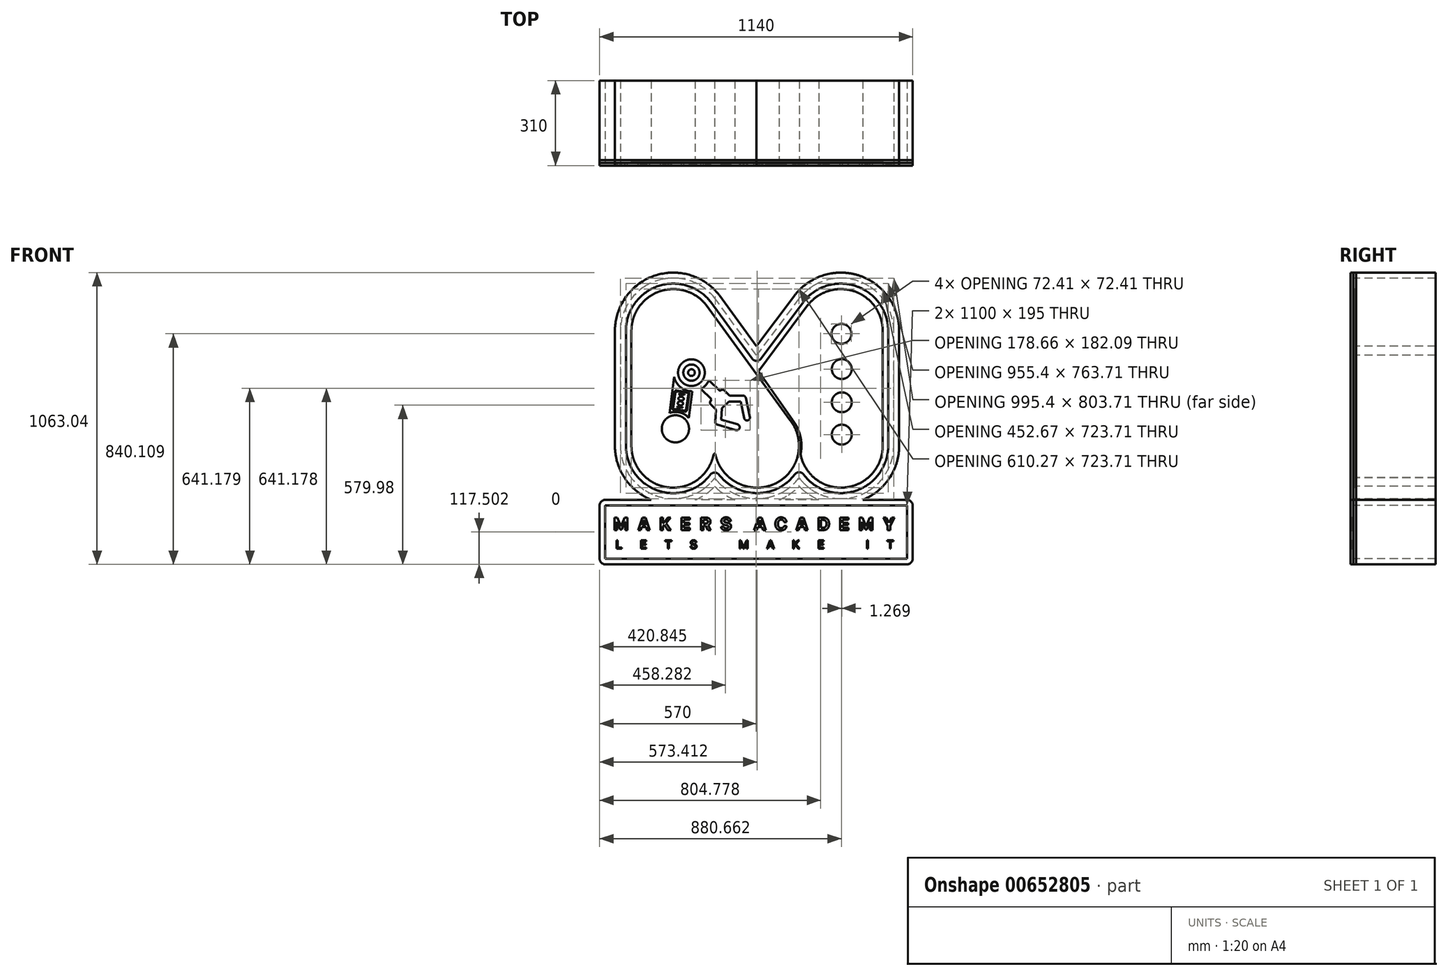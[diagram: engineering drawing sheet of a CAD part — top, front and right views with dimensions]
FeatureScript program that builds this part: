
annotation { "Feature Type Name" : "Feature", "Feature Type Description" : "" }
export const myFeature = defineFeature(function(context is Context, id is Id, definition is map)
    precondition{}
    {
        {
            var Q0;
            Q0=qCreatedBy(makeId("Front.planeOp"),FACE);
            var sketch = newSketch(context, id + "F0", { "sketchPlane" : qUnion([Q0])});
            skLineSegment(sketch, "E0", {"start": v(-550, -511.99) * mm, "end": v(550, -511.99) * mm});
            skLineSegment(sketch, "E1", {"start": v(550, -316.99) * mm, "end": v(-550, -316.99) * mm});
            skLineSegment(sketch, "E2", {"start": v(-550, -316.99) * mm, "end": v(-550, -511.99) * mm});
            skArc(sketch, "E3", {"start": v(-150.98, -217.61) * mm, "mid": v(-142.45, -227.73) * mm, "end": v(-133.24, -237.25) * mm});
            skArc(sketch, "E4", {"start": v(-133.24, -237.25) * mm, "mid": v(-111.33, -255.56) * mm, "end": v(-87, -270.53) * mm});
            skArc(sketch, "E5", {"start": v(-87, -270.53) * mm, "mid": v(-70.2, -278.28) * mm, "end": v(-52.73, -284.43) * mm});
            skArc(sketch, "E6", {"start": v(-52.73, -284.43) * mm, "mid": v(-21.09, -291.12) * mm, "end": v(11.22, -292.51) * mm});
            skArc(sketch, "E7", {"start": v(11.22, -292.51) * mm, "mid": v(24.47, -291.52) * mm, "end": v(37.6, -289.63) * mm});
            skArc(sketch, "E8", {"start": v(37.6, -289.63) * mm, "mid": v(69.6, -280.98) * mm, "end": v(99.62, -266.94) * mm});
            skArc(sketch, "E9", {"start": v(99.62, -266.94) * mm, "mid": v(130.78, -244.53) * mm, "end": v(156.9, -216.4) * mm});
            skArc(sketch, "E10", {"start": v(156.9, -216.4) * mm, "mid": v(166.57, -228.37) * mm, "end": v(177.16, -239.53) * mm});
            skArc(sketch, "E11", {"start": v(177.16, -239.53) * mm, "mid": v(189.2, -250.27) * mm, "end": v(202.1, -259.94) * mm});
            skArc(sketch, "E12", {"start": v(202.1, -259.94) * mm, "mid": v(217.76, -269.57) * mm, "end": v(234.28, -277.6) * mm});
            skArc(sketch, "E13", {"start": v(234.28, -277.6) * mm, "mid": v(256.09, -285.35) * mm, "end": v(278.69, -290.34) * mm});
            skArc(sketch, "E14", {"start": v(278.69, -290.34) * mm, "mid": v(290.19, -291.8) * mm, "end": v(301.76, -292.55) * mm});
            skArc(sketch, "E15", {"start": v(301.76, -292.55) * mm, "mid": v(320.66, -292.3) * mm, "end": v(339.45, -290.2) * mm});
            skArc(sketch, "E16", {"start": v(339.45, -290.2) * mm, "mid": v(373.7, -281.35) * mm, "end": v(405.75, -266.36) * mm});
            skArc(sketch, "E17", {"start": v(405.75, -266.36) * mm, "mid": v(442.26, -238.68) * mm, "end": v(471.22, -203.18) * mm});
            skArc(sketch, "E18", {"start": v(471.22, -203.18) * mm, "mid": v(481.3, -185.26) * mm, "end": v(489.4, -166.37) * mm});
            skArc(sketch, "E19", {"start": v(489.4, -166.37) * mm, "mid": v(496.56, -141.9) * mm, "end": v(500.4, -116.68) * mm});
            skArc(sketch, "E20", {"start": v(500.4, -116.68) * mm, "mid": v(500.94, -108.4) * mm, "end": v(501.11, -100.1) * mm});
            skLineSegment(sketch, "E21", {"start": v(501.11, -100.1) * mm, "end": v(501.11, 318.47) * mm});
            skArc(sketch, "E22", {"start": v(501.11, 318.47) * mm, "mid": v(499.96, 339.69) * mm, "end": v(496.47, 360.65) * mm});
            skArc(sketch, "E23", {"start": v(496.47, 360.65) * mm, "mid": v(485.62, 394.26) * mm, "end": v(468.78, 425.3) * mm});
            skArc(sketch, "E24", {"start": v(468.78, 425.3) * mm, "mid": v(442.9, 456.44) * mm, "end": v(411.1, 481.5) * mm});
            skArc(sketch, "E25", {"start": v(411.1, 481.5) * mm, "mid": v(392.87, 491.64) * mm, "end": v(373.66, 499.74) * mm});
            skArc(sketch, "E26", {"start": v(373.66, 499.74) * mm, "mid": v(349.05, 506.77) * mm, "end": v(323.73, 510.45) * mm});
            skArc(sketch, "E27", {"start": v(323.73, 510.45) * mm, "mid": v(304.95, 511.01) * mm, "end": v(286.2, 509.76) * mm});
            skArc(sketch, "E28", {"start": v(286.2, 509.76) * mm, "mid": v(254.68, 503.4) * mm, "end": v(224.66, 491.85) * mm});
            skArc(sketch, "E29", {"start": v(224.66, 491.85) * mm, "mid": v(210.68, 484.35) * mm, "end": v(197.37, 475.72) * mm});
            skArc(sketch, "E30", {"start": v(197.37, 475.72) * mm, "mid": v(175.68, 457.87) * mm, "end": v(156.81, 437.06) * mm});
            skArc(sketch, "E31", {"start": v(156.81, 437.06) * mm, "mid": v(156.59, 436.76) * mm, "end": v(156.36, 436.46) * mm});
            skLineSegment(sketch, "E32", {"start": v(156.36, 436.46) * mm, "end": v(1.38, 229.45) * mm});
            skLineSegment(sketch, "E33", {"start": v(1.38, 229.45) * mm, "end": v(-149.24, 436.06) * mm});
            skArc(sketch, "E34", {"start": v(-149.24, 436.06) * mm, "mid": v(-149.74, 436.73) * mm, "end": v(-150.26, 437.4) * mm});
            skArc(sketch, "E35", {"start": v(-150.26, 437.4) * mm, "mid": v(-178.98, 466.86) * mm, "end": v(-213.3, 489.58) * mm});
            skArc(sketch, "E36", {"start": v(-213.3, 489.58) * mm, "mid": v(-246.8, 503.08) * mm, "end": v(-282.23, 510.07) * mm});
            skArc(sketch, "E37", {"start": v(-282.23, 510.07) * mm, "mid": v(-298.43, 511.02) * mm, "end": v(-314.65, 510.62) * mm});
            skArc(sketch, "E38", {"start": v(-314.65, 510.62) * mm, "mid": v(-327.45, 509.34) * mm, "end": v(-340.13, 507.2) * mm});
            skArc(sketch, "E39", {"start": v(-340.13, 507.2) * mm, "mid": v(-372.24, 497.7) * mm, "end": v(-402.22, 482.77) * mm});
            skArc(sketch, "E40", {"start": v(-402.22, 482.77) * mm, "mid": v(-441.08, 451.38) * mm, "end": v(-470.6, 411.07) * mm});
            skArc(sketch, "E41", {"start": v(-470.6, 411.07) * mm, "mid": v(-486.12, 374.1) * mm, "end": v(-493.61, 334.71) * mm});
            skArc(sketch, "E42", {"start": v(-493.61, 334.71) * mm, "mid": v(-494.12, 326.6) * mm, "end": v(-494.29, 318.47) * mm});
            skLineSegment(sketch, "E43", {"start": v(-494.29, 318.47) * mm, "end": v(-494.29, -100.1) * mm});
            skArc(sketch, "E44", {"start": v(-494.29, -100.1) * mm, "mid": v(-493.13, -121.3) * mm, "end": v(-489.65, -142.27) * mm});
            skArc(sketch, "E45", {"start": v(-489.65, -142.27) * mm, "mid": v(-478.8, -175.88) * mm, "end": v(-461.96, -206.93) * mm});
            skArc(sketch, "E46", {"start": v(-461.96, -206.93) * mm, "mid": v(-436.07, -238.06) * mm, "end": v(-404.27, -263.12) * mm});
            skArc(sketch, "E47", {"start": v(-404.27, -263.12) * mm, "mid": v(-385.92, -273.32) * mm, "end": v(-366.57, -281.46) * mm});
            skArc(sketch, "E48", {"start": v(-366.57, -281.46) * mm, "mid": v(-342.63, -288.3) * mm, "end": v(-318, -291.98) * mm});
            skArc(sketch, "E49", {"start": v(-318, -291.98) * mm, "mid": v(-299.59, -292.66) * mm, "end": v(-281.2, -291.58) * mm});
            skArc(sketch, "E50", {"start": v(-281.2, -291.58) * mm, "mid": v(-269.11, -289.9) * mm, "end": v(-257.17, -287.43) * mm});
            skArc(sketch, "E51", {"start": v(-257.17, -287.43) * mm, "mid": v(-222.65, -275.47) * mm, "end": v(-191.12, -257.01) * mm});
            skArc(sketch, "E52", {"start": v(-191.12, -257.01) * mm, "mid": v(-176.56, -245.31) * mm, "end": v(-163.22, -232.23) * mm});
            skArc(sketch, "E53", {"start": v(-163.22, -232.23) * mm, "mid": v(-156.92, -225.08) * mm, "end": v(-150.98, -217.61) * mm});
            skArc(sketch, "E54", {"start": v(83.64, -296.99) * mm, "mid": v(101.14, -288.9) * mm, "end": v(117.83, -279.27) * mm});
            skArc(sketch, "E55", {"start": v(117.83, -279.27) * mm, "mid": v(138.24, -264.44) * mm, "end": v(156.76, -247.31) * mm});
            skArc(sketch, "E56", {"start": v(156.76, -247.31) * mm, "mid": v(161.27, -251.95) * mm, "end": v(165.93, -256.46) * mm});
            skLineSegment(sketch, "E57", {"start": v(165.93, -256.46) * mm, "end": v(165.93, -256.46) * mm});
            skArc(sketch, "E58", {"start": v(165.93, -256.46) * mm, "mid": v(179.46, -268.1) * mm, "end": v(193.94, -278.55) * mm});
            skLineSegment(sketch, "E59", {"start": v(193.94, -278.55) * mm, "end": v(193.94, -278.55) * mm});
            skArc(sketch, "E60", {"start": v(193.94, -278.55) * mm, "mid": v(210.92, -288.6) * mm, "end": v(228.79, -296.99) * mm});
            skLineSegment(sketch, "E61", {"start": v(228.79, -296.99) * mm, "end": v(83.64, -296.99) * mm});
            skArc(sketch, "E62", {"start": v(388.77, -296.99) * mm, "mid": v(405.98, -289.06) * mm, "end": v(422.4, -279.62) * mm});
            skArc(sketch, "E63", {"start": v(422.4, -279.62) * mm, "mid": v(461.58, -247.63) * mm, "end": v(492.13, -207.3) * mm});
            skLineSegment(sketch, "E64", {"start": v(492.13, -207.3) * mm, "end": v(492.13, -207.3) * mm});
            skArc(sketch, "E65", {"start": v(492.13, -207.3) * mm, "mid": v(502.9, -186.3) * mm, "end": v(511.25, -164.23) * mm});
            skLineSegment(sketch, "E66", {"start": v(511.25, -164.23) * mm, "end": v(511.25, -164.22) * mm});
            skArc(sketch, "E67", {"start": v(511.25, -164.22) * mm, "mid": v(517.15, -141.08) * mm, "end": v(520.41, -117.42) * mm});
            skArc(sketch, "E68", {"start": v(520.41, -117.42) * mm, "mid": v(520.94, -108.76) * mm, "end": v(521.11, -100.09) * mm});
            skLineSegment(sketch, "E69", {"start": v(521.11, -100.09) * mm, "end": v(521.11, 318.46) * mm});
            skArc(sketch, "E70", {"start": v(521.11, 318.46) * mm, "mid": v(519.73, 342.83) * mm, "end": v(515.56, 366.88) * mm});
            skLineSegment(sketch, "E71", {"start": v(515.56, 366.88) * mm, "end": v(515.56, 366.89) * mm});
            skArc(sketch, "E72", {"start": v(515.56, 366.89) * mm, "mid": v(503.43, 403.45) * mm, "end": v(484.88, 437.2) * mm});
            skArc(sketch, "E73", {"start": v(484.88, 437.2) * mm, "mid": v(453.73, 473.74) * mm, "end": v(415.2, 502.38) * mm});
            skLineSegment(sketch, "E74", {"start": v(415.2, 502.38) * mm, "end": v(415.2, 502.38) * mm});
            skArc(sketch, "E75", {"start": v(415.2, 502.38) * mm, "mid": v(393.81, 513.23) * mm, "end": v(371.34, 521.6) * mm});
            skLineSegment(sketch, "E76", {"start": v(371.34, 521.6) * mm, "end": v(371.34, 521.6) * mm});
            skArc(sketch, "E77", {"start": v(371.34, 521.6) * mm, "mid": v(348.09, 527.36) * mm, "end": v(324.33, 530.46) * mm});
            skArc(sketch, "E78", {"start": v(324.33, 530.46) * mm, "mid": v(301.23, 530.92) * mm, "end": v(278.2, 528.89) * mm});
            skLineSegment(sketch, "E79", {"start": v(278.2, 528.89) * mm, "end": v(278.2, 528.89) * mm});
            skArc(sketch, "E80", {"start": v(278.2, 528.89) * mm, "mid": v(236, 518.32) * mm, "end": v(196.86, 499.36) * mm});
            skLineSegment(sketch, "E81", {"start": v(196.86, 499.36) * mm, "end": v(196.86, 499.36) * mm});
            skArc(sketch, "E82", {"start": v(196.86, 499.36) * mm, "mid": v(180.99, 488.53) * mm, "end": v(166.16, 476.3) * mm});
            skArc(sketch, "E83", {"start": v(166.16, 476.3) * mm, "mid": v(153.03, 463.39) * mm, "end": v(141.06, 449.38) * mm});
            skArc(sketch, "E84", {"start": v(141.06, 449.38) * mm, "mid": v(141.04, 449.35) * mm, "end": v(141.02, 449.33) * mm});
            skArc(sketch, "E85", {"start": v(141.02, 449.33) * mm, "mid": v(140.68, 448.9) * mm, "end": v(140.35, 448.45) * mm});
            skLineSegment(sketch, "E86", {"start": v(140.35, 448.45) * mm, "end": v(140.35, 448.45) * mm});
            skLineSegment(sketch, "E87", {"start": v(140.35, 448.45) * mm, "end": v(1.6, 263.1) * mm});
            skLineSegment(sketch, "E88", {"start": v(1.6, 263.1) * mm, "end": v(-133.08, 447.84) * mm});
            skLineSegment(sketch, "E89", {"start": v(-133.08, 447.84) * mm, "end": v(-133.09, 447.85) * mm});
            skArc(sketch, "E90", {"start": v(-133.09, 447.85) * mm, "mid": v(-133.81, 448.83) * mm, "end": v(-134.55, 449.78) * mm});
            skArc(sketch, "E91", {"start": v(-134.55, 449.78) * mm, "mid": v(-166.62, 482.59) * mm, "end": v(-204.95, 507.78) * mm});
            skLineSegment(sketch, "E92", {"start": v(-204.95, 507.78) * mm, "end": v(-204.96, 507.78) * mm});
            skArc(sketch, "E93", {"start": v(-204.96, 507.78) * mm, "mid": v(-242.95, 522.8) * mm, "end": v(-283.12, 530.24) * mm});
            skArc(sketch, "E94", {"start": v(-283.12, 530.24) * mm, "mid": v(-305.69, 531) * mm, "end": v(-328.22, 529.4) * mm});
            skLineSegment(sketch, "E95", {"start": v(-328.22, 529.4) * mm, "end": v(-328.22, 529.4) * mm});
            skArc(sketch, "E96", {"start": v(-328.22, 529.4) * mm, "mid": v(-372.48, 518.96) * mm, "end": v(-413.49, 499.32) * mm});
            skArc(sketch, "E97", {"start": v(-413.49, 499.32) * mm, "mid": v(-456.54, 464.14) * mm, "end": v(-489.04, 419.02) * mm});
            skLineSegment(sketch, "E98", {"start": v(-489.04, 419.02) * mm, "end": v(-489.04, 419.02) * mm});
            skArc(sketch, "E99", {"start": v(-489.04, 419.02) * mm, "mid": v(-505.68, 378.5) * mm, "end": v(-513.62, 335.44) * mm});
            skArc(sketch, "E100", {"start": v(-513.62, 335.44) * mm, "mid": v(-514.12, 326.96) * mm, "end": v(-514.29, 318.47) * mm});
            skLineSegment(sketch, "E101", {"start": v(-514.29, 318.47) * mm, "end": v(-514.29, -100.08) * mm});
            skArc(sketch, "E102", {"start": v(-514.29, -100.08) * mm, "mid": v(-512.9, -124.45) * mm, "end": v(-508.74, -148.5) * mm});
            skLineSegment(sketch, "E103", {"start": v(-508.74, -148.5) * mm, "end": v(-508.74, -148.5) * mm});
            skArc(sketch, "E104", {"start": v(-508.74, -148.5) * mm, "mid": v(-496.6, -185.07) * mm, "end": v(-478.06, -218.83) * mm});
            skArc(sketch, "E105", {"start": v(-478.06, -218.83) * mm, "mid": v(-446.89, -255.38) * mm, "end": v(-408.33, -284.03) * mm});
            skLineSegment(sketch, "E106", {"start": v(-408.33, -284.03) * mm, "end": v(-408.33, -284.03) * mm});
            skArc(sketch, "E107", {"start": v(-408.33, -284.03) * mm, "mid": v(-395.36, -290.97) * mm, "end": v(-381.95, -296.99) * mm});
            skLineSegment(sketch, "E108", {"start": v(-381.95, -296.99) * mm, "end": v(-550, -296.99) * mm});
            skArc(sketch, "E109", {"start": v(-550, -296.99) * mm, "mid": v(-564.14, -302.85) * mm, "end": v(-570, -316.99) * mm});
            skLineSegment(sketch, "E110", {"start": v(-570, -316.99) * mm, "end": v(-570, -511.99) * mm});
            skArc(sketch, "E111", {"start": v(-570, -511.99) * mm, "mid": v(-564.14, -526.13) * mm, "end": v(-550, -531.99) * mm});
            skLineSegment(sketch, "E112", {"start": v(-550, -531.99) * mm, "end": v(550, -531.99) * mm});
            skArc(sketch, "E113", {"start": v(550, -531.99) * mm, "mid": v(564.14, -526.13) * mm, "end": v(570, -511.99) * mm});
            skLineSegment(sketch, "E114", {"start": v(570, -511.99) * mm, "end": v(570, -316.99) * mm});
            skArc(sketch, "E115", {"start": v(570, -316.99) * mm, "mid": v(564.14, -302.85) * mm, "end": v(550, -296.99) * mm});
            skLineSegment(sketch, "E116", {"start": v(550, -296.99) * mm, "end": v(388.77, -296.99) * mm});
            skArc(sketch, "E117", {"start": v(-221.97, -296.99) * mm, "mid": v(-198.71, -285.65) * mm, "end": v(-177.06, -271.5) * mm});
            skArc(sketch, "E118", {"start": v(-177.06, -271.5) * mm, "mid": v(-163.39, -260.36) * mm, "end": v(-150.7, -248.12) * mm});
            skArc(sketch, "E119", {"start": v(-150.7, -248.12) * mm, "mid": v(-147.2, -251.58) * mm, "end": v(-143.63, -254.95) * mm});
            skArc(sketch, "E120", {"start": v(-143.63, -254.95) * mm, "mid": v(-119.45, -274.3) * mm, "end": v(-92.77, -290.03) * mm});
            skArc(sketch, "E121", {"start": v(-92.77, -290.03) * mm, "mid": v(-85.1, -293.66) * mm, "end": v(-77.29, -296.99) * mm});
            skLineSegment(sketch, "E122", {"start": v(-77.29, -296.99) * mm, "end": v(-221.97, -296.99) * mm});
            skArc(sketch, "E123", {"start": v(-135.27, -205.24) * mm, "mid": v(-151.18, -197.61) * mm, "end": v(-166.94, -205.56) * mm});
            skArc(sketch, "E124", {"start": v(-166.94, -205.56) * mm, "mid": v(-172.01, -211.94) * mm, "end": v(-177.38, -218.08) * mm});
            skLineSegment(sketch, "E125", {"start": v(-177.38, -218.08) * mm, "end": v(-177.38, -218.09) * mm});
            skArc(sketch, "E126", {"start": v(-177.38, -218.09) * mm, "mid": v(-188.68, -229.32) * mm, "end": v(-200.99, -239.44) * mm});
            skLineSegment(sketch, "E127", {"start": v(-200.99, -239.44) * mm, "end": v(-201, -239.44) * mm});
            skArc(sketch, "E128", {"start": v(-201, -239.44) * mm, "mid": v(-227.9, -255.83) * mm, "end": v(-257.4, -266.85) * mm});
            skArc(sketch, "E129", {"start": v(-257.4, -266.85) * mm, "mid": v(-269.15, -269.57) * mm, "end": v(-281.07, -271.43) * mm});
            skArc(sketch, "E130", {"start": v(-281.07, -271.43) * mm, "mid": v(-298.29, -272.63) * mm, "end": v(-315.54, -272.12) * mm});
            skLineSegment(sketch, "E131", {"start": v(-315.54, -272.12) * mm, "end": v(-315.56, -272.12) * mm});
            skArc(sketch, "E132", {"start": v(-315.56, -272.12) * mm, "mid": v(-334.18, -269.61) * mm, "end": v(-352.42, -265.1) * mm});
            skArc(sketch, "E133", {"start": v(-352.42, -265.1) * mm, "mid": v(-370.78, -258.29) * mm, "end": v(-388.24, -249.44) * mm});
            skArc(sketch, "E134", {"start": v(-388.24, -249.44) * mm, "mid": v(-419.57, -226.16) * mm, "end": v(-444.9, -196.47) * mm});
            skLineSegment(sketch, "E135", {"start": v(-444.9, -196.47) * mm, "end": v(-444.9, -196.46) * mm});
            skArc(sketch, "E136", {"start": v(-444.9, -196.46) * mm, "mid": v(-459.94, -169.08) * mm, "end": v(-469.78, -139.42) * mm});
            skArc(sketch, "E137", {"start": v(-469.78, -139.42) * mm, "mid": v(-473.17, -119.9) * mm, "end": v(-474.29, -100.1) * mm});
            skLineSegment(sketch, "E138", {"start": v(-474.29, -100.1) * mm, "end": v(-474.29, -100.1) * mm});
            skLineSegment(sketch, "E139", {"start": v(-474.29, -100.1) * mm, "end": v(-474.29, 318.47) * mm});
            skLineSegment(sketch, "E140", {"start": v(-474.29, 318.47) * mm, "end": v(-474.29, 318.48) * mm});
            skArc(sketch, "E141", {"start": v(-474.29, 318.48) * mm, "mid": v(-474.15, 325.38) * mm, "end": v(-473.75, 332.28) * mm});
            skLineSegment(sketch, "E142", {"start": v(-473.75, 332.28) * mm, "end": v(-473.74, 332.29) * mm});
            skArc(sketch, "E143", {"start": v(-473.74, 332.29) * mm, "mid": v(-467.3, 367.22) * mm, "end": v(-453.81, 400.08) * mm});
            skArc(sketch, "E144", {"start": v(-453.81, 400.08) * mm, "mid": v(-427.4, 436.73) * mm, "end": v(-392.43, 465.3) * mm});
            skLineSegment(sketch, "E145", {"start": v(-392.43, 465.3) * mm, "end": v(-392.43, 465.3) * mm});
            skArc(sketch, "E146", {"start": v(-392.43, 465.3) * mm, "mid": v(-359.17, 481.24) * mm, "end": v(-323.27, 489.7) * mm});
            skArc(sketch, "E147", {"start": v(-323.27, 489.7) * mm, "mid": v(-304.95, 491.02) * mm, "end": v(-286.58, 490.39) * mm});
            skLineSegment(sketch, "E148", {"start": v(-286.58, 490.39) * mm, "end": v(-286.58, 490.39) * mm});
            skArc(sketch, "E149", {"start": v(-286.58, 490.39) * mm, "mid": v(-254, 484.35) * mm, "end": v(-223.19, 472.17) * mm});
            skArc(sketch, "E150", {"start": v(-223.19, 472.17) * mm, "mid": v(-192.03, 451.7) * mm, "end": v(-165.98, 425.04) * mm});
            skArc(sketch, "E151", {"start": v(-165.98, 425.04) * mm, "mid": v(-165.96, 425) * mm, "end": v(-165.93, 424.97) * mm});
            skArc(sketch, "E152", {"start": v(-165.93, 424.97) * mm, "mid": v(-165.66, 424.62) * mm, "end": v(-165.4, 424.27) * mm});
            skLineSegment(sketch, "E153", {"start": v(-165.4, 424.27) * mm, "end": v(-14.78, 217.67) * mm});
            skArc(sketch, "E154", {"start": v(-14.78, 217.67) * mm, "mid": v(1.25, 209.45) * mm, "end": v(17.4, 217.46) * mm});
            skLineSegment(sketch, "E155", {"start": v(17.4, 217.46) * mm, "end": v(172.37, 424.47) * mm});
            skArc(sketch, "E156", {"start": v(172.37, 424.47) * mm, "mid": v(172.48, 424.62) * mm, "end": v(172.59, 424.76) * mm});
            skArc(sketch, "E157", {"start": v(172.59, 424.76) * mm, "mid": v(182.3, 436.13) * mm, "end": v(192.96, 446.61) * mm});
            skArc(sketch, "E158", {"start": v(192.96, 446.61) * mm, "mid": v(205, 456.54) * mm, "end": v(217.9, 465.34) * mm});
            skArc(sketch, "E159", {"start": v(217.9, 465.34) * mm, "mid": v(249.65, 480.72) * mm, "end": v(283.87, 489.3) * mm});
            skArc(sketch, "E160", {"start": v(283.87, 489.3) * mm, "mid": v(302.6, 490.94) * mm, "end": v(321.39, 490.57) * mm});
            skLineSegment(sketch, "E161", {"start": v(321.39, 490.57) * mm, "end": v(321.4, 490.57) * mm});
            skArc(sketch, "E162", {"start": v(321.4, 490.57) * mm, "mid": v(340.67, 488.05) * mm, "end": v(359.54, 483.38) * mm});
            skArc(sketch, "E163", {"start": v(359.54, 483.38) * mm, "mid": v(377.76, 476.6) * mm, "end": v(395.1, 467.8) * mm});
            skArc(sketch, "E164", {"start": v(395.1, 467.8) * mm, "mid": v(426.4, 444.53) * mm, "end": v(451.71, 414.85) * mm});
            skLineSegment(sketch, "E165", {"start": v(451.71, 414.85) * mm, "end": v(451.72, 414.84) * mm});
            skArc(sketch, "E166", {"start": v(451.72, 414.84) * mm, "mid": v(466.77, 387.46) * mm, "end": v(476.6, 357.8) * mm});
            skArc(sketch, "E167", {"start": v(476.6, 357.8) * mm, "mid": v(479.99, 338.27) * mm, "end": v(481.11, 318.48) * mm});
            skLineSegment(sketch, "E168", {"start": v(481.11, 318.48) * mm, "end": v(481.11, 318.47) * mm});
            skLineSegment(sketch, "E169", {"start": v(481.11, 318.47) * mm, "end": v(481.11, -100.1) * mm});
            skLineSegment(sketch, "E170", {"start": v(481.11, -100.1) * mm, "end": v(481.11, -100.1) * mm});
            skArc(sketch, "E171", {"start": v(481.11, -100.1) * mm, "mid": v(480.97, -107.15) * mm, "end": v(480.55, -114.2) * mm});
            skLineSegment(sketch, "E172", {"start": v(480.55, -114.2) * mm, "end": v(480.54, -114.2) * mm});
            skArc(sketch, "E173", {"start": v(480.54, -114.2) * mm, "mid": v(477.9, -133.4) * mm, "end": v(473.11, -152.17) * mm});
            skArc(sketch, "E174", {"start": v(473.11, -152.17) * mm, "mid": v(466.33, -170.07) * mm, "end": v(457.6, -187.1) * mm});
            skArc(sketch, "E175", {"start": v(457.6, -187.1) * mm, "mid": v(432.79, -219.87) * mm, "end": v(400.96, -245.86) * mm});
            skLineSegment(sketch, "E176", {"start": v(400.96, -245.86) * mm, "end": v(400.95, -245.86) * mm});
            skArc(sketch, "E177", {"start": v(400.95, -245.86) * mm, "mid": v(370.95, -261.03) * mm, "end": v(338.57, -270.06) * mm});
            skArc(sketch, "E178", {"start": v(338.57, -270.06) * mm, "mid": v(320.97, -272.23) * mm, "end": v(303.25, -272.59) * mm});
            skLineSegment(sketch, "E179", {"start": v(303.25, -272.59) * mm, "end": v(303.24, -272.59) * mm});
            skArc(sketch, "E180", {"start": v(303.24, -272.59) * mm, "mid": v(293.25, -272) * mm, "end": v(283.3, -270.82) * mm});
            skLineSegment(sketch, "E181", {"start": v(283.3, -270.82) * mm, "end": v(283.3, -270.82) * mm});
            skArc(sketch, "E182", {"start": v(283.3, -270.82) * mm, "mid": v(264.93, -267.04) * mm, "end": v(247.09, -261.23) * mm});
            skArc(sketch, "E183", {"start": v(247.09, -261.23) * mm, "mid": v(231.09, -254) * mm, "end": v(215.94, -245.14) * mm});
            skArc(sketch, "E184", {"start": v(215.94, -245.14) * mm, "mid": v(204.23, -236.7) * mm, "end": v(193.3, -227.28) * mm});
            skArc(sketch, "E185", {"start": v(193.3, -227.28) * mm, "mid": v(182.62, -216.33) * mm, "end": v(172.95, -204.47) * mm});
            skArc(sketch, "E186", {"start": v(172.95, -204.47) * mm, "mid": v(157, -196.4) * mm, "end": v(140.97, -204.32) * mm});
            skArc(sketch, "E187", {"start": v(140.97, -204.32) * mm, "mid": v(120.45, -226.92) * mm, "end": v(96.28, -245.57) * mm});
            skLineSegment(sketch, "E188", {"start": v(96.28, -245.57) * mm, "end": v(96.27, -245.57) * mm});
            skArc(sketch, "E189", {"start": v(96.27, -245.57) * mm, "mid": v(68.18, -260.1) * mm, "end": v(37.9, -269.21) * mm});
            skArc(sketch, "E190", {"start": v(37.9, -269.21) * mm, "mid": v(26.9, -271.08) * mm, "end": v(15.8, -272.23) * mm});
            skArc(sketch, "E191", {"start": v(15.8, -272.23) * mm, "mid": v(-14.35, -271.77) * mm, "end": v(-43.98, -266.15) * mm});
            skArc(sketch, "E192", {"start": v(-43.98, -266.15) * mm, "mid": v(-59.75, -260.9) * mm, "end": v(-74.96, -254.21) * mm});
            skLineSegment(sketch, "E193", {"start": v(-74.96, -254.21) * mm, "end": v(-74.96, -254.21) * mm});
            skArc(sketch, "E194", {"start": v(-74.96, -254.21) * mm, "mid": v(-96.74, -241.38) * mm, "end": v(-116.48, -225.58) * mm});
            skLineSegment(sketch, "E195", {"start": v(-116.48, -225.58) * mm, "end": v(-116.48, -225.58) * mm});
            skArc(sketch, "E196", {"start": v(-116.48, -225.58) * mm, "mid": v(-126.28, -215.78) * mm, "end": v(-135.27, -205.24) * mm});
            skLineSegment(sketch, "E197", {"start": v(-530, -491.99) * mm, "end": v(-530, -336.99) * mm});
            skLineSegment(sketch, "E198", {"start": v(-530, -336.99) * mm, "end": v(530, -336.99) * mm});
            skLineSegment(sketch, "E199", {"start": v(530, -336.99) * mm, "end": v(530, -491.99) * mm});
            skLineSegment(sketch, "E200", {"start": v(530, -491.99) * mm, "end": v(-530, -491.99) * mm});
            skLineSegment(sketch, "E201", {"start": v(311.93, 143.37) * mm, "end": v(311, 143.38) * mm});
            skLineSegment(sketch, "E202", {"start": v(311, 143.38) * mm, "end": v(310.07, 143.42) * mm});
            skLineSegment(sketch, "E203", {"start": v(310.07, 143.42) * mm, "end": v(309.15, 143.47) * mm});
            skLineSegment(sketch, "E204", {"start": v(309.15, 143.47) * mm, "end": v(308.23, 143.56) * mm});
            skLineSegment(sketch, "E205", {"start": v(308.23, 143.56) * mm, "end": v(307.32, 143.66) * mm});
            skLineSegment(sketch, "E206", {"start": v(307.32, 143.66) * mm, "end": v(306.42, 143.79) * mm});
            skLineSegment(sketch, "E207", {"start": v(306.42, 143.79) * mm, "end": v(305.52, 143.93) * mm});
            skLineSegment(sketch, "E208", {"start": v(305.52, 143.93) * mm, "end": v(304.63, 144.1) * mm});
            skLineSegment(sketch, "E209", {"start": v(304.63, 144.1) * mm, "end": v(303.75, 144.3) * mm});
            skLineSegment(sketch, "E210", {"start": v(303.75, 144.3) * mm, "end": v(302.88, 144.5) * mm});
            skLineSegment(sketch, "E211", {"start": v(302.88, 144.5) * mm, "end": v(302.02, 144.74) * mm});
            skLineSegment(sketch, "E212", {"start": v(302.02, 144.74) * mm, "end": v(301.17, 145) * mm});
            skLineSegment(sketch, "E213", {"start": v(301.17, 145) * mm, "end": v(300.32, 145.27) * mm});
            skLineSegment(sketch, "E214", {"start": v(300.32, 145.27) * mm, "end": v(299.48, 145.57) * mm});
            skLineSegment(sketch, "E215", {"start": v(299.48, 145.57) * mm, "end": v(298.66, 145.88) * mm});
            skLineSegment(sketch, "E216", {"start": v(298.66, 145.88) * mm, "end": v(297.84, 146.21) * mm});
            skLineSegment(sketch, "E217", {"start": v(297.84, 146.21) * mm, "end": v(297.03, 146.57) * mm});
            skLineSegment(sketch, "E218", {"start": v(297.03, 146.57) * mm, "end": v(296.23, 146.94) * mm});
            skLineSegment(sketch, "E219", {"start": v(296.23, 146.94) * mm, "end": v(295.45, 147.33) * mm});
            skLineSegment(sketch, "E220", {"start": v(295.45, 147.33) * mm, "end": v(294.67, 147.74) * mm});
            skLineSegment(sketch, "E221", {"start": v(294.67, 147.74) * mm, "end": v(293.9, 148.17) * mm});
            skLineSegment(sketch, "E222", {"start": v(293.9, 148.17) * mm, "end": v(293.16, 148.6) * mm});
            skLineSegment(sketch, "E223", {"start": v(293.16, 148.6) * mm, "end": v(292.42, 149.07) * mm});
            skLineSegment(sketch, "E224", {"start": v(292.42, 149.07) * mm, "end": v(291.69, 149.55) * mm});
            skLineSegment(sketch, "E225", {"start": v(291.69, 149.55) * mm, "end": v(290.97, 150.05) * mm});
            skLineSegment(sketch, "E226", {"start": v(290.97, 150.05) * mm, "end": v(290.27, 150.56) * mm});
            skLineSegment(sketch, "E227", {"start": v(290.27, 150.56) * mm, "end": v(289.58, 151.1) * mm});
            skLineSegment(sketch, "E228", {"start": v(289.58, 151.1) * mm, "end": v(288.9, 151.64) * mm});
            skLineSegment(sketch, "E229", {"start": v(288.9, 151.64) * mm, "end": v(288.24, 152.2) * mm});
            skLineSegment(sketch, "E230", {"start": v(288.24, 152.2) * mm, "end": v(287.59, 152.77) * mm});
            skLineSegment(sketch, "E231", {"start": v(287.59, 152.77) * mm, "end": v(286.95, 153.37) * mm});
            skLineSegment(sketch, "E232", {"start": v(286.95, 153.37) * mm, "end": v(286.33, 153.97) * mm});
            skLineSegment(sketch, "E233", {"start": v(286.33, 153.97) * mm, "end": v(285.72, 154.6) * mm});
            skLineSegment(sketch, "E234", {"start": v(285.72, 154.6) * mm, "end": v(285.13, 155.23) * mm});
            skLineSegment(sketch, "E235", {"start": v(285.13, 155.23) * mm, "end": v(284.55, 155.88) * mm});
            skLineSegment(sketch, "E236", {"start": v(284.55, 155.88) * mm, "end": v(284, 156.54) * mm});
            skLineSegment(sketch, "E237", {"start": v(284, 156.54) * mm, "end": v(283.45, 157.22) * mm});
            skLineSegment(sketch, "E238", {"start": v(283.45, 157.22) * mm, "end": v(282.92, 157.91) * mm});
            skLineSegment(sketch, "E239", {"start": v(282.92, 157.91) * mm, "end": v(282.4, 158.61) * mm});
            skLineSegment(sketch, "E240", {"start": v(282.4, 158.61) * mm, "end": v(281.9, 159.33) * mm});
            skLineSegment(sketch, "E241", {"start": v(281.9, 159.33) * mm, "end": v(281.43, 160.06) * mm});
            skLineSegment(sketch, "E242", {"start": v(281.43, 160.06) * mm, "end": v(280.97, 160.8) * mm});
            skLineSegment(sketch, "E243", {"start": v(280.97, 160.8) * mm, "end": v(280.52, 161.55) * mm});
            skLineSegment(sketch, "E244", {"start": v(280.52, 161.55) * mm, "end": v(280.1, 162.32) * mm});
            skLineSegment(sketch, "E245", {"start": v(280.1, 162.32) * mm, "end": v(279.69, 163.1) * mm});
            skLineSegment(sketch, "E246", {"start": v(279.69, 163.1) * mm, "end": v(279.3, 163.88) * mm});
            skLineSegment(sketch, "E247", {"start": v(279.3, 163.88) * mm, "end": v(278.92, 164.67) * mm});
            skLineSegment(sketch, "E248", {"start": v(278.92, 164.67) * mm, "end": v(278.57, 165.48) * mm});
            skLineSegment(sketch, "E249", {"start": v(278.57, 165.48) * mm, "end": v(278.24, 166.3) * mm});
            skLineSegment(sketch, "E250", {"start": v(278.24, 166.3) * mm, "end": v(277.92, 167.13) * mm});
            skLineSegment(sketch, "E251", {"start": v(277.92, 167.13) * mm, "end": v(277.63, 167.96) * mm});
            skLineSegment(sketch, "E252", {"start": v(277.63, 167.96) * mm, "end": v(277.35, 168.8) * mm});
            skLineSegment(sketch, "E253", {"start": v(277.35, 168.8) * mm, "end": v(277.1, 169.66) * mm});
            skLineSegment(sketch, "E254", {"start": v(277.1, 169.66) * mm, "end": v(276.87, 170.53) * mm});
            skLineSegment(sketch, "E255", {"start": v(276.87, 170.53) * mm, "end": v(276.65, 171.4) * mm});
            skLineSegment(sketch, "E256", {"start": v(276.65, 171.4) * mm, "end": v(276.46, 172.28) * mm});
            skLineSegment(sketch, "E257", {"start": v(276.46, 172.28) * mm, "end": v(276.3, 173.16) * mm});
            skLineSegment(sketch, "E258", {"start": v(276.3, 173.16) * mm, "end": v(276.14, 174.06) * mm});
            skLineSegment(sketch, "E259", {"start": v(276.14, 174.06) * mm, "end": v(276.02, 174.96) * mm});
            skLineSegment(sketch, "E260", {"start": v(276.02, 174.96) * mm, "end": v(275.91, 175.87) * mm});
            skLineSegment(sketch, "E261", {"start": v(275.91, 175.87) * mm, "end": v(275.83, 176.79) * mm});
            skLineSegment(sketch, "E262", {"start": v(275.83, 176.79) * mm, "end": v(275.77, 177.71) * mm});
            skLineSegment(sketch, "E263", {"start": v(275.77, 177.71) * mm, "end": v(275.74, 178.64) * mm});
            skLineSegment(sketch, "E264", {"start": v(275.74, 178.64) * mm, "end": v(275.73, 179.57) * mm});
            skLineSegment(sketch, "E265", {"start": v(275.73, 179.57) * mm, "end": v(275.74, 180.5) * mm});
            skLineSegment(sketch, "E266", {"start": v(275.74, 180.5) * mm, "end": v(275.77, 181.44) * mm});
            skLineSegment(sketch, "E267", {"start": v(275.77, 181.44) * mm, "end": v(275.83, 182.36) * mm});
            skLineSegment(sketch, "E268", {"start": v(275.83, 182.36) * mm, "end": v(275.91, 183.28) * mm});
            skLineSegment(sketch, "E269", {"start": v(275.91, 183.28) * mm, "end": v(276.02, 184.19) * mm});
            skLineSegment(sketch, "E270", {"start": v(276.02, 184.19) * mm, "end": v(276.14, 185.09) * mm});
            skLineSegment(sketch, "E271", {"start": v(276.14, 185.09) * mm, "end": v(276.3, 185.98) * mm});
            skLineSegment(sketch, "E272", {"start": v(276.3, 185.98) * mm, "end": v(276.46, 186.87) * mm});
            skLineSegment(sketch, "E273", {"start": v(276.46, 186.87) * mm, "end": v(276.65, 187.75) * mm});
            skLineSegment(sketch, "E274", {"start": v(276.65, 187.75) * mm, "end": v(276.87, 188.62) * mm});
            skLineSegment(sketch, "E275", {"start": v(276.87, 188.62) * mm, "end": v(277.1, 189.49) * mm});
            skLineSegment(sketch, "E276", {"start": v(277.1, 189.49) * mm, "end": v(277.35, 190.34) * mm});
            skLineSegment(sketch, "E277", {"start": v(277.35, 190.34) * mm, "end": v(277.63, 191.19) * mm});
            skLineSegment(sketch, "E278", {"start": v(277.63, 191.19) * mm, "end": v(277.92, 192.02) * mm});
            skLineSegment(sketch, "E279", {"start": v(277.92, 192.02) * mm, "end": v(278.24, 192.85) * mm});
            skLineSegment(sketch, "E280", {"start": v(278.24, 192.85) * mm, "end": v(278.57, 193.67) * mm});
            skLineSegment(sketch, "E281", {"start": v(278.57, 193.67) * mm, "end": v(278.92, 194.47) * mm});
            skLineSegment(sketch, "E282", {"start": v(278.92, 194.47) * mm, "end": v(279.3, 195.27) * mm});
            skLineSegment(sketch, "E283", {"start": v(279.3, 195.27) * mm, "end": v(279.69, 196.06) * mm});
            skLineSegment(sketch, "E284", {"start": v(279.69, 196.06) * mm, "end": v(280.1, 196.83) * mm});
            skLineSegment(sketch, "E285", {"start": v(280.1, 196.83) * mm, "end": v(280.52, 197.6) * mm});
            skLineSegment(sketch, "E286", {"start": v(280.52, 197.6) * mm, "end": v(280.97, 198.35) * mm});
            skLineSegment(sketch, "E287", {"start": v(280.97, 198.35) * mm, "end": v(281.43, 199.09) * mm});
            skLineSegment(sketch, "E288", {"start": v(281.43, 199.09) * mm, "end": v(281.9, 199.82) * mm});
            skLineSegment(sketch, "E289", {"start": v(281.9, 199.82) * mm, "end": v(282.4, 200.53) * mm});
            skLineSegment(sketch, "E290", {"start": v(282.4, 200.53) * mm, "end": v(282.92, 201.24) * mm});
            skLineSegment(sketch, "E291", {"start": v(282.92, 201.24) * mm, "end": v(283.45, 201.93) * mm});
            skLineSegment(sketch, "E292", {"start": v(283.45, 201.93) * mm, "end": v(284, 202.6) * mm});
            skLineSegment(sketch, "E293", {"start": v(284, 202.6) * mm, "end": v(284.55, 203.27) * mm});
            skLineSegment(sketch, "E294", {"start": v(284.55, 203.27) * mm, "end": v(285.13, 203.92) * mm});
            skLineSegment(sketch, "E295", {"start": v(285.13, 203.92) * mm, "end": v(285.72, 204.55) * mm});
            skLineSegment(sketch, "E296", {"start": v(285.72, 204.55) * mm, "end": v(286.33, 205.17) * mm});
            skLineSegment(sketch, "E297", {"start": v(286.33, 205.17) * mm, "end": v(286.95, 205.78) * mm});
            skLineSegment(sketch, "E298", {"start": v(286.95, 205.78) * mm, "end": v(287.59, 206.37) * mm});
            skLineSegment(sketch, "E299", {"start": v(287.59, 206.37) * mm, "end": v(288.24, 206.95) * mm});
            skLineSegment(sketch, "E300", {"start": v(288.24, 206.95) * mm, "end": v(288.9, 207.51) * mm});
            skLineSegment(sketch, "E301", {"start": v(288.9, 207.51) * mm, "end": v(289.58, 208.06) * mm});
            skLineSegment(sketch, "E302", {"start": v(289.58, 208.06) * mm, "end": v(290.27, 208.59) * mm});
            skLineSegment(sketch, "E303", {"start": v(290.27, 208.59) * mm, "end": v(290.97, 209.1) * mm});
            skLineSegment(sketch, "E304", {"start": v(290.97, 209.1) * mm, "end": v(291.69, 209.6) * mm});
            skLineSegment(sketch, "E305", {"start": v(291.69, 209.6) * mm, "end": v(292.42, 210.08) * mm});
            skLineSegment(sketch, "E306", {"start": v(292.42, 210.08) * mm, "end": v(293.16, 210.54) * mm});
            skLineSegment(sketch, "E307", {"start": v(293.16, 210.54) * mm, "end": v(293.9, 210.98) * mm});
            skLineSegment(sketch, "E308", {"start": v(293.9, 210.98) * mm, "end": v(294.67, 211.4) * mm});
            skLineSegment(sketch, "E309", {"start": v(294.67, 211.4) * mm, "end": v(295.45, 211.82) * mm});
            skLineSegment(sketch, "E310", {"start": v(295.45, 211.82) * mm, "end": v(296.23, 212.2) * mm});
            skLineSegment(sketch, "E311", {"start": v(296.23, 212.2) * mm, "end": v(297.03, 212.58) * mm});
            skLineSegment(sketch, "E312", {"start": v(297.03, 212.58) * mm, "end": v(297.84, 212.93) * mm});
            skLineSegment(sketch, "E313", {"start": v(297.84, 212.93) * mm, "end": v(298.66, 213.27) * mm});
            skLineSegment(sketch, "E314", {"start": v(298.66, 213.27) * mm, "end": v(299.48, 213.58) * mm});
            skLineSegment(sketch, "E315", {"start": v(299.48, 213.58) * mm, "end": v(300.32, 213.88) * mm});
            skLineSegment(sketch, "E316", {"start": v(300.32, 213.88) * mm, "end": v(301.17, 214.15) * mm});
            skLineSegment(sketch, "E317", {"start": v(301.17, 214.15) * mm, "end": v(302.02, 214.4) * mm});
            skLineSegment(sketch, "E318", {"start": v(302.02, 214.4) * mm, "end": v(302.88, 214.64) * mm});
            skLineSegment(sketch, "E319", {"start": v(302.88, 214.64) * mm, "end": v(303.75, 214.85) * mm});
            skLineSegment(sketch, "E320", {"start": v(303.75, 214.85) * mm, "end": v(304.63, 215.04) * mm});
            skLineSegment(sketch, "E321", {"start": v(304.63, 215.04) * mm, "end": v(305.52, 215.21) * mm});
            skLineSegment(sketch, "E322", {"start": v(305.52, 215.21) * mm, "end": v(306.42, 215.36) * mm});
            skLineSegment(sketch, "E323", {"start": v(306.42, 215.36) * mm, "end": v(307.32, 215.49) * mm});
            skLineSegment(sketch, "E324", {"start": v(307.32, 215.49) * mm, "end": v(308.23, 215.6) * mm});
            skLineSegment(sketch, "E325", {"start": v(308.23, 215.6) * mm, "end": v(309.15, 215.67) * mm});
            skLineSegment(sketch, "E326", {"start": v(309.15, 215.67) * mm, "end": v(310.07, 215.73) * mm});
            skLineSegment(sketch, "E327", {"start": v(310.07, 215.73) * mm, "end": v(311, 215.77) * mm});
            skLineSegment(sketch, "E328", {"start": v(311, 215.77) * mm, "end": v(311.93, 215.78) * mm});
            skLineSegment(sketch, "E329", {"start": v(311.93, 215.78) * mm, "end": v(312.87, 215.77) * mm});
            skLineSegment(sketch, "E330", {"start": v(312.87, 215.77) * mm, "end": v(313.8, 215.73) * mm});
            skLineSegment(sketch, "E331", {"start": v(313.8, 215.73) * mm, "end": v(314.72, 215.67) * mm});
            skLineSegment(sketch, "E332", {"start": v(314.72, 215.67) * mm, "end": v(315.63, 215.6) * mm});
            skLineSegment(sketch, "E333", {"start": v(315.63, 215.6) * mm, "end": v(316.54, 215.49) * mm});
            skLineSegment(sketch, "E334", {"start": v(316.54, 215.49) * mm, "end": v(317.44, 215.36) * mm});
            skLineSegment(sketch, "E335", {"start": v(317.44, 215.36) * mm, "end": v(318.34, 215.21) * mm});
            skLineSegment(sketch, "E336", {"start": v(318.34, 215.21) * mm, "end": v(319.23, 215.04) * mm});
            skLineSegment(sketch, "E337", {"start": v(319.23, 215.04) * mm, "end": v(320.1, 214.85) * mm});
            skLineSegment(sketch, "E338", {"start": v(320.1, 214.85) * mm, "end": v(320.98, 214.64) * mm});
            skLineSegment(sketch, "E339", {"start": v(320.98, 214.64) * mm, "end": v(321.84, 214.4) * mm});
            skLineSegment(sketch, "E340", {"start": v(321.84, 214.4) * mm, "end": v(322.7, 214.15) * mm});
            skLineSegment(sketch, "E341", {"start": v(322.7, 214.15) * mm, "end": v(323.54, 213.88) * mm});
            skLineSegment(sketch, "E342", {"start": v(323.54, 213.88) * mm, "end": v(324.38, 213.58) * mm});
            skLineSegment(sketch, "E343", {"start": v(324.38, 213.58) * mm, "end": v(325.2, 213.27) * mm});
            skLineSegment(sketch, "E344", {"start": v(325.2, 213.27) * mm, "end": v(326.02, 212.93) * mm});
            skLineSegment(sketch, "E345", {"start": v(326.02, 212.93) * mm, "end": v(326.83, 212.58) * mm});
            skLineSegment(sketch, "E346", {"start": v(326.83, 212.58) * mm, "end": v(327.63, 212.2) * mm});
            skLineSegment(sketch, "E347", {"start": v(327.63, 212.2) * mm, "end": v(328.41, 211.82) * mm});
            skLineSegment(sketch, "E348", {"start": v(328.41, 211.82) * mm, "end": v(329.19, 211.4) * mm});
            skLineSegment(sketch, "E349", {"start": v(329.19, 211.4) * mm, "end": v(329.95, 210.98) * mm});
            skLineSegment(sketch, "E350", {"start": v(329.95, 210.98) * mm, "end": v(330.7, 210.54) * mm});
            skLineSegment(sketch, "E351", {"start": v(330.7, 210.54) * mm, "end": v(331.44, 210.08) * mm});
            skLineSegment(sketch, "E352", {"start": v(331.44, 210.08) * mm, "end": v(332.17, 209.6) * mm});
            skLineSegment(sketch, "E353", {"start": v(332.17, 209.6) * mm, "end": v(332.89, 209.1) * mm});
            skLineSegment(sketch, "E354", {"start": v(332.89, 209.1) * mm, "end": v(333.6, 208.59) * mm});
            skLineSegment(sketch, "E355", {"start": v(333.6, 208.59) * mm, "end": v(334.28, 208.06) * mm});
            skLineSegment(sketch, "E356", {"start": v(334.28, 208.06) * mm, "end": v(334.96, 207.51) * mm});
            skLineSegment(sketch, "E357", {"start": v(334.96, 207.51) * mm, "end": v(335.62, 206.95) * mm});
            skLineSegment(sketch, "E358", {"start": v(335.62, 206.95) * mm, "end": v(336.27, 206.37) * mm});
            skLineSegment(sketch, "E359", {"start": v(336.27, 206.37) * mm, "end": v(336.9, 205.78) * mm});
            skLineSegment(sketch, "E360", {"start": v(336.9, 205.78) * mm, "end": v(337.53, 205.17) * mm});
            skLineSegment(sketch, "E361", {"start": v(337.53, 205.17) * mm, "end": v(338.14, 204.55) * mm});
            skLineSegment(sketch, "E362", {"start": v(338.14, 204.55) * mm, "end": v(338.73, 203.92) * mm});
            skLineSegment(sketch, "E363", {"start": v(338.73, 203.92) * mm, "end": v(339.3, 203.27) * mm});
            skLineSegment(sketch, "E364", {"start": v(339.3, 203.27) * mm, "end": v(339.87, 202.6) * mm});
            skLineSegment(sketch, "E365", {"start": v(339.87, 202.6) * mm, "end": v(340.41, 201.93) * mm});
            skLineSegment(sketch, "E366", {"start": v(340.41, 201.93) * mm, "end": v(340.94, 201.24) * mm});
            skLineSegment(sketch, "E367", {"start": v(340.94, 201.24) * mm, "end": v(341.46, 200.53) * mm});
            skLineSegment(sketch, "E368", {"start": v(341.46, 200.53) * mm, "end": v(341.95, 199.82) * mm});
            skLineSegment(sketch, "E369", {"start": v(341.95, 199.82) * mm, "end": v(342.43, 199.09) * mm});
            skLineSegment(sketch, "E370", {"start": v(342.43, 199.09) * mm, "end": v(342.9, 198.35) * mm});
            skLineSegment(sketch, "E371", {"start": v(342.9, 198.35) * mm, "end": v(343.34, 197.6) * mm});
            skLineSegment(sketch, "E372", {"start": v(343.34, 197.6) * mm, "end": v(343.77, 196.83) * mm});
            skLineSegment(sketch, "E373", {"start": v(343.77, 196.83) * mm, "end": v(344.17, 196.06) * mm});
            skLineSegment(sketch, "E374", {"start": v(344.17, 196.06) * mm, "end": v(344.56, 195.27) * mm});
            skLineSegment(sketch, "E375", {"start": v(344.56, 195.27) * mm, "end": v(344.94, 194.47) * mm});
            skLineSegment(sketch, "E376", {"start": v(344.94, 194.47) * mm, "end": v(345.29, 193.67) * mm});
            skLineSegment(sketch, "E377", {"start": v(345.29, 193.67) * mm, "end": v(345.62, 192.85) * mm});
            skLineSegment(sketch, "E378", {"start": v(345.62, 192.85) * mm, "end": v(345.94, 192.02) * mm});
            skLineSegment(sketch, "E379", {"start": v(345.94, 192.02) * mm, "end": v(346.23, 191.19) * mm});
            skLineSegment(sketch, "E380", {"start": v(346.23, 191.19) * mm, "end": v(346.5, 190.34) * mm});
            skLineSegment(sketch, "E381", {"start": v(346.5, 190.34) * mm, "end": v(346.76, 189.49) * mm});
            skLineSegment(sketch, "E382", {"start": v(346.76, 189.49) * mm, "end": v(347, 188.62) * mm});
            skLineSegment(sketch, "E383", {"start": v(347, 188.62) * mm, "end": v(347.2, 187.75) * mm});
            skLineSegment(sketch, "E384", {"start": v(347.2, 187.75) * mm, "end": v(347.4, 186.87) * mm});
            skLineSegment(sketch, "E385", {"start": v(347.4, 186.87) * mm, "end": v(347.57, 185.98) * mm});
            skLineSegment(sketch, "E386", {"start": v(347.57, 185.98) * mm, "end": v(347.72, 185.09) * mm});
            skLineSegment(sketch, "E387", {"start": v(347.72, 185.09) * mm, "end": v(347.84, 184.19) * mm});
            skLineSegment(sketch, "E388", {"start": v(347.84, 184.19) * mm, "end": v(347.95, 183.28) * mm});
            skLineSegment(sketch, "E389", {"start": v(347.95, 183.28) * mm, "end": v(348.03, 182.36) * mm});
            skLineSegment(sketch, "E390", {"start": v(348.03, 182.36) * mm, "end": v(348.09, 181.44) * mm});
            skLineSegment(sketch, "E391", {"start": v(348.09, 181.44) * mm, "end": v(348.12, 180.5) * mm});
            skLineSegment(sketch, "E392", {"start": v(348.12, 180.5) * mm, "end": v(348.13, 179.57) * mm});
            skLineSegment(sketch, "E393", {"start": v(348.13, 179.57) * mm, "end": v(348.12, 178.64) * mm});
            skLineSegment(sketch, "E394", {"start": v(348.12, 178.64) * mm, "end": v(348.09, 177.71) * mm});
            skLineSegment(sketch, "E395", {"start": v(348.09, 177.71) * mm, "end": v(348.03, 176.79) * mm});
            skLineSegment(sketch, "E396", {"start": v(348.03, 176.79) * mm, "end": v(347.95, 175.87) * mm});
            skLineSegment(sketch, "E397", {"start": v(347.95, 175.87) * mm, "end": v(347.84, 174.96) * mm});
            skLineSegment(sketch, "E398", {"start": v(347.84, 174.96) * mm, "end": v(347.72, 174.06) * mm});
            skLineSegment(sketch, "E399", {"start": v(347.72, 174.06) * mm, "end": v(347.57, 173.16) * mm});
            skLineSegment(sketch, "E400", {"start": v(347.57, 173.16) * mm, "end": v(347.4, 172.28) * mm});
            skLineSegment(sketch, "E401", {"start": v(347.4, 172.28) * mm, "end": v(347.2, 171.4) * mm});
            skLineSegment(sketch, "E402", {"start": v(347.2, 171.4) * mm, "end": v(347, 170.53) * mm});
            skLineSegment(sketch, "E403", {"start": v(347, 170.53) * mm, "end": v(346.76, 169.66) * mm});
            skLineSegment(sketch, "E404", {"start": v(346.76, 169.66) * mm, "end": v(346.5, 168.8) * mm});
            skLineSegment(sketch, "E405", {"start": v(346.5, 168.8) * mm, "end": v(346.23, 167.96) * mm});
            skLineSegment(sketch, "E406", {"start": v(346.23, 167.96) * mm, "end": v(345.94, 167.13) * mm});
            skLineSegment(sketch, "E407", {"start": v(345.94, 167.13) * mm, "end": v(345.62, 166.3) * mm});
            skLineSegment(sketch, "E408", {"start": v(345.62, 166.3) * mm, "end": v(345.29, 165.48) * mm});
            skLineSegment(sketch, "E409", {"start": v(345.29, 165.48) * mm, "end": v(344.94, 164.67) * mm});
            skLineSegment(sketch, "E410", {"start": v(344.94, 164.67) * mm, "end": v(344.56, 163.88) * mm});
            skLineSegment(sketch, "E411", {"start": v(344.56, 163.88) * mm, "end": v(344.17, 163.1) * mm});
            skLineSegment(sketch, "E412", {"start": v(344.17, 163.1) * mm, "end": v(343.77, 162.32) * mm});
            skLineSegment(sketch, "E413", {"start": v(343.77, 162.32) * mm, "end": v(343.34, 161.55) * mm});
            skLineSegment(sketch, "E414", {"start": v(343.34, 161.55) * mm, "end": v(342.9, 160.8) * mm});
            skLineSegment(sketch, "E415", {"start": v(342.9, 160.8) * mm, "end": v(342.43, 160.06) * mm});
            skLineSegment(sketch, "E416", {"start": v(342.43, 160.06) * mm, "end": v(341.95, 159.33) * mm});
            skLineSegment(sketch, "E417", {"start": v(341.95, 159.33) * mm, "end": v(341.46, 158.61) * mm});
            skLineSegment(sketch, "E418", {"start": v(341.46, 158.61) * mm, "end": v(340.94, 157.91) * mm});
            skLineSegment(sketch, "E419", {"start": v(340.94, 157.91) * mm, "end": v(340.41, 157.22) * mm});
            skLineSegment(sketch, "E420", {"start": v(340.41, 157.22) * mm, "end": v(339.87, 156.54) * mm});
            skLineSegment(sketch, "E421", {"start": v(339.87, 156.54) * mm, "end": v(339.3, 155.88) * mm});
            skLineSegment(sketch, "E422", {"start": v(339.3, 155.88) * mm, "end": v(338.73, 155.23) * mm});
            skLineSegment(sketch, "E423", {"start": v(338.73, 155.23) * mm, "end": v(338.14, 154.6) * mm});
            skLineSegment(sketch, "E424", {"start": v(338.14, 154.6) * mm, "end": v(337.53, 153.97) * mm});
            skLineSegment(sketch, "E425", {"start": v(337.53, 153.97) * mm, "end": v(336.9, 153.37) * mm});
            skLineSegment(sketch, "E426", {"start": v(336.9, 153.37) * mm, "end": v(336.27, 152.77) * mm});
            skLineSegment(sketch, "E427", {"start": v(336.27, 152.77) * mm, "end": v(335.62, 152.2) * mm});
            skLineSegment(sketch, "E428", {"start": v(335.62, 152.2) * mm, "end": v(334.96, 151.64) * mm});
            skLineSegment(sketch, "E429", {"start": v(334.96, 151.64) * mm, "end": v(334.28, 151.1) * mm});
            skLineSegment(sketch, "E430", {"start": v(334.28, 151.1) * mm, "end": v(333.6, 150.56) * mm});
            skLineSegment(sketch, "E431", {"start": v(333.6, 150.56) * mm, "end": v(332.89, 150.05) * mm});
            skLineSegment(sketch, "E432", {"start": v(332.89, 150.05) * mm, "end": v(332.17, 149.55) * mm});
            skLineSegment(sketch, "E433", {"start": v(332.17, 149.55) * mm, "end": v(331.44, 149.07) * mm});
            skLineSegment(sketch, "E434", {"start": v(331.44, 149.07) * mm, "end": v(330.7, 148.6) * mm});
            skLineSegment(sketch, "E435", {"start": v(330.7, 148.6) * mm, "end": v(329.95, 148.17) * mm});
            skLineSegment(sketch, "E436", {"start": v(329.95, 148.17) * mm, "end": v(329.19, 147.74) * mm});
            skLineSegment(sketch, "E437", {"start": v(329.19, 147.74) * mm, "end": v(328.41, 147.33) * mm});
            skLineSegment(sketch, "E438", {"start": v(328.41, 147.33) * mm, "end": v(327.63, 146.94) * mm});
            skLineSegment(sketch, "E439", {"start": v(327.63, 146.94) * mm, "end": v(326.83, 146.57) * mm});
            skLineSegment(sketch, "E440", {"start": v(326.83, 146.57) * mm, "end": v(326.02, 146.21) * mm});
            skLineSegment(sketch, "E441", {"start": v(326.02, 146.21) * mm, "end": v(325.2, 145.88) * mm});
            skLineSegment(sketch, "E442", {"start": v(325.2, 145.88) * mm, "end": v(324.38, 145.57) * mm});
            skLineSegment(sketch, "E443", {"start": v(324.38, 145.57) * mm, "end": v(323.54, 145.27) * mm});
            skLineSegment(sketch, "E444", {"start": v(323.54, 145.27) * mm, "end": v(322.7, 145) * mm});
            skLineSegment(sketch, "E445", {"start": v(322.7, 145) * mm, "end": v(321.84, 144.74) * mm});
            skLineSegment(sketch, "E446", {"start": v(321.84, 144.74) * mm, "end": v(320.98, 144.5) * mm});
            skLineSegment(sketch, "E447", {"start": v(320.98, 144.5) * mm, "end": v(320.1, 144.3) * mm});
            skLineSegment(sketch, "E448", {"start": v(320.1, 144.3) * mm, "end": v(319.23, 144.1) * mm});
            skLineSegment(sketch, "E449", {"start": v(319.23, 144.1) * mm, "end": v(318.34, 143.93) * mm});
            skLineSegment(sketch, "E450", {"start": v(318.34, 143.93) * mm, "end": v(317.44, 143.79) * mm});
            skLineSegment(sketch, "E451", {"start": v(317.44, 143.79) * mm, "end": v(316.54, 143.66) * mm});
            skLineSegment(sketch, "E452", {"start": v(316.54, 143.66) * mm, "end": v(315.63, 143.56) * mm});
            skLineSegment(sketch, "E453", {"start": v(315.63, 143.56) * mm, "end": v(314.72, 143.47) * mm});
            skLineSegment(sketch, "E454", {"start": v(314.72, 143.47) * mm, "end": v(313.8, 143.42) * mm});
            skLineSegment(sketch, "E455", {"start": v(313.8, 143.42) * mm, "end": v(312.87, 143.38) * mm});
            skLineSegment(sketch, "E456", {"start": v(312.87, 143.38) * mm, "end": v(311.93, 143.37) * mm});
            skLineSegment(sketch, "E457", {"start": v(311.93, 22.27) * mm, "end": v(311, 22.28) * mm});
            skLineSegment(sketch, "E458", {"start": v(311, 22.28) * mm, "end": v(310.07, 22.32) * mm});
            skLineSegment(sketch, "E459", {"start": v(310.07, 22.32) * mm, "end": v(309.15, 22.38) * mm});
            skLineSegment(sketch, "E460", {"start": v(309.15, 22.38) * mm, "end": v(308.23, 22.46) * mm});
            skLineSegment(sketch, "E461", {"start": v(308.23, 22.46) * mm, "end": v(307.32, 22.56) * mm});
            skLineSegment(sketch, "E462", {"start": v(307.32, 22.56) * mm, "end": v(306.42, 22.69) * mm});
            skLineSegment(sketch, "E463", {"start": v(306.42, 22.69) * mm, "end": v(305.52, 22.84) * mm});
            skLineSegment(sketch, "E464", {"start": v(305.52, 22.84) * mm, "end": v(304.63, 23) * mm});
            skLineSegment(sketch, "E465", {"start": v(304.63, 23) * mm, "end": v(303.75, 23.2) * mm});
            skLineSegment(sketch, "E466", {"start": v(303.75, 23.2) * mm, "end": v(302.88, 23.41) * mm});
            skLineSegment(sketch, "E467", {"start": v(302.88, 23.41) * mm, "end": v(302.02, 23.64) * mm});
            skLineSegment(sketch, "E468", {"start": v(302.02, 23.64) * mm, "end": v(301.17, 23.9) * mm});
            skLineSegment(sketch, "E469", {"start": v(301.17, 23.9) * mm, "end": v(300.32, 24.17) * mm});
            skLineSegment(sketch, "E470", {"start": v(300.32, 24.17) * mm, "end": v(299.48, 24.47) * mm});
            skLineSegment(sketch, "E471", {"start": v(299.48, 24.47) * mm, "end": v(298.66, 24.78) * mm});
            skLineSegment(sketch, "E472", {"start": v(298.66, 24.78) * mm, "end": v(297.84, 25.12) * mm});
            skLineSegment(sketch, "E473", {"start": v(297.84, 25.12) * mm, "end": v(297.03, 25.47) * mm});
            skLineSegment(sketch, "E474", {"start": v(297.03, 25.47) * mm, "end": v(296.23, 25.84) * mm});
            skLineSegment(sketch, "E475", {"start": v(296.23, 25.84) * mm, "end": v(295.45, 26.23) * mm});
            skLineSegment(sketch, "E476", {"start": v(295.45, 26.23) * mm, "end": v(294.67, 26.64) * mm});
            skLineSegment(sketch, "E477", {"start": v(294.67, 26.64) * mm, "end": v(293.9, 27.07) * mm});
            skLineSegment(sketch, "E478", {"start": v(293.9, 27.07) * mm, "end": v(293.16, 27.51) * mm});
            skLineSegment(sketch, "E479", {"start": v(293.16, 27.51) * mm, "end": v(292.42, 27.97) * mm});
            skLineSegment(sketch, "E480", {"start": v(292.42, 27.97) * mm, "end": v(291.69, 28.45) * mm});
            skLineSegment(sketch, "E481", {"start": v(291.69, 28.45) * mm, "end": v(290.97, 28.95) * mm});
            skLineSegment(sketch, "E482", {"start": v(290.97, 28.95) * mm, "end": v(290.27, 29.46) * mm});
            skLineSegment(sketch, "E483", {"start": v(290.27, 29.46) * mm, "end": v(289.58, 30) * mm});
            skLineSegment(sketch, "E484", {"start": v(289.58, 30) * mm, "end": v(288.9, 30.54) * mm});
            skLineSegment(sketch, "E485", {"start": v(288.9, 30.54) * mm, "end": v(288.24, 31.1) * mm});
            skLineSegment(sketch, "E486", {"start": v(288.24, 31.1) * mm, "end": v(287.59, 31.68) * mm});
            skLineSegment(sketch, "E487", {"start": v(287.59, 31.68) * mm, "end": v(286.95, 32.27) * mm});
            skLineSegment(sketch, "E488", {"start": v(286.95, 32.27) * mm, "end": v(286.33, 32.87) * mm});
            skLineSegment(sketch, "E489", {"start": v(286.33, 32.87) * mm, "end": v(285.72, 33.5) * mm});
            skLineSegment(sketch, "E490", {"start": v(285.72, 33.5) * mm, "end": v(285.13, 34.13) * mm});
            skLineSegment(sketch, "E491", {"start": v(285.13, 34.13) * mm, "end": v(284.55, 34.78) * mm});
            skLineSegment(sketch, "E492", {"start": v(284.55, 34.78) * mm, "end": v(284, 35.45) * mm});
            skLineSegment(sketch, "E493", {"start": v(284, 35.45) * mm, "end": v(283.45, 36.12) * mm});
            skLineSegment(sketch, "E494", {"start": v(283.45, 36.12) * mm, "end": v(282.92, 36.81) * mm});
            skLineSegment(sketch, "E495", {"start": v(282.92, 36.81) * mm, "end": v(282.4, 37.52) * mm});
            skLineSegment(sketch, "E496", {"start": v(282.4, 37.52) * mm, "end": v(281.9, 38.23) * mm});
            skLineSegment(sketch, "E497", {"start": v(281.9, 38.23) * mm, "end": v(281.43, 38.96) * mm});
            skLineSegment(sketch, "E498", {"start": v(281.43, 38.96) * mm, "end": v(280.97, 39.7) * mm});
            skLineSegment(sketch, "E499", {"start": v(280.97, 39.7) * mm, "end": v(280.52, 40.45) * mm});
            skLineSegment(sketch, "E500", {"start": v(280.52, 40.45) * mm, "end": v(280.1, 41.22) * mm});
            skLineSegment(sketch, "E501", {"start": v(280.1, 41.22) * mm, "end": v(279.69, 42) * mm});
            skLineSegment(sketch, "E502", {"start": v(279.69, 42) * mm, "end": v(279.3, 42.78) * mm});
            skLineSegment(sketch, "E503", {"start": v(279.3, 42.78) * mm, "end": v(278.92, 43.58) * mm});
            skLineSegment(sketch, "E504", {"start": v(278.92, 43.58) * mm, "end": v(278.57, 44.38) * mm});
            skLineSegment(sketch, "E505", {"start": v(278.57, 44.38) * mm, "end": v(278.24, 45.2) * mm});
            skLineSegment(sketch, "E506", {"start": v(278.24, 45.2) * mm, "end": v(277.92, 46.03) * mm});
            skLineSegment(sketch, "E507", {"start": v(277.92, 46.03) * mm, "end": v(277.63, 46.86) * mm});
            skLineSegment(sketch, "E508", {"start": v(277.63, 46.86) * mm, "end": v(277.35, 47.71) * mm});
            skLineSegment(sketch, "E509", {"start": v(277.35, 47.71) * mm, "end": v(277.1, 48.57) * mm});
            skLineSegment(sketch, "E510", {"start": v(277.1, 48.57) * mm, "end": v(276.87, 49.43) * mm});
            skLineSegment(sketch, "E511", {"start": v(276.87, 49.43) * mm, "end": v(276.65, 50.3) * mm});
            skLineSegment(sketch, "E512", {"start": v(276.65, 50.3) * mm, "end": v(276.46, 51.18) * mm});
            skLineSegment(sketch, "E513", {"start": v(276.46, 51.18) * mm, "end": v(276.3, 52.07) * mm});
            skLineSegment(sketch, "E514", {"start": v(276.3, 52.07) * mm, "end": v(276.14, 52.96) * mm});
            skLineSegment(sketch, "E515", {"start": v(276.14, 52.96) * mm, "end": v(276.02, 53.87) * mm});
            skLineSegment(sketch, "E516", {"start": v(276.02, 53.87) * mm, "end": v(275.91, 54.78) * mm});
            skLineSegment(sketch, "E517", {"start": v(275.91, 54.78) * mm, "end": v(275.83, 55.7) * mm});
            skLineSegment(sketch, "E518", {"start": v(275.83, 55.7) * mm, "end": v(275.77, 56.61) * mm});
            skLineSegment(sketch, "E519", {"start": v(275.77, 56.61) * mm, "end": v(275.74, 57.54) * mm});
            skLineSegment(sketch, "E520", {"start": v(275.74, 57.54) * mm, "end": v(275.73, 58.48) * mm});
            skLineSegment(sketch, "E521", {"start": v(275.73, 58.48) * mm, "end": v(275.74, 59.41) * mm});
            skLineSegment(sketch, "E522", {"start": v(275.74, 59.41) * mm, "end": v(275.77, 60.34) * mm});
            skLineSegment(sketch, "E523", {"start": v(275.77, 60.34) * mm, "end": v(275.83, 61.26) * mm});
            skLineSegment(sketch, "E524", {"start": v(275.83, 61.26) * mm, "end": v(275.91, 62.18) * mm});
            skLineSegment(sketch, "E525", {"start": v(275.91, 62.18) * mm, "end": v(276.02, 63.09) * mm});
            skLineSegment(sketch, "E526", {"start": v(276.02, 63.09) * mm, "end": v(276.14, 64) * mm});
            skLineSegment(sketch, "E527", {"start": v(276.14, 64) * mm, "end": v(276.3, 64.89) * mm});
            skLineSegment(sketch, "E528", {"start": v(276.3, 64.89) * mm, "end": v(276.46, 65.77) * mm});
            skLineSegment(sketch, "E529", {"start": v(276.46, 65.77) * mm, "end": v(276.65, 66.65) * mm});
            skLineSegment(sketch, "E530", {"start": v(276.65, 66.65) * mm, "end": v(276.87, 67.53) * mm});
            skLineSegment(sketch, "E531", {"start": v(276.87, 67.53) * mm, "end": v(277.1, 68.39) * mm});
            skLineSegment(sketch, "E532", {"start": v(277.1, 68.39) * mm, "end": v(277.35, 69.24) * mm});
            skLineSegment(sketch, "E533", {"start": v(277.35, 69.24) * mm, "end": v(277.63, 70.1) * mm});
            skLineSegment(sketch, "E534", {"start": v(277.63, 70.1) * mm, "end": v(277.92, 70.93) * mm});
            skLineSegment(sketch, "E535", {"start": v(277.92, 70.93) * mm, "end": v(278.24, 71.75) * mm});
            skLineSegment(sketch, "E536", {"start": v(278.24, 71.75) * mm, "end": v(278.57, 72.57) * mm});
            skLineSegment(sketch, "E537", {"start": v(278.57, 72.57) * mm, "end": v(278.92, 73.38) * mm});
            skLineSegment(sketch, "E538", {"start": v(278.92, 73.38) * mm, "end": v(279.3, 74.17) * mm});
            skLineSegment(sketch, "E539", {"start": v(279.3, 74.17) * mm, "end": v(279.69, 74.96) * mm});
            skLineSegment(sketch, "E540", {"start": v(279.69, 74.96) * mm, "end": v(280.1, 75.74) * mm});
            skLineSegment(sketch, "E541", {"start": v(280.1, 75.74) * mm, "end": v(280.52, 76.5) * mm});
            skLineSegment(sketch, "E542", {"start": v(280.52, 76.5) * mm, "end": v(280.97, 77.25) * mm});
            skLineSegment(sketch, "E543", {"start": v(280.97, 77.25) * mm, "end": v(281.43, 78) * mm});
            skLineSegment(sketch, "E544", {"start": v(281.43, 78) * mm, "end": v(281.9, 78.72) * mm});
            skLineSegment(sketch, "E545", {"start": v(281.9, 78.72) * mm, "end": v(282.4, 79.44) * mm});
            skLineSegment(sketch, "E546", {"start": v(282.4, 79.44) * mm, "end": v(282.92, 80.14) * mm});
            skLineSegment(sketch, "E547", {"start": v(282.92, 80.14) * mm, "end": v(283.45, 80.83) * mm});
            skLineSegment(sketch, "E548", {"start": v(283.45, 80.83) * mm, "end": v(284, 81.5) * mm});
            skLineSegment(sketch, "E549", {"start": v(284, 81.5) * mm, "end": v(284.55, 82.17) * mm});
            skLineSegment(sketch, "E550", {"start": v(284.55, 82.17) * mm, "end": v(285.13, 82.82) * mm});
            skLineSegment(sketch, "E551", {"start": v(285.13, 82.82) * mm, "end": v(285.72, 83.46) * mm});
            skLineSegment(sketch, "E552", {"start": v(285.72, 83.46) * mm, "end": v(286.33, 84.08) * mm});
            skLineSegment(sketch, "E553", {"start": v(286.33, 84.08) * mm, "end": v(286.95, 84.69) * mm});
            skLineSegment(sketch, "E554", {"start": v(286.95, 84.69) * mm, "end": v(287.59, 85.28) * mm});
            skLineSegment(sketch, "E555", {"start": v(287.59, 85.28) * mm, "end": v(288.24, 85.85) * mm});
            skLineSegment(sketch, "E556", {"start": v(288.24, 85.85) * mm, "end": v(288.9, 86.42) * mm});
            skLineSegment(sketch, "E557", {"start": v(288.9, 86.42) * mm, "end": v(289.58, 86.96) * mm});
            skLineSegment(sketch, "E558", {"start": v(289.58, 86.96) * mm, "end": v(290.27, 87.5) * mm});
            skLineSegment(sketch, "E559", {"start": v(290.27, 87.5) * mm, "end": v(290.97, 88) * mm});
            skLineSegment(sketch, "E560", {"start": v(290.97, 88) * mm, "end": v(291.69, 88.5) * mm});
            skLineSegment(sketch, "E561", {"start": v(291.69, 88.5) * mm, "end": v(292.42, 88.98) * mm});
            skLineSegment(sketch, "E562", {"start": v(292.42, 88.98) * mm, "end": v(293.16, 89.44) * mm});
            skLineSegment(sketch, "E563", {"start": v(293.16, 89.44) * mm, "end": v(293.9, 89.89) * mm});
            skLineSegment(sketch, "E564", {"start": v(293.9, 89.89) * mm, "end": v(294.67, 90.31) * mm});
            skLineSegment(sketch, "E565", {"start": v(294.67, 90.31) * mm, "end": v(295.45, 90.72) * mm});
            skLineSegment(sketch, "E566", {"start": v(295.45, 90.72) * mm, "end": v(296.23, 91.11) * mm});
            skLineSegment(sketch, "E567", {"start": v(296.23, 91.11) * mm, "end": v(297.03, 91.48) * mm});
            skLineSegment(sketch, "E568", {"start": v(297.03, 91.48) * mm, "end": v(297.84, 91.84) * mm});
            skLineSegment(sketch, "E569", {"start": v(297.84, 91.84) * mm, "end": v(298.66, 92.17) * mm});
            skLineSegment(sketch, "E570", {"start": v(298.66, 92.17) * mm, "end": v(299.48, 92.49) * mm});
            skLineSegment(sketch, "E571", {"start": v(299.48, 92.49) * mm, "end": v(300.32, 92.78) * mm});
            skLineSegment(sketch, "E572", {"start": v(300.32, 92.78) * mm, "end": v(301.17, 93.06) * mm});
            skLineSegment(sketch, "E573", {"start": v(301.17, 93.06) * mm, "end": v(302.02, 93.3) * mm});
            skLineSegment(sketch, "E574", {"start": v(302.02, 93.3) * mm, "end": v(302.88, 93.54) * mm});
            skLineSegment(sketch, "E575", {"start": v(302.88, 93.54) * mm, "end": v(303.75, 93.76) * mm});
            skLineSegment(sketch, "E576", {"start": v(303.75, 93.76) * mm, "end": v(304.63, 93.95) * mm});
            skLineSegment(sketch, "E577", {"start": v(304.63, 93.95) * mm, "end": v(305.52, 94.12) * mm});
            skLineSegment(sketch, "E578", {"start": v(305.52, 94.12) * mm, "end": v(306.42, 94.27) * mm});
            skLineSegment(sketch, "E579", {"start": v(306.42, 94.27) * mm, "end": v(307.32, 94.4) * mm});
            skLineSegment(sketch, "E580", {"start": v(307.32, 94.4) * mm, "end": v(308.23, 94.5) * mm});
            skLineSegment(sketch, "E581", {"start": v(308.23, 94.5) * mm, "end": v(309.15, 94.58) * mm});
            skLineSegment(sketch, "E582", {"start": v(309.15, 94.58) * mm, "end": v(310.07, 94.64) * mm});
            skLineSegment(sketch, "E583", {"start": v(310.07, 94.64) * mm, "end": v(311, 94.67) * mm});
            skLineSegment(sketch, "E584", {"start": v(311, 94.67) * mm, "end": v(311.93, 94.68) * mm});
            skLineSegment(sketch, "E585", {"start": v(311.93, 94.68) * mm, "end": v(312.87, 94.67) * mm});
            skLineSegment(sketch, "E586", {"start": v(312.87, 94.67) * mm, "end": v(313.8, 94.64) * mm});
            skLineSegment(sketch, "E587", {"start": v(313.8, 94.64) * mm, "end": v(314.72, 94.58) * mm});
            skLineSegment(sketch, "E588", {"start": v(314.72, 94.58) * mm, "end": v(315.63, 94.5) * mm});
            skLineSegment(sketch, "E589", {"start": v(315.63, 94.5) * mm, "end": v(316.54, 94.4) * mm});
            skLineSegment(sketch, "E590", {"start": v(316.54, 94.4) * mm, "end": v(317.44, 94.27) * mm});
            skLineSegment(sketch, "E591", {"start": v(317.44, 94.27) * mm, "end": v(318.34, 94.12) * mm});
            skLineSegment(sketch, "E592", {"start": v(318.34, 94.12) * mm, "end": v(319.23, 93.95) * mm});
            skLineSegment(sketch, "E593", {"start": v(319.23, 93.95) * mm, "end": v(320.1, 93.76) * mm});
            skLineSegment(sketch, "E594", {"start": v(320.1, 93.76) * mm, "end": v(320.98, 93.54) * mm});
            skLineSegment(sketch, "E595", {"start": v(320.98, 93.54) * mm, "end": v(321.84, 93.3) * mm});
            skLineSegment(sketch, "E596", {"start": v(321.84, 93.3) * mm, "end": v(322.7, 93.06) * mm});
            skLineSegment(sketch, "E597", {"start": v(322.7, 93.06) * mm, "end": v(323.54, 92.78) * mm});
            skLineSegment(sketch, "E598", {"start": v(323.54, 92.78) * mm, "end": v(324.38, 92.49) * mm});
            skLineSegment(sketch, "E599", {"start": v(324.38, 92.49) * mm, "end": v(325.2, 92.17) * mm});
            skLineSegment(sketch, "E600", {"start": v(325.2, 92.17) * mm, "end": v(326.02, 91.84) * mm});
            skLineSegment(sketch, "E601", {"start": v(326.02, 91.84) * mm, "end": v(326.83, 91.48) * mm});
            skLineSegment(sketch, "E602", {"start": v(326.83, 91.48) * mm, "end": v(327.63, 91.11) * mm});
            skLineSegment(sketch, "E603", {"start": v(327.63, 91.11) * mm, "end": v(328.41, 90.72) * mm});
            skLineSegment(sketch, "E604", {"start": v(328.41, 90.72) * mm, "end": v(329.19, 90.31) * mm});
            skLineSegment(sketch, "E605", {"start": v(329.19, 90.31) * mm, "end": v(329.95, 89.89) * mm});
            skLineSegment(sketch, "E606", {"start": v(329.95, 89.89) * mm, "end": v(330.7, 89.44) * mm});
            skLineSegment(sketch, "E607", {"start": v(330.7, 89.44) * mm, "end": v(331.44, 88.98) * mm});
            skLineSegment(sketch, "E608", {"start": v(331.44, 88.98) * mm, "end": v(332.17, 88.5) * mm});
            skLineSegment(sketch, "E609", {"start": v(332.17, 88.5) * mm, "end": v(332.89, 88) * mm});
            skLineSegment(sketch, "E610", {"start": v(332.89, 88) * mm, "end": v(333.6, 87.5) * mm});
            skLineSegment(sketch, "E611", {"start": v(333.6, 87.5) * mm, "end": v(334.28, 86.96) * mm});
            skLineSegment(sketch, "E612", {"start": v(334.28, 86.96) * mm, "end": v(334.96, 86.42) * mm});
            skLineSegment(sketch, "E613", {"start": v(334.96, 86.42) * mm, "end": v(335.62, 85.85) * mm});
            skLineSegment(sketch, "E614", {"start": v(335.62, 85.85) * mm, "end": v(336.27, 85.28) * mm});
            skLineSegment(sketch, "E615", {"start": v(336.27, 85.28) * mm, "end": v(336.9, 84.69) * mm});
            skLineSegment(sketch, "E616", {"start": v(336.9, 84.69) * mm, "end": v(337.53, 84.08) * mm});
            skLineSegment(sketch, "E617", {"start": v(337.53, 84.08) * mm, "end": v(338.14, 83.46) * mm});
            skLineSegment(sketch, "E618", {"start": v(338.14, 83.46) * mm, "end": v(338.73, 82.82) * mm});
            skLineSegment(sketch, "E619", {"start": v(338.73, 82.82) * mm, "end": v(339.3, 82.17) * mm});
            skLineSegment(sketch, "E620", {"start": v(339.3, 82.17) * mm, "end": v(339.87, 81.5) * mm});
            skLineSegment(sketch, "E621", {"start": v(339.87, 81.5) * mm, "end": v(340.41, 80.83) * mm});
            skLineSegment(sketch, "E622", {"start": v(340.41, 80.83) * mm, "end": v(340.94, 80.14) * mm});
            skLineSegment(sketch, "E623", {"start": v(340.94, 80.14) * mm, "end": v(341.46, 79.44) * mm});
            skLineSegment(sketch, "E624", {"start": v(341.46, 79.44) * mm, "end": v(341.95, 78.72) * mm});
            skLineSegment(sketch, "E625", {"start": v(341.95, 78.72) * mm, "end": v(342.43, 78) * mm});
            skLineSegment(sketch, "E626", {"start": v(342.43, 78) * mm, "end": v(342.9, 77.25) * mm});
            skLineSegment(sketch, "E627", {"start": v(342.9, 77.25) * mm, "end": v(343.34, 76.5) * mm});
            skLineSegment(sketch, "E628", {"start": v(343.34, 76.5) * mm, "end": v(343.77, 75.74) * mm});
            skLineSegment(sketch, "E629", {"start": v(343.77, 75.74) * mm, "end": v(344.17, 74.96) * mm});
            skLineSegment(sketch, "E630", {"start": v(344.17, 74.96) * mm, "end": v(344.56, 74.17) * mm});
            skLineSegment(sketch, "E631", {"start": v(344.56, 74.17) * mm, "end": v(344.94, 73.38) * mm});
            skLineSegment(sketch, "E632", {"start": v(344.94, 73.38) * mm, "end": v(345.29, 72.57) * mm});
            skLineSegment(sketch, "E633", {"start": v(345.29, 72.57) * mm, "end": v(345.62, 71.75) * mm});
            skLineSegment(sketch, "E634", {"start": v(345.62, 71.75) * mm, "end": v(345.94, 70.93) * mm});
            skLineSegment(sketch, "E635", {"start": v(345.94, 70.93) * mm, "end": v(346.23, 70.1) * mm});
            skLineSegment(sketch, "E636", {"start": v(346.23, 70.1) * mm, "end": v(346.5, 69.24) * mm});
            skLineSegment(sketch, "E637", {"start": v(346.5, 69.24) * mm, "end": v(346.76, 68.39) * mm});
            skLineSegment(sketch, "E638", {"start": v(346.76, 68.39) * mm, "end": v(347, 67.53) * mm});
            skLineSegment(sketch, "E639", {"start": v(347, 67.53) * mm, "end": v(347.2, 66.65) * mm});
            skLineSegment(sketch, "E640", {"start": v(347.2, 66.65) * mm, "end": v(347.4, 65.77) * mm});
            skLineSegment(sketch, "E641", {"start": v(347.4, 65.77) * mm, "end": v(347.57, 64.89) * mm});
            skLineSegment(sketch, "E642", {"start": v(347.57, 64.89) * mm, "end": v(347.72, 64) * mm});
            skLineSegment(sketch, "E643", {"start": v(347.72, 64) * mm, "end": v(347.84, 63.09) * mm});
            skLineSegment(sketch, "E644", {"start": v(347.84, 63.09) * mm, "end": v(347.95, 62.18) * mm});
            skLineSegment(sketch, "E645", {"start": v(347.95, 62.18) * mm, "end": v(348.03, 61.26) * mm});
            skLineSegment(sketch, "E646", {"start": v(348.03, 61.26) * mm, "end": v(348.09, 60.34) * mm});
            skLineSegment(sketch, "E647", {"start": v(348.09, 60.34) * mm, "end": v(348.12, 59.41) * mm});
            skLineSegment(sketch, "E648", {"start": v(348.12, 59.41) * mm, "end": v(348.13, 58.48) * mm});
            skLineSegment(sketch, "E649", {"start": v(348.13, 58.48) * mm, "end": v(348.12, 57.54) * mm});
            skLineSegment(sketch, "E650", {"start": v(348.12, 57.54) * mm, "end": v(348.09, 56.61) * mm});
            skLineSegment(sketch, "E651", {"start": v(348.09, 56.61) * mm, "end": v(348.03, 55.7) * mm});
            skLineSegment(sketch, "E652", {"start": v(348.03, 55.7) * mm, "end": v(347.95, 54.78) * mm});
            skLineSegment(sketch, "E653", {"start": v(347.95, 54.78) * mm, "end": v(347.84, 53.87) * mm});
            skLineSegment(sketch, "E654", {"start": v(347.84, 53.87) * mm, "end": v(347.72, 52.96) * mm});
            skLineSegment(sketch, "E655", {"start": v(347.72, 52.96) * mm, "end": v(347.57, 52.07) * mm});
            skLineSegment(sketch, "E656", {"start": v(347.57, 52.07) * mm, "end": v(347.4, 51.18) * mm});
            skLineSegment(sketch, "E657", {"start": v(347.4, 51.18) * mm, "end": v(347.2, 50.3) * mm});
            skLineSegment(sketch, "E658", {"start": v(347.2, 50.3) * mm, "end": v(347, 49.43) * mm});
            skLineSegment(sketch, "E659", {"start": v(347, 49.43) * mm, "end": v(346.76, 48.57) * mm});
            skLineSegment(sketch, "E660", {"start": v(346.76, 48.57) * mm, "end": v(346.5, 47.71) * mm});
            skLineSegment(sketch, "E661", {"start": v(346.5, 47.71) * mm, "end": v(346.23, 46.86) * mm});
            skLineSegment(sketch, "E662", {"start": v(346.23, 46.86) * mm, "end": v(345.94, 46.03) * mm});
            skLineSegment(sketch, "E663", {"start": v(345.94, 46.03) * mm, "end": v(345.62, 45.2) * mm});
            skLineSegment(sketch, "E664", {"start": v(345.62, 45.2) * mm, "end": v(345.29, 44.38) * mm});
            skLineSegment(sketch, "E665", {"start": v(345.29, 44.38) * mm, "end": v(344.94, 43.58) * mm});
            skLineSegment(sketch, "E666", {"start": v(344.94, 43.58) * mm, "end": v(344.56, 42.78) * mm});
            skLineSegment(sketch, "E667", {"start": v(344.56, 42.78) * mm, "end": v(344.17, 42) * mm});
            skLineSegment(sketch, "E668", {"start": v(344.17, 42) * mm, "end": v(343.77, 41.22) * mm});
            skLineSegment(sketch, "E669", {"start": v(343.77, 41.22) * mm, "end": v(343.34, 40.45) * mm});
            skLineSegment(sketch, "E670", {"start": v(343.34, 40.45) * mm, "end": v(342.9, 39.7) * mm});
            skLineSegment(sketch, "E671", {"start": v(342.9, 39.7) * mm, "end": v(342.43, 38.96) * mm});
            skLineSegment(sketch, "E672", {"start": v(342.43, 38.96) * mm, "end": v(341.95, 38.23) * mm});
            skLineSegment(sketch, "E673", {"start": v(341.95, 38.23) * mm, "end": v(341.46, 37.52) * mm});
            skLineSegment(sketch, "E674", {"start": v(341.46, 37.52) * mm, "end": v(340.94, 36.81) * mm});
            skLineSegment(sketch, "E675", {"start": v(340.94, 36.81) * mm, "end": v(340.41, 36.12) * mm});
            skLineSegment(sketch, "E676", {"start": v(340.41, 36.12) * mm, "end": v(339.87, 35.45) * mm});
            skLineSegment(sketch, "E677", {"start": v(339.87, 35.45) * mm, "end": v(339.3, 34.78) * mm});
            skLineSegment(sketch, "E678", {"start": v(339.3, 34.78) * mm, "end": v(338.73, 34.13) * mm});
            skLineSegment(sketch, "E679", {"start": v(338.73, 34.13) * mm, "end": v(338.14, 33.5) * mm});
            skLineSegment(sketch, "E680", {"start": v(338.14, 33.5) * mm, "end": v(337.53, 32.87) * mm});
            skLineSegment(sketch, "E681", {"start": v(337.53, 32.87) * mm, "end": v(336.9, 32.27) * mm});
            skLineSegment(sketch, "E682", {"start": v(336.9, 32.27) * mm, "end": v(336.27, 31.68) * mm});
            skLineSegment(sketch, "E683", {"start": v(336.27, 31.68) * mm, "end": v(335.62, 31.1) * mm});
            skLineSegment(sketch, "E684", {"start": v(335.62, 31.1) * mm, "end": v(334.96, 30.54) * mm});
            skLineSegment(sketch, "E685", {"start": v(334.96, 30.54) * mm, "end": v(334.28, 30) * mm});
            skLineSegment(sketch, "E686", {"start": v(334.28, 30) * mm, "end": v(333.6, 29.46) * mm});
            skLineSegment(sketch, "E687", {"start": v(333.6, 29.46) * mm, "end": v(332.89, 28.95) * mm});
            skLineSegment(sketch, "E688", {"start": v(332.89, 28.95) * mm, "end": v(332.17, 28.45) * mm});
            skLineSegment(sketch, "E689", {"start": v(332.17, 28.45) * mm, "end": v(331.44, 27.97) * mm});
            skLineSegment(sketch, "E690", {"start": v(331.44, 27.97) * mm, "end": v(330.7, 27.51) * mm});
            skLineSegment(sketch, "E691", {"start": v(330.7, 27.51) * mm, "end": v(329.95, 27.07) * mm});
            skLineSegment(sketch, "E692", {"start": v(329.95, 27.07) * mm, "end": v(329.19, 26.64) * mm});
            skLineSegment(sketch, "E693", {"start": v(329.19, 26.64) * mm, "end": v(328.41, 26.23) * mm});
            skLineSegment(sketch, "E694", {"start": v(328.41, 26.23) * mm, "end": v(327.63, 25.84) * mm});
            skLineSegment(sketch, "E695", {"start": v(327.63, 25.84) * mm, "end": v(326.83, 25.47) * mm});
            skLineSegment(sketch, "E696", {"start": v(326.83, 25.47) * mm, "end": v(326.02, 25.12) * mm});
            skLineSegment(sketch, "E697", {"start": v(326.02, 25.12) * mm, "end": v(325.2, 24.78) * mm});
            skLineSegment(sketch, "E698", {"start": v(325.2, 24.78) * mm, "end": v(324.38, 24.47) * mm});
            skLineSegment(sketch, "E699", {"start": v(324.38, 24.47) * mm, "end": v(323.54, 24.17) * mm});
            skLineSegment(sketch, "E700", {"start": v(323.54, 24.17) * mm, "end": v(322.7, 23.9) * mm});
            skLineSegment(sketch, "E701", {"start": v(322.7, 23.9) * mm, "end": v(321.84, 23.64) * mm});
            skLineSegment(sketch, "E702", {"start": v(321.84, 23.64) * mm, "end": v(320.98, 23.41) * mm});
            skLineSegment(sketch, "E703", {"start": v(320.98, 23.41) * mm, "end": v(320.1, 23.2) * mm});
            skLineSegment(sketch, "E704", {"start": v(320.1, 23.2) * mm, "end": v(319.23, 23) * mm});
            skLineSegment(sketch, "E705", {"start": v(319.23, 23) * mm, "end": v(318.34, 22.84) * mm});
            skLineSegment(sketch, "E706", {"start": v(318.34, 22.84) * mm, "end": v(317.44, 22.69) * mm});
            skLineSegment(sketch, "E707", {"start": v(317.44, 22.69) * mm, "end": v(316.54, 22.56) * mm});
            skLineSegment(sketch, "E708", {"start": v(316.54, 22.56) * mm, "end": v(315.63, 22.46) * mm});
            skLineSegment(sketch, "E709", {"start": v(315.63, 22.46) * mm, "end": v(314.72, 22.38) * mm});
            skLineSegment(sketch, "E710", {"start": v(314.72, 22.38) * mm, "end": v(313.8, 22.32) * mm});
            skLineSegment(sketch, "E711", {"start": v(313.8, 22.32) * mm, "end": v(312.87, 22.28) * mm});
            skLineSegment(sketch, "E712", {"start": v(312.87, 22.28) * mm, "end": v(311.93, 22.27) * mm});
            skLineSegment(sketch, "E713", {"start": v(311.93, -95.46) * mm, "end": v(311, -95.44) * mm});
            skLineSegment(sketch, "E714", {"start": v(311, -95.44) * mm, "end": v(310.07, -95.4) * mm});
            skLineSegment(sketch, "E715", {"start": v(310.07, -95.4) * mm, "end": v(309.15, -95.35) * mm});
            skLineSegment(sketch, "E716", {"start": v(309.15, -95.35) * mm, "end": v(308.23, -95.27) * mm});
            skLineSegment(sketch, "E717", {"start": v(308.23, -95.27) * mm, "end": v(307.32, -95.17) * mm});
            skLineSegment(sketch, "E718", {"start": v(307.32, -95.17) * mm, "end": v(306.42, -95.04) * mm});
            skLineSegment(sketch, "E719", {"start": v(306.42, -95.04) * mm, "end": v(305.52, -94.9) * mm});
            skLineSegment(sketch, "E720", {"start": v(305.52, -94.9) * mm, "end": v(304.63, -94.72) * mm});
            skLineSegment(sketch, "E721", {"start": v(304.63, -94.72) * mm, "end": v(303.75, -94.53) * mm});
            skLineSegment(sketch, "E722", {"start": v(303.75, -94.53) * mm, "end": v(302.88, -94.32) * mm});
            skLineSegment(sketch, "E723", {"start": v(302.88, -94.32) * mm, "end": v(302.02, -94.08) * mm});
            skLineSegment(sketch, "E724", {"start": v(302.02, -94.08) * mm, "end": v(301.17, -93.83) * mm});
            skLineSegment(sketch, "E725", {"start": v(301.17, -93.83) * mm, "end": v(300.32, -93.55) * mm});
            skLineSegment(sketch, "E726", {"start": v(300.32, -93.55) * mm, "end": v(299.48, -93.26) * mm});
            skLineSegment(sketch, "E727", {"start": v(299.48, -93.26) * mm, "end": v(298.66, -92.95) * mm});
            skLineSegment(sketch, "E728", {"start": v(298.66, -92.95) * mm, "end": v(297.84, -92.61) * mm});
            skLineSegment(sketch, "E729", {"start": v(297.84, -92.61) * mm, "end": v(297.03, -92.26) * mm});
            skLineSegment(sketch, "E730", {"start": v(297.03, -92.26) * mm, "end": v(296.23, -91.89) * mm});
            skLineSegment(sketch, "E731", {"start": v(296.23, -91.89) * mm, "end": v(295.45, -91.5) * mm});
            skLineSegment(sketch, "E732", {"start": v(295.45, -91.5) * mm, "end": v(294.67, -91.09) * mm});
            skLineSegment(sketch, "E733", {"start": v(294.67, -91.09) * mm, "end": v(293.9, -90.66) * mm});
            skLineSegment(sketch, "E734", {"start": v(293.9, -90.66) * mm, "end": v(293.16, -90.21) * mm});
            skLineSegment(sketch, "E735", {"start": v(293.16, -90.21) * mm, "end": v(292.42, -89.75) * mm});
            skLineSegment(sketch, "E736", {"start": v(292.42, -89.75) * mm, "end": v(291.69, -89.27) * mm});
            skLineSegment(sketch, "E737", {"start": v(291.69, -89.27) * mm, "end": v(290.97, -88.78) * mm});
            skLineSegment(sketch, "E738", {"start": v(290.97, -88.78) * mm, "end": v(290.27, -88.26) * mm});
            skLineSegment(sketch, "E739", {"start": v(290.27, -88.26) * mm, "end": v(289.58, -87.73) * mm});
            skLineSegment(sketch, "E740", {"start": v(289.58, -87.73) * mm, "end": v(288.9, -87.19) * mm});
            skLineSegment(sketch, "E741", {"start": v(288.9, -87.19) * mm, "end": v(288.24, -86.63) * mm});
            skLineSegment(sketch, "E742", {"start": v(288.24, -86.63) * mm, "end": v(287.59, -86.05) * mm});
            skLineSegment(sketch, "E743", {"start": v(287.59, -86.05) * mm, "end": v(286.95, -85.46) * mm});
            skLineSegment(sketch, "E744", {"start": v(286.95, -85.46) * mm, "end": v(286.33, -84.85) * mm});
            skLineSegment(sketch, "E745", {"start": v(286.33, -84.85) * mm, "end": v(285.72, -84.23) * mm});
            skLineSegment(sketch, "E746", {"start": v(285.72, -84.23) * mm, "end": v(285.13, -83.6) * mm});
            skLineSegment(sketch, "E747", {"start": v(285.13, -83.6) * mm, "end": v(284.55, -82.94) * mm});
            skLineSegment(sketch, "E748", {"start": v(284.55, -82.94) * mm, "end": v(284, -82.28) * mm});
            skLineSegment(sketch, "E749", {"start": v(284, -82.28) * mm, "end": v(283.45, -81.6) * mm});
            skLineSegment(sketch, "E750", {"start": v(283.45, -81.6) * mm, "end": v(282.92, -80.91) * mm});
            skLineSegment(sketch, "E751", {"start": v(282.92, -80.91) * mm, "end": v(282.4, -80.21) * mm});
            skLineSegment(sketch, "E752", {"start": v(282.4, -80.21) * mm, "end": v(281.9, -79.5) * mm});
            skLineSegment(sketch, "E753", {"start": v(281.9, -79.5) * mm, "end": v(281.43, -78.77) * mm});
            skLineSegment(sketch, "E754", {"start": v(281.43, -78.77) * mm, "end": v(280.97, -78.03) * mm});
            skLineSegment(sketch, "E755", {"start": v(280.97, -78.03) * mm, "end": v(280.52, -77.27) * mm});
            skLineSegment(sketch, "E756", {"start": v(280.52, -77.27) * mm, "end": v(280.1, -76.5) * mm});
            skLineSegment(sketch, "E757", {"start": v(280.1, -76.5) * mm, "end": v(279.69, -75.73) * mm});
            skLineSegment(sketch, "E758", {"start": v(279.69, -75.73) * mm, "end": v(279.3, -74.95) * mm});
            skLineSegment(sketch, "E759", {"start": v(279.3, -74.95) * mm, "end": v(278.92, -74.15) * mm});
            skLineSegment(sketch, "E760", {"start": v(278.92, -74.15) * mm, "end": v(278.57, -73.34) * mm});
            skLineSegment(sketch, "E761", {"start": v(278.57, -73.34) * mm, "end": v(278.24, -72.53) * mm});
            skLineSegment(sketch, "E762", {"start": v(278.24, -72.53) * mm, "end": v(277.92, -71.7) * mm});
            skLineSegment(sketch, "E763", {"start": v(277.92, -71.7) * mm, "end": v(277.63, -70.86) * mm});
            skLineSegment(sketch, "E764", {"start": v(277.63, -70.86) * mm, "end": v(277.35, -70.02) * mm});
            skLineSegment(sketch, "E765", {"start": v(277.35, -70.02) * mm, "end": v(277.1, -69.16) * mm});
            skLineSegment(sketch, "E766", {"start": v(277.1, -69.16) * mm, "end": v(276.87, -68.3) * mm});
            skLineSegment(sketch, "E767", {"start": v(276.87, -68.3) * mm, "end": v(276.65, -67.43) * mm});
            skLineSegment(sketch, "E768", {"start": v(276.65, -67.43) * mm, "end": v(276.46, -66.55) * mm});
            skLineSegment(sketch, "E769", {"start": v(276.46, -66.55) * mm, "end": v(276.3, -65.66) * mm});
            skLineSegment(sketch, "E770", {"start": v(276.3, -65.66) * mm, "end": v(276.14, -64.76) * mm});
            skLineSegment(sketch, "E771", {"start": v(276.14, -64.76) * mm, "end": v(276.02, -63.86) * mm});
            skLineSegment(sketch, "E772", {"start": v(276.02, -63.86) * mm, "end": v(275.91, -62.95) * mm});
            skLineSegment(sketch, "E773", {"start": v(275.91, -62.95) * mm, "end": v(275.83, -62.04) * mm});
            skLineSegment(sketch, "E774", {"start": v(275.83, -62.04) * mm, "end": v(275.77, -61.11) * mm});
            skLineSegment(sketch, "E775", {"start": v(275.77, -61.11) * mm, "end": v(275.74, -60.19) * mm});
            skLineSegment(sketch, "E776", {"start": v(275.74, -60.19) * mm, "end": v(275.73, -59.25) * mm});
            skLineSegment(sketch, "E777", {"start": v(275.73, -59.25) * mm, "end": v(275.74, -58.32) * mm});
            skLineSegment(sketch, "E778", {"start": v(275.74, -58.32) * mm, "end": v(275.77, -57.39) * mm});
            skLineSegment(sketch, "E779", {"start": v(275.77, -57.39) * mm, "end": v(275.83, -56.47) * mm});
            skLineSegment(sketch, "E780", {"start": v(275.83, -56.47) * mm, "end": v(275.91, -55.55) * mm});
            skLineSegment(sketch, "E781", {"start": v(275.91, -55.55) * mm, "end": v(276.02, -54.64) * mm});
            skLineSegment(sketch, "E782", {"start": v(276.02, -54.64) * mm, "end": v(276.14, -53.74) * mm});
            skLineSegment(sketch, "E783", {"start": v(276.14, -53.74) * mm, "end": v(276.3, -52.84) * mm});
            skLineSegment(sketch, "E784", {"start": v(276.3, -52.84) * mm, "end": v(276.46, -51.95) * mm});
            skLineSegment(sketch, "E785", {"start": v(276.46, -51.95) * mm, "end": v(276.65, -51.07) * mm});
            skLineSegment(sketch, "E786", {"start": v(276.65, -51.07) * mm, "end": v(276.87, -50.2) * mm});
            skLineSegment(sketch, "E787", {"start": v(276.87, -50.2) * mm, "end": v(277.1, -49.34) * mm});
            skLineSegment(sketch, "E788", {"start": v(277.1, -49.34) * mm, "end": v(277.35, -48.48) * mm});
            skLineSegment(sketch, "E789", {"start": v(277.35, -48.48) * mm, "end": v(277.63, -47.64) * mm});
            skLineSegment(sketch, "E790", {"start": v(277.63, -47.64) * mm, "end": v(277.92, -46.8) * mm});
            skLineSegment(sketch, "E791", {"start": v(277.92, -46.8) * mm, "end": v(278.24, -45.98) * mm});
            skLineSegment(sketch, "E792", {"start": v(278.24, -45.98) * mm, "end": v(278.57, -45.16) * mm});
            skLineSegment(sketch, "E793", {"start": v(278.57, -45.16) * mm, "end": v(278.92, -44.35) * mm});
            skLineSegment(sketch, "E794", {"start": v(278.92, -44.35) * mm, "end": v(279.3, -43.55) * mm});
            skLineSegment(sketch, "E795", {"start": v(279.3, -43.55) * mm, "end": v(279.69, -42.77) * mm});
            skLineSegment(sketch, "E796", {"start": v(279.69, -42.77) * mm, "end": v(280.1, -42) * mm});
            skLineSegment(sketch, "E797", {"start": v(280.1, -42) * mm, "end": v(280.52, -41.23) * mm});
            skLineSegment(sketch, "E798", {"start": v(280.52, -41.23) * mm, "end": v(280.97, -40.48) * mm});
            skLineSegment(sketch, "E799", {"start": v(280.97, -40.48) * mm, "end": v(281.43, -39.74) * mm});
            skLineSegment(sketch, "E800", {"start": v(281.43, -39.74) * mm, "end": v(281.9, -39) * mm});
            skLineSegment(sketch, "E801", {"start": v(281.9, -39) * mm, "end": v(282.4, -38.3) * mm});
            skLineSegment(sketch, "E802", {"start": v(282.4, -38.3) * mm, "end": v(282.92, -37.59) * mm});
            skLineSegment(sketch, "E803", {"start": v(282.92, -37.59) * mm, "end": v(283.45, -36.9) * mm});
            skLineSegment(sketch, "E804", {"start": v(283.45, -36.9) * mm, "end": v(284, -36.22) * mm});
            skLineSegment(sketch, "E805", {"start": v(284, -36.22) * mm, "end": v(284.55, -35.56) * mm});
            skLineSegment(sketch, "E806", {"start": v(284.55, -35.56) * mm, "end": v(285.13, -34.9) * mm});
            skLineSegment(sketch, "E807", {"start": v(285.13, -34.9) * mm, "end": v(285.72, -34.27) * mm});
            skLineSegment(sketch, "E808", {"start": v(285.72, -34.27) * mm, "end": v(286.33, -33.65) * mm});
            skLineSegment(sketch, "E809", {"start": v(286.33, -33.65) * mm, "end": v(286.95, -33.04) * mm});
            skLineSegment(sketch, "E810", {"start": v(286.95, -33.04) * mm, "end": v(287.59, -32.45) * mm});
            skLineSegment(sketch, "E811", {"start": v(287.59, -32.45) * mm, "end": v(288.24, -31.87) * mm});
            skLineSegment(sketch, "E812", {"start": v(288.24, -31.87) * mm, "end": v(288.9, -31.31) * mm});
            skLineSegment(sketch, "E813", {"start": v(288.9, -31.31) * mm, "end": v(289.58, -30.77) * mm});
            skLineSegment(sketch, "E814", {"start": v(289.58, -30.77) * mm, "end": v(290.27, -30.24) * mm});
            skLineSegment(sketch, "E815", {"start": v(290.27, -30.24) * mm, "end": v(290.97, -29.73) * mm});
            skLineSegment(sketch, "E816", {"start": v(290.97, -29.73) * mm, "end": v(291.69, -29.23) * mm});
            skLineSegment(sketch, "E817", {"start": v(291.69, -29.23) * mm, "end": v(292.42, -28.75) * mm});
            skLineSegment(sketch, "E818", {"start": v(292.42, -28.75) * mm, "end": v(293.16, -28.29) * mm});
            skLineSegment(sketch, "E819", {"start": v(293.16, -28.29) * mm, "end": v(293.9, -27.84) * mm});
            skLineSegment(sketch, "E820", {"start": v(293.9, -27.84) * mm, "end": v(294.67, -27.42) * mm});
            skLineSegment(sketch, "E821", {"start": v(294.67, -27.42) * mm, "end": v(295.45, -27) * mm});
            skLineSegment(sketch, "E822", {"start": v(295.45, -27) * mm, "end": v(296.23, -26.62) * mm});
            skLineSegment(sketch, "E823", {"start": v(296.23, -26.62) * mm, "end": v(297.03, -26.24) * mm});
            skLineSegment(sketch, "E824", {"start": v(297.03, -26.24) * mm, "end": v(297.84, -25.9) * mm});
            skLineSegment(sketch, "E825", {"start": v(297.84, -25.9) * mm, "end": v(298.66, -25.56) * mm});
            skLineSegment(sketch, "E826", {"start": v(298.66, -25.56) * mm, "end": v(299.48, -25.24) * mm});
            skLineSegment(sketch, "E827", {"start": v(299.48, -25.24) * mm, "end": v(300.32, -24.95) * mm});
            skLineSegment(sketch, "E828", {"start": v(300.32, -24.95) * mm, "end": v(301.17, -24.67) * mm});
            skLineSegment(sketch, "E829", {"start": v(301.17, -24.67) * mm, "end": v(302.02, -24.42) * mm});
            skLineSegment(sketch, "E830", {"start": v(302.02, -24.42) * mm, "end": v(302.88, -24.19) * mm});
            skLineSegment(sketch, "E831", {"start": v(302.88, -24.19) * mm, "end": v(303.75, -23.97) * mm});
            skLineSegment(sketch, "E832", {"start": v(303.75, -23.97) * mm, "end": v(304.63, -23.78) * mm});
            skLineSegment(sketch, "E833", {"start": v(304.63, -23.78) * mm, "end": v(305.52, -23.61) * mm});
            skLineSegment(sketch, "E834", {"start": v(305.52, -23.61) * mm, "end": v(306.42, -23.46) * mm});
            skLineSegment(sketch, "E835", {"start": v(306.42, -23.46) * mm, "end": v(307.32, -23.34) * mm});
            skLineSegment(sketch, "E836", {"start": v(307.32, -23.34) * mm, "end": v(308.23, -23.23) * mm});
            skLineSegment(sketch, "E837", {"start": v(308.23, -23.23) * mm, "end": v(309.15, -23.15) * mm});
            skLineSegment(sketch, "E838", {"start": v(309.15, -23.15) * mm, "end": v(310.07, -23.1) * mm});
            skLineSegment(sketch, "E839", {"start": v(310.07, -23.1) * mm, "end": v(311, -23.06) * mm});
            skLineSegment(sketch, "E840", {"start": v(311, -23.06) * mm, "end": v(311.93, -23.05) * mm});
            skLineSegment(sketch, "E841", {"start": v(311.93, -23.05) * mm, "end": v(312.87, -23.06) * mm});
            skLineSegment(sketch, "E842", {"start": v(312.87, -23.06) * mm, "end": v(313.8, -23.1) * mm});
            skLineSegment(sketch, "E843", {"start": v(313.8, -23.1) * mm, "end": v(314.72, -23.15) * mm});
            skLineSegment(sketch, "E844", {"start": v(314.72, -23.15) * mm, "end": v(315.63, -23.23) * mm});
            skLineSegment(sketch, "E845", {"start": v(315.63, -23.23) * mm, "end": v(316.54, -23.34) * mm});
            skLineSegment(sketch, "E846", {"start": v(316.54, -23.34) * mm, "end": v(317.44, -23.46) * mm});
            skLineSegment(sketch, "E847", {"start": v(317.44, -23.46) * mm, "end": v(318.34, -23.61) * mm});
            skLineSegment(sketch, "E848", {"start": v(318.34, -23.61) * mm, "end": v(319.23, -23.78) * mm});
            skLineSegment(sketch, "E849", {"start": v(319.23, -23.78) * mm, "end": v(320.1, -23.97) * mm});
            skLineSegment(sketch, "E850", {"start": v(320.1, -23.97) * mm, "end": v(320.98, -24.19) * mm});
            skLineSegment(sketch, "E851", {"start": v(320.98, -24.19) * mm, "end": v(321.84, -24.42) * mm});
            skLineSegment(sketch, "E852", {"start": v(321.84, -24.42) * mm, "end": v(322.7, -24.67) * mm});
            skLineSegment(sketch, "E853", {"start": v(322.7, -24.67) * mm, "end": v(323.54, -24.95) * mm});
            skLineSegment(sketch, "E854", {"start": v(323.54, -24.95) * mm, "end": v(324.38, -25.24) * mm});
            skLineSegment(sketch, "E855", {"start": v(324.38, -25.24) * mm, "end": v(325.2, -25.56) * mm});
            skLineSegment(sketch, "E856", {"start": v(325.2, -25.56) * mm, "end": v(326.02, -25.9) * mm});
            skLineSegment(sketch, "E857", {"start": v(326.02, -25.9) * mm, "end": v(326.83, -26.24) * mm});
            skLineSegment(sketch, "E858", {"start": v(326.83, -26.24) * mm, "end": v(327.63, -26.62) * mm});
            skLineSegment(sketch, "E859", {"start": v(327.63, -26.62) * mm, "end": v(328.41, -27) * mm});
            skLineSegment(sketch, "E860", {"start": v(328.41, -27) * mm, "end": v(329.19, -27.42) * mm});
            skLineSegment(sketch, "E861", {"start": v(329.19, -27.42) * mm, "end": v(329.95, -27.84) * mm});
            skLineSegment(sketch, "E862", {"start": v(329.95, -27.84) * mm, "end": v(330.7, -28.29) * mm});
            skLineSegment(sketch, "E863", {"start": v(330.7, -28.29) * mm, "end": v(331.44, -28.75) * mm});
            skLineSegment(sketch, "E864", {"start": v(331.44, -28.75) * mm, "end": v(332.17, -29.23) * mm});
            skLineSegment(sketch, "E865", {"start": v(332.17, -29.23) * mm, "end": v(332.89, -29.73) * mm});
            skLineSegment(sketch, "E866", {"start": v(332.89, -29.73) * mm, "end": v(333.6, -30.24) * mm});
            skLineSegment(sketch, "E867", {"start": v(333.6, -30.24) * mm, "end": v(334.28, -30.77) * mm});
            skLineSegment(sketch, "E868", {"start": v(334.28, -30.77) * mm, "end": v(334.96, -31.31) * mm});
            skLineSegment(sketch, "E869", {"start": v(334.96, -31.31) * mm, "end": v(335.62, -31.87) * mm});
            skLineSegment(sketch, "E870", {"start": v(335.62, -31.87) * mm, "end": v(336.27, -32.45) * mm});
            skLineSegment(sketch, "E871", {"start": v(336.27, -32.45) * mm, "end": v(336.9, -33.04) * mm});
            skLineSegment(sketch, "E872", {"start": v(336.9, -33.04) * mm, "end": v(337.53, -33.65) * mm});
            skLineSegment(sketch, "E873", {"start": v(337.53, -33.65) * mm, "end": v(338.14, -34.27) * mm});
            skLineSegment(sketch, "E874", {"start": v(338.14, -34.27) * mm, "end": v(338.73, -34.9) * mm});
            skLineSegment(sketch, "E875", {"start": v(338.73, -34.9) * mm, "end": v(339.3, -35.56) * mm});
            skLineSegment(sketch, "E876", {"start": v(339.3, -35.56) * mm, "end": v(339.87, -36.22) * mm});
            skLineSegment(sketch, "E877", {"start": v(339.87, -36.22) * mm, "end": v(340.41, -36.9) * mm});
            skLineSegment(sketch, "E878", {"start": v(340.41, -36.9) * mm, "end": v(340.94, -37.59) * mm});
            skLineSegment(sketch, "E879", {"start": v(340.94, -37.59) * mm, "end": v(341.46, -38.3) * mm});
            skLineSegment(sketch, "E880", {"start": v(341.46, -38.3) * mm, "end": v(341.95, -39) * mm});
            skLineSegment(sketch, "E881", {"start": v(341.95, -39) * mm, "end": v(342.43, -39.74) * mm});
            skLineSegment(sketch, "E882", {"start": v(342.43, -39.74) * mm, "end": v(342.9, -40.48) * mm});
            skLineSegment(sketch, "E883", {"start": v(342.9, -40.48) * mm, "end": v(343.34, -41.23) * mm});
            skLineSegment(sketch, "E884", {"start": v(343.34, -41.23) * mm, "end": v(343.77, -42) * mm});
            skLineSegment(sketch, "E885", {"start": v(343.77, -42) * mm, "end": v(344.17, -42.77) * mm});
            skLineSegment(sketch, "E886", {"start": v(344.17, -42.77) * mm, "end": v(344.56, -43.55) * mm});
            skLineSegment(sketch, "E887", {"start": v(344.56, -43.55) * mm, "end": v(344.94, -44.35) * mm});
            skLineSegment(sketch, "E888", {"start": v(344.94, -44.35) * mm, "end": v(345.29, -45.16) * mm});
            skLineSegment(sketch, "E889", {"start": v(345.29, -45.16) * mm, "end": v(345.62, -45.98) * mm});
            skLineSegment(sketch, "E890", {"start": v(345.62, -45.98) * mm, "end": v(345.94, -46.8) * mm});
            skLineSegment(sketch, "E891", {"start": v(345.94, -46.8) * mm, "end": v(346.23, -47.64) * mm});
            skLineSegment(sketch, "E892", {"start": v(346.23, -47.64) * mm, "end": v(346.5, -48.48) * mm});
            skLineSegment(sketch, "E893", {"start": v(346.5, -48.48) * mm, "end": v(346.76, -49.34) * mm});
            skLineSegment(sketch, "E894", {"start": v(346.76, -49.34) * mm, "end": v(347, -50.2) * mm});
            skLineSegment(sketch, "E895", {"start": v(347, -50.2) * mm, "end": v(347.2, -51.07) * mm});
            skLineSegment(sketch, "E896", {"start": v(347.2, -51.07) * mm, "end": v(347.4, -51.95) * mm});
            skLineSegment(sketch, "E897", {"start": v(347.4, -51.95) * mm, "end": v(347.57, -52.84) * mm});
            skLineSegment(sketch, "E898", {"start": v(347.57, -52.84) * mm, "end": v(347.72, -53.74) * mm});
            skLineSegment(sketch, "E899", {"start": v(347.72, -53.74) * mm, "end": v(347.84, -54.64) * mm});
            skLineSegment(sketch, "E900", {"start": v(347.84, -54.64) * mm, "end": v(347.95, -55.55) * mm});
            skLineSegment(sketch, "E901", {"start": v(347.95, -55.55) * mm, "end": v(348.03, -56.47) * mm});
            skLineSegment(sketch, "E902", {"start": v(348.03, -56.47) * mm, "end": v(348.09, -57.39) * mm});
            skLineSegment(sketch, "E903", {"start": v(348.09, -57.39) * mm, "end": v(348.12, -58.32) * mm});
            skLineSegment(sketch, "E904", {"start": v(348.12, -58.32) * mm, "end": v(348.13, -59.25) * mm});
            skLineSegment(sketch, "E905", {"start": v(348.13, -59.25) * mm, "end": v(348.12, -60.19) * mm});
            skLineSegment(sketch, "E906", {"start": v(348.12, -60.19) * mm, "end": v(348.09, -61.11) * mm});
            skLineSegment(sketch, "E907", {"start": v(348.09, -61.11) * mm, "end": v(348.03, -62.04) * mm});
            skLineSegment(sketch, "E908", {"start": v(348.03, -62.04) * mm, "end": v(347.95, -62.95) * mm});
            skLineSegment(sketch, "E909", {"start": v(347.95, -62.95) * mm, "end": v(347.84, -63.86) * mm});
            skLineSegment(sketch, "E910", {"start": v(347.84, -63.86) * mm, "end": v(347.72, -64.76) * mm});
            skLineSegment(sketch, "E911", {"start": v(347.72, -64.76) * mm, "end": v(347.57, -65.66) * mm});
            skLineSegment(sketch, "E912", {"start": v(347.57, -65.66) * mm, "end": v(347.4, -66.55) * mm});
            skLineSegment(sketch, "E913", {"start": v(347.4, -66.55) * mm, "end": v(347.2, -67.43) * mm});
            skLineSegment(sketch, "E914", {"start": v(347.2, -67.43) * mm, "end": v(347, -68.3) * mm});
            skLineSegment(sketch, "E915", {"start": v(347, -68.3) * mm, "end": v(346.76, -69.16) * mm});
            skLineSegment(sketch, "E916", {"start": v(346.76, -69.16) * mm, "end": v(346.5, -70.02) * mm});
            skLineSegment(sketch, "E917", {"start": v(346.5, -70.02) * mm, "end": v(346.23, -70.86) * mm});
            skLineSegment(sketch, "E918", {"start": v(346.23, -70.86) * mm, "end": v(345.94, -71.7) * mm});
            skLineSegment(sketch, "E919", {"start": v(345.94, -71.7) * mm, "end": v(345.62, -72.53) * mm});
            skLineSegment(sketch, "E920", {"start": v(345.62, -72.53) * mm, "end": v(345.29, -73.34) * mm});
            skLineSegment(sketch, "E921", {"start": v(345.29, -73.34) * mm, "end": v(344.94, -74.15) * mm});
            skLineSegment(sketch, "E922", {"start": v(344.94, -74.15) * mm, "end": v(344.56, -74.95) * mm});
            skLineSegment(sketch, "E923", {"start": v(344.56, -74.95) * mm, "end": v(344.17, -75.73) * mm});
            skLineSegment(sketch, "E924", {"start": v(344.17, -75.73) * mm, "end": v(343.77, -76.5) * mm});
            skLineSegment(sketch, "E925", {"start": v(343.77, -76.5) * mm, "end": v(343.34, -77.27) * mm});
            skLineSegment(sketch, "E926", {"start": v(343.34, -77.27) * mm, "end": v(342.9, -78.03) * mm});
            skLineSegment(sketch, "E927", {"start": v(342.9, -78.03) * mm, "end": v(342.43, -78.77) * mm});
            skLineSegment(sketch, "E928", {"start": v(342.43, -78.77) * mm, "end": v(341.95, -79.5) * mm});
            skLineSegment(sketch, "E929", {"start": v(341.95, -79.5) * mm, "end": v(341.46, -80.21) * mm});
            skLineSegment(sketch, "E930", {"start": v(341.46, -80.21) * mm, "end": v(340.94, -80.91) * mm});
            skLineSegment(sketch, "E931", {"start": v(340.94, -80.91) * mm, "end": v(340.41, -81.6) * mm});
            skLineSegment(sketch, "E932", {"start": v(340.41, -81.6) * mm, "end": v(339.87, -82.28) * mm});
            skLineSegment(sketch, "E933", {"start": v(339.87, -82.28) * mm, "end": v(339.3, -82.94) * mm});
            skLineSegment(sketch, "E934", {"start": v(339.3, -82.94) * mm, "end": v(338.73, -83.6) * mm});
            skLineSegment(sketch, "E935", {"start": v(338.73, -83.6) * mm, "end": v(338.14, -84.23) * mm});
            skLineSegment(sketch, "E936", {"start": v(338.14, -84.23) * mm, "end": v(337.53, -84.85) * mm});
            skLineSegment(sketch, "E937", {"start": v(337.53, -84.85) * mm, "end": v(336.9, -85.46) * mm});
            skLineSegment(sketch, "E938", {"start": v(336.9, -85.46) * mm, "end": v(336.27, -86.05) * mm});
            skLineSegment(sketch, "E939", {"start": v(336.27, -86.05) * mm, "end": v(335.62, -86.63) * mm});
            skLineSegment(sketch, "E940", {"start": v(335.62, -86.63) * mm, "end": v(334.96, -87.19) * mm});
            skLineSegment(sketch, "E941", {"start": v(334.96, -87.19) * mm, "end": v(334.28, -87.73) * mm});
            skLineSegment(sketch, "E942", {"start": v(334.28, -87.73) * mm, "end": v(333.6, -88.26) * mm});
            skLineSegment(sketch, "E943", {"start": v(333.6, -88.26) * mm, "end": v(332.89, -88.78) * mm});
            skLineSegment(sketch, "E944", {"start": v(332.89, -88.78) * mm, "end": v(332.17, -89.27) * mm});
            skLineSegment(sketch, "E945", {"start": v(332.17, -89.27) * mm, "end": v(331.44, -89.75) * mm});
            skLineSegment(sketch, "E946", {"start": v(331.44, -89.75) * mm, "end": v(330.7, -90.21) * mm});
            skLineSegment(sketch, "E947", {"start": v(330.7, -90.21) * mm, "end": v(329.95, -90.66) * mm});
            skLineSegment(sketch, "E948", {"start": v(329.95, -90.66) * mm, "end": v(329.19, -91.09) * mm});
            skLineSegment(sketch, "E949", {"start": v(329.19, -91.09) * mm, "end": v(328.41, -91.5) * mm});
            skLineSegment(sketch, "E950", {"start": v(328.41, -91.5) * mm, "end": v(327.63, -91.89) * mm});
            skLineSegment(sketch, "E951", {"start": v(327.63, -91.89) * mm, "end": v(326.83, -92.26) * mm});
            skLineSegment(sketch, "E952", {"start": v(326.83, -92.26) * mm, "end": v(326.02, -92.61) * mm});
            skLineSegment(sketch, "E953", {"start": v(326.02, -92.61) * mm, "end": v(325.2, -92.95) * mm});
            skLineSegment(sketch, "E954", {"start": v(325.2, -92.95) * mm, "end": v(324.38, -93.26) * mm});
            skLineSegment(sketch, "E955", {"start": v(324.38, -93.26) * mm, "end": v(323.54, -93.55) * mm});
            skLineSegment(sketch, "E956", {"start": v(323.54, -93.55) * mm, "end": v(322.7, -93.83) * mm});
            skLineSegment(sketch, "E957", {"start": v(322.7, -93.83) * mm, "end": v(321.84, -94.08) * mm});
            skLineSegment(sketch, "E958", {"start": v(321.84, -94.08) * mm, "end": v(320.98, -94.32) * mm});
            skLineSegment(sketch, "E959", {"start": v(320.98, -94.32) * mm, "end": v(320.1, -94.53) * mm});
            skLineSegment(sketch, "E960", {"start": v(320.1, -94.53) * mm, "end": v(319.23, -94.72) * mm});
            skLineSegment(sketch, "E961", {"start": v(319.23, -94.72) * mm, "end": v(318.34, -94.9) * mm});
            skLineSegment(sketch, "E962", {"start": v(318.34, -94.9) * mm, "end": v(317.44, -95.04) * mm});
            skLineSegment(sketch, "E963", {"start": v(317.44, -95.04) * mm, "end": v(316.54, -95.17) * mm});
            skLineSegment(sketch, "E964", {"start": v(316.54, -95.17) * mm, "end": v(315.63, -95.27) * mm});
            skLineSegment(sketch, "E965", {"start": v(315.63, -95.27) * mm, "end": v(314.72, -95.35) * mm});
            skLineSegment(sketch, "E966", {"start": v(314.72, -95.35) * mm, "end": v(313.8, -95.4) * mm});
            skLineSegment(sketch, "E967", {"start": v(313.8, -95.4) * mm, "end": v(312.87, -95.44) * mm});
            skLineSegment(sketch, "E968", {"start": v(312.87, -95.44) * mm, "end": v(311.93, -95.46) * mm});
            skLineSegment(sketch, "E969", {"start": v(310.66, 344.32) * mm, "end": v(311.6, 344.31) * mm});
            skLineSegment(sketch, "E970", {"start": v(311.6, 344.31) * mm, "end": v(312.53, 344.28) * mm});
            skLineSegment(sketch, "E971", {"start": v(312.53, 344.28) * mm, "end": v(313.45, 344.22) * mm});
            skLineSegment(sketch, "E972", {"start": v(313.45, 344.22) * mm, "end": v(314.36, 344.14) * mm});
            skLineSegment(sketch, "E973", {"start": v(314.36, 344.14) * mm, "end": v(315.27, 344.03) * mm});
            skLineSegment(sketch, "E974", {"start": v(315.27, 344.03) * mm, "end": v(316.18, 343.9) * mm});
            skLineSegment(sketch, "E975", {"start": v(316.18, 343.9) * mm, "end": v(317.07, 343.76) * mm});
            skLineSegment(sketch, "E976", {"start": v(317.07, 343.76) * mm, "end": v(317.96, 343.59) * mm});
            skLineSegment(sketch, "E977", {"start": v(317.96, 343.59) * mm, "end": v(318.84, 343.4) * mm});
            skLineSegment(sketch, "E978", {"start": v(318.84, 343.4) * mm, "end": v(319.71, 343.18) * mm});
            skLineSegment(sketch, "E979", {"start": v(319.71, 343.18) * mm, "end": v(320.57, 342.95) * mm});
            skLineSegment(sketch, "E980", {"start": v(320.57, 342.95) * mm, "end": v(321.43, 342.7) * mm});
            skLineSegment(sketch, "E981", {"start": v(321.43, 342.7) * mm, "end": v(322.27, 342.42) * mm});
            skLineSegment(sketch, "E982", {"start": v(322.27, 342.42) * mm, "end": v(323.11, 342.13) * mm});
            skLineSegment(sketch, "E983", {"start": v(323.11, 342.13) * mm, "end": v(323.94, 341.81) * mm});
            skLineSegment(sketch, "E984", {"start": v(323.94, 341.81) * mm, "end": v(324.75, 341.48) * mm});
            skLineSegment(sketch, "E985", {"start": v(324.75, 341.48) * mm, "end": v(325.56, 341.13) * mm});
            skLineSegment(sketch, "E986", {"start": v(325.56, 341.13) * mm, "end": v(326.36, 340.75) * mm});
            skLineSegment(sketch, "E987", {"start": v(326.36, 340.75) * mm, "end": v(327.14, 340.36) * mm});
            skLineSegment(sketch, "E988", {"start": v(327.14, 340.36) * mm, "end": v(327.92, 339.95) * mm});
            skLineSegment(sketch, "E989", {"start": v(327.92, 339.95) * mm, "end": v(328.68, 339.53) * mm});
            skLineSegment(sketch, "E990", {"start": v(328.68, 339.53) * mm, "end": v(329.44, 339.08) * mm});
            skLineSegment(sketch, "E991", {"start": v(329.44, 339.08) * mm, "end": v(330.18, 338.62) * mm});
            skLineSegment(sketch, "E992", {"start": v(330.18, 338.62) * mm, "end": v(330.9, 338.14) * mm});
            skLineSegment(sketch, "E993", {"start": v(330.9, 338.14) * mm, "end": v(331.62, 337.64) * mm});
            skLineSegment(sketch, "E994", {"start": v(331.62, 337.64) * mm, "end": v(332.32, 337.13) * mm});
            skLineSegment(sketch, "E995", {"start": v(332.32, 337.13) * mm, "end": v(333.01, 336.6) * mm});
            skLineSegment(sketch, "E996", {"start": v(333.01, 336.6) * mm, "end": v(333.7, 336.06) * mm});
            skLineSegment(sketch, "E997", {"start": v(333.7, 336.06) * mm, "end": v(334.35, 335.5) * mm});
            skLineSegment(sketch, "E998", {"start": v(334.35, 335.5) * mm, "end": v(335, 334.92) * mm});
            skLineSegment(sketch, "E999", {"start": v(335, 334.92) * mm, "end": v(335.64, 334.33) * mm});
            skLineSegment(sketch, "E1000", {"start": v(335.64, 334.33) * mm, "end": v(336.26, 333.72) * mm});
            skLineSegment(sketch, "E1001", {"start": v(336.26, 333.72) * mm, "end": v(336.87, 333.1) * mm});
            skLineSegment(sketch, "E1002", {"start": v(336.87, 333.1) * mm, "end": v(337.46, 332.46) * mm});
            skLineSegment(sketch, "E1003", {"start": v(337.46, 332.46) * mm, "end": v(338.04, 331.81) * mm});
            skLineSegment(sketch, "E1004", {"start": v(338.04, 331.81) * mm, "end": v(338.6, 331.15) * mm});
            skLineSegment(sketch, "E1005", {"start": v(338.6, 331.15) * mm, "end": v(339.14, 330.47) * mm});
            skLineSegment(sketch, "E1006", {"start": v(339.14, 330.47) * mm, "end": v(339.67, 329.78) * mm});
            skLineSegment(sketch, "E1007", {"start": v(339.67, 329.78) * mm, "end": v(340.19, 329.08) * mm});
            skLineSegment(sketch, "E1008", {"start": v(340.19, 329.08) * mm, "end": v(340.68, 328.36) * mm});
            skLineSegment(sketch, "E1009", {"start": v(340.68, 328.36) * mm, "end": v(341.16, 327.63) * mm});
            skLineSegment(sketch, "E1010", {"start": v(341.16, 327.63) * mm, "end": v(341.62, 326.9) * mm});
            skLineSegment(sketch, "E1011", {"start": v(341.62, 326.9) * mm, "end": v(342.07, 326.14) * mm});
            skLineSegment(sketch, "E1012", {"start": v(342.07, 326.14) * mm, "end": v(342.5, 325.38) * mm});
            skLineSegment(sketch, "E1013", {"start": v(342.5, 325.38) * mm, "end": v(342.9, 324.6) * mm});
            skLineSegment(sketch, "E1014", {"start": v(342.9, 324.6) * mm, "end": v(343.3, 323.82) * mm});
            skLineSegment(sketch, "E1015", {"start": v(343.3, 323.82) * mm, "end": v(343.67, 323.02) * mm});
            skLineSegment(sketch, "E1016", {"start": v(343.67, 323.02) * mm, "end": v(344.02, 322.21) * mm});
            skLineSegment(sketch, "E1017", {"start": v(344.02, 322.21) * mm, "end": v(344.35, 321.4) * mm});
            skLineSegment(sketch, "E1018", {"start": v(344.35, 321.4) * mm, "end": v(344.67, 320.57) * mm});
            skLineSegment(sketch, "E1019", {"start": v(344.67, 320.57) * mm, "end": v(344.96, 319.73) * mm});
            skLineSegment(sketch, "E1020", {"start": v(344.96, 319.73) * mm, "end": v(345.24, 318.88) * mm});
            skLineSegment(sketch, "E1021", {"start": v(345.24, 318.88) * mm, "end": v(345.5, 318.03) * mm});
            skLineSegment(sketch, "E1022", {"start": v(345.5, 318.03) * mm, "end": v(345.73, 317.17) * mm});
            skLineSegment(sketch, "E1023", {"start": v(345.73, 317.17) * mm, "end": v(345.94, 316.3) * mm});
            skLineSegment(sketch, "E1024", {"start": v(345.94, 316.3) * mm, "end": v(346.13, 315.42) * mm});
            skLineSegment(sketch, "E1025", {"start": v(346.13, 315.42) * mm, "end": v(346.3, 314.53) * mm});
            skLineSegment(sketch, "E1026", {"start": v(346.3, 314.53) * mm, "end": v(346.45, 313.63) * mm});
            skLineSegment(sketch, "E1027", {"start": v(346.45, 313.63) * mm, "end": v(346.57, 312.73) * mm});
            skLineSegment(sketch, "E1028", {"start": v(346.57, 312.73) * mm, "end": v(346.68, 311.82) * mm});
            skLineSegment(sketch, "E1029", {"start": v(346.68, 311.82) * mm, "end": v(346.76, 310.9) * mm});
            skLineSegment(sketch, "E1030", {"start": v(346.76, 310.9) * mm, "end": v(346.82, 309.98) * mm});
            skLineSegment(sketch, "E1031", {"start": v(346.82, 309.98) * mm, "end": v(346.85, 309.05) * mm});
            skLineSegment(sketch, "E1032", {"start": v(346.85, 309.05) * mm, "end": v(346.87, 308.12) * mm});
            skLineSegment(sketch, "E1033", {"start": v(346.87, 308.12) * mm, "end": v(346.85, 307.18) * mm});
            skLineSegment(sketch, "E1034", {"start": v(346.85, 307.18) * mm, "end": v(346.82, 306.26) * mm});
            skLineSegment(sketch, "E1035", {"start": v(346.82, 306.26) * mm, "end": v(346.76, 305.33) * mm});
            skLineSegment(sketch, "E1036", {"start": v(346.76, 305.33) * mm, "end": v(346.68, 304.42) * mm});
            skLineSegment(sketch, "E1037", {"start": v(346.68, 304.42) * mm, "end": v(346.57, 303.5) * mm});
            skLineSegment(sketch, "E1038", {"start": v(346.57, 303.5) * mm, "end": v(346.45, 302.6) * mm});
            skLineSegment(sketch, "E1039", {"start": v(346.45, 302.6) * mm, "end": v(346.3, 301.7) * mm});
            skLineSegment(sketch, "E1040", {"start": v(346.3, 301.7) * mm, "end": v(346.13, 300.82) * mm});
            skLineSegment(sketch, "E1041", {"start": v(346.13, 300.82) * mm, "end": v(345.94, 299.94) * mm});
            skLineSegment(sketch, "E1042", {"start": v(345.94, 299.94) * mm, "end": v(345.73, 299.07) * mm});
            skLineSegment(sketch, "E1043", {"start": v(345.73, 299.07) * mm, "end": v(345.5, 298.2) * mm});
            skLineSegment(sketch, "E1044", {"start": v(345.5, 298.2) * mm, "end": v(345.24, 297.35) * mm});
            skLineSegment(sketch, "E1045", {"start": v(345.24, 297.35) * mm, "end": v(344.96, 296.5) * mm});
            skLineSegment(sketch, "E1046", {"start": v(344.96, 296.5) * mm, "end": v(344.67, 295.67) * mm});
            skLineSegment(sketch, "E1047", {"start": v(344.67, 295.67) * mm, "end": v(344.35, 294.84) * mm});
            skLineSegment(sketch, "E1048", {"start": v(344.35, 294.84) * mm, "end": v(344.02, 294.03) * mm});
            skLineSegment(sketch, "E1049", {"start": v(344.02, 294.03) * mm, "end": v(343.67, 293.22) * mm});
            skLineSegment(sketch, "E1050", {"start": v(343.67, 293.22) * mm, "end": v(343.3, 292.42) * mm});
            skLineSegment(sketch, "E1051", {"start": v(343.3, 292.42) * mm, "end": v(342.9, 291.64) * mm});
            skLineSegment(sketch, "E1052", {"start": v(342.9, 291.64) * mm, "end": v(342.5, 290.86) * mm});
            skLineSegment(sketch, "E1053", {"start": v(342.5, 290.86) * mm, "end": v(342.07, 290.1) * mm});
            skLineSegment(sketch, "E1054", {"start": v(342.07, 290.1) * mm, "end": v(341.62, 289.34) * mm});
            skLineSegment(sketch, "E1055", {"start": v(341.62, 289.34) * mm, "end": v(341.16, 288.6) * mm});
            skLineSegment(sketch, "E1056", {"start": v(341.16, 288.6) * mm, "end": v(340.68, 287.88) * mm});
            skLineSegment(sketch, "E1057", {"start": v(340.68, 287.88) * mm, "end": v(340.19, 287.16) * mm});
            skLineSegment(sketch, "E1058", {"start": v(340.19, 287.16) * mm, "end": v(339.67, 286.46) * mm});
            skLineSegment(sketch, "E1059", {"start": v(339.67, 286.46) * mm, "end": v(339.14, 285.77) * mm});
            skLineSegment(sketch, "E1060", {"start": v(339.14, 285.77) * mm, "end": v(338.6, 285.09) * mm});
            skLineSegment(sketch, "E1061", {"start": v(338.6, 285.09) * mm, "end": v(338.04, 284.42) * mm});
            skLineSegment(sketch, "E1062", {"start": v(338.04, 284.42) * mm, "end": v(337.46, 283.77) * mm});
            skLineSegment(sketch, "E1063", {"start": v(337.46, 283.77) * mm, "end": v(336.87, 283.14) * mm});
            skLineSegment(sketch, "E1064", {"start": v(336.87, 283.14) * mm, "end": v(336.26, 282.52) * mm});
            skLineSegment(sketch, "E1065", {"start": v(336.26, 282.52) * mm, "end": v(335.64, 281.91) * mm});
            skLineSegment(sketch, "E1066", {"start": v(335.64, 281.91) * mm, "end": v(335, 281.32) * mm});
            skLineSegment(sketch, "E1067", {"start": v(335, 281.32) * mm, "end": v(334.35, 280.74) * mm});
            skLineSegment(sketch, "E1068", {"start": v(334.35, 280.74) * mm, "end": v(333.7, 280.18) * mm});
            skLineSegment(sketch, "E1069", {"start": v(333.7, 280.18) * mm, "end": v(333.01, 279.64) * mm});
            skLineSegment(sketch, "E1070", {"start": v(333.01, 279.64) * mm, "end": v(332.32, 279.1) * mm});
            skLineSegment(sketch, "E1071", {"start": v(332.32, 279.1) * mm, "end": v(331.62, 278.6) * mm});
            skLineSegment(sketch, "E1072", {"start": v(331.62, 278.6) * mm, "end": v(330.9, 278.1) * mm});
            skLineSegment(sketch, "E1073", {"start": v(330.9, 278.1) * mm, "end": v(330.18, 277.62) * mm});
            skLineSegment(sketch, "E1074", {"start": v(330.18, 277.62) * mm, "end": v(329.44, 277.15) * mm});
            skLineSegment(sketch, "E1075", {"start": v(329.44, 277.15) * mm, "end": v(328.68, 276.7) * mm});
            skLineSegment(sketch, "E1076", {"start": v(328.68, 276.7) * mm, "end": v(327.92, 276.28) * mm});
            skLineSegment(sketch, "E1077", {"start": v(327.92, 276.28) * mm, "end": v(327.14, 275.87) * mm});
            skLineSegment(sketch, "E1078", {"start": v(327.14, 275.87) * mm, "end": v(326.36, 275.48) * mm});
            skLineSegment(sketch, "E1079", {"start": v(326.36, 275.48) * mm, "end": v(325.56, 275.11) * mm});
            skLineSegment(sketch, "E1080", {"start": v(325.56, 275.11) * mm, "end": v(324.75, 274.76) * mm});
            skLineSegment(sketch, "E1081", {"start": v(324.75, 274.76) * mm, "end": v(323.94, 274.42) * mm});
            skLineSegment(sketch, "E1082", {"start": v(323.94, 274.42) * mm, "end": v(323.11, 274.11) * mm});
            skLineSegment(sketch, "E1083", {"start": v(323.11, 274.11) * mm, "end": v(322.27, 273.82) * mm});
            skLineSegment(sketch, "E1084", {"start": v(322.27, 273.82) * mm, "end": v(321.43, 273.54) * mm});
            skLineSegment(sketch, "E1085", {"start": v(321.43, 273.54) * mm, "end": v(320.57, 273.29) * mm});
            skLineSegment(sketch, "E1086", {"start": v(320.57, 273.29) * mm, "end": v(319.71, 273.05) * mm});
            skLineSegment(sketch, "E1087", {"start": v(319.71, 273.05) * mm, "end": v(318.84, 272.84) * mm});
            skLineSegment(sketch, "E1088", {"start": v(318.84, 272.84) * mm, "end": v(317.96, 272.65) * mm});
            skLineSegment(sketch, "E1089", {"start": v(317.96, 272.65) * mm, "end": v(317.07, 272.48) * mm});
            skLineSegment(sketch, "E1090", {"start": v(317.07, 272.48) * mm, "end": v(316.18, 272.33) * mm});
            skLineSegment(sketch, "E1091", {"start": v(316.18, 272.33) * mm, "end": v(315.27, 272.2) * mm});
            skLineSegment(sketch, "E1092", {"start": v(315.27, 272.2) * mm, "end": v(314.36, 272.1) * mm});
            skLineSegment(sketch, "E1093", {"start": v(314.36, 272.1) * mm, "end": v(313.45, 272.02) * mm});
            skLineSegment(sketch, "E1094", {"start": v(313.45, 272.02) * mm, "end": v(312.53, 271.96) * mm});
            skLineSegment(sketch, "E1095", {"start": v(312.53, 271.96) * mm, "end": v(311.6, 271.92) * mm});
            skLineSegment(sketch, "E1096", {"start": v(311.6, 271.92) * mm, "end": v(310.66, 271.91) * mm});
            skLineSegment(sketch, "E1097", {"start": v(310.66, 271.91) * mm, "end": v(309.73, 271.92) * mm});
            skLineSegment(sketch, "E1098", {"start": v(309.73, 271.92) * mm, "end": v(308.8, 271.96) * mm});
            skLineSegment(sketch, "E1099", {"start": v(308.8, 271.96) * mm, "end": v(307.88, 272.02) * mm});
            skLineSegment(sketch, "E1100", {"start": v(307.88, 272.02) * mm, "end": v(306.96, 272.1) * mm});
            skLineSegment(sketch, "E1101", {"start": v(306.96, 272.1) * mm, "end": v(306.05, 272.2) * mm});
            skLineSegment(sketch, "E1102", {"start": v(306.05, 272.2) * mm, "end": v(305.15, 272.33) * mm});
            skLineSegment(sketch, "E1103", {"start": v(305.15, 272.33) * mm, "end": v(304.25, 272.48) * mm});
            skLineSegment(sketch, "E1104", {"start": v(304.25, 272.48) * mm, "end": v(303.37, 272.65) * mm});
            skLineSegment(sketch, "E1105", {"start": v(303.37, 272.65) * mm, "end": v(302.49, 272.84) * mm});
            skLineSegment(sketch, "E1106", {"start": v(302.49, 272.84) * mm, "end": v(301.61, 273.05) * mm});
            skLineSegment(sketch, "E1107", {"start": v(301.61, 273.05) * mm, "end": v(300.75, 273.29) * mm});
            skLineSegment(sketch, "E1108", {"start": v(300.75, 273.29) * mm, "end": v(299.9, 273.54) * mm});
            skLineSegment(sketch, "E1109", {"start": v(299.9, 273.54) * mm, "end": v(299.05, 273.82) * mm});
            skLineSegment(sketch, "E1110", {"start": v(299.05, 273.82) * mm, "end": v(298.21, 274.11) * mm});
            skLineSegment(sketch, "E1111", {"start": v(298.21, 274.11) * mm, "end": v(297.39, 274.42) * mm});
            skLineSegment(sketch, "E1112", {"start": v(297.39, 274.42) * mm, "end": v(296.57, 274.76) * mm});
            skLineSegment(sketch, "E1113", {"start": v(296.57, 274.76) * mm, "end": v(295.76, 275.11) * mm});
            skLineSegment(sketch, "E1114", {"start": v(295.76, 275.11) * mm, "end": v(294.97, 275.48) * mm});
            skLineSegment(sketch, "E1115", {"start": v(294.97, 275.48) * mm, "end": v(294.18, 275.87) * mm});
            skLineSegment(sketch, "E1116", {"start": v(294.18, 275.87) * mm, "end": v(293.4, 276.28) * mm});
            skLineSegment(sketch, "E1117", {"start": v(293.4, 276.28) * mm, "end": v(292.64, 276.7) * mm});
            skLineSegment(sketch, "E1118", {"start": v(292.64, 276.7) * mm, "end": v(291.89, 277.15) * mm});
            skLineSegment(sketch, "E1119", {"start": v(291.89, 277.15) * mm, "end": v(291.15, 277.62) * mm});
            skLineSegment(sketch, "E1120", {"start": v(291.15, 277.62) * mm, "end": v(290.42, 278.1) * mm});
            skLineSegment(sketch, "E1121", {"start": v(290.42, 278.1) * mm, "end": v(289.7, 278.6) * mm});
            skLineSegment(sketch, "E1122", {"start": v(289.7, 278.6) * mm, "end": v(289, 279.1) * mm});
            skLineSegment(sketch, "E1123", {"start": v(289, 279.1) * mm, "end": v(288.3, 279.64) * mm});
            skLineSegment(sketch, "E1124", {"start": v(288.3, 279.64) * mm, "end": v(287.63, 280.18) * mm});
            skLineSegment(sketch, "E1125", {"start": v(287.63, 280.18) * mm, "end": v(286.97, 280.74) * mm});
            skLineSegment(sketch, "E1126", {"start": v(286.97, 280.74) * mm, "end": v(286.32, 281.32) * mm});
            skLineSegment(sketch, "E1127", {"start": v(286.32, 281.32) * mm, "end": v(285.68, 281.91) * mm});
            skLineSegment(sketch, "E1128", {"start": v(285.68, 281.91) * mm, "end": v(285.06, 282.52) * mm});
            skLineSegment(sketch, "E1129", {"start": v(285.06, 282.52) * mm, "end": v(284.45, 283.14) * mm});
            skLineSegment(sketch, "E1130", {"start": v(284.45, 283.14) * mm, "end": v(283.86, 283.77) * mm});
            skLineSegment(sketch, "E1131", {"start": v(283.86, 283.77) * mm, "end": v(283.29, 284.42) * mm});
            skLineSegment(sketch, "E1132", {"start": v(283.29, 284.42) * mm, "end": v(282.72, 285.09) * mm});
            skLineSegment(sketch, "E1133", {"start": v(282.72, 285.09) * mm, "end": v(282.18, 285.77) * mm});
            skLineSegment(sketch, "E1134", {"start": v(282.18, 285.77) * mm, "end": v(281.65, 286.46) * mm});
            skLineSegment(sketch, "E1135", {"start": v(281.65, 286.46) * mm, "end": v(281.14, 287.16) * mm});
            skLineSegment(sketch, "E1136", {"start": v(281.14, 287.16) * mm, "end": v(280.64, 287.88) * mm});
            skLineSegment(sketch, "E1137", {"start": v(280.64, 287.88) * mm, "end": v(280.16, 288.6) * mm});
            skLineSegment(sketch, "E1138", {"start": v(280.16, 288.6) * mm, "end": v(279.7, 289.34) * mm});
            skLineSegment(sketch, "E1139", {"start": v(279.7, 289.34) * mm, "end": v(279.25, 290.1) * mm});
            skLineSegment(sketch, "E1140", {"start": v(279.25, 290.1) * mm, "end": v(278.83, 290.86) * mm});
            skLineSegment(sketch, "E1141", {"start": v(278.83, 290.86) * mm, "end": v(278.42, 291.64) * mm});
            skLineSegment(sketch, "E1142", {"start": v(278.42, 291.64) * mm, "end": v(278.03, 292.42) * mm});
            skLineSegment(sketch, "E1143", {"start": v(278.03, 292.42) * mm, "end": v(277.66, 293.22) * mm});
            skLineSegment(sketch, "E1144", {"start": v(277.66, 293.22) * mm, "end": v(277.3, 294.03) * mm});
            skLineSegment(sketch, "E1145", {"start": v(277.3, 294.03) * mm, "end": v(276.97, 294.84) * mm});
            skLineSegment(sketch, "E1146", {"start": v(276.97, 294.84) * mm, "end": v(276.65, 295.67) * mm});
            skLineSegment(sketch, "E1147", {"start": v(276.65, 295.67) * mm, "end": v(276.36, 296.5) * mm});
            skLineSegment(sketch, "E1148", {"start": v(276.36, 296.5) * mm, "end": v(276.08, 297.35) * mm});
            skLineSegment(sketch, "E1149", {"start": v(276.08, 297.35) * mm, "end": v(275.83, 298.2) * mm});
            skLineSegment(sketch, "E1150", {"start": v(275.83, 298.2) * mm, "end": v(275.6, 299.07) * mm});
            skLineSegment(sketch, "E1151", {"start": v(275.6, 299.07) * mm, "end": v(275.38, 299.94) * mm});
            skLineSegment(sketch, "E1152", {"start": v(275.38, 299.94) * mm, "end": v(275.2, 300.82) * mm});
            skLineSegment(sketch, "E1153", {"start": v(275.2, 300.82) * mm, "end": v(275.02, 301.7) * mm});
            skLineSegment(sketch, "E1154", {"start": v(275.02, 301.7) * mm, "end": v(274.87, 302.6) * mm});
            skLineSegment(sketch, "E1155", {"start": v(274.87, 302.6) * mm, "end": v(274.75, 303.5) * mm});
            skLineSegment(sketch, "E1156", {"start": v(274.75, 303.5) * mm, "end": v(274.64, 304.42) * mm});
            skLineSegment(sketch, "E1157", {"start": v(274.64, 304.42) * mm, "end": v(274.56, 305.33) * mm});
            skLineSegment(sketch, "E1158", {"start": v(274.56, 305.33) * mm, "end": v(274.5, 306.26) * mm});
            skLineSegment(sketch, "E1159", {"start": v(274.5, 306.26) * mm, "end": v(274.47, 307.18) * mm});
            skLineSegment(sketch, "E1160", {"start": v(274.47, 307.18) * mm, "end": v(274.46, 308.12) * mm});
            skLineSegment(sketch, "E1161", {"start": v(274.46, 308.12) * mm, "end": v(274.47, 309.05) * mm});
            skLineSegment(sketch, "E1162", {"start": v(274.47, 309.05) * mm, "end": v(274.5, 309.98) * mm});
            skLineSegment(sketch, "E1163", {"start": v(274.5, 309.98) * mm, "end": v(274.56, 310.9) * mm});
            skLineSegment(sketch, "E1164", {"start": v(274.56, 310.9) * mm, "end": v(274.64, 311.82) * mm});
            skLineSegment(sketch, "E1165", {"start": v(274.64, 311.82) * mm, "end": v(274.75, 312.73) * mm});
            skLineSegment(sketch, "E1166", {"start": v(274.75, 312.73) * mm, "end": v(274.87, 313.63) * mm});
            skLineSegment(sketch, "E1167", {"start": v(274.87, 313.63) * mm, "end": v(275.02, 314.53) * mm});
            skLineSegment(sketch, "E1168", {"start": v(275.02, 314.53) * mm, "end": v(275.2, 315.42) * mm});
            skLineSegment(sketch, "E1169", {"start": v(275.2, 315.42) * mm, "end": v(275.38, 316.3) * mm});
            skLineSegment(sketch, "E1170", {"start": v(275.38, 316.3) * mm, "end": v(275.6, 317.17) * mm});
            skLineSegment(sketch, "E1171", {"start": v(275.6, 317.17) * mm, "end": v(275.83, 318.03) * mm});
            skLineSegment(sketch, "E1172", {"start": v(275.83, 318.03) * mm, "end": v(276.08, 318.88) * mm});
            skLineSegment(sketch, "E1173", {"start": v(276.08, 318.88) * mm, "end": v(276.36, 319.73) * mm});
            skLineSegment(sketch, "E1174", {"start": v(276.36, 319.73) * mm, "end": v(276.65, 320.57) * mm});
            skLineSegment(sketch, "E1175", {"start": v(276.65, 320.57) * mm, "end": v(276.97, 321.4) * mm});
            skLineSegment(sketch, "E1176", {"start": v(276.97, 321.4) * mm, "end": v(277.3, 322.21) * mm});
            skLineSegment(sketch, "E1177", {"start": v(277.3, 322.21) * mm, "end": v(277.66, 323.02) * mm});
            skLineSegment(sketch, "E1178", {"start": v(277.66, 323.02) * mm, "end": v(278.03, 323.82) * mm});
            skLineSegment(sketch, "E1179", {"start": v(278.03, 323.82) * mm, "end": v(278.42, 324.6) * mm});
            skLineSegment(sketch, "E1180", {"start": v(278.42, 324.6) * mm, "end": v(278.83, 325.38) * mm});
            skLineSegment(sketch, "E1181", {"start": v(278.83, 325.38) * mm, "end": v(279.25, 326.14) * mm});
            skLineSegment(sketch, "E1182", {"start": v(279.25, 326.14) * mm, "end": v(279.7, 326.9) * mm});
            skLineSegment(sketch, "E1183", {"start": v(279.7, 326.9) * mm, "end": v(280.16, 327.63) * mm});
            skLineSegment(sketch, "E1184", {"start": v(280.16, 327.63) * mm, "end": v(280.64, 328.36) * mm});
            skLineSegment(sketch, "E1185", {"start": v(280.64, 328.36) * mm, "end": v(281.14, 329.08) * mm});
            skLineSegment(sketch, "E1186", {"start": v(281.14, 329.08) * mm, "end": v(281.65, 329.78) * mm});
            skLineSegment(sketch, "E1187", {"start": v(281.65, 329.78) * mm, "end": v(282.18, 330.47) * mm});
            skLineSegment(sketch, "E1188", {"start": v(282.18, 330.47) * mm, "end": v(282.72, 331.15) * mm});
            skLineSegment(sketch, "E1189", {"start": v(282.72, 331.15) * mm, "end": v(283.29, 331.81) * mm});
            skLineSegment(sketch, "E1190", {"start": v(283.29, 331.81) * mm, "end": v(283.86, 332.46) * mm});
            skLineSegment(sketch, "E1191", {"start": v(283.86, 332.46) * mm, "end": v(284.45, 333.1) * mm});
            skLineSegment(sketch, "E1192", {"start": v(284.45, 333.1) * mm, "end": v(285.06, 333.72) * mm});
            skLineSegment(sketch, "E1193", {"start": v(285.06, 333.72) * mm, "end": v(285.68, 334.33) * mm});
            skLineSegment(sketch, "E1194", {"start": v(285.68, 334.33) * mm, "end": v(286.32, 334.92) * mm});
            skLineSegment(sketch, "E1195", {"start": v(286.32, 334.92) * mm, "end": v(286.97, 335.5) * mm});
            skLineSegment(sketch, "E1196", {"start": v(286.97, 335.5) * mm, "end": v(287.63, 336.06) * mm});
            skLineSegment(sketch, "E1197", {"start": v(287.63, 336.06) * mm, "end": v(288.3, 336.6) * mm});
            skLineSegment(sketch, "E1198", {"start": v(288.3, 336.6) * mm, "end": v(289, 337.13) * mm});
            skLineSegment(sketch, "E1199", {"start": v(289, 337.13) * mm, "end": v(289.7, 337.64) * mm});
            skLineSegment(sketch, "E1200", {"start": v(289.7, 337.64) * mm, "end": v(290.42, 338.14) * mm});
            skLineSegment(sketch, "E1201", {"start": v(290.42, 338.14) * mm, "end": v(291.15, 338.62) * mm});
            skLineSegment(sketch, "E1202", {"start": v(291.15, 338.62) * mm, "end": v(291.89, 339.08) * mm});
            skLineSegment(sketch, "E1203", {"start": v(291.89, 339.08) * mm, "end": v(292.64, 339.53) * mm});
            skLineSegment(sketch, "E1204", {"start": v(292.64, 339.53) * mm, "end": v(293.4, 339.95) * mm});
            skLineSegment(sketch, "E1205", {"start": v(293.4, 339.95) * mm, "end": v(294.18, 340.36) * mm});
            skLineSegment(sketch, "E1206", {"start": v(294.18, 340.36) * mm, "end": v(294.97, 340.75) * mm});
            skLineSegment(sketch, "E1207", {"start": v(294.97, 340.75) * mm, "end": v(295.76, 341.13) * mm});
            skLineSegment(sketch, "E1208", {"start": v(295.76, 341.13) * mm, "end": v(296.57, 341.48) * mm});
            skLineSegment(sketch, "E1209", {"start": v(296.57, 341.48) * mm, "end": v(297.39, 341.81) * mm});
            skLineSegment(sketch, "E1210", {"start": v(297.39, 341.81) * mm, "end": v(298.21, 342.13) * mm});
            skLineSegment(sketch, "E1211", {"start": v(298.21, 342.13) * mm, "end": v(299.05, 342.42) * mm});
            skLineSegment(sketch, "E1212", {"start": v(299.05, 342.42) * mm, "end": v(299.9, 342.7) * mm});
            skLineSegment(sketch, "E1213", {"start": v(299.9, 342.7) * mm, "end": v(300.75, 342.95) * mm});
            skLineSegment(sketch, "E1214", {"start": v(300.75, 342.95) * mm, "end": v(301.61, 343.18) * mm});
            skLineSegment(sketch, "E1215", {"start": v(301.61, 343.18) * mm, "end": v(302.49, 343.4) * mm});
            skLineSegment(sketch, "E1216", {"start": v(302.49, 343.4) * mm, "end": v(303.37, 343.59) * mm});
            skLineSegment(sketch, "E1217", {"start": v(303.37, 343.59) * mm, "end": v(304.25, 343.76) * mm});
            skLineSegment(sketch, "E1218", {"start": v(304.25, 343.76) * mm, "end": v(305.15, 343.9) * mm});
            skLineSegment(sketch, "E1219", {"start": v(305.15, 343.9) * mm, "end": v(306.05, 344.03) * mm});
            skLineSegment(sketch, "E1220", {"start": v(306.05, 344.03) * mm, "end": v(306.96, 344.14) * mm});
            skLineSegment(sketch, "E1221", {"start": v(306.96, 344.14) * mm, "end": v(307.88, 344.22) * mm});
            skLineSegment(sketch, "E1222", {"start": v(307.88, 344.22) * mm, "end": v(308.8, 344.28) * mm});
            skLineSegment(sketch, "E1223", {"start": v(308.8, 344.28) * mm, "end": v(309.73, 344.31) * mm});
            skLineSegment(sketch, "E1224", {"start": v(309.73, 344.31) * mm, "end": v(310.66, 344.32) * mm});
            skLineSegment(sketch, "E1225", {"start": v(308.55, 471.04) * mm, "end": v(306.26, 471.03) * mm});
            skLineSegment(sketch, "E1226", {"start": v(306.26, 471.03) * mm, "end": v(303.99, 470.98) * mm});
            skLineSegment(sketch, "E1227", {"start": v(303.99, 470.98) * mm, "end": v(301.72, 470.9) * mm});
            skLineSegment(sketch, "E1228", {"start": v(301.72, 470.9) * mm, "end": v(299.46, 470.78) * mm});
            skLineSegment(sketch, "E1229", {"start": v(299.46, 470.78) * mm, "end": v(297.21, 470.63) * mm});
            skLineSegment(sketch, "E1230", {"start": v(297.21, 470.63) * mm, "end": v(294.97, 470.45) * mm});
            skLineSegment(sketch, "E1231", {"start": v(294.97, 470.45) * mm, "end": v(292.74, 470.23) * mm});
            skLineSegment(sketch, "E1232", {"start": v(292.74, 470.23) * mm, "end": v(290.52, 469.99) * mm});
            skLineSegment(sketch, "E1233", {"start": v(290.52, 469.99) * mm, "end": v(288.3, 469.71) * mm});
            skLineSegment(sketch, "E1234", {"start": v(288.3, 469.71) * mm, "end": v(286.1, 469.4) * mm});
            skLineSegment(sketch, "E1235", {"start": v(286.1, 469.4) * mm, "end": v(283.91, 469.07) * mm});
            skLineSegment(sketch, "E1236", {"start": v(283.91, 469.07) * mm, "end": v(281.73, 468.7) * mm});
            skLineSegment(sketch, "E1237", {"start": v(281.73, 468.7) * mm, "end": v(279.56, 468.3) * mm});
            skLineSegment(sketch, "E1238", {"start": v(279.56, 468.3) * mm, "end": v(277.4, 467.86) * mm});
            skLineSegment(sketch, "E1239", {"start": v(277.4, 467.86) * mm, "end": v(275.25, 467.4) * mm});
            skLineSegment(sketch, "E1240", {"start": v(275.25, 467.4) * mm, "end": v(273.11, 466.9) * mm});
            skLineSegment(sketch, "E1241", {"start": v(273.11, 466.9) * mm, "end": v(270.99, 466.39) * mm});
            skLineSegment(sketch, "E1242", {"start": v(270.99, 466.39) * mm, "end": v(268.87, 465.83) * mm});
            skLineSegment(sketch, "E1243", {"start": v(268.87, 465.83) * mm, "end": v(266.77, 465.25) * mm});
            skLineSegment(sketch, "E1244", {"start": v(266.77, 465.25) * mm, "end": v(264.68, 464.64) * mm});
            skLineSegment(sketch, "E1245", {"start": v(264.68, 464.64) * mm, "end": v(262.6, 464) * mm});
            skLineSegment(sketch, "E1246", {"start": v(262.6, 464) * mm, "end": v(260.54, 463.34) * mm});
            skLineSegment(sketch, "E1247", {"start": v(260.54, 463.34) * mm, "end": v(258.48, 462.64) * mm});
            skLineSegment(sketch, "E1248", {"start": v(258.48, 462.64) * mm, "end": v(256.45, 461.92) * mm});
            skLineSegment(sketch, "E1249", {"start": v(256.45, 461.92) * mm, "end": v(254.42, 461.16) * mm});
            skLineSegment(sketch, "E1250", {"start": v(254.42, 461.16) * mm, "end": v(252.4, 460.38) * mm});
            skLineSegment(sketch, "E1251", {"start": v(252.4, 460.38) * mm, "end": v(250.41, 459.58) * mm});
            skLineSegment(sketch, "E1252", {"start": v(250.41, 459.58) * mm, "end": v(248.43, 458.74) * mm});
            skLineSegment(sketch, "E1253", {"start": v(248.43, 458.74) * mm, "end": v(246.46, 457.88) * mm});
            skLineSegment(sketch, "E1254", {"start": v(246.46, 457.88) * mm, "end": v(244.5, 457) * mm});
            skLineSegment(sketch, "E1255", {"start": v(244.5, 457) * mm, "end": v(242.56, 456.08) * mm});
            skLineSegment(sketch, "E1256", {"start": v(242.56, 456.08) * mm, "end": v(240.64, 455.13) * mm});
            skLineSegment(sketch, "E1257", {"start": v(240.64, 455.13) * mm, "end": v(238.73, 454.17) * mm});
            skLineSegment(sketch, "E1258", {"start": v(238.73, 454.17) * mm, "end": v(236.83, 453.17) * mm});
            skLineSegment(sketch, "E1259", {"start": v(236.83, 453.17) * mm, "end": v(234.96, 452.15) * mm});
            skLineSegment(sketch, "E1260", {"start": v(234.96, 452.15) * mm, "end": v(233.1, 451.1) * mm});
            skLineSegment(sketch, "E1261", {"start": v(233.1, 451.1) * mm, "end": v(231.25, 450.04) * mm});
            skLineSegment(sketch, "E1262", {"start": v(231.25, 450.04) * mm, "end": v(229.42, 448.94) * mm});
            skLineSegment(sketch, "E1263", {"start": v(229.42, 448.94) * mm, "end": v(227.6, 447.83) * mm});
            skLineSegment(sketch, "E1264", {"start": v(227.6, 447.83) * mm, "end": v(225.8, 446.68) * mm});
            skLineSegment(sketch, "E1265", {"start": v(225.8, 446.68) * mm, "end": v(224.03, 445.51) * mm});
            skLineSegment(sketch, "E1266", {"start": v(224.03, 445.51) * mm, "end": v(222.27, 444.32) * mm});
            skLineSegment(sketch, "E1267", {"start": v(222.27, 444.32) * mm, "end": v(220.52, 443.1) * mm});
            skLineSegment(sketch, "E1268", {"start": v(220.52, 443.1) * mm, "end": v(218.8, 441.87) * mm});
            skLineSegment(sketch, "E1269", {"start": v(218.8, 441.87) * mm, "end": v(217.09, 440.6) * mm});
            skLineSegment(sketch, "E1270", {"start": v(217.09, 440.6) * mm, "end": v(215.4, 439.32) * mm});
            skLineSegment(sketch, "E1271", {"start": v(215.4, 439.32) * mm, "end": v(213.73, 438) * mm});
            skLineSegment(sketch, "E1272", {"start": v(213.73, 438) * mm, "end": v(212.08, 436.68) * mm});
            skLineSegment(sketch, "E1273", {"start": v(212.08, 436.68) * mm, "end": v(210.44, 435.32) * mm});
            skLineSegment(sketch, "E1274", {"start": v(210.44, 435.32) * mm, "end": v(208.83, 433.95) * mm});
            skLineSegment(sketch, "E1275", {"start": v(208.83, 433.95) * mm, "end": v(207.23, 432.55) * mm});
            skLineSegment(sketch, "E1276", {"start": v(207.23, 432.55) * mm, "end": v(205.66, 431.13) * mm});
            skLineSegment(sketch, "E1277", {"start": v(205.66, 431.13) * mm, "end": v(204.1, 429.69) * mm});
            skLineSegment(sketch, "E1278", {"start": v(204.1, 429.69) * mm, "end": v(202.57, 428.23) * mm});
            skLineSegment(sketch, "E1279", {"start": v(202.57, 428.23) * mm, "end": v(201.05, 426.74) * mm});
            skLineSegment(sketch, "E1280", {"start": v(201.05, 426.74) * mm, "end": v(199.56, 425.24) * mm});
            skLineSegment(sketch, "E1281", {"start": v(199.56, 425.24) * mm, "end": v(198.09, 423.71) * mm});
            skLineSegment(sketch, "E1282", {"start": v(198.09, 423.71) * mm, "end": v(196.63, 422.17) * mm});
            skLineSegment(sketch, "E1283", {"start": v(196.63, 422.17) * mm, "end": v(195.2, 420.6) * mm});
            skLineSegment(sketch, "E1284", {"start": v(195.2, 420.6) * mm, "end": v(193.8, 419.02) * mm});
            skLineSegment(sketch, "E1285", {"start": v(193.8, 419.02) * mm, "end": v(192.4, 417.42) * mm});
            skLineSegment(sketch, "E1286", {"start": v(192.4, 417.42) * mm, "end": v(191.04, 415.8) * mm});
            skLineSegment(sketch, "E1287", {"start": v(191.04, 415.8) * mm, "end": v(189.7, 414.15) * mm});
            skLineSegment(sketch, "E1288", {"start": v(189.7, 414.15) * mm, "end": v(188.38, 412.49) * mm});
            skLineSegment(sketch, "E1289", {"start": v(188.38, 412.49) * mm, "end": v(8.44, 172.14) * mm});
            skLineSegment(sketch, "E1290", {"start": v(8.44, 172.14) * mm, "end": v(132.69, -6.09) * mm});
            skLineSegment(sketch, "E1291", {"start": v(132.69, -6.09) * mm, "end": v(133.63, -7.3) * mm});
            skLineSegment(sketch, "E1292", {"start": v(133.63, -7.3) * mm, "end": v(134.57, -8.54) * mm});
            skLineSegment(sketch, "E1293", {"start": v(134.57, -8.54) * mm, "end": v(135.49, -9.77) * mm});
            skLineSegment(sketch, "E1294", {"start": v(135.49, -9.77) * mm, "end": v(136.4, -11.02) * mm});
            skLineSegment(sketch, "E1295", {"start": v(136.4, -11.02) * mm, "end": v(137.3, -12.28) * mm});
            skLineSegment(sketch, "E1296", {"start": v(137.3, -12.28) * mm, "end": v(138.18, -13.55) * mm});
            skLineSegment(sketch, "E1297", {"start": v(138.18, -13.55) * mm, "end": v(139.05, -14.82) * mm});
            skLineSegment(sketch, "E1298", {"start": v(139.05, -14.82) * mm, "end": v(139.9, -16.1) * mm});
            skLineSegment(sketch, "E1299", {"start": v(139.9, -16.1) * mm, "end": v(140.75, -17.4) * mm});
            skLineSegment(sketch, "E1300", {"start": v(140.75, -17.4) * mm, "end": v(141.59, -18.7) * mm});
            skLineSegment(sketch, "E1301", {"start": v(141.59, -18.7) * mm, "end": v(142.4, -20.02) * mm});
            skLineSegment(sketch, "E1302", {"start": v(142.4, -20.02) * mm, "end": v(143.21, -21.34) * mm});
            skLineSegment(sketch, "E1303", {"start": v(143.21, -21.34) * mm, "end": v(144, -22.67) * mm});
            skLineSegment(sketch, "E1304", {"start": v(144, -22.67) * mm, "end": v(144.79, -24.01) * mm});
            skLineSegment(sketch, "E1305", {"start": v(144.79, -24.01) * mm, "end": v(145.56, -25.36) * mm});
            skLineSegment(sketch, "E1306", {"start": v(145.56, -25.36) * mm, "end": v(146.31, -26.72) * mm});
            skLineSegment(sketch, "E1307", {"start": v(146.31, -26.72) * mm, "end": v(147.05, -28.08) * mm});
            skLineSegment(sketch, "E1308", {"start": v(147.05, -28.08) * mm, "end": v(147.78, -29.46) * mm});
            skLineSegment(sketch, "E1309", {"start": v(147.78, -29.46) * mm, "end": v(148.5, -30.84) * mm});
            skLineSegment(sketch, "E1310", {"start": v(148.5, -30.84) * mm, "end": v(149.2, -32.23) * mm});
            skLineSegment(sketch, "E1311", {"start": v(149.2, -32.23) * mm, "end": v(149.88, -33.63) * mm});
            skLineSegment(sketch, "E1312", {"start": v(149.88, -33.63) * mm, "end": v(150.55, -35.03) * mm});
            skLineSegment(sketch, "E1313", {"start": v(150.55, -35.03) * mm, "end": v(151.21, -36.45) * mm});
            skLineSegment(sketch, "E1314", {"start": v(151.21, -36.45) * mm, "end": v(151.86, -37.87) * mm});
            skLineSegment(sketch, "E1315", {"start": v(151.86, -37.87) * mm, "end": v(152.49, -39.3) * mm});
            skLineSegment(sketch, "E1316", {"start": v(152.49, -39.3) * mm, "end": v(153.1, -40.73) * mm});
            skLineSegment(sketch, "E1317", {"start": v(153.1, -40.73) * mm, "end": v(153.7, -42.18) * mm});
            skLineSegment(sketch, "E1318", {"start": v(153.7, -42.18) * mm, "end": v(154.3, -43.63) * mm});
            skLineSegment(sketch, "E1319", {"start": v(154.3, -43.63) * mm, "end": v(154.87, -45.09) * mm});
            skLineSegment(sketch, "E1320", {"start": v(154.87, -45.09) * mm, "end": v(155.43, -46.55) * mm});
            skLineSegment(sketch, "E1321", {"start": v(155.43, -46.55) * mm, "end": v(155.97, -48.03) * mm});
            skLineSegment(sketch, "E1322", {"start": v(155.97, -48.03) * mm, "end": v(156.5, -49.5) * mm});
            skLineSegment(sketch, "E1323", {"start": v(156.5, -49.5) * mm, "end": v(157.01, -51) * mm});
            skLineSegment(sketch, "E1324", {"start": v(157.01, -51) * mm, "end": v(157.51, -52.5) * mm});
            skLineSegment(sketch, "E1325", {"start": v(157.51, -52.5) * mm, "end": v(158, -54) * mm});
            skLineSegment(sketch, "E1326", {"start": v(158, -54) * mm, "end": v(158.46, -55.5) * mm});
            skLineSegment(sketch, "E1327", {"start": v(158.46, -55.5) * mm, "end": v(158.92, -57.02) * mm});
            skLineSegment(sketch, "E1328", {"start": v(158.92, -57.02) * mm, "end": v(159.36, -58.54) * mm});
            skLineSegment(sketch, "E1329", {"start": v(159.36, -58.54) * mm, "end": v(159.78, -60.06) * mm});
            skLineSegment(sketch, "E1330", {"start": v(159.78, -60.06) * mm, "end": v(160.19, -61.6) * mm});
            skLineSegment(sketch, "E1331", {"start": v(160.19, -61.6) * mm, "end": v(160.58, -63.14) * mm});
            skLineSegment(sketch, "E1332", {"start": v(160.58, -63.14) * mm, "end": v(160.95, -64.69) * mm});
            skLineSegment(sketch, "E1333", {"start": v(160.95, -64.69) * mm, "end": v(161.31, -66.24) * mm});
            skLineSegment(sketch, "E1334", {"start": v(161.31, -66.24) * mm, "end": v(161.66, -67.8) * mm});
            skLineSegment(sketch, "E1335", {"start": v(161.66, -67.8) * mm, "end": v(161.99, -69.36) * mm});
            skLineSegment(sketch, "E1336", {"start": v(161.99, -69.36) * mm, "end": v(162.3, -70.93) * mm});
            skLineSegment(sketch, "E1337", {"start": v(162.3, -70.93) * mm, "end": v(162.6, -72.5) * mm});
            skLineSegment(sketch, "E1338", {"start": v(162.6, -72.5) * mm, "end": v(162.88, -74.1) * mm});
            skLineSegment(sketch, "E1339", {"start": v(162.88, -74.1) * mm, "end": v(163.14, -75.68) * mm});
            skLineSegment(sketch, "E1340", {"start": v(163.14, -75.68) * mm, "end": v(163.39, -77.27) * mm});
            skLineSegment(sketch, "E1341", {"start": v(163.39, -77.27) * mm, "end": v(163.62, -78.87) * mm});
            skLineSegment(sketch, "E1342", {"start": v(163.62, -78.87) * mm, "end": v(163.83, -80.47) * mm});
            skLineSegment(sketch, "E1343", {"start": v(163.83, -80.47) * mm, "end": v(164.03, -82.08) * mm});
            skLineSegment(sketch, "E1344", {"start": v(164.03, -82.08) * mm, "end": v(164.21, -83.7) * mm});
            skLineSegment(sketch, "E1345", {"start": v(164.21, -83.7) * mm, "end": v(164.38, -85.32) * mm});
            skLineSegment(sketch, "E1346", {"start": v(164.38, -85.32) * mm, "end": v(164.53, -86.94) * mm});
            skLineSegment(sketch, "E1347", {"start": v(164.53, -86.94) * mm, "end": v(164.66, -88.57) * mm});
            skLineSegment(sketch, "E1348", {"start": v(164.66, -88.57) * mm, "end": v(164.77, -90.2) * mm});
            skLineSegment(sketch, "E1349", {"start": v(164.77, -90.2) * mm, "end": v(164.87, -91.84) * mm});
            skLineSegment(sketch, "E1350", {"start": v(164.87, -91.84) * mm, "end": v(164.94, -93.48) * mm});
            skLineSegment(sketch, "E1351", {"start": v(164.94, -93.48) * mm, "end": v(165, -95.13) * mm});
            skLineSegment(sketch, "E1352", {"start": v(165, -95.13) * mm, "end": v(165.05, -96.78) * mm});
            skLineSegment(sketch, "E1353", {"start": v(165.05, -96.78) * mm, "end": v(165.08, -98.44) * mm});
            skLineSegment(sketch, "E1354", {"start": v(165.08, -98.44) * mm, "end": v(165.09, -100.1) * mm});
            skLineSegment(sketch, "E1355", {"start": v(165.09, -100.1) * mm, "end": v(165.07, -101.87) * mm});
            skLineSegment(sketch, "E1356", {"start": v(165.07, -101.87) * mm, "end": v(165.02, -103.7) * mm});
            skLineSegment(sketch, "E1357", {"start": v(165.02, -103.7) * mm, "end": v(164.94, -105.6) * mm});
            skLineSegment(sketch, "E1358", {"start": v(164.94, -105.6) * mm, "end": v(164.83, -107.53) * mm});
            skLineSegment(sketch, "E1359", {"start": v(164.83, -107.53) * mm, "end": v(164.7, -109.48) * mm});
            skLineSegment(sketch, "E1360", {"start": v(164.7, -109.48) * mm, "end": v(164.56, -111.43) * mm});
            skLineSegment(sketch, "E1361", {"start": v(164.56, -111.43) * mm, "end": v(164.4, -113.36) * mm});
            skLineSegment(sketch, "E1362", {"start": v(164.4, -113.36) * mm, "end": v(164.22, -115.26) * mm});
            skLineSegment(sketch, "E1363", {"start": v(164.22, -115.26) * mm, "end": v(163.83, -118.88) * mm});
            skLineSegment(sketch, "E1364", {"start": v(163.83, -118.88) * mm, "end": v(163.44, -122.16) * mm});
            skLineSegment(sketch, "E1365", {"start": v(163.44, -122.16) * mm, "end": v(163.05, -124.95) * mm});
            skLineSegment(sketch, "E1366", {"start": v(163.05, -124.95) * mm, "end": v(162.87, -126.13) * mm});
            skLineSegment(sketch, "E1367", {"start": v(162.87, -126.13) * mm, "end": v(162.7, -127.13) * mm});
            skLineSegment(sketch, "E1368", {"start": v(162.7, -127.13) * mm, "end": v(162.62, -127.84) * mm});
            skLineSegment(sketch, "E1369", {"start": v(162.62, -127.84) * mm, "end": v(162.56, -128.56) * mm});
            skLineSegment(sketch, "E1370", {"start": v(162.56, -128.56) * mm, "end": v(162.53, -129.3) * mm});
            skLineSegment(sketch, "E1371", {"start": v(162.53, -129.3) * mm, "end": v(162.52, -130.04) * mm});
            skLineSegment(sketch, "E1372", {"start": v(162.52, -130.04) * mm, "end": v(162.53, -130.8) * mm});
            skLineSegment(sketch, "E1373", {"start": v(162.53, -130.8) * mm, "end": v(162.55, -131.55) * mm});
            skLineSegment(sketch, "E1374", {"start": v(162.55, -131.55) * mm, "end": v(162.6, -132.31) * mm});
            skLineSegment(sketch, "E1375", {"start": v(162.6, -132.31) * mm, "end": v(162.65, -133.07) * mm});
            skLineSegment(sketch, "E1376", {"start": v(162.65, -133.07) * mm, "end": v(162.81, -134.59) * mm});
            skLineSegment(sketch, "E1377", {"start": v(162.81, -134.59) * mm, "end": v(163.02, -136.07) * mm});
            skLineSegment(sketch, "E1378", {"start": v(163.02, -136.07) * mm, "end": v(163.26, -137.5) * mm});
            skLineSegment(sketch, "E1379", {"start": v(163.26, -137.5) * mm, "end": v(163.52, -138.88) * mm});
            skLineSegment(sketch, "E1380", {"start": v(163.52, -138.88) * mm, "end": v(163.79, -140.16) * mm});
            skLineSegment(sketch, "E1381", {"start": v(163.79, -140.16) * mm, "end": v(164.06, -141.33) * mm});
            skLineSegment(sketch, "E1382", {"start": v(164.06, -141.33) * mm, "end": v(164.32, -142.38) * mm});
            skLineSegment(sketch, "E1383", {"start": v(164.32, -142.38) * mm, "end": v(164.56, -143.28) * mm});
            skLineSegment(sketch, "E1384", {"start": v(164.56, -143.28) * mm, "end": v(164.93, -144.56) * mm});
            skLineSegment(sketch, "E1385", {"start": v(164.93, -144.56) * mm, "end": v(165.07, -145.02) * mm});
            skLineSegment(sketch, "E1386", {"start": v(165.07, -145.02) * mm, "end": v(166, -147.93) * mm});
            skLineSegment(sketch, "E1387", {"start": v(166, -147.93) * mm, "end": v(166.96, -150.82) * mm});
            skLineSegment(sketch, "E1388", {"start": v(166.96, -150.82) * mm, "end": v(167.98, -153.67) * mm});
            skLineSegment(sketch, "E1389", {"start": v(167.98, -153.67) * mm, "end": v(169.06, -156.5) * mm});
            skLineSegment(sketch, "E1390", {"start": v(169.06, -156.5) * mm, "end": v(170.19, -159.3) * mm});
            skLineSegment(sketch, "E1391", {"start": v(170.19, -159.3) * mm, "end": v(171.37, -162.08) * mm});
            skLineSegment(sketch, "E1392", {"start": v(171.37, -162.08) * mm, "end": v(172.6, -164.83) * mm});
            skLineSegment(sketch, "E1393", {"start": v(172.6, -164.83) * mm, "end": v(173.88, -167.55) * mm});
            skLineSegment(sketch, "E1394", {"start": v(173.88, -167.55) * mm, "end": v(175.2, -170.23) * mm});
            skLineSegment(sketch, "E1395", {"start": v(175.2, -170.23) * mm, "end": v(176.58, -172.89) * mm});
            skLineSegment(sketch, "E1396", {"start": v(176.58, -172.89) * mm, "end": v(178, -175.51) * mm});
            skLineSegment(sketch, "E1397", {"start": v(178, -175.51) * mm, "end": v(179.48, -178.1) * mm});
            skLineSegment(sketch, "E1398", {"start": v(179.48, -178.1) * mm, "end": v(181, -180.66) * mm});
            skLineSegment(sketch, "E1399", {"start": v(181, -180.66) * mm, "end": v(182.58, -183.2) * mm});
            skLineSegment(sketch, "E1400", {"start": v(182.58, -183.2) * mm, "end": v(184.2, -185.68) * mm});
            skLineSegment(sketch, "E1401", {"start": v(184.2, -185.68) * mm, "end": v(185.85, -188.14) * mm});
            skLineSegment(sketch, "E1402", {"start": v(185.85, -188.14) * mm, "end": v(187.56, -190.56) * mm});
            skLineSegment(sketch, "E1403", {"start": v(187.56, -190.56) * mm, "end": v(189.3, -192.95) * mm});
            skLineSegment(sketch, "E1404", {"start": v(189.3, -192.95) * mm, "end": v(191.1, -195.3) * mm});
            skLineSegment(sketch, "E1405", {"start": v(191.1, -195.3) * mm, "end": v(192.94, -197.61) * mm});
            skLineSegment(sketch, "E1406", {"start": v(192.94, -197.61) * mm, "end": v(194.82, -199.89) * mm});
            skLineSegment(sketch, "E1407", {"start": v(194.82, -199.89) * mm, "end": v(196.75, -202.12) * mm});
            skLineSegment(sketch, "E1408", {"start": v(196.75, -202.12) * mm, "end": v(198.71, -204.32) * mm});
            skLineSegment(sketch, "E1409", {"start": v(198.71, -204.32) * mm, "end": v(200.72, -206.48) * mm});
            skLineSegment(sketch, "E1410", {"start": v(200.72, -206.48) * mm, "end": v(202.77, -208.6) * mm});
            skLineSegment(sketch, "E1411", {"start": v(202.77, -208.6) * mm, "end": v(204.85, -210.67) * mm});
            skLineSegment(sketch, "E1412", {"start": v(204.85, -210.67) * mm, "end": v(206.98, -212.7) * mm});
            skLineSegment(sketch, "E1413", {"start": v(206.98, -212.7) * mm, "end": v(209.15, -214.7) * mm});
            skLineSegment(sketch, "E1414", {"start": v(209.15, -214.7) * mm, "end": v(211.35, -216.64) * mm});
            skLineSegment(sketch, "E1415", {"start": v(211.35, -216.64) * mm, "end": v(213.6, -218.54) * mm});
            skLineSegment(sketch, "E1416", {"start": v(213.6, -218.54) * mm, "end": v(215.88, -220.4) * mm});
            skLineSegment(sketch, "E1417", {"start": v(215.88, -220.4) * mm, "end": v(218.2, -222.22) * mm});
            skLineSegment(sketch, "E1418", {"start": v(218.2, -222.22) * mm, "end": v(220.55, -223.99) * mm});
            skLineSegment(sketch, "E1419", {"start": v(220.55, -223.99) * mm, "end": v(222.94, -225.71) * mm});
            skLineSegment(sketch, "E1420", {"start": v(222.94, -225.71) * mm, "end": v(225.36, -227.39) * mm});
            skLineSegment(sketch, "E1421", {"start": v(225.36, -227.39) * mm, "end": v(227.82, -229.02) * mm});
            skLineSegment(sketch, "E1422", {"start": v(227.82, -229.02) * mm, "end": v(230.32, -230.6) * mm});
            skLineSegment(sketch, "E1423", {"start": v(230.32, -230.6) * mm, "end": v(232.85, -232.13) * mm});
            skLineSegment(sketch, "E1424", {"start": v(232.85, -232.13) * mm, "end": v(235.4, -233.61) * mm});
            skLineSegment(sketch, "E1425", {"start": v(235.4, -233.61) * mm, "end": v(238, -235.04) * mm});
            skLineSegment(sketch, "E1426", {"start": v(238, -235.04) * mm, "end": v(239.3, -235.74) * mm});
            skLineSegment(sketch, "E1427", {"start": v(239.3, -235.74) * mm, "end": v(240.62, -236.42) * mm});
            skLineSegment(sketch, "E1428", {"start": v(240.62, -236.42) * mm, "end": v(241.95, -237.1) * mm});
            skLineSegment(sketch, "E1429", {"start": v(241.95, -237.1) * mm, "end": v(243.28, -237.75) * mm});
            skLineSegment(sketch, "E1430", {"start": v(243.28, -237.75) * mm, "end": v(244.62, -238.4) * mm});
            skLineSegment(sketch, "E1431", {"start": v(244.62, -238.4) * mm, "end": v(245.97, -239.03) * mm});
            skLineSegment(sketch, "E1432", {"start": v(245.97, -239.03) * mm, "end": v(247.32, -239.65) * mm});
            skLineSegment(sketch, "E1433", {"start": v(247.32, -239.65) * mm, "end": v(248.69, -240.26) * mm});
            skLineSegment(sketch, "E1434", {"start": v(248.69, -240.26) * mm, "end": v(250.06, -240.85) * mm});
            skLineSegment(sketch, "E1435", {"start": v(250.06, -240.85) * mm, "end": v(251.43, -241.43) * mm});
            skLineSegment(sketch, "E1436", {"start": v(251.43, -241.43) * mm, "end": v(252.82, -242) * mm});
            skLineSegment(sketch, "E1437", {"start": v(252.82, -242) * mm, "end": v(254.2, -242.54) * mm});
            skLineSegment(sketch, "E1438", {"start": v(254.2, -242.54) * mm, "end": v(255.6, -243.08) * mm});
            skLineSegment(sketch, "E1439", {"start": v(255.6, -243.08) * mm, "end": v(257.01, -243.6) * mm});
            skLineSegment(sketch, "E1440", {"start": v(257.01, -243.6) * mm, "end": v(258.43, -244.12) * mm});
            skLineSegment(sketch, "E1441", {"start": v(258.43, -244.12) * mm, "end": v(259.85, -244.61) * mm});
            skLineSegment(sketch, "E1442", {"start": v(259.85, -244.61) * mm, "end": v(261.27, -245.1) * mm});
            skLineSegment(sketch, "E1443", {"start": v(261.27, -245.1) * mm, "end": v(262.7, -245.56) * mm});
            skLineSegment(sketch, "E1444", {"start": v(262.7, -245.56) * mm, "end": v(264.15, -246.02) * mm});
            skLineSegment(sketch, "E1445", {"start": v(264.15, -246.02) * mm, "end": v(265.6, -246.46) * mm});
            skLineSegment(sketch, "E1446", {"start": v(265.6, -246.46) * mm, "end": v(267.05, -246.88) * mm});
            skLineSegment(sketch, "E1447", {"start": v(267.05, -246.88) * mm, "end": v(268.5, -247.3) * mm});
            skLineSegment(sketch, "E1448", {"start": v(268.5, -247.3) * mm, "end": v(269.98, -247.7) * mm});
            skLineSegment(sketch, "E1449", {"start": v(269.98, -247.7) * mm, "end": v(271.45, -248.07) * mm});
            skLineSegment(sketch, "E1450", {"start": v(271.45, -248.07) * mm, "end": v(272.93, -248.44) * mm});
            skLineSegment(sketch, "E1451", {"start": v(272.93, -248.44) * mm, "end": v(274.41, -248.8) * mm});
            skLineSegment(sketch, "E1452", {"start": v(274.41, -248.8) * mm, "end": v(275.9, -249.13) * mm});
            skLineSegment(sketch, "E1453", {"start": v(275.9, -249.13) * mm, "end": v(277.4, -249.46) * mm});
            skLineSegment(sketch, "E1454", {"start": v(277.4, -249.46) * mm, "end": v(278.9, -249.76) * mm});
            skLineSegment(sketch, "E1455", {"start": v(278.9, -249.76) * mm, "end": v(280.42, -250.06) * mm});
            skLineSegment(sketch, "E1456", {"start": v(280.42, -250.06) * mm, "end": v(281.94, -250.33) * mm});
            skLineSegment(sketch, "E1457", {"start": v(281.94, -250.33) * mm, "end": v(283.46, -250.6) * mm});
            skLineSegment(sketch, "E1458", {"start": v(283.46, -250.6) * mm, "end": v(284.98, -250.84) * mm});
            skLineSegment(sketch, "E1459", {"start": v(284.98, -250.84) * mm, "end": v(286.52, -251.08) * mm});
            skLineSegment(sketch, "E1460", {"start": v(286.52, -251.08) * mm, "end": v(288.06, -251.3) * mm});
            skLineSegment(sketch, "E1461", {"start": v(288.06, -251.3) * mm, "end": v(289.6, -251.5) * mm});
            skLineSegment(sketch, "E1462", {"start": v(289.6, -251.5) * mm, "end": v(291.15, -251.68) * mm});
            skLineSegment(sketch, "E1463", {"start": v(291.15, -251.68) * mm, "end": v(292.7, -251.85) * mm});
            skLineSegment(sketch, "E1464", {"start": v(292.7, -251.85) * mm, "end": v(294.27, -252) * mm});
            skLineSegment(sketch, "E1465", {"start": v(294.27, -252) * mm, "end": v(295.83, -252.14) * mm});
            skLineSegment(sketch, "E1466", {"start": v(295.83, -252.14) * mm, "end": v(297.4, -252.26) * mm});
            skLineSegment(sketch, "E1467", {"start": v(297.4, -252.26) * mm, "end": v(298.98, -252.37) * mm});
            skLineSegment(sketch, "E1468", {"start": v(298.98, -252.37) * mm, "end": v(300.56, -252.46) * mm});
            skLineSegment(sketch, "E1469", {"start": v(300.56, -252.46) * mm, "end": v(302.15, -252.53) * mm});
            skLineSegment(sketch, "E1470", {"start": v(302.15, -252.53) * mm, "end": v(303.74, -252.6) * mm});
            skLineSegment(sketch, "E1471", {"start": v(303.74, -252.6) * mm, "end": v(305.34, -252.63) * mm});
            skLineSegment(sketch, "E1472", {"start": v(305.34, -252.63) * mm, "end": v(306.94, -252.66) * mm});
            skLineSegment(sketch, "E1473", {"start": v(306.94, -252.66) * mm, "end": v(308.55, -252.67) * mm});
            skLineSegment(sketch, "E1474", {"start": v(308.55, -252.67) * mm, "end": v(310.52, -252.65) * mm});
            skLineSegment(sketch, "E1475", {"start": v(310.52, -252.65) * mm, "end": v(312.48, -252.62) * mm});
            skLineSegment(sketch, "E1476", {"start": v(312.48, -252.62) * mm, "end": v(314.44, -252.55) * mm});
            skLineSegment(sketch, "E1477", {"start": v(314.44, -252.55) * mm, "end": v(316.4, -252.47) * mm});
            skLineSegment(sketch, "E1478", {"start": v(316.4, -252.47) * mm, "end": v(318.34, -252.36) * mm});
            skLineSegment(sketch, "E1479", {"start": v(318.34, -252.36) * mm, "end": v(320.28, -252.22) * mm});
            skLineSegment(sketch, "E1480", {"start": v(320.28, -252.22) * mm, "end": v(322.22, -252.06) * mm});
            skLineSegment(sketch, "E1481", {"start": v(322.22, -252.06) * mm, "end": v(324.15, -251.88) * mm});
            skLineSegment(sketch, "E1482", {"start": v(324.15, -251.88) * mm, "end": v(326.06, -251.67) * mm});
            skLineSegment(sketch, "E1483", {"start": v(326.06, -251.67) * mm, "end": v(327.98, -251.44) * mm});
            skLineSegment(sketch, "E1484", {"start": v(327.98, -251.44) * mm, "end": v(329.88, -251.19) * mm});
            skLineSegment(sketch, "E1485", {"start": v(329.88, -251.19) * mm, "end": v(331.78, -250.9) * mm});
            skLineSegment(sketch, "E1486", {"start": v(331.78, -250.9) * mm, "end": v(333.67, -250.6) * mm});
            skLineSegment(sketch, "E1487", {"start": v(333.67, -250.6) * mm, "end": v(335.55, -250.28) * mm});
            skLineSegment(sketch, "E1488", {"start": v(335.55, -250.28) * mm, "end": v(337.43, -249.94) * mm});
            skLineSegment(sketch, "E1489", {"start": v(337.43, -249.94) * mm, "end": v(339.3, -249.57) * mm});
            skLineSegment(sketch, "E1490", {"start": v(339.3, -249.57) * mm, "end": v(341.15, -249.17) * mm});
            skLineSegment(sketch, "E1491", {"start": v(341.15, -249.17) * mm, "end": v(343, -248.76) * mm});
            skLineSegment(sketch, "E1492", {"start": v(343, -248.76) * mm, "end": v(344.84, -248.32) * mm});
            skLineSegment(sketch, "E1493", {"start": v(344.84, -248.32) * mm, "end": v(346.67, -247.86) * mm});
            skLineSegment(sketch, "E1494", {"start": v(346.67, -247.86) * mm, "end": v(348.5, -247.38) * mm});
            skLineSegment(sketch, "E1495", {"start": v(348.5, -247.38) * mm, "end": v(350.31, -246.88) * mm});
            skLineSegment(sketch, "E1496", {"start": v(350.31, -246.88) * mm, "end": v(352.12, -246.35) * mm});
            skLineSegment(sketch, "E1497", {"start": v(352.12, -246.35) * mm, "end": v(353.91, -245.8) * mm});
            skLineSegment(sketch, "E1498", {"start": v(353.91, -245.8) * mm, "end": v(355.7, -245.24) * mm});
            skLineSegment(sketch, "E1499", {"start": v(355.7, -245.24) * mm, "end": v(357.48, -244.65) * mm});
            skLineSegment(sketch, "E1500", {"start": v(357.48, -244.65) * mm, "end": v(359.25, -244.04) * mm});
            skLineSegment(sketch, "E1501", {"start": v(359.25, -244.04) * mm, "end": v(361, -243.4) * mm});
            skLineSegment(sketch, "E1502", {"start": v(361, -243.4) * mm, "end": v(362.75, -242.76) * mm});
            skLineSegment(sketch, "E1503", {"start": v(362.75, -242.76) * mm, "end": v(364.49, -242.08) * mm});
            skLineSegment(sketch, "E1504", {"start": v(364.49, -242.08) * mm, "end": v(366.22, -241.4) * mm});
            skLineSegment(sketch, "E1505", {"start": v(366.22, -241.4) * mm, "end": v(367.93, -240.68) * mm});
            skLineSegment(sketch, "E1506", {"start": v(367.93, -240.68) * mm, "end": v(369.64, -239.94) * mm});
            skLineSegment(sketch, "E1507", {"start": v(369.64, -239.94) * mm, "end": v(371.33, -239.19) * mm});
            skLineSegment(sketch, "E1508", {"start": v(371.33, -239.19) * mm, "end": v(373.02, -238.41) * mm});
            skLineSegment(sketch, "E1509", {"start": v(373.02, -238.41) * mm, "end": v(374.69, -237.62) * mm});
            skLineSegment(sketch, "E1510", {"start": v(374.69, -237.62) * mm, "end": v(376.35, -236.8) * mm});
            skLineSegment(sketch, "E1511", {"start": v(376.35, -236.8) * mm, "end": v(378, -235.98) * mm});
            skLineSegment(sketch, "E1512", {"start": v(378, -235.98) * mm, "end": v(379.64, -235.12) * mm});
            skLineSegment(sketch, "E1513", {"start": v(379.64, -235.12) * mm, "end": v(381.27, -234.25) * mm});
            skLineSegment(sketch, "E1514", {"start": v(381.27, -234.25) * mm, "end": v(382.88, -233.36) * mm});
            skLineSegment(sketch, "E1515", {"start": v(382.88, -233.36) * mm, "end": v(384.49, -232.45) * mm});
            skLineSegment(sketch, "E1516", {"start": v(384.49, -232.45) * mm, "end": v(386.08, -231.52) * mm});
            skLineSegment(sketch, "E1517", {"start": v(386.08, -231.52) * mm, "end": v(387.66, -230.58) * mm});
            skLineSegment(sketch, "E1518", {"start": v(387.66, -230.58) * mm, "end": v(389.22, -229.61) * mm});
            skLineSegment(sketch, "E1519", {"start": v(389.22, -229.61) * mm, "end": v(390.78, -228.63) * mm});
            skLineSegment(sketch, "E1520", {"start": v(390.78, -228.63) * mm, "end": v(392.32, -227.63) * mm});
            skLineSegment(sketch, "E1521", {"start": v(392.32, -227.63) * mm, "end": v(393.85, -226.61) * mm});
            skLineSegment(sketch, "E1522", {"start": v(393.85, -226.61) * mm, "end": v(395.36, -225.57) * mm});
            skLineSegment(sketch, "E1523", {"start": v(395.36, -225.57) * mm, "end": v(396.87, -224.52) * mm});
            skLineSegment(sketch, "E1524", {"start": v(396.87, -224.52) * mm, "end": v(398.35, -223.45) * mm});
            skLineSegment(sketch, "E1525", {"start": v(398.35, -223.45) * mm, "end": v(399.83, -222.36) * mm});
            skLineSegment(sketch, "E1526", {"start": v(399.83, -222.36) * mm, "end": v(401.3, -221.25) * mm});
            skLineSegment(sketch, "E1527", {"start": v(401.3, -221.25) * mm, "end": v(402.74, -220.13) * mm});
            skLineSegment(sketch, "E1528", {"start": v(402.74, -220.13) * mm, "end": v(404.17, -218.98) * mm});
            skLineSegment(sketch, "E1529", {"start": v(404.17, -218.98) * mm, "end": v(405.6, -217.83) * mm});
            skLineSegment(sketch, "E1530", {"start": v(405.6, -217.83) * mm, "end": v(407, -216.65) * mm});
            skLineSegment(sketch, "E1531", {"start": v(407, -216.65) * mm, "end": v(408.39, -215.46) * mm});
            skLineSegment(sketch, "E1532", {"start": v(408.39, -215.46) * mm, "end": v(409.77, -214.26) * mm});
            skLineSegment(sketch, "E1533", {"start": v(409.77, -214.26) * mm, "end": v(411.13, -213.03) * mm});
            skLineSegment(sketch, "E1534", {"start": v(411.13, -213.03) * mm, "end": v(412.48, -211.8) * mm});
            skLineSegment(sketch, "E1535", {"start": v(412.48, -211.8) * mm, "end": v(413.8, -210.54) * mm});
            skLineSegment(sketch, "E1536", {"start": v(413.8, -210.54) * mm, "end": v(415.13, -209.27) * mm});
            skLineSegment(sketch, "E1537", {"start": v(415.13, -209.27) * mm, "end": v(416.43, -207.98) * mm});
            skLineSegment(sketch, "E1538", {"start": v(416.43, -207.98) * mm, "end": v(417.71, -206.68) * mm});
            skLineSegment(sketch, "E1539", {"start": v(417.71, -206.68) * mm, "end": v(418.98, -205.36) * mm});
            skLineSegment(sketch, "E1540", {"start": v(418.98, -205.36) * mm, "end": v(420.24, -204.03) * mm});
            skLineSegment(sketch, "E1541", {"start": v(420.24, -204.03) * mm, "end": v(421.48, -202.68) * mm});
            skLineSegment(sketch, "E1542", {"start": v(421.48, -202.68) * mm, "end": v(422.7, -201.32) * mm});
            skLineSegment(sketch, "E1543", {"start": v(422.7, -201.32) * mm, "end": v(423.9, -199.94) * mm});
            skLineSegment(sketch, "E1544", {"start": v(423.9, -199.94) * mm, "end": v(425.1, -198.55) * mm});
            skLineSegment(sketch, "E1545", {"start": v(425.1, -198.55) * mm, "end": v(426.27, -197.15) * mm});
            skLineSegment(sketch, "E1546", {"start": v(426.27, -197.15) * mm, "end": v(427.43, -195.73) * mm});
            skLineSegment(sketch, "E1547", {"start": v(427.43, -195.73) * mm, "end": v(428.57, -194.3) * mm});
            skLineSegment(sketch, "E1548", {"start": v(428.57, -194.3) * mm, "end": v(429.7, -192.84) * mm});
            skLineSegment(sketch, "E1549", {"start": v(429.7, -192.84) * mm, "end": v(430.8, -191.38) * mm});
            skLineSegment(sketch, "E1550", {"start": v(430.8, -191.38) * mm, "end": v(431.9, -189.9) * mm});
            skLineSegment(sketch, "E1551", {"start": v(431.9, -189.9) * mm, "end": v(432.97, -188.42) * mm});
            skLineSegment(sketch, "E1552", {"start": v(432.97, -188.42) * mm, "end": v(434.02, -186.92) * mm});
            skLineSegment(sketch, "E1553", {"start": v(434.02, -186.92) * mm, "end": v(435.06, -185.4) * mm});
            skLineSegment(sketch, "E1554", {"start": v(435.06, -185.4) * mm, "end": v(436.08, -183.87) * mm});
            skLineSegment(sketch, "E1555", {"start": v(436.08, -183.87) * mm, "end": v(437.08, -182.33) * mm});
            skLineSegment(sketch, "E1556", {"start": v(437.08, -182.33) * mm, "end": v(438.06, -180.78) * mm});
            skLineSegment(sketch, "E1557", {"start": v(438.06, -180.78) * mm, "end": v(439.03, -179.21) * mm});
            skLineSegment(sketch, "E1558", {"start": v(439.03, -179.21) * mm, "end": v(439.97, -177.63) * mm});
            skLineSegment(sketch, "E1559", {"start": v(439.97, -177.63) * mm, "end": v(440.9, -176.04) * mm});
            skLineSegment(sketch, "E1560", {"start": v(440.9, -176.04) * mm, "end": v(441.8, -174.44) * mm});
            skLineSegment(sketch, "E1561", {"start": v(441.8, -174.44) * mm, "end": v(442.7, -172.82) * mm});
            skLineSegment(sketch, "E1562", {"start": v(442.7, -172.82) * mm, "end": v(443.57, -171.2) * mm});
            skLineSegment(sketch, "E1563", {"start": v(443.57, -171.2) * mm, "end": v(444.42, -169.56) * mm});
            skLineSegment(sketch, "E1564", {"start": v(444.42, -169.56) * mm, "end": v(445.26, -167.9) * mm});
            skLineSegment(sketch, "E1565", {"start": v(445.26, -167.9) * mm, "end": v(446.07, -166.24) * mm});
            skLineSegment(sketch, "E1566", {"start": v(446.07, -166.24) * mm, "end": v(446.86, -164.57) * mm});
            skLineSegment(sketch, "E1567", {"start": v(446.86, -164.57) * mm, "end": v(447.64, -162.89) * mm});
            skLineSegment(sketch, "E1568", {"start": v(447.64, -162.89) * mm, "end": v(448.4, -161.2) * mm});
            skLineSegment(sketch, "E1569", {"start": v(448.4, -161.2) * mm, "end": v(449.12, -159.48) * mm});
            skLineSegment(sketch, "E1570", {"start": v(449.12, -159.48) * mm, "end": v(449.84, -157.77) * mm});
            skLineSegment(sketch, "E1571", {"start": v(449.84, -157.77) * mm, "end": v(450.53, -156.04) * mm});
            skLineSegment(sketch, "E1572", {"start": v(450.53, -156.04) * mm, "end": v(451.2, -154.3) * mm});
            skLineSegment(sketch, "E1573", {"start": v(451.2, -154.3) * mm, "end": v(451.86, -152.56) * mm});
            skLineSegment(sketch, "E1574", {"start": v(451.86, -152.56) * mm, "end": v(452.49, -150.8) * mm});
            skLineSegment(sketch, "E1575", {"start": v(452.49, -150.8) * mm, "end": v(453.1, -149.03) * mm});
            skLineSegment(sketch, "E1576", {"start": v(453.1, -149.03) * mm, "end": v(453.69, -147.25) * mm});
            skLineSegment(sketch, "E1577", {"start": v(453.69, -147.25) * mm, "end": v(454.25, -145.47) * mm});
            skLineSegment(sketch, "E1578", {"start": v(454.25, -145.47) * mm, "end": v(454.8, -143.67) * mm});
            skLineSegment(sketch, "E1579", {"start": v(454.8, -143.67) * mm, "end": v(455.33, -141.87) * mm});
            skLineSegment(sketch, "E1580", {"start": v(455.33, -141.87) * mm, "end": v(455.83, -140.05) * mm});
            skLineSegment(sketch, "E1581", {"start": v(455.83, -140.05) * mm, "end": v(456.31, -138.23) * mm});
            skLineSegment(sketch, "E1582", {"start": v(456.31, -138.23) * mm, "end": v(456.77, -136.4) * mm});
            skLineSegment(sketch, "E1583", {"start": v(456.77, -136.4) * mm, "end": v(457.2, -134.55) * mm});
            skLineSegment(sketch, "E1584", {"start": v(457.2, -134.55) * mm, "end": v(457.62, -132.7) * mm});
            skLineSegment(sketch, "E1585", {"start": v(457.62, -132.7) * mm, "end": v(458.01, -130.85) * mm});
            skLineSegment(sketch, "E1586", {"start": v(458.01, -130.85) * mm, "end": v(458.38, -128.98) * mm});
            skLineSegment(sketch, "E1587", {"start": v(458.38, -128.98) * mm, "end": v(458.73, -127.1) * mm});
            skLineSegment(sketch, "E1588", {"start": v(458.73, -127.1) * mm, "end": v(459.05, -125.22) * mm});
            skLineSegment(sketch, "E1589", {"start": v(459.05, -125.22) * mm, "end": v(459.36, -123.33) * mm});
            skLineSegment(sketch, "E1590", {"start": v(459.36, -123.33) * mm, "end": v(459.63, -121.44) * mm});
            skLineSegment(sketch, "E1591", {"start": v(459.63, -121.44) * mm, "end": v(459.89, -119.53) * mm});
            skLineSegment(sketch, "E1592", {"start": v(459.89, -119.53) * mm, "end": v(460.12, -117.62) * mm});
            skLineSegment(sketch, "E1593", {"start": v(460.12, -117.62) * mm, "end": v(460.33, -115.7) * mm});
            skLineSegment(sketch, "E1594", {"start": v(460.33, -115.7) * mm, "end": v(460.5, -113.77) * mm});
            skLineSegment(sketch, "E1595", {"start": v(460.5, -113.77) * mm, "end": v(460.67, -111.84) * mm});
            skLineSegment(sketch, "E1596", {"start": v(460.67, -111.84) * mm, "end": v(460.8, -109.9) * mm});
            skLineSegment(sketch, "E1597", {"start": v(460.8, -109.9) * mm, "end": v(460.92, -107.95) * mm});
            skLineSegment(sketch, "E1598", {"start": v(460.92, -107.95) * mm, "end": v(461, -106) * mm});
            skLineSegment(sketch, "E1599", {"start": v(461, -106) * mm, "end": v(461.06, -104.04) * mm});
            skLineSegment(sketch, "E1600", {"start": v(461.06, -104.04) * mm, "end": v(461.1, -102.07) * mm});
            skLineSegment(sketch, "E1601", {"start": v(461.1, -102.07) * mm, "end": v(461.11, -100.1) * mm});
            skLineSegment(sketch, "E1602", {"start": v(461.11, -100.1) * mm, "end": v(461.11, 318.48) * mm});
            skLineSegment(sketch, "E1603", {"start": v(461.11, 318.48) * mm, "end": v(461.1, 320.45) * mm});
            skLineSegment(sketch, "E1604", {"start": v(461.1, 320.45) * mm, "end": v(461.06, 322.41) * mm});
            skLineSegment(sketch, "E1605", {"start": v(461.06, 322.41) * mm, "end": v(461, 324.37) * mm});
            skLineSegment(sketch, "E1606", {"start": v(461, 324.37) * mm, "end": v(460.92, 326.33) * mm});
            skLineSegment(sketch, "E1607", {"start": v(460.92, 326.33) * mm, "end": v(460.8, 328.27) * mm});
            skLineSegment(sketch, "E1608", {"start": v(460.8, 328.27) * mm, "end": v(460.67, 330.21) * mm});
            skLineSegment(sketch, "E1609", {"start": v(460.67, 330.21) * mm, "end": v(460.5, 332.15) * mm});
            skLineSegment(sketch, "E1610", {"start": v(460.5, 332.15) * mm, "end": v(460.33, 334.07) * mm});
            skLineSegment(sketch, "E1611", {"start": v(460.33, 334.07) * mm, "end": v(460.12, 336) * mm});
            skLineSegment(sketch, "E1612", {"start": v(460.12, 336) * mm, "end": v(459.89, 337.9) * mm});
            skLineSegment(sketch, "E1613", {"start": v(459.89, 337.9) * mm, "end": v(459.63, 339.81) * mm});
            skLineSegment(sketch, "E1614", {"start": v(459.63, 339.81) * mm, "end": v(459.36, 341.71) * mm});
            skLineSegment(sketch, "E1615", {"start": v(459.36, 341.71) * mm, "end": v(459.05, 343.6) * mm});
            skLineSegment(sketch, "E1616", {"start": v(459.05, 343.6) * mm, "end": v(458.73, 345.48) * mm});
            skLineSegment(sketch, "E1617", {"start": v(458.73, 345.48) * mm, "end": v(458.38, 347.36) * mm});
            skLineSegment(sketch, "E1618", {"start": v(458.38, 347.36) * mm, "end": v(458.01, 349.22) * mm});
            skLineSegment(sketch, "E1619", {"start": v(458.01, 349.22) * mm, "end": v(457.62, 351.08) * mm});
            skLineSegment(sketch, "E1620", {"start": v(457.62, 351.08) * mm, "end": v(457.2, 352.93) * mm});
            skLineSegment(sketch, "E1621", {"start": v(457.2, 352.93) * mm, "end": v(456.77, 354.77) * mm});
            skLineSegment(sketch, "E1622", {"start": v(456.77, 354.77) * mm, "end": v(456.31, 356.6) * mm});
            skLineSegment(sketch, "E1623", {"start": v(456.31, 356.6) * mm, "end": v(455.83, 358.43) * mm});
            skLineSegment(sketch, "E1624", {"start": v(455.83, 358.43) * mm, "end": v(455.33, 360.24) * mm});
            skLineSegment(sketch, "E1625", {"start": v(455.33, 360.24) * mm, "end": v(454.8, 362.05) * mm});
            skLineSegment(sketch, "E1626", {"start": v(454.8, 362.05) * mm, "end": v(454.25, 363.84) * mm});
            skLineSegment(sketch, "E1627", {"start": v(454.25, 363.84) * mm, "end": v(453.69, 365.63) * mm});
            skLineSegment(sketch, "E1628", {"start": v(453.69, 365.63) * mm, "end": v(453.1, 367.4) * mm});
            skLineSegment(sketch, "E1629", {"start": v(453.1, 367.4) * mm, "end": v(452.49, 369.18) * mm});
            skLineSegment(sketch, "E1630", {"start": v(452.49, 369.18) * mm, "end": v(451.86, 370.93) * mm});
            skLineSegment(sketch, "E1631", {"start": v(451.86, 370.93) * mm, "end": v(451.2, 372.68) * mm});
            skLineSegment(sketch, "E1632", {"start": v(451.2, 372.68) * mm, "end": v(450.53, 374.42) * mm});
            skLineSegment(sketch, "E1633", {"start": v(450.53, 374.42) * mm, "end": v(449.84, 376.15) * mm});
            skLineSegment(sketch, "E1634", {"start": v(449.84, 376.15) * mm, "end": v(449.12, 377.86) * mm});
            skLineSegment(sketch, "E1635", {"start": v(449.12, 377.86) * mm, "end": v(448.4, 379.57) * mm});
            skLineSegment(sketch, "E1636", {"start": v(448.4, 379.57) * mm, "end": v(447.64, 381.26) * mm});
            skLineSegment(sketch, "E1637", {"start": v(447.64, 381.26) * mm, "end": v(446.86, 382.95) * mm});
            skLineSegment(sketch, "E1638", {"start": v(446.86, 382.95) * mm, "end": v(446.07, 384.62) * mm});
            skLineSegment(sketch, "E1639", {"start": v(446.07, 384.62) * mm, "end": v(445.26, 386.28) * mm});
            skLineSegment(sketch, "E1640", {"start": v(445.26, 386.28) * mm, "end": v(444.42, 387.93) * mm});
            skLineSegment(sketch, "E1641", {"start": v(444.42, 387.93) * mm, "end": v(443.57, 389.57) * mm});
            skLineSegment(sketch, "E1642", {"start": v(443.57, 389.57) * mm, "end": v(442.7, 391.2) * mm});
            skLineSegment(sketch, "E1643", {"start": v(442.7, 391.2) * mm, "end": v(441.8, 392.81) * mm});
            skLineSegment(sketch, "E1644", {"start": v(441.8, 392.81) * mm, "end": v(440.9, 394.42) * mm});
            skLineSegment(sketch, "E1645", {"start": v(440.9, 394.42) * mm, "end": v(439.97, 396) * mm});
            skLineSegment(sketch, "E1646", {"start": v(439.97, 396) * mm, "end": v(439.03, 397.59) * mm});
            skLineSegment(sketch, "E1647", {"start": v(439.03, 397.59) * mm, "end": v(438.06, 399.15) * mm});
            skLineSegment(sketch, "E1648", {"start": v(438.06, 399.15) * mm, "end": v(437.08, 400.7) * mm});
            skLineSegment(sketch, "E1649", {"start": v(437.08, 400.7) * mm, "end": v(436.08, 402.25) * mm});
            skLineSegment(sketch, "E1650", {"start": v(436.08, 402.25) * mm, "end": v(435.06, 403.78) * mm});
            skLineSegment(sketch, "E1651", {"start": v(435.06, 403.78) * mm, "end": v(434.02, 405.3) * mm});
            skLineSegment(sketch, "E1652", {"start": v(434.02, 405.3) * mm, "end": v(432.97, 406.8) * mm});
            skLineSegment(sketch, "E1653", {"start": v(432.97, 406.8) * mm, "end": v(431.9, 408.28) * mm});
            skLineSegment(sketch, "E1654", {"start": v(431.9, 408.28) * mm, "end": v(430.8, 409.76) * mm});
            skLineSegment(sketch, "E1655", {"start": v(430.8, 409.76) * mm, "end": v(429.7, 411.22) * mm});
            skLineSegment(sketch, "E1656", {"start": v(429.7, 411.22) * mm, "end": v(428.57, 412.67) * mm});
            skLineSegment(sketch, "E1657", {"start": v(428.57, 412.67) * mm, "end": v(427.43, 414.1) * mm});
            skLineSegment(sketch, "E1658", {"start": v(427.43, 414.1) * mm, "end": v(426.27, 415.52) * mm});
            skLineSegment(sketch, "E1659", {"start": v(426.27, 415.52) * mm, "end": v(425.1, 416.93) * mm});
            skLineSegment(sketch, "E1660", {"start": v(425.1, 416.93) * mm, "end": v(423.9, 418.32) * mm});
            skLineSegment(sketch, "E1661", {"start": v(423.9, 418.32) * mm, "end": v(422.7, 419.7) * mm});
            skLineSegment(sketch, "E1662", {"start": v(422.7, 419.7) * mm, "end": v(421.48, 421.06) * mm});
            skLineSegment(sketch, "E1663", {"start": v(421.48, 421.06) * mm, "end": v(420.24, 422.4) * mm});
            skLineSegment(sketch, "E1664", {"start": v(420.24, 422.4) * mm, "end": v(418.98, 423.74) * mm});
            skLineSegment(sketch, "E1665", {"start": v(418.98, 423.74) * mm, "end": v(417.71, 425.06) * mm});
            skLineSegment(sketch, "E1666", {"start": v(417.71, 425.06) * mm, "end": v(416.43, 426.36) * mm});
            skLineSegment(sketch, "E1667", {"start": v(416.43, 426.36) * mm, "end": v(415.13, 427.64) * mm});
            skLineSegment(sketch, "E1668", {"start": v(415.13, 427.64) * mm, "end": v(413.8, 428.91) * mm});
            skLineSegment(sketch, "E1669", {"start": v(413.8, 428.91) * mm, "end": v(412.48, 430.17) * mm});
            skLineSegment(sketch, "E1670", {"start": v(412.48, 430.17) * mm, "end": v(411.13, 431.4) * mm});
            skLineSegment(sketch, "E1671", {"start": v(411.13, 431.4) * mm, "end": v(409.77, 432.63) * mm});
            skLineSegment(sketch, "E1672", {"start": v(409.77, 432.63) * mm, "end": v(408.39, 433.84) * mm});
            skLineSegment(sketch, "E1673", {"start": v(408.39, 433.84) * mm, "end": v(407, 435.03) * mm});
            skLineSegment(sketch, "E1674", {"start": v(407, 435.03) * mm, "end": v(405.6, 436.2) * mm});
            skLineSegment(sketch, "E1675", {"start": v(405.6, 436.2) * mm, "end": v(404.17, 437.36) * mm});
            skLineSegment(sketch, "E1676", {"start": v(404.17, 437.36) * mm, "end": v(402.74, 438.5) * mm});
            skLineSegment(sketch, "E1677", {"start": v(402.74, 438.5) * mm, "end": v(401.3, 439.63) * mm});
            skLineSegment(sketch, "E1678", {"start": v(401.3, 439.63) * mm, "end": v(399.83, 440.73) * mm});
            skLineSegment(sketch, "E1679", {"start": v(399.83, 440.73) * mm, "end": v(398.35, 441.82) * mm});
            skLineSegment(sketch, "E1680", {"start": v(398.35, 441.82) * mm, "end": v(396.87, 442.9) * mm});
            skLineSegment(sketch, "E1681", {"start": v(396.87, 442.9) * mm, "end": v(395.36, 443.95) * mm});
            skLineSegment(sketch, "E1682", {"start": v(395.36, 443.95) * mm, "end": v(393.85, 444.99) * mm});
            skLineSegment(sketch, "E1683", {"start": v(393.85, 444.99) * mm, "end": v(392.32, 446) * mm});
            skLineSegment(sketch, "E1684", {"start": v(392.32, 446) * mm, "end": v(390.78, 447) * mm});
            skLineSegment(sketch, "E1685", {"start": v(390.78, 447) * mm, "end": v(389.22, 448) * mm});
            skLineSegment(sketch, "E1686", {"start": v(389.22, 448) * mm, "end": v(387.66, 448.96) * mm});
            skLineSegment(sketch, "E1687", {"start": v(387.66, 448.96) * mm, "end": v(386.08, 449.9) * mm});
            skLineSegment(sketch, "E1688", {"start": v(386.08, 449.9) * mm, "end": v(384.49, 450.83) * mm});
            skLineSegment(sketch, "E1689", {"start": v(384.49, 450.83) * mm, "end": v(382.88, 451.74) * mm});
            skLineSegment(sketch, "E1690", {"start": v(382.88, 451.74) * mm, "end": v(381.27, 452.63) * mm});
            skLineSegment(sketch, "E1691", {"start": v(381.27, 452.63) * mm, "end": v(379.64, 453.5) * mm});
            skLineSegment(sketch, "E1692", {"start": v(379.64, 453.5) * mm, "end": v(378, 454.35) * mm});
            skLineSegment(sketch, "E1693", {"start": v(378, 454.35) * mm, "end": v(376.35, 455.19) * mm});
            skLineSegment(sketch, "E1694", {"start": v(376.35, 455.19) * mm, "end": v(374.69, 456) * mm});
            skLineSegment(sketch, "E1695", {"start": v(374.69, 456) * mm, "end": v(373.02, 456.8) * mm});
            skLineSegment(sketch, "E1696", {"start": v(373.02, 456.8) * mm, "end": v(371.33, 457.57) * mm});
            skLineSegment(sketch, "E1697", {"start": v(371.33, 457.57) * mm, "end": v(369.64, 458.32) * mm});
            skLineSegment(sketch, "E1698", {"start": v(369.64, 458.32) * mm, "end": v(367.93, 459.05) * mm});
            skLineSegment(sketch, "E1699", {"start": v(367.93, 459.05) * mm, "end": v(366.22, 459.77) * mm});
            skLineSegment(sketch, "E1700", {"start": v(366.22, 459.77) * mm, "end": v(364.49, 460.46) * mm});
            skLineSegment(sketch, "E1701", {"start": v(364.49, 460.46) * mm, "end": v(362.75, 461.13) * mm});
            skLineSegment(sketch, "E1702", {"start": v(362.75, 461.13) * mm, "end": v(361, 461.79) * mm});
            skLineSegment(sketch, "E1703", {"start": v(361, 461.79) * mm, "end": v(359.25, 462.42) * mm});
            skLineSegment(sketch, "E1704", {"start": v(359.25, 462.42) * mm, "end": v(357.48, 463.03) * mm});
            skLineSegment(sketch, "E1705", {"start": v(357.48, 463.03) * mm, "end": v(355.7, 463.62) * mm});
            skLineSegment(sketch, "E1706", {"start": v(355.7, 463.62) * mm, "end": v(353.91, 464.18) * mm});
            skLineSegment(sketch, "E1707", {"start": v(353.91, 464.18) * mm, "end": v(352.12, 464.73) * mm});
            skLineSegment(sketch, "E1708", {"start": v(352.12, 464.73) * mm, "end": v(350.31, 465.26) * mm});
            skLineSegment(sketch, "E1709", {"start": v(350.31, 465.26) * mm, "end": v(348.5, 465.76) * mm});
            skLineSegment(sketch, "E1710", {"start": v(348.5, 465.76) * mm, "end": v(346.67, 466.24) * mm});
            skLineSegment(sketch, "E1711", {"start": v(346.67, 466.24) * mm, "end": v(344.84, 466.7) * mm});
            skLineSegment(sketch, "E1712", {"start": v(344.84, 466.7) * mm, "end": v(343, 467.14) * mm});
            skLineSegment(sketch, "E1713", {"start": v(343, 467.14) * mm, "end": v(341.15, 467.55) * mm});
            skLineSegment(sketch, "E1714", {"start": v(341.15, 467.55) * mm, "end": v(339.3, 467.94) * mm});
            skLineSegment(sketch, "E1715", {"start": v(339.3, 467.94) * mm, "end": v(337.43, 468.31) * mm});
            skLineSegment(sketch, "E1716", {"start": v(337.43, 468.31) * mm, "end": v(335.55, 468.66) * mm});
            skLineSegment(sketch, "E1717", {"start": v(335.55, 468.66) * mm, "end": v(333.67, 468.98) * mm});
            skLineSegment(sketch, "E1718", {"start": v(333.67, 468.98) * mm, "end": v(331.78, 469.29) * mm});
            skLineSegment(sketch, "E1719", {"start": v(331.78, 469.29) * mm, "end": v(329.88, 469.56) * mm});
            skLineSegment(sketch, "E1720", {"start": v(329.88, 469.56) * mm, "end": v(327.98, 469.82) * mm});
            skLineSegment(sketch, "E1721", {"start": v(327.98, 469.82) * mm, "end": v(326.06, 470.05) * mm});
            skLineSegment(sketch, "E1722", {"start": v(326.06, 470.05) * mm, "end": v(324.15, 470.26) * mm});
            skLineSegment(sketch, "E1723", {"start": v(324.15, 470.26) * mm, "end": v(322.22, 470.44) * mm});
            skLineSegment(sketch, "E1724", {"start": v(322.22, 470.44) * mm, "end": v(320.28, 470.6) * mm});
            skLineSegment(sketch, "E1725", {"start": v(320.28, 470.6) * mm, "end": v(318.34, 470.73) * mm});
            skLineSegment(sketch, "E1726", {"start": v(318.34, 470.73) * mm, "end": v(316.4, 470.85) * mm});
            skLineSegment(sketch, "E1727", {"start": v(316.4, 470.85) * mm, "end": v(314.44, 470.93) * mm});
            skLineSegment(sketch, "E1728", {"start": v(314.44, 470.93) * mm, "end": v(312.48, 471) * mm});
            skLineSegment(sketch, "E1729", {"start": v(312.48, 471) * mm, "end": v(310.52, 471.03) * mm});
            skLineSegment(sketch, "E1730", {"start": v(310.52, 471.03) * mm, "end": v(308.55, 471.04) * mm});
            skLineSegment(sketch, "E1731", {"start": v(123.58, -6.08) * mm, "end": v(-181.56, 412.49) * mm});
            skLineSegment(sketch, "E1732", {"start": v(-181.56, 412.49) * mm, "end": v(-182.88, 414.15) * mm});
            skLineSegment(sketch, "E1733", {"start": v(-182.88, 414.15) * mm, "end": v(-184.22, 415.8) * mm});
            skLineSegment(sketch, "E1734", {"start": v(-184.22, 415.8) * mm, "end": v(-185.58, 417.42) * mm});
            skLineSegment(sketch, "E1735", {"start": v(-185.58, 417.42) * mm, "end": v(-186.97, 419.02) * mm});
            skLineSegment(sketch, "E1736", {"start": v(-186.97, 419.02) * mm, "end": v(-188.38, 420.6) * mm});
            skLineSegment(sketch, "E1737", {"start": v(-188.38, 420.6) * mm, "end": v(-189.81, 422.17) * mm});
            skLineSegment(sketch, "E1738", {"start": v(-189.81, 422.17) * mm, "end": v(-191.26, 423.71) * mm});
            skLineSegment(sketch, "E1739", {"start": v(-191.26, 423.71) * mm, "end": v(-192.74, 425.24) * mm});
            skLineSegment(sketch, "E1740", {"start": v(-192.74, 425.24) * mm, "end": v(-194.23, 426.74) * mm});
            skLineSegment(sketch, "E1741", {"start": v(-194.23, 426.74) * mm, "end": v(-195.74, 428.23) * mm});
            skLineSegment(sketch, "E1742", {"start": v(-195.74, 428.23) * mm, "end": v(-197.28, 429.69) * mm});
            skLineSegment(sketch, "E1743", {"start": v(-197.28, 429.69) * mm, "end": v(-198.83, 431.13) * mm});
            skLineSegment(sketch, "E1744", {"start": v(-198.83, 431.13) * mm, "end": v(-200.4, 432.55) * mm});
            skLineSegment(sketch, "E1745", {"start": v(-200.4, 432.55) * mm, "end": v(-202, 433.95) * mm});
            skLineSegment(sketch, "E1746", {"start": v(-202, 433.95) * mm, "end": v(-203.62, 435.32) * mm});
            skLineSegment(sketch, "E1747", {"start": v(-203.62, 435.32) * mm, "end": v(-205.25, 436.68) * mm});
            skLineSegment(sketch, "E1748", {"start": v(-205.25, 436.68) * mm, "end": v(-206.9, 438) * mm});
            skLineSegment(sketch, "E1749", {"start": v(-206.9, 438) * mm, "end": v(-208.58, 439.32) * mm});
            skLineSegment(sketch, "E1750", {"start": v(-208.58, 439.32) * mm, "end": v(-210.26, 440.6) * mm});
            skLineSegment(sketch, "E1751", {"start": v(-210.26, 440.6) * mm, "end": v(-211.97, 441.86) * mm});
            skLineSegment(sketch, "E1752", {"start": v(-211.97, 441.86) * mm, "end": v(-213.7, 443.1) * mm});
            skLineSegment(sketch, "E1753", {"start": v(-213.7, 443.1) * mm, "end": v(-215.44, 444.32) * mm});
            skLineSegment(sketch, "E1754", {"start": v(-215.44, 444.32) * mm, "end": v(-217.2, 445.51) * mm});
            skLineSegment(sketch, "E1755", {"start": v(-217.2, 445.51) * mm, "end": v(-218.98, 446.68) * mm});
            skLineSegment(sketch, "E1756", {"start": v(-218.98, 446.68) * mm, "end": v(-220.78, 447.82) * mm});
            skLineSegment(sketch, "E1757", {"start": v(-220.78, 447.82) * mm, "end": v(-222.6, 448.94) * mm});
            skLineSegment(sketch, "E1758", {"start": v(-222.6, 448.94) * mm, "end": v(-224.42, 450.04) * mm});
            skLineSegment(sketch, "E1759", {"start": v(-224.42, 450.04) * mm, "end": v(-226.27, 451.1) * mm});
            skLineSegment(sketch, "E1760", {"start": v(-226.27, 451.1) * mm, "end": v(-228.13, 452.15) * mm});
            skLineSegment(sketch, "E1761", {"start": v(-228.13, 452.15) * mm, "end": v(-230, 453.17) * mm});
            skLineSegment(sketch, "E1762", {"start": v(-230, 453.17) * mm, "end": v(-231.9, 454.17) * mm});
            skLineSegment(sketch, "E1763", {"start": v(-231.9, 454.17) * mm, "end": v(-233.81, 455.13) * mm});
            skLineSegment(sketch, "E1764", {"start": v(-233.81, 455.13) * mm, "end": v(-235.74, 456.07) * mm});
            skLineSegment(sketch, "E1765", {"start": v(-235.74, 456.07) * mm, "end": v(-237.68, 457) * mm});
            skLineSegment(sketch, "E1766", {"start": v(-237.68, 457) * mm, "end": v(-239.63, 457.88) * mm});
            skLineSegment(sketch, "E1767", {"start": v(-239.63, 457.88) * mm, "end": v(-241.6, 458.74) * mm});
            skLineSegment(sketch, "E1768", {"start": v(-241.6, 458.74) * mm, "end": v(-243.59, 459.58) * mm});
            skLineSegment(sketch, "E1769", {"start": v(-243.59, 459.58) * mm, "end": v(-245.58, 460.38) * mm});
            skLineSegment(sketch, "E1770", {"start": v(-245.58, 460.38) * mm, "end": v(-247.6, 461.16) * mm});
            skLineSegment(sketch, "E1771", {"start": v(-247.6, 461.16) * mm, "end": v(-249.62, 461.92) * mm});
            skLineSegment(sketch, "E1772", {"start": v(-249.62, 461.92) * mm, "end": v(-251.66, 462.64) * mm});
            skLineSegment(sketch, "E1773", {"start": v(-251.66, 462.64) * mm, "end": v(-253.71, 463.34) * mm});
            skLineSegment(sketch, "E1774", {"start": v(-253.71, 463.34) * mm, "end": v(-255.78, 464) * mm});
            skLineSegment(sketch, "E1775", {"start": v(-255.78, 464) * mm, "end": v(-257.85, 464.64) * mm});
            skLineSegment(sketch, "E1776", {"start": v(-257.85, 464.64) * mm, "end": v(-259.94, 465.25) * mm});
            skLineSegment(sketch, "E1777", {"start": v(-259.94, 465.25) * mm, "end": v(-262.05, 465.83) * mm});
            skLineSegment(sketch, "E1778", {"start": v(-262.05, 465.83) * mm, "end": v(-264.16, 466.39) * mm});
            skLineSegment(sketch, "E1779", {"start": v(-264.16, 466.39) * mm, "end": v(-266.29, 466.9) * mm});
            skLineSegment(sketch, "E1780", {"start": v(-266.29, 466.9) * mm, "end": v(-268.43, 467.4) * mm});
            skLineSegment(sketch, "E1781", {"start": v(-268.43, 467.4) * mm, "end": v(-270.58, 467.86) * mm});
            skLineSegment(sketch, "E1782", {"start": v(-270.58, 467.86) * mm, "end": v(-272.74, 468.3) * mm});
            skLineSegment(sketch, "E1783", {"start": v(-272.74, 468.3) * mm, "end": v(-274.9, 468.7) * mm});
            skLineSegment(sketch, "E1784", {"start": v(-274.9, 468.7) * mm, "end": v(-277.09, 469.06) * mm});
            skLineSegment(sketch, "E1785", {"start": v(-277.09, 469.06) * mm, "end": v(-279.28, 469.4) * mm});
            skLineSegment(sketch, "E1786", {"start": v(-279.28, 469.4) * mm, "end": v(-281.48, 469.71) * mm});
            skLineSegment(sketch, "E1787", {"start": v(-281.48, 469.71) * mm, "end": v(-283.7, 469.99) * mm});
            skLineSegment(sketch, "E1788", {"start": v(-283.7, 469.99) * mm, "end": v(-285.92, 470.23) * mm});
            skLineSegment(sketch, "E1789", {"start": v(-285.92, 470.23) * mm, "end": v(-288.15, 470.45) * mm});
            skLineSegment(sketch, "E1790", {"start": v(-288.15, 470.45) * mm, "end": v(-290.39, 470.63) * mm});
            skLineSegment(sketch, "E1791", {"start": v(-290.39, 470.63) * mm, "end": v(-292.64, 470.78) * mm});
            skLineSegment(sketch, "E1792", {"start": v(-292.64, 470.78) * mm, "end": v(-294.9, 470.9) * mm});
            skLineSegment(sketch, "E1793", {"start": v(-294.9, 470.9) * mm, "end": v(-297.16, 470.98) * mm});
            skLineSegment(sketch, "E1794", {"start": v(-297.16, 470.98) * mm, "end": v(-299.44, 471.03) * mm});
            skLineSegment(sketch, "E1795", {"start": v(-299.44, 471.03) * mm, "end": v(-301.72, 471.04) * mm});
            skLineSegment(sketch, "E1796", {"start": v(-301.72, 471.04) * mm, "end": v(-303.7, 471.03) * mm});
            skLineSegment(sketch, "E1797", {"start": v(-303.7, 471.03) * mm, "end": v(-305.66, 471) * mm});
            skLineSegment(sketch, "E1798", {"start": v(-305.66, 471) * mm, "end": v(-307.62, 470.93) * mm});
            skLineSegment(sketch, "E1799", {"start": v(-307.62, 470.93) * mm, "end": v(-309.57, 470.85) * mm});
            skLineSegment(sketch, "E1800", {"start": v(-309.57, 470.85) * mm, "end": v(-311.52, 470.73) * mm});
            skLineSegment(sketch, "E1801", {"start": v(-311.52, 470.73) * mm, "end": v(-313.46, 470.6) * mm});
            skLineSegment(sketch, "E1802", {"start": v(-313.46, 470.6) * mm, "end": v(-315.4, 470.44) * mm});
            skLineSegment(sketch, "E1803", {"start": v(-315.4, 470.44) * mm, "end": v(-317.32, 470.26) * mm});
            skLineSegment(sketch, "E1804", {"start": v(-317.32, 470.26) * mm, "end": v(-319.24, 470.05) * mm});
            skLineSegment(sketch, "E1805", {"start": v(-319.24, 470.05) * mm, "end": v(-321.15, 469.82) * mm});
            skLineSegment(sketch, "E1806", {"start": v(-321.15, 469.82) * mm, "end": v(-323.06, 469.56) * mm});
            skLineSegment(sketch, "E1807", {"start": v(-323.06, 469.56) * mm, "end": v(-324.96, 469.29) * mm});
            skLineSegment(sketch, "E1808", {"start": v(-324.96, 469.29) * mm, "end": v(-326.85, 468.98) * mm});
            skLineSegment(sketch, "E1809", {"start": v(-326.85, 468.98) * mm, "end": v(-328.73, 468.66) * mm});
            skLineSegment(sketch, "E1810", {"start": v(-328.73, 468.66) * mm, "end": v(-330.6, 468.31) * mm});
            skLineSegment(sketch, "E1811", {"start": v(-330.6, 468.31) * mm, "end": v(-332.47, 467.94) * mm});
            skLineSegment(sketch, "E1812", {"start": v(-332.47, 467.94) * mm, "end": v(-334.33, 467.55) * mm});
            skLineSegment(sketch, "E1813", {"start": v(-334.33, 467.55) * mm, "end": v(-336.18, 467.14) * mm});
            skLineSegment(sketch, "E1814", {"start": v(-336.18, 467.14) * mm, "end": v(-338.02, 466.7) * mm});
            skLineSegment(sketch, "E1815", {"start": v(-338.02, 466.7) * mm, "end": v(-339.85, 466.24) * mm});
            skLineSegment(sketch, "E1816", {"start": v(-339.85, 466.24) * mm, "end": v(-341.68, 465.76) * mm});
            skLineSegment(sketch, "E1817", {"start": v(-341.68, 465.76) * mm, "end": v(-343.49, 465.26) * mm});
            skLineSegment(sketch, "E1818", {"start": v(-343.49, 465.26) * mm, "end": v(-345.3, 464.73) * mm});
            skLineSegment(sketch, "E1819", {"start": v(-345.3, 464.73) * mm, "end": v(-347.1, 464.18) * mm});
            skLineSegment(sketch, "E1820", {"start": v(-347.1, 464.18) * mm, "end": v(-348.88, 463.62) * mm});
            skLineSegment(sketch, "E1821", {"start": v(-348.88, 463.62) * mm, "end": v(-350.66, 463.03) * mm});
            skLineSegment(sketch, "E1822", {"start": v(-350.66, 463.03) * mm, "end": v(-352.42, 462.42) * mm});
            skLineSegment(sketch, "E1823", {"start": v(-352.42, 462.42) * mm, "end": v(-354.18, 461.79) * mm});
            skLineSegment(sketch, "E1824", {"start": v(-354.18, 461.79) * mm, "end": v(-355.93, 461.13) * mm});
            skLineSegment(sketch, "E1825", {"start": v(-355.93, 461.13) * mm, "end": v(-357.67, 460.46) * mm});
            skLineSegment(sketch, "E1826", {"start": v(-357.67, 460.46) * mm, "end": v(-359.4, 459.77) * mm});
            skLineSegment(sketch, "E1827", {"start": v(-359.4, 459.77) * mm, "end": v(-361.1, 459.05) * mm});
            skLineSegment(sketch, "E1828", {"start": v(-361.1, 459.05) * mm, "end": v(-362.81, 458.32) * mm});
            skLineSegment(sketch, "E1829", {"start": v(-362.81, 458.32) * mm, "end": v(-364.5, 457.57) * mm});
            skLineSegment(sketch, "E1830", {"start": v(-364.5, 457.57) * mm, "end": v(-366.2, 456.8) * mm});
            skLineSegment(sketch, "E1831", {"start": v(-366.2, 456.8) * mm, "end": v(-367.87, 456) * mm});
            skLineSegment(sketch, "E1832", {"start": v(-367.87, 456) * mm, "end": v(-369.53, 455.19) * mm});
            skLineSegment(sketch, "E1833", {"start": v(-369.53, 455.19) * mm, "end": v(-371.18, 454.35) * mm});
            skLineSegment(sketch, "E1834", {"start": v(-371.18, 454.35) * mm, "end": v(-372.82, 453.5) * mm});
            skLineSegment(sketch, "E1835", {"start": v(-372.82, 453.5) * mm, "end": v(-374.45, 452.63) * mm});
            skLineSegment(sketch, "E1836", {"start": v(-374.45, 452.63) * mm, "end": v(-376.06, 451.74) * mm});
            skLineSegment(sketch, "E1837", {"start": v(-376.06, 451.74) * mm, "end": v(-377.66, 450.83) * mm});
            skLineSegment(sketch, "E1838", {"start": v(-377.66, 450.83) * mm, "end": v(-379.26, 449.9) * mm});
            skLineSegment(sketch, "E1839", {"start": v(-379.26, 449.9) * mm, "end": v(-380.83, 448.96) * mm});
            skLineSegment(sketch, "E1840", {"start": v(-380.83, 448.96) * mm, "end": v(-382.4, 448) * mm});
            skLineSegment(sketch, "E1841", {"start": v(-382.4, 448) * mm, "end": v(-383.95, 447) * mm});
            skLineSegment(sketch, "E1842", {"start": v(-383.95, 447) * mm, "end": v(-385.5, 446) * mm});
            skLineSegment(sketch, "E1843", {"start": v(-385.5, 446) * mm, "end": v(-387.02, 444.99) * mm});
            skLineSegment(sketch, "E1844", {"start": v(-387.02, 444.99) * mm, "end": v(-388.54, 443.95) * mm});
            skLineSegment(sketch, "E1845", {"start": v(-388.54, 443.95) * mm, "end": v(-390.04, 442.9) * mm});
            skLineSegment(sketch, "E1846", {"start": v(-390.04, 442.9) * mm, "end": v(-391.53, 441.82) * mm});
            skLineSegment(sketch, "E1847", {"start": v(-391.53, 441.82) * mm, "end": v(-393, 440.73) * mm});
            skLineSegment(sketch, "E1848", {"start": v(-393, 440.73) * mm, "end": v(-394.47, 439.63) * mm});
            skLineSegment(sketch, "E1849", {"start": v(-394.47, 439.63) * mm, "end": v(-395.92, 438.5) * mm});
            skLineSegment(sketch, "E1850", {"start": v(-395.92, 438.5) * mm, "end": v(-397.35, 437.36) * mm});
            skLineSegment(sketch, "E1851", {"start": v(-397.35, 437.36) * mm, "end": v(-398.77, 436.2) * mm});
            skLineSegment(sketch, "E1852", {"start": v(-398.77, 436.2) * mm, "end": v(-400.18, 435.03) * mm});
            skLineSegment(sketch, "E1853", {"start": v(-400.18, 435.03) * mm, "end": v(-401.57, 433.84) * mm});
            skLineSegment(sketch, "E1854", {"start": v(-401.57, 433.84) * mm, "end": v(-402.94, 432.63) * mm});
            skLineSegment(sketch, "E1855", {"start": v(-402.94, 432.63) * mm, "end": v(-404.3, 431.4) * mm});
            skLineSegment(sketch, "E1856", {"start": v(-404.3, 431.4) * mm, "end": v(-405.65, 430.17) * mm});
            skLineSegment(sketch, "E1857", {"start": v(-405.65, 430.17) * mm, "end": v(-406.99, 428.92) * mm});
            skLineSegment(sketch, "E1858", {"start": v(-406.99, 428.92) * mm, "end": v(-408.3, 427.64) * mm});
            skLineSegment(sketch, "E1859", {"start": v(-408.3, 427.64) * mm, "end": v(-409.6, 426.36) * mm});
            skLineSegment(sketch, "E1860", {"start": v(-409.6, 426.36) * mm, "end": v(-410.9, 425.06) * mm});
            skLineSegment(sketch, "E1861", {"start": v(-410.9, 425.06) * mm, "end": v(-412.16, 423.74) * mm});
            skLineSegment(sketch, "E1862", {"start": v(-412.16, 423.74) * mm, "end": v(-413.42, 422.4) * mm});
            skLineSegment(sketch, "E1863", {"start": v(-413.42, 422.4) * mm, "end": v(-414.66, 421.06) * mm});
            skLineSegment(sketch, "E1864", {"start": v(-414.66, 421.06) * mm, "end": v(-415.88, 419.7) * mm});
            skLineSegment(sketch, "E1865", {"start": v(-415.88, 419.7) * mm, "end": v(-417.09, 418.32) * mm});
            skLineSegment(sketch, "E1866", {"start": v(-417.09, 418.32) * mm, "end": v(-418.28, 416.93) * mm});
            skLineSegment(sketch, "E1867", {"start": v(-418.28, 416.93) * mm, "end": v(-419.45, 415.52) * mm});
            skLineSegment(sketch, "E1868", {"start": v(-419.45, 415.52) * mm, "end": v(-420.6, 414.1) * mm});
            skLineSegment(sketch, "E1869", {"start": v(-420.6, 414.1) * mm, "end": v(-421.75, 412.67) * mm});
            skLineSegment(sketch, "E1870", {"start": v(-421.75, 412.67) * mm, "end": v(-422.87, 411.22) * mm});
            skLineSegment(sketch, "E1871", {"start": v(-422.87, 411.22) * mm, "end": v(-423.98, 409.76) * mm});
            skLineSegment(sketch, "E1872", {"start": v(-423.98, 409.76) * mm, "end": v(-425.07, 408.28) * mm});
            skLineSegment(sketch, "E1873", {"start": v(-425.07, 408.28) * mm, "end": v(-426.14, 406.8) * mm});
            skLineSegment(sketch, "E1874", {"start": v(-426.14, 406.8) * mm, "end": v(-427.2, 405.3) * mm});
            skLineSegment(sketch, "E1875", {"start": v(-427.2, 405.3) * mm, "end": v(-428.23, 403.78) * mm});
            skLineSegment(sketch, "E1876", {"start": v(-428.23, 403.78) * mm, "end": v(-429.25, 402.25) * mm});
            skLineSegment(sketch, "E1877", {"start": v(-429.25, 402.25) * mm, "end": v(-430.25, 400.7) * mm});
            skLineSegment(sketch, "E1878", {"start": v(-430.25, 400.7) * mm, "end": v(-431.24, 399.15) * mm});
            skLineSegment(sketch, "E1879", {"start": v(-431.24, 399.15) * mm, "end": v(-432.2, 397.59) * mm});
            skLineSegment(sketch, "E1880", {"start": v(-432.2, 397.59) * mm, "end": v(-433.15, 396) * mm});
            skLineSegment(sketch, "E1881", {"start": v(-433.15, 396) * mm, "end": v(-434.08, 394.42) * mm});
            skLineSegment(sketch, "E1882", {"start": v(-434.08, 394.42) * mm, "end": v(-434.99, 392.81) * mm});
            skLineSegment(sketch, "E1883", {"start": v(-434.99, 392.81) * mm, "end": v(-435.88, 391.2) * mm});
            skLineSegment(sketch, "E1884", {"start": v(-435.88, 391.2) * mm, "end": v(-436.75, 389.57) * mm});
            skLineSegment(sketch, "E1885", {"start": v(-436.75, 389.57) * mm, "end": v(-437.6, 387.93) * mm});
            skLineSegment(sketch, "E1886", {"start": v(-437.6, 387.93) * mm, "end": v(-438.43, 386.28) * mm});
            skLineSegment(sketch, "E1887", {"start": v(-438.43, 386.28) * mm, "end": v(-439.25, 384.62) * mm});
            skLineSegment(sketch, "E1888", {"start": v(-439.25, 384.62) * mm, "end": v(-440.04, 382.95) * mm});
            skLineSegment(sketch, "E1889", {"start": v(-440.04, 382.95) * mm, "end": v(-440.81, 381.26) * mm});
            skLineSegment(sketch, "E1890", {"start": v(-440.81, 381.26) * mm, "end": v(-441.57, 379.57) * mm});
            skLineSegment(sketch, "E1891", {"start": v(-441.57, 379.57) * mm, "end": v(-442.3, 377.86) * mm});
            skLineSegment(sketch, "E1892", {"start": v(-442.3, 377.86) * mm, "end": v(-443.01, 376.15) * mm});
            skLineSegment(sketch, "E1893", {"start": v(-443.01, 376.15) * mm, "end": v(-443.7, 374.42) * mm});
            skLineSegment(sketch, "E1894", {"start": v(-443.7, 374.42) * mm, "end": v(-444.38, 372.68) * mm});
            skLineSegment(sketch, "E1895", {"start": v(-444.38, 372.68) * mm, "end": v(-445.03, 370.93) * mm});
            skLineSegment(sketch, "E1896", {"start": v(-445.03, 370.93) * mm, "end": v(-445.66, 369.18) * mm});
            skLineSegment(sketch, "E1897", {"start": v(-445.66, 369.18) * mm, "end": v(-446.27, 367.4) * mm});
            skLineSegment(sketch, "E1898", {"start": v(-446.27, 367.4) * mm, "end": v(-446.86, 365.63) * mm});
            skLineSegment(sketch, "E1899", {"start": v(-446.86, 365.63) * mm, "end": v(-447.43, 363.85) * mm});
            skLineSegment(sketch, "E1900", {"start": v(-447.43, 363.85) * mm, "end": v(-447.98, 362.05) * mm});
            skLineSegment(sketch, "E1901", {"start": v(-447.98, 362.05) * mm, "end": v(-448.5, 360.24) * mm});
            skLineSegment(sketch, "E1902", {"start": v(-448.5, 360.24) * mm, "end": v(-449, 358.43) * mm});
            skLineSegment(sketch, "E1903", {"start": v(-449, 358.43) * mm, "end": v(-449.49, 356.6) * mm});
            skLineSegment(sketch, "E1904", {"start": v(-449.49, 356.6) * mm, "end": v(-449.95, 354.77) * mm});
            skLineSegment(sketch, "E1905", {"start": v(-449.95, 354.77) * mm, "end": v(-450.38, 352.93) * mm});
            skLineSegment(sketch, "E1906", {"start": v(-450.38, 352.93) * mm, "end": v(-450.8, 351.08) * mm});
            skLineSegment(sketch, "E1907", {"start": v(-450.8, 351.08) * mm, "end": v(-451.2, 349.22) * mm});
            skLineSegment(sketch, "E1908", {"start": v(-451.2, 349.22) * mm, "end": v(-451.56, 347.36) * mm});
            skLineSegment(sketch, "E1909", {"start": v(-451.56, 347.36) * mm, "end": v(-451.9, 345.48) * mm});
            skLineSegment(sketch, "E1910", {"start": v(-451.9, 345.48) * mm, "end": v(-452.23, 343.6) * mm});
            skLineSegment(sketch, "E1911", {"start": v(-452.23, 343.6) * mm, "end": v(-452.53, 341.71) * mm});
            skLineSegment(sketch, "E1912", {"start": v(-452.53, 341.71) * mm, "end": v(-452.8, 339.81) * mm});
            skLineSegment(sketch, "E1913", {"start": v(-452.8, 339.81) * mm, "end": v(-453.06, 337.9) * mm});
            skLineSegment(sketch, "E1914", {"start": v(-453.06, 337.9) * mm, "end": v(-453.3, 336) * mm});
            skLineSegment(sketch, "E1915", {"start": v(-453.3, 336) * mm, "end": v(-453.5, 334.08) * mm});
            skLineSegment(sketch, "E1916", {"start": v(-453.5, 334.08) * mm, "end": v(-453.69, 332.15) * mm});
            skLineSegment(sketch, "E1917", {"start": v(-453.69, 332.15) * mm, "end": v(-453.85, 330.21) * mm});
            skLineSegment(sketch, "E1918", {"start": v(-453.85, 330.21) * mm, "end": v(-453.98, 328.27) * mm});
            skLineSegment(sketch, "E1919", {"start": v(-453.98, 328.27) * mm, "end": v(-454.1, 326.33) * mm});
            skLineSegment(sketch, "E1920", {"start": v(-454.1, 326.33) * mm, "end": v(-454.18, 324.37) * mm});
            skLineSegment(sketch, "E1921", {"start": v(-454.18, 324.37) * mm, "end": v(-454.24, 322.41) * mm});
            skLineSegment(sketch, "E1922", {"start": v(-454.24, 322.41) * mm, "end": v(-454.28, 320.45) * mm});
            skLineSegment(sketch, "E1923", {"start": v(-454.28, 320.45) * mm, "end": v(-454.29, 318.48) * mm});
            skLineSegment(sketch, "E1924", {"start": v(-454.29, 318.48) * mm, "end": v(-454.29, -100.1) * mm});
            skLineSegment(sketch, "E1925", {"start": v(-454.29, -100.1) * mm, "end": v(-454.28, -102.07) * mm});
            skLineSegment(sketch, "E1926", {"start": v(-454.28, -102.07) * mm, "end": v(-454.24, -104.04) * mm});
            skLineSegment(sketch, "E1927", {"start": v(-454.24, -104.04) * mm, "end": v(-454.18, -106) * mm});
            skLineSegment(sketch, "E1928", {"start": v(-454.18, -106) * mm, "end": v(-454.1, -107.95) * mm});
            skLineSegment(sketch, "E1929", {"start": v(-454.1, -107.95) * mm, "end": v(-453.98, -109.9) * mm});
            skLineSegment(sketch, "E1930", {"start": v(-453.98, -109.9) * mm, "end": v(-453.85, -111.84) * mm});
            skLineSegment(sketch, "E1931", {"start": v(-453.85, -111.84) * mm, "end": v(-453.69, -113.77) * mm});
            skLineSegment(sketch, "E1932", {"start": v(-453.69, -113.77) * mm, "end": v(-453.5, -115.7) * mm});
            skLineSegment(sketch, "E1933", {"start": v(-453.5, -115.7) * mm, "end": v(-453.3, -117.62) * mm});
            skLineSegment(sketch, "E1934", {"start": v(-453.3, -117.62) * mm, "end": v(-453.06, -119.53) * mm});
            skLineSegment(sketch, "E1935", {"start": v(-453.06, -119.53) * mm, "end": v(-452.8, -121.44) * mm});
            skLineSegment(sketch, "E1936", {"start": v(-452.8, -121.44) * mm, "end": v(-452.53, -123.33) * mm});
            skLineSegment(sketch, "E1937", {"start": v(-452.53, -123.33) * mm, "end": v(-452.23, -125.22) * mm});
            skLineSegment(sketch, "E1938", {"start": v(-452.23, -125.22) * mm, "end": v(-451.9, -127.1) * mm});
            skLineSegment(sketch, "E1939", {"start": v(-451.9, -127.1) * mm, "end": v(-451.56, -128.98) * mm});
            skLineSegment(sketch, "E1940", {"start": v(-451.56, -128.98) * mm, "end": v(-451.2, -130.85) * mm});
            skLineSegment(sketch, "E1941", {"start": v(-451.2, -130.85) * mm, "end": v(-450.8, -132.7) * mm});
            skLineSegment(sketch, "E1942", {"start": v(-450.8, -132.7) * mm, "end": v(-450.38, -134.55) * mm});
            skLineSegment(sketch, "E1943", {"start": v(-450.38, -134.55) * mm, "end": v(-449.95, -136.4) * mm});
            skLineSegment(sketch, "E1944", {"start": v(-449.95, -136.4) * mm, "end": v(-449.49, -138.23) * mm});
            skLineSegment(sketch, "E1945", {"start": v(-449.49, -138.23) * mm, "end": v(-449, -140.05) * mm});
            skLineSegment(sketch, "E1946", {"start": v(-449, -140.05) * mm, "end": v(-448.5, -141.87) * mm});
            skLineSegment(sketch, "E1947", {"start": v(-448.5, -141.87) * mm, "end": v(-447.98, -143.67) * mm});
            skLineSegment(sketch, "E1948", {"start": v(-447.98, -143.67) * mm, "end": v(-447.43, -145.47) * mm});
            skLineSegment(sketch, "E1949", {"start": v(-447.43, -145.47) * mm, "end": v(-446.86, -147.25) * mm});
            skLineSegment(sketch, "E1950", {"start": v(-446.86, -147.25) * mm, "end": v(-446.27, -149.03) * mm});
            skLineSegment(sketch, "E1951", {"start": v(-446.27, -149.03) * mm, "end": v(-445.66, -150.8) * mm});
            skLineSegment(sketch, "E1952", {"start": v(-445.66, -150.8) * mm, "end": v(-445.03, -152.56) * mm});
            skLineSegment(sketch, "E1953", {"start": v(-445.03, -152.56) * mm, "end": v(-444.38, -154.3) * mm});
            skLineSegment(sketch, "E1954", {"start": v(-444.38, -154.3) * mm, "end": v(-443.7, -156.04) * mm});
            skLineSegment(sketch, "E1955", {"start": v(-443.7, -156.04) * mm, "end": v(-443.01, -157.77) * mm});
            skLineSegment(sketch, "E1956", {"start": v(-443.01, -157.77) * mm, "end": v(-442.3, -159.48) * mm});
            skLineSegment(sketch, "E1957", {"start": v(-442.3, -159.48) * mm, "end": v(-441.57, -161.2) * mm});
            skLineSegment(sketch, "E1958", {"start": v(-441.57, -161.2) * mm, "end": v(-440.81, -162.89) * mm});
            skLineSegment(sketch, "E1959", {"start": v(-440.81, -162.89) * mm, "end": v(-440.04, -164.57) * mm});
            skLineSegment(sketch, "E1960", {"start": v(-440.04, -164.57) * mm, "end": v(-439.25, -166.24) * mm});
            skLineSegment(sketch, "E1961", {"start": v(-439.25, -166.24) * mm, "end": v(-438.43, -167.9) * mm});
            skLineSegment(sketch, "E1962", {"start": v(-438.43, -167.9) * mm, "end": v(-437.6, -169.56) * mm});
            skLineSegment(sketch, "E1963", {"start": v(-437.6, -169.56) * mm, "end": v(-436.75, -171.2) * mm});
            skLineSegment(sketch, "E1964", {"start": v(-436.75, -171.2) * mm, "end": v(-435.88, -172.82) * mm});
            skLineSegment(sketch, "E1965", {"start": v(-435.88, -172.82) * mm, "end": v(-434.99, -174.44) * mm});
            skLineSegment(sketch, "E1966", {"start": v(-434.99, -174.44) * mm, "end": v(-434.08, -176.04) * mm});
            skLineSegment(sketch, "E1967", {"start": v(-434.08, -176.04) * mm, "end": v(-433.15, -177.63) * mm});
            skLineSegment(sketch, "E1968", {"start": v(-433.15, -177.63) * mm, "end": v(-432.2, -179.21) * mm});
            skLineSegment(sketch, "E1969", {"start": v(-432.2, -179.21) * mm, "end": v(-431.24, -180.78) * mm});
            skLineSegment(sketch, "E1970", {"start": v(-431.24, -180.78) * mm, "end": v(-430.25, -182.33) * mm});
            skLineSegment(sketch, "E1971", {"start": v(-430.25, -182.33) * mm, "end": v(-429.25, -183.87) * mm});
            skLineSegment(sketch, "E1972", {"start": v(-429.25, -183.87) * mm, "end": v(-428.23, -185.4) * mm});
            skLineSegment(sketch, "E1973", {"start": v(-428.23, -185.4) * mm, "end": v(-427.2, -186.92) * mm});
            skLineSegment(sketch, "E1974", {"start": v(-427.2, -186.92) * mm, "end": v(-426.14, -188.42) * mm});
            skLineSegment(sketch, "E1975", {"start": v(-426.14, -188.42) * mm, "end": v(-425.07, -189.9) * mm});
            skLineSegment(sketch, "E1976", {"start": v(-425.07, -189.9) * mm, "end": v(-423.98, -191.38) * mm});
            skLineSegment(sketch, "E1977", {"start": v(-423.98, -191.38) * mm, "end": v(-422.87, -192.84) * mm});
            skLineSegment(sketch, "E1978", {"start": v(-422.87, -192.84) * mm, "end": v(-421.75, -194.3) * mm});
            skLineSegment(sketch, "E1979", {"start": v(-421.75, -194.3) * mm, "end": v(-420.6, -195.73) * mm});
            skLineSegment(sketch, "E1980", {"start": v(-420.6, -195.73) * mm, "end": v(-419.45, -197.15) * mm});
            skLineSegment(sketch, "E1981", {"start": v(-419.45, -197.15) * mm, "end": v(-418.28, -198.55) * mm});
            skLineSegment(sketch, "E1982", {"start": v(-418.28, -198.55) * mm, "end": v(-417.09, -199.94) * mm});
            skLineSegment(sketch, "E1983", {"start": v(-417.09, -199.94) * mm, "end": v(-415.88, -201.32) * mm});
            skLineSegment(sketch, "E1984", {"start": v(-415.88, -201.32) * mm, "end": v(-414.66, -202.68) * mm});
            skLineSegment(sketch, "E1985", {"start": v(-414.66, -202.68) * mm, "end": v(-413.42, -204.03) * mm});
            skLineSegment(sketch, "E1986", {"start": v(-413.42, -204.03) * mm, "end": v(-412.16, -205.36) * mm});
            skLineSegment(sketch, "E1987", {"start": v(-412.16, -205.36) * mm, "end": v(-410.9, -206.68) * mm});
            skLineSegment(sketch, "E1988", {"start": v(-410.9, -206.68) * mm, "end": v(-409.6, -207.98) * mm});
            skLineSegment(sketch, "E1989", {"start": v(-409.6, -207.98) * mm, "end": v(-408.3, -209.27) * mm});
            skLineSegment(sketch, "E1990", {"start": v(-408.3, -209.27) * mm, "end": v(-406.99, -210.54) * mm});
            skLineSegment(sketch, "E1991", {"start": v(-406.99, -210.54) * mm, "end": v(-405.65, -211.8) * mm});
            skLineSegment(sketch, "E1992", {"start": v(-405.65, -211.8) * mm, "end": v(-404.3, -213.03) * mm});
            skLineSegment(sketch, "E1993", {"start": v(-404.3, -213.03) * mm, "end": v(-402.94, -214.26) * mm});
            skLineSegment(sketch, "E1994", {"start": v(-402.94, -214.26) * mm, "end": v(-401.57, -215.46) * mm});
            skLineSegment(sketch, "E1995", {"start": v(-401.57, -215.46) * mm, "end": v(-400.18, -216.65) * mm});
            skLineSegment(sketch, "E1996", {"start": v(-400.18, -216.65) * mm, "end": v(-398.77, -217.83) * mm});
            skLineSegment(sketch, "E1997", {"start": v(-398.77, -217.83) * mm, "end": v(-397.35, -218.98) * mm});
            skLineSegment(sketch, "E1998", {"start": v(-397.35, -218.98) * mm, "end": v(-395.92, -220.13) * mm});
            skLineSegment(sketch, "E1999", {"start": v(-395.92, -220.13) * mm, "end": v(-394.47, -221.25) * mm});
            skLineSegment(sketch, "E2000", {"start": v(-394.47, -221.25) * mm, "end": v(-393, -222.36) * mm});
            skLineSegment(sketch, "E2001", {"start": v(-393, -222.36) * mm, "end": v(-391.53, -223.45) * mm});
            skLineSegment(sketch, "E2002", {"start": v(-391.53, -223.45) * mm, "end": v(-390.04, -224.52) * mm});
            skLineSegment(sketch, "E2003", {"start": v(-390.04, -224.52) * mm, "end": v(-388.54, -225.57) * mm});
            skLineSegment(sketch, "E2004", {"start": v(-388.54, -225.57) * mm, "end": v(-387.02, -226.61) * mm});
            skLineSegment(sketch, "E2005", {"start": v(-387.02, -226.61) * mm, "end": v(-385.5, -227.63) * mm});
            skLineSegment(sketch, "E2006", {"start": v(-385.5, -227.63) * mm, "end": v(-383.95, -228.63) * mm});
            skLineSegment(sketch, "E2007", {"start": v(-383.95, -228.63) * mm, "end": v(-382.4, -229.61) * mm});
            skLineSegment(sketch, "E2008", {"start": v(-382.4, -229.61) * mm, "end": v(-380.83, -230.58) * mm});
            skLineSegment(sketch, "E2009", {"start": v(-380.83, -230.58) * mm, "end": v(-379.26, -231.52) * mm});
            skLineSegment(sketch, "E2010", {"start": v(-379.26, -231.52) * mm, "end": v(-377.66, -232.45) * mm});
            skLineSegment(sketch, "E2011", {"start": v(-377.66, -232.45) * mm, "end": v(-376.06, -233.36) * mm});
            skLineSegment(sketch, "E2012", {"start": v(-376.06, -233.36) * mm, "end": v(-374.45, -234.25) * mm});
            skLineSegment(sketch, "E2013", {"start": v(-374.45, -234.25) * mm, "end": v(-372.82, -235.12) * mm});
            skLineSegment(sketch, "E2014", {"start": v(-372.82, -235.12) * mm, "end": v(-371.18, -235.98) * mm});
            skLineSegment(sketch, "E2015", {"start": v(-371.18, -235.98) * mm, "end": v(-369.53, -236.8) * mm});
            skLineSegment(sketch, "E2016", {"start": v(-369.53, -236.8) * mm, "end": v(-367.87, -237.62) * mm});
            skLineSegment(sketch, "E2017", {"start": v(-367.87, -237.62) * mm, "end": v(-366.2, -238.41) * mm});
            skLineSegment(sketch, "E2018", {"start": v(-366.2, -238.41) * mm, "end": v(-364.5, -239.19) * mm});
            skLineSegment(sketch, "E2019", {"start": v(-364.5, -239.19) * mm, "end": v(-362.81, -239.94) * mm});
            skLineSegment(sketch, "E2020", {"start": v(-362.81, -239.94) * mm, "end": v(-361.1, -240.68) * mm});
            skLineSegment(sketch, "E2021", {"start": v(-361.1, -240.68) * mm, "end": v(-359.4, -241.4) * mm});
            skLineSegment(sketch, "E2022", {"start": v(-359.4, -241.4) * mm, "end": v(-357.67, -242.08) * mm});
            skLineSegment(sketch, "E2023", {"start": v(-357.67, -242.08) * mm, "end": v(-355.93, -242.76) * mm});
            skLineSegment(sketch, "E2024", {"start": v(-355.93, -242.76) * mm, "end": v(-354.18, -243.4) * mm});
            skLineSegment(sketch, "E2025", {"start": v(-354.18, -243.4) * mm, "end": v(-352.42, -244.04) * mm});
            skLineSegment(sketch, "E2026", {"start": v(-352.42, -244.04) * mm, "end": v(-350.66, -244.65) * mm});
            skLineSegment(sketch, "E2027", {"start": v(-350.66, -244.65) * mm, "end": v(-348.88, -245.24) * mm});
            skLineSegment(sketch, "E2028", {"start": v(-348.88, -245.24) * mm, "end": v(-347.1, -245.8) * mm});
            skLineSegment(sketch, "E2029", {"start": v(-347.1, -245.8) * mm, "end": v(-345.3, -246.35) * mm});
            skLineSegment(sketch, "E2030", {"start": v(-345.3, -246.35) * mm, "end": v(-343.49, -246.88) * mm});
            skLineSegment(sketch, "E2031", {"start": v(-343.49, -246.88) * mm, "end": v(-341.68, -247.38) * mm});
            skLineSegment(sketch, "E2032", {"start": v(-341.68, -247.38) * mm, "end": v(-339.85, -247.86) * mm});
            skLineSegment(sketch, "E2033", {"start": v(-339.85, -247.86) * mm, "end": v(-338.02, -248.32) * mm});
            skLineSegment(sketch, "E2034", {"start": v(-338.02, -248.32) * mm, "end": v(-336.18, -248.76) * mm});
            skLineSegment(sketch, "E2035", {"start": v(-336.18, -248.76) * mm, "end": v(-334.33, -249.17) * mm});
            skLineSegment(sketch, "E2036", {"start": v(-334.33, -249.17) * mm, "end": v(-332.47, -249.57) * mm});
            skLineSegment(sketch, "E2037", {"start": v(-332.47, -249.57) * mm, "end": v(-330.6, -249.94) * mm});
            skLineSegment(sketch, "E2038", {"start": v(-330.6, -249.94) * mm, "end": v(-328.73, -250.28) * mm});
            skLineSegment(sketch, "E2039", {"start": v(-328.73, -250.28) * mm, "end": v(-326.85, -250.6) * mm});
            skLineSegment(sketch, "E2040", {"start": v(-326.85, -250.6) * mm, "end": v(-324.96, -250.9) * mm});
            skLineSegment(sketch, "E2041", {"start": v(-324.96, -250.9) * mm, "end": v(-323.06, -251.19) * mm});
            skLineSegment(sketch, "E2042", {"start": v(-323.06, -251.19) * mm, "end": v(-321.15, -251.44) * mm});
            skLineSegment(sketch, "E2043", {"start": v(-321.15, -251.44) * mm, "end": v(-319.24, -251.67) * mm});
            skLineSegment(sketch, "E2044", {"start": v(-319.24, -251.67) * mm, "end": v(-317.32, -251.88) * mm});
            skLineSegment(sketch, "E2045", {"start": v(-317.32, -251.88) * mm, "end": v(-315.4, -252.06) * mm});
            skLineSegment(sketch, "E2046", {"start": v(-315.4, -252.06) * mm, "end": v(-313.46, -252.22) * mm});
            skLineSegment(sketch, "E2047", {"start": v(-313.46, -252.22) * mm, "end": v(-311.52, -252.36) * mm});
            skLineSegment(sketch, "E2048", {"start": v(-311.52, -252.36) * mm, "end": v(-309.57, -252.47) * mm});
            skLineSegment(sketch, "E2049", {"start": v(-309.57, -252.47) * mm, "end": v(-307.62, -252.55) * mm});
            skLineSegment(sketch, "E2050", {"start": v(-307.62, -252.55) * mm, "end": v(-305.66, -252.62) * mm});
            skLineSegment(sketch, "E2051", {"start": v(-305.66, -252.62) * mm, "end": v(-303.7, -252.65) * mm});
            skLineSegment(sketch, "E2052", {"start": v(-303.7, -252.65) * mm, "end": v(-301.72, -252.67) * mm});
            skLineSegment(sketch, "E2053", {"start": v(-301.72, -252.67) * mm, "end": v(-300.04, -252.66) * mm});
            skLineSegment(sketch, "E2054", {"start": v(-300.04, -252.66) * mm, "end": v(-298.37, -252.63) * mm});
            skLineSegment(sketch, "E2055", {"start": v(-298.37, -252.63) * mm, "end": v(-296.7, -252.58) * mm});
            skLineSegment(sketch, "E2056", {"start": v(-296.7, -252.58) * mm, "end": v(-295.04, -252.52) * mm});
            skLineSegment(sketch, "E2057", {"start": v(-295.04, -252.52) * mm, "end": v(-293.38, -252.44) * mm});
            skLineSegment(sketch, "E2058", {"start": v(-293.38, -252.44) * mm, "end": v(-291.72, -252.34) * mm});
            skLineSegment(sketch, "E2059", {"start": v(-291.72, -252.34) * mm, "end": v(-290.08, -252.23) * mm});
            skLineSegment(sketch, "E2060", {"start": v(-290.08, -252.23) * mm, "end": v(-288.44, -252.1) * mm});
            skLineSegment(sketch, "E2061", {"start": v(-288.44, -252.1) * mm, "end": v(-286.8, -251.94) * mm});
            skLineSegment(sketch, "E2062", {"start": v(-286.8, -251.94) * mm, "end": v(-285.17, -251.77) * mm});
            skLineSegment(sketch, "E2063", {"start": v(-285.17, -251.77) * mm, "end": v(-283.55, -251.59) * mm});
            skLineSegment(sketch, "E2064", {"start": v(-283.55, -251.59) * mm, "end": v(-281.93, -251.39) * mm});
            skLineSegment(sketch, "E2065", {"start": v(-281.93, -251.39) * mm, "end": v(-280.32, -251.17) * mm});
            skLineSegment(sketch, "E2066", {"start": v(-280.32, -251.17) * mm, "end": v(-278.71, -250.93) * mm});
            skLineSegment(sketch, "E2067", {"start": v(-278.71, -250.93) * mm, "end": v(-277.11, -250.68) * mm});
            skLineSegment(sketch, "E2068", {"start": v(-277.11, -250.68) * mm, "end": v(-275.52, -250.4) * mm});
            skLineSegment(sketch, "E2069", {"start": v(-275.52, -250.4) * mm, "end": v(-273.93, -250.12) * mm});
            skLineSegment(sketch, "E2070", {"start": v(-273.93, -250.12) * mm, "end": v(-272.35, -249.82) * mm});
            skLineSegment(sketch, "E2071", {"start": v(-272.35, -249.82) * mm, "end": v(-270.78, -249.5) * mm});
            skLineSegment(sketch, "E2072", {"start": v(-270.78, -249.5) * mm, "end": v(-269.2, -249.16) * mm});
            skLineSegment(sketch, "E2073", {"start": v(-269.2, -249.16) * mm, "end": v(-267.65, -248.8) * mm});
            skLineSegment(sketch, "E2074", {"start": v(-267.65, -248.8) * mm, "end": v(-266.1, -248.44) * mm});
            skLineSegment(sketch, "E2075", {"start": v(-266.1, -248.44) * mm, "end": v(-264.55, -248.05) * mm});
            skLineSegment(sketch, "E2076", {"start": v(-264.55, -248.05) * mm, "end": v(-263, -247.65) * mm});
            skLineSegment(sketch, "E2077", {"start": v(-263, -247.65) * mm, "end": v(-261.47, -247.24) * mm});
            skLineSegment(sketch, "E2078", {"start": v(-261.47, -247.24) * mm, "end": v(-259.95, -246.8) * mm});
            skLineSegment(sketch, "E2079", {"start": v(-259.95, -246.8) * mm, "end": v(-258.43, -246.35) * mm});
            skLineSegment(sketch, "E2080", {"start": v(-258.43, -246.35) * mm, "end": v(-256.92, -245.9) * mm});
            skLineSegment(sketch, "E2081", {"start": v(-256.92, -245.9) * mm, "end": v(-255.41, -245.41) * mm});
            skLineSegment(sketch, "E2082", {"start": v(-255.41, -245.41) * mm, "end": v(-253.92, -244.92) * mm});
            skLineSegment(sketch, "E2083", {"start": v(-253.92, -244.92) * mm, "end": v(-252.43, -244.4) * mm});
            skLineSegment(sketch, "E2084", {"start": v(-252.43, -244.4) * mm, "end": v(-250.94, -243.88) * mm});
            skLineSegment(sketch, "E2085", {"start": v(-250.94, -243.88) * mm, "end": v(-249.47, -243.34) * mm});
            skLineSegment(sketch, "E2086", {"start": v(-249.47, -243.34) * mm, "end": v(-248, -242.78) * mm});
            skLineSegment(sketch, "E2087", {"start": v(-248, -242.78) * mm, "end": v(-246.54, -242.21) * mm});
            skLineSegment(sketch, "E2088", {"start": v(-246.54, -242.21) * mm, "end": v(-245.1, -241.63) * mm});
            skLineSegment(sketch, "E2089", {"start": v(-245.1, -241.63) * mm, "end": v(-243.65, -241.02) * mm});
            skLineSegment(sketch, "E2090", {"start": v(-243.65, -241.02) * mm, "end": v(-242.22, -240.4) * mm});
            skLineSegment(sketch, "E2091", {"start": v(-242.22, -240.4) * mm, "end": v(-240.79, -239.78) * mm});
            skLineSegment(sketch, "E2092", {"start": v(-240.79, -239.78) * mm, "end": v(-239.37, -239.13) * mm});
            skLineSegment(sketch, "E2093", {"start": v(-239.37, -239.13) * mm, "end": v(-237.96, -238.48) * mm});
            skLineSegment(sketch, "E2094", {"start": v(-237.96, -238.48) * mm, "end": v(-236.56, -237.8) * mm});
            skLineSegment(sketch, "E2095", {"start": v(-236.56, -237.8) * mm, "end": v(-235.16, -237.11) * mm});
            skLineSegment(sketch, "E2096", {"start": v(-235.16, -237.11) * mm, "end": v(-233.78, -236.41) * mm});
            skLineSegment(sketch, "E2097", {"start": v(-233.78, -236.41) * mm, "end": v(-232.4, -235.7) * mm});
            skLineSegment(sketch, "E2098", {"start": v(-232.4, -235.7) * mm, "end": v(-231.04, -234.97) * mm});
            skLineSegment(sketch, "E2099", {"start": v(-231.04, -234.97) * mm, "end": v(-229.68, -234.22) * mm});
            skLineSegment(sketch, "E2100", {"start": v(-229.68, -234.22) * mm, "end": v(-228.33, -233.47) * mm});
            skLineSegment(sketch, "E2101", {"start": v(-228.33, -233.47) * mm, "end": v(-226.98, -232.7) * mm});
            skLineSegment(sketch, "E2102", {"start": v(-226.98, -232.7) * mm, "end": v(-225.65, -231.9) * mm});
            skLineSegment(sketch, "E2103", {"start": v(-225.65, -231.9) * mm, "end": v(-224.33, -231.11) * mm});
            skLineSegment(sketch, "E2104", {"start": v(-224.33, -231.11) * mm, "end": v(-223.02, -230.3) * mm});
            skLineSegment(sketch, "E2105", {"start": v(-223.02, -230.3) * mm, "end": v(-221.71, -229.47) * mm});
            skLineSegment(sketch, "E2106", {"start": v(-221.71, -229.47) * mm, "end": v(-220.41, -228.64) * mm});
            skLineSegment(sketch, "E2107", {"start": v(-220.41, -228.64) * mm, "end": v(-219.13, -227.78) * mm});
            skLineSegment(sketch, "E2108", {"start": v(-219.13, -227.78) * mm, "end": v(-217.85, -226.92) * mm});
            skLineSegment(sketch, "E2109", {"start": v(-217.85, -226.92) * mm, "end": v(-216.58, -226.04) * mm});
            skLineSegment(sketch, "E2110", {"start": v(-216.58, -226.04) * mm, "end": v(-215.33, -225.15) * mm});
            skLineSegment(sketch, "E2111", {"start": v(-215.33, -225.15) * mm, "end": v(-214.08, -224.25) * mm});
            skLineSegment(sketch, "E2112", {"start": v(-214.08, -224.25) * mm, "end": v(-212.84, -223.33) * mm});
            skLineSegment(sketch, "E2113", {"start": v(-212.84, -223.33) * mm, "end": v(-211.61, -222.4) * mm});
            skLineSegment(sketch, "E2114", {"start": v(-211.61, -222.4) * mm, "end": v(-210.4, -221.46) * mm});
            skLineSegment(sketch, "E2115", {"start": v(-210.4, -221.46) * mm, "end": v(-209.19, -220.5) * mm});
            skLineSegment(sketch, "E2116", {"start": v(-209.19, -220.5) * mm, "end": v(-207.99, -219.54) * mm});
            skLineSegment(sketch, "E2117", {"start": v(-207.99, -219.54) * mm, "end": v(-206.8, -218.56) * mm});
            skLineSegment(sketch, "E2118", {"start": v(-206.8, -218.56) * mm, "end": v(-205.62, -217.57) * mm});
            skLineSegment(sketch, "E2119", {"start": v(-205.62, -217.57) * mm, "end": v(-204.45, -216.57) * mm});
            skLineSegment(sketch, "E2120", {"start": v(-204.45, -216.57) * mm, "end": v(-203.3, -215.56) * mm});
            skLineSegment(sketch, "E2121", {"start": v(-203.3, -215.56) * mm, "end": v(-202.15, -214.53) * mm});
            skLineSegment(sketch, "E2122", {"start": v(-202.15, -214.53) * mm, "end": v(-201.01, -213.5) * mm});
            skLineSegment(sketch, "E2123", {"start": v(-201.01, -213.5) * mm, "end": v(-199.89, -212.44) * mm});
            skLineSegment(sketch, "E2124", {"start": v(-199.89, -212.44) * mm, "end": v(-198.77, -211.38) * mm});
            skLineSegment(sketch, "E2125", {"start": v(-198.77, -211.38) * mm, "end": v(-197.67, -210.31) * mm});
            skLineSegment(sketch, "E2126", {"start": v(-197.67, -210.31) * mm, "end": v(-196.58, -209.23) * mm});
            skLineSegment(sketch, "E2127", {"start": v(-196.58, -209.23) * mm, "end": v(-195.5, -208.13) * mm});
            skLineSegment(sketch, "E2128", {"start": v(-195.5, -208.13) * mm, "end": v(-194.42, -207.03) * mm});
            skLineSegment(sketch, "E2129", {"start": v(-194.42, -207.03) * mm, "end": v(-193.36, -205.9) * mm});
            skLineSegment(sketch, "E2130", {"start": v(-193.36, -205.9) * mm, "end": v(-192.31, -204.78) * mm});
            skLineSegment(sketch, "E2131", {"start": v(-192.31, -204.78) * mm, "end": v(-191.28, -203.64) * mm});
            skLineSegment(sketch, "E2132", {"start": v(-191.28, -203.64) * mm, "end": v(-190.25, -202.5) * mm});
            skLineSegment(sketch, "E2133", {"start": v(-190.25, -202.5) * mm, "end": v(-189.23, -201.33) * mm});
            skLineSegment(sketch, "E2134", {"start": v(-189.23, -201.33) * mm, "end": v(-188.23, -200.16) * mm});
            skLineSegment(sketch, "E2135", {"start": v(-188.23, -200.16) * mm, "end": v(-187.24, -198.98) * mm});
            skLineSegment(sketch, "E2136", {"start": v(-187.24, -198.98) * mm, "end": v(-186.26, -197.78) * mm});
            skLineSegment(sketch, "E2137", {"start": v(-186.26, -197.78) * mm, "end": v(-185.3, -196.58) * mm});
            skLineSegment(sketch, "E2138", {"start": v(-185.3, -196.58) * mm, "end": v(-184.33, -195.37) * mm});
            skLineSegment(sketch, "E2139", {"start": v(-184.33, -195.37) * mm, "end": v(-183.39, -194.14) * mm});
            skLineSegment(sketch, "E2140", {"start": v(-183.39, -194.14) * mm, "end": v(-182.46, -192.9) * mm});
            skLineSegment(sketch, "E2141", {"start": v(-182.46, -192.9) * mm, "end": v(-181.54, -191.67) * mm});
            skLineSegment(sketch, "E2142", {"start": v(-181.54, -191.67) * mm, "end": v(-180.63, -190.41) * mm});
            skLineSegment(sketch, "E2143", {"start": v(-180.63, -190.41) * mm, "end": v(-179.73, -189.15) * mm});
            skLineSegment(sketch, "E2144", {"start": v(-179.73, -189.15) * mm, "end": v(-178.85, -187.88) * mm});
            skLineSegment(sketch, "E2145", {"start": v(-178.85, -187.88) * mm, "end": v(-177.98, -186.6) * mm});
            skLineSegment(sketch, "E2146", {"start": v(-177.98, -186.6) * mm, "end": v(-177.12, -185.3) * mm});
            skLineSegment(sketch, "E2147", {"start": v(-177.12, -185.3) * mm, "end": v(-176.27, -184) * mm});
            skLineSegment(sketch, "E2148", {"start": v(-176.27, -184) * mm, "end": v(-175.44, -182.69) * mm});
            skLineSegment(sketch, "E2149", {"start": v(-175.44, -182.69) * mm, "end": v(-174.61, -181.37) * mm});
            skLineSegment(sketch, "E2150", {"start": v(-174.61, -181.37) * mm, "end": v(-173.8, -180.04) * mm});
            skLineSegment(sketch, "E2151", {"start": v(-173.8, -180.04) * mm, "end": v(-173.01, -178.7) * mm});
            skLineSegment(sketch, "E2152", {"start": v(-173.01, -178.7) * mm, "end": v(-172.23, -177.35) * mm});
            skLineSegment(sketch, "E2153", {"start": v(-172.23, -177.35) * mm, "end": v(-171.46, -176) * mm});
            skLineSegment(sketch, "E2154", {"start": v(-171.46, -176) * mm, "end": v(-170.7, -174.63) * mm});
            skLineSegment(sketch, "E2155", {"start": v(-170.7, -174.63) * mm, "end": v(-169.96, -173.26) * mm});
            skLineSegment(sketch, "E2156", {"start": v(-169.96, -173.26) * mm, "end": v(-169.23, -171.87) * mm});
            skLineSegment(sketch, "E2157", {"start": v(-169.23, -171.87) * mm, "end": v(-168.5, -170.48) * mm});
            skLineSegment(sketch, "E2158", {"start": v(-168.5, -170.48) * mm, "end": v(-167.8, -169.08) * mm});
            skLineSegment(sketch, "E2159", {"start": v(-167.8, -169.08) * mm, "end": v(-167.12, -167.68) * mm});
            skLineSegment(sketch, "E2160", {"start": v(-167.12, -167.68) * mm, "end": v(-166.44, -166.26) * mm});
            skLineSegment(sketch, "E2161", {"start": v(-166.44, -166.26) * mm, "end": v(-165.78, -164.83) * mm});
            skLineSegment(sketch, "E2162", {"start": v(-165.78, -164.83) * mm, "end": v(-165.13, -163.4) * mm});
            skLineSegment(sketch, "E2163", {"start": v(-165.13, -163.4) * mm, "end": v(-164.5, -161.96) * mm});
            skLineSegment(sketch, "E2164", {"start": v(-164.5, -161.96) * mm, "end": v(-163.87, -160.51) * mm});
            skLineSegment(sketch, "E2165", {"start": v(-163.87, -160.51) * mm, "end": v(-163.26, -159.06) * mm});
            skLineSegment(sketch, "E2166", {"start": v(-163.26, -159.06) * mm, "end": v(-162.67, -157.6) * mm});
            skLineSegment(sketch, "E2167", {"start": v(-162.67, -157.6) * mm, "end": v(-162.09, -156.12) * mm});
            skLineSegment(sketch, "E2168", {"start": v(-162.09, -156.12) * mm, "end": v(-161.52, -154.64) * mm});
            skLineSegment(sketch, "E2169", {"start": v(-161.52, -154.64) * mm, "end": v(-160.97, -153.16) * mm});
            skLineSegment(sketch, "E2170", {"start": v(-160.97, -153.16) * mm, "end": v(-160.44, -151.67) * mm});
            skLineSegment(sketch, "E2171", {"start": v(-160.44, -151.67) * mm, "end": v(-159.91, -150.16) * mm});
            skLineSegment(sketch, "E2172", {"start": v(-159.91, -150.16) * mm, "end": v(-159.4, -148.66) * mm});
            skLineSegment(sketch, "E2173", {"start": v(-159.4, -148.66) * mm, "end": v(-158.91, -147.14) * mm});
            skLineSegment(sketch, "E2174", {"start": v(-158.91, -147.14) * mm, "end": v(-158.44, -145.62) * mm});
            skLineSegment(sketch, "E2175", {"start": v(-158.44, -145.62) * mm, "end": v(-157.97, -144.1) * mm});
            skLineSegment(sketch, "E2176", {"start": v(-157.97, -144.1) * mm, "end": v(-157.52, -142.56) * mm});
            skLineSegment(sketch, "E2177", {"start": v(-157.52, -142.56) * mm, "end": v(-157.09, -141.01) * mm});
            skLineSegment(sketch, "E2178", {"start": v(-157.09, -141.01) * mm, "end": v(-156.67, -139.47) * mm});
            skLineSegment(sketch, "E2179", {"start": v(-156.67, -139.47) * mm, "end": v(-156.27, -137.91) * mm});
            skLineSegment(sketch, "E2180", {"start": v(-156.27, -137.91) * mm, "end": v(-155.88, -136.35) * mm});
            skLineSegment(sketch, "E2181", {"start": v(-155.88, -136.35) * mm, "end": v(-155.61, -135.3) * mm});
            skLineSegment(sketch, "E2182", {"start": v(-155.61, -135.3) * mm, "end": v(-155.34, -134.3) * mm});
            skLineSegment(sketch, "E2183", {"start": v(-155.34, -134.3) * mm, "end": v(-155.08, -133.4) * mm});
            skLineSegment(sketch, "E2184", {"start": v(-155.08, -133.4) * mm, "end": v(-154.8, -132.54) * mm});
            skLineSegment(sketch, "E2185", {"start": v(-154.8, -132.54) * mm, "end": v(-154.54, -131.76) * mm});
            skLineSegment(sketch, "E2186", {"start": v(-154.54, -131.76) * mm, "end": v(-154.27, -131.05) * mm});
            skLineSegment(sketch, "E2187", {"start": v(-154.27, -131.05) * mm, "end": v(-154, -130.4) * mm});
            skLineSegment(sketch, "E2188", {"start": v(-154, -130.4) * mm, "end": v(-153.72, -129.83) * mm});
            skLineSegment(sketch, "E2189", {"start": v(-153.72, -129.83) * mm, "end": v(-153.45, -129.33) * mm});
            skLineSegment(sketch, "E2190", {"start": v(-153.45, -129.33) * mm, "end": v(-153.18, -128.9) * mm});
            skLineSegment(sketch, "E2191", {"start": v(-153.18, -128.9) * mm, "end": v(-152.9, -128.52) * mm});
            skLineSegment(sketch, "E2192", {"start": v(-152.9, -128.52) * mm, "end": v(-152.63, -128.22) * mm});
            skLineSegment(sketch, "E2193", {"start": v(-152.63, -128.22) * mm, "end": v(-152.36, -128) * mm});
            skLineSegment(sketch, "E2194", {"start": v(-152.36, -128) * mm, "end": v(-152.08, -127.83) * mm});
            skLineSegment(sketch, "E2195", {"start": v(-152.08, -127.83) * mm, "end": v(-151.94, -127.77) * mm});
            skLineSegment(sketch, "E2196", {"start": v(-151.94, -127.77) * mm, "end": v(-151.8, -127.73) * mm});
            skLineSegment(sketch, "E2197", {"start": v(-151.8, -127.73) * mm, "end": v(-151.67, -127.71) * mm});
            skLineSegment(sketch, "E2198", {"start": v(-151.67, -127.71) * mm, "end": v(-151.53, -127.7) * mm});
            skLineSegment(sketch, "E2199", {"start": v(-151.53, -127.7) * mm, "end": v(-151.4, -127.72) * mm});
            skLineSegment(sketch, "E2200", {"start": v(-151.4, -127.72) * mm, "end": v(-151.26, -127.75) * mm});
            skLineSegment(sketch, "E2201", {"start": v(-151.26, -127.75) * mm, "end": v(-151.12, -127.8) * mm});
            skLineSegment(sketch, "E2202", {"start": v(-151.12, -127.8) * mm, "end": v(-150.98, -127.86) * mm});
            skLineSegment(sketch, "E2203", {"start": v(-150.98, -127.86) * mm, "end": v(-150.7, -128.04) * mm});
            skLineSegment(sketch, "E2204", {"start": v(-150.7, -128.04) * mm, "end": v(-150.43, -128.28) * mm});
            skLineSegment(sketch, "E2205", {"start": v(-150.43, -128.28) * mm, "end": v(-150.16, -128.6) * mm});
            skLineSegment(sketch, "E2206", {"start": v(-150.16, -128.6) * mm, "end": v(-149.88, -128.98) * mm});
            skLineSegment(sketch, "E2207", {"start": v(-149.88, -128.98) * mm, "end": v(-149.6, -129.43) * mm});
            skLineSegment(sketch, "E2208", {"start": v(-149.6, -129.43) * mm, "end": v(-149.33, -129.95) * mm});
            skLineSegment(sketch, "E2209", {"start": v(-149.33, -129.95) * mm, "end": v(-149.06, -130.54) * mm});
            skLineSegment(sketch, "E2210", {"start": v(-149.06, -130.54) * mm, "end": v(-148.79, -131.19) * mm});
            skLineSegment(sketch, "E2211", {"start": v(-148.79, -131.19) * mm, "end": v(-148.52, -131.91) * mm});
            skLineSegment(sketch, "E2212", {"start": v(-148.52, -131.91) * mm, "end": v(-148.24, -132.7) * mm});
            skLineSegment(sketch, "E2213", {"start": v(-148.24, -132.7) * mm, "end": v(-147.97, -133.56) * mm});
            skLineSegment(sketch, "E2214", {"start": v(-147.97, -133.56) * mm, "end": v(-147.7, -134.48) * mm});
            skLineSegment(sketch, "E2215", {"start": v(-147.7, -134.48) * mm, "end": v(-147.43, -135.48) * mm});
            skLineSegment(sketch, "E2216", {"start": v(-147.43, -135.48) * mm, "end": v(-147.16, -136.54) * mm});
            skLineSegment(sketch, "E2217", {"start": v(-147.16, -136.54) * mm, "end": v(-146.77, -138.1) * mm});
            skLineSegment(sketch, "E2218", {"start": v(-146.77, -138.1) * mm, "end": v(-146.36, -139.65) * mm});
            skLineSegment(sketch, "E2219", {"start": v(-146.36, -139.65) * mm, "end": v(-145.94, -141.2) * mm});
            skLineSegment(sketch, "E2220", {"start": v(-145.94, -141.2) * mm, "end": v(-145.5, -142.74) * mm});
            skLineSegment(sketch, "E2221", {"start": v(-145.5, -142.74) * mm, "end": v(-145.04, -144.27) * mm});
            skLineSegment(sketch, "E2222", {"start": v(-145.04, -144.27) * mm, "end": v(-144.56, -145.8) * mm});
            skLineSegment(sketch, "E2223", {"start": v(-144.56, -145.8) * mm, "end": v(-144.07, -147.32) * mm});
            skLineSegment(sketch, "E2224", {"start": v(-144.07, -147.32) * mm, "end": v(-143.57, -148.83) * mm});
            skLineSegment(sketch, "E2225", {"start": v(-143.57, -148.83) * mm, "end": v(-143.04, -150.33) * mm});
            skLineSegment(sketch, "E2226", {"start": v(-143.04, -150.33) * mm, "end": v(-142.5, -151.83) * mm});
            skLineSegment(sketch, "E2227", {"start": v(-142.5, -151.83) * mm, "end": v(-141.95, -153.32) * mm});
            skLineSegment(sketch, "E2228", {"start": v(-141.95, -153.32) * mm, "end": v(-141.38, -154.8) * mm});
            skLineSegment(sketch, "E2229", {"start": v(-141.38, -154.8) * mm, "end": v(-140.8, -156.28) * mm});
            skLineSegment(sketch, "E2230", {"start": v(-140.8, -156.28) * mm, "end": v(-140.2, -157.75) * mm});
            skLineSegment(sketch, "E2231", {"start": v(-140.2, -157.75) * mm, "end": v(-139.58, -159.21) * mm});
            skLineSegment(sketch, "E2232", {"start": v(-139.58, -159.21) * mm, "end": v(-138.94, -160.67) * mm});
            skLineSegment(sketch, "E2233", {"start": v(-138.94, -160.67) * mm, "end": v(-138.3, -162.11) * mm});
            skLineSegment(sketch, "E2234", {"start": v(-138.3, -162.11) * mm, "end": v(-137.63, -163.55) * mm});
            skLineSegment(sketch, "E2235", {"start": v(-137.63, -163.55) * mm, "end": v(-136.96, -164.98) * mm});
            skLineSegment(sketch, "E2236", {"start": v(-136.96, -164.98) * mm, "end": v(-136.26, -166.4) * mm});
            skLineSegment(sketch, "E2237", {"start": v(-136.26, -166.4) * mm, "end": v(-135.56, -167.82) * mm});
            skLineSegment(sketch, "E2238", {"start": v(-135.56, -167.82) * mm, "end": v(-134.83, -169.22) * mm});
            skLineSegment(sketch, "E2239", {"start": v(-134.83, -169.22) * mm, "end": v(-134.1, -170.62) * mm});
            skLineSegment(sketch, "E2240", {"start": v(-134.1, -170.62) * mm, "end": v(-133.35, -172.01) * mm});
            skLineSegment(sketch, "E2241", {"start": v(-133.35, -172.01) * mm, "end": v(-132.58, -173.4) * mm});
            skLineSegment(sketch, "E2242", {"start": v(-132.58, -173.4) * mm, "end": v(-131.8, -174.76) * mm});
            skLineSegment(sketch, "E2243", {"start": v(-131.8, -174.76) * mm, "end": v(-131, -176.13) * mm});
            skLineSegment(sketch, "E2244", {"start": v(-131, -176.13) * mm, "end": v(-130.2, -177.48) * mm});
            skLineSegment(sketch, "E2245", {"start": v(-130.2, -177.48) * mm, "end": v(-129.38, -178.83) * mm});
            skLineSegment(sketch, "E2246", {"start": v(-129.38, -178.83) * mm, "end": v(-128.54, -180.16) * mm});
            skLineSegment(sketch, "E2247", {"start": v(-128.54, -180.16) * mm, "end": v(-127.7, -181.49) * mm});
            skLineSegment(sketch, "E2248", {"start": v(-127.7, -181.49) * mm, "end": v(-126.83, -182.8) * mm});
            skLineSegment(sketch, "E2249", {"start": v(-126.83, -182.8) * mm, "end": v(-125.95, -184.12) * mm});
            skLineSegment(sketch, "E2250", {"start": v(-125.95, -184.12) * mm, "end": v(-125.06, -185.42) * mm});
            skLineSegment(sketch, "E2251", {"start": v(-125.06, -185.42) * mm, "end": v(-124.16, -186.7) * mm});
            skLineSegment(sketch, "E2252", {"start": v(-124.16, -186.7) * mm, "end": v(-123.24, -187.99) * mm});
            skLineSegment(sketch, "E2253", {"start": v(-123.24, -187.99) * mm, "end": v(-122.31, -189.26) * mm});
            skLineSegment(sketch, "E2254", {"start": v(-122.31, -189.26) * mm, "end": v(-121.37, -190.52) * mm});
            skLineSegment(sketch, "E2255", {"start": v(-121.37, -190.52) * mm, "end": v(-120.41, -191.77) * mm});
            skLineSegment(sketch, "E2256", {"start": v(-120.41, -191.77) * mm, "end": v(-119.44, -193.01) * mm});
            skLineSegment(sketch, "E2257", {"start": v(-119.44, -193.01) * mm, "end": v(-118.46, -194.24) * mm});
            skLineSegment(sketch, "E2258", {"start": v(-118.46, -194.24) * mm, "end": v(-117.47, -195.47) * mm});
            skLineSegment(sketch, "E2259", {"start": v(-117.47, -195.47) * mm, "end": v(-116.46, -196.68) * mm});
            skLineSegment(sketch, "E2260", {"start": v(-116.46, -196.68) * mm, "end": v(-115.44, -197.88) * mm});
            skLineSegment(sketch, "E2261", {"start": v(-115.44, -197.88) * mm, "end": v(-114.41, -199.07) * mm});
            skLineSegment(sketch, "E2262", {"start": v(-114.41, -199.07) * mm, "end": v(-113.37, -200.25) * mm});
            skLineSegment(sketch, "E2263", {"start": v(-113.37, -200.25) * mm, "end": v(-112.31, -201.42) * mm});
            skLineSegment(sketch, "E2264", {"start": v(-112.31, -201.42) * mm, "end": v(-111.25, -202.58) * mm});
            skLineSegment(sketch, "E2265", {"start": v(-111.25, -202.58) * mm, "end": v(-110.17, -203.73) * mm});
            skLineSegment(sketch, "E2266", {"start": v(-110.17, -203.73) * mm, "end": v(-109.08, -204.86) * mm});
            skLineSegment(sketch, "E2267", {"start": v(-109.08, -204.86) * mm, "end": v(-107.98, -206) * mm});
            skLineSegment(sketch, "E2268", {"start": v(-107.98, -206) * mm, "end": v(-106.86, -207.1) * mm});
            skLineSegment(sketch, "E2269", {"start": v(-106.86, -207.1) * mm, "end": v(-105.74, -208.21) * mm});
            skLineSegment(sketch, "E2270", {"start": v(-105.74, -208.21) * mm, "end": v(-104.6, -209.3) * mm});
            skLineSegment(sketch, "E2271", {"start": v(-104.6, -209.3) * mm, "end": v(-103.45, -210.39) * mm});
            skLineSegment(sketch, "E2272", {"start": v(-103.45, -210.39) * mm, "end": v(-102.3, -211.46) * mm});
            skLineSegment(sketch, "E2273", {"start": v(-102.3, -211.46) * mm, "end": v(-101.12, -212.52) * mm});
            skLineSegment(sketch, "E2274", {"start": v(-101.12, -212.52) * mm, "end": v(-99.94, -213.56) * mm});
            skLineSegment(sketch, "E2275", {"start": v(-99.94, -213.56) * mm, "end": v(-98.75, -214.6) * mm});
            skLineSegment(sketch, "E2276", {"start": v(-98.75, -214.6) * mm, "end": v(-97.55, -215.62) * mm});
            skLineSegment(sketch, "E2277", {"start": v(-97.55, -215.62) * mm, "end": v(-96.34, -216.64) * mm});
            skLineSegment(sketch, "E2278", {"start": v(-96.34, -216.64) * mm, "end": v(-95.12, -217.64) * mm});
            skLineSegment(sketch, "E2279", {"start": v(-95.12, -217.64) * mm, "end": v(-93.88, -218.63) * mm});
            skLineSegment(sketch, "E2280", {"start": v(-93.88, -218.63) * mm, "end": v(-92.64, -219.6) * mm});
            skLineSegment(sketch, "E2281", {"start": v(-92.64, -219.6) * mm, "end": v(-91.38, -220.57) * mm});
            skLineSegment(sketch, "E2282", {"start": v(-91.38, -220.57) * mm, "end": v(-90.12, -221.52) * mm});
            skLineSegment(sketch, "E2283", {"start": v(-90.12, -221.52) * mm, "end": v(-88.85, -222.46) * mm});
            skLineSegment(sketch, "E2284", {"start": v(-88.85, -222.46) * mm, "end": v(-87.56, -223.38) * mm});
            skLineSegment(sketch, "E2285", {"start": v(-87.56, -223.38) * mm, "end": v(-86.27, -224.3) * mm});
            skLineSegment(sketch, "E2286", {"start": v(-86.27, -224.3) * mm, "end": v(-84.97, -225.2) * mm});
            skLineSegment(sketch, "E2287", {"start": v(-84.97, -225.2) * mm, "end": v(-83.66, -226.09) * mm});
            skLineSegment(sketch, "E2288", {"start": v(-83.66, -226.09) * mm, "end": v(-82.33, -226.97) * mm});
            skLineSegment(sketch, "E2289", {"start": v(-82.33, -226.97) * mm, "end": v(-81, -227.83) * mm});
            skLineSegment(sketch, "E2290", {"start": v(-81, -227.83) * mm, "end": v(-79.66, -228.68) * mm});
            skLineSegment(sketch, "E2291", {"start": v(-79.66, -228.68) * mm, "end": v(-78.31, -229.52) * mm});
            skLineSegment(sketch, "E2292", {"start": v(-78.31, -229.52) * mm, "end": v(-76.95, -230.34) * mm});
            skLineSegment(sketch, "E2293", {"start": v(-76.95, -230.34) * mm, "end": v(-75.59, -231.15) * mm});
            skLineSegment(sketch, "E2294", {"start": v(-75.59, -231.15) * mm, "end": v(-74.21, -231.95) * mm});
            skLineSegment(sketch, "E2295", {"start": v(-74.21, -231.95) * mm, "end": v(-72.83, -232.73) * mm});
            skLineSegment(sketch, "E2296", {"start": v(-72.83, -232.73) * mm, "end": v(-71.43, -233.5) * mm});
            skLineSegment(sketch, "E2297", {"start": v(-71.43, -233.5) * mm, "end": v(-70.03, -234.26) * mm});
            skLineSegment(sketch, "E2298", {"start": v(-70.03, -234.26) * mm, "end": v(-68.62, -235) * mm});
            skLineSegment(sketch, "E2299", {"start": v(-68.62, -235) * mm, "end": v(-67.2, -235.73) * mm});
            skLineSegment(sketch, "E2300", {"start": v(-67.2, -235.73) * mm, "end": v(-65.78, -236.44) * mm});
            skLineSegment(sketch, "E2301", {"start": v(-65.78, -236.44) * mm, "end": v(-64.34, -237.14) * mm});
            skLineSegment(sketch, "E2302", {"start": v(-64.34, -237.14) * mm, "end": v(-62.9, -237.83) * mm});
            skLineSegment(sketch, "E2303", {"start": v(-62.9, -237.83) * mm, "end": v(-61.45, -238.5) * mm});
            skLineSegment(sketch, "E2304", {"start": v(-61.45, -238.5) * mm, "end": v(-60, -239.16) * mm});
            skLineSegment(sketch, "E2305", {"start": v(-60, -239.16) * mm, "end": v(-58.53, -239.8) * mm});
            skLineSegment(sketch, "E2306", {"start": v(-58.53, -239.8) * mm, "end": v(-57.06, -240.43) * mm});
            skLineSegment(sketch, "E2307", {"start": v(-57.06, -240.43) * mm, "end": v(-55.58, -241.05) * mm});
            skLineSegment(sketch, "E2308", {"start": v(-55.58, -241.05) * mm, "end": v(-54.09, -241.65) * mm});
            skLineSegment(sketch, "E2309", {"start": v(-54.09, -241.65) * mm, "end": v(-52.6, -242.23) * mm});
            skLineSegment(sketch, "E2310", {"start": v(-52.6, -242.23) * mm, "end": v(-51.1, -242.8) * mm});
            skLineSegment(sketch, "E2311", {"start": v(-51.1, -242.8) * mm, "end": v(-49.58, -243.36) * mm});
            skLineSegment(sketch, "E2312", {"start": v(-49.58, -243.36) * mm, "end": v(-48.07, -243.9) * mm});
            skLineSegment(sketch, "E2313", {"start": v(-48.07, -243.9) * mm, "end": v(-46.55, -244.42) * mm});
            skLineSegment(sketch, "E2314", {"start": v(-46.55, -244.42) * mm, "end": v(-45.02, -244.93) * mm});
            skLineSegment(sketch, "E2315", {"start": v(-45.02, -244.93) * mm, "end": v(-43.48, -245.42) * mm});
            skLineSegment(sketch, "E2316", {"start": v(-43.48, -245.42) * mm, "end": v(-41.94, -245.9) * mm});
            skLineSegment(sketch, "E2317", {"start": v(-41.94, -245.9) * mm, "end": v(-40.4, -246.37) * mm});
            skLineSegment(sketch, "E2318", {"start": v(-40.4, -246.37) * mm, "end": v(-38.84, -246.81) * mm});
            skLineSegment(sketch, "E2319", {"start": v(-38.84, -246.81) * mm, "end": v(-37.28, -247.25) * mm});
            skLineSegment(sketch, "E2320", {"start": v(-37.28, -247.25) * mm, "end": v(-35.71, -247.66) * mm});
            skLineSegment(sketch, "E2321", {"start": v(-35.71, -247.66) * mm, "end": v(-34.14, -248.06) * mm});
            skLineSegment(sketch, "E2322", {"start": v(-34.14, -248.06) * mm, "end": v(-32.56, -248.45) * mm});
            skLineSegment(sketch, "E2323", {"start": v(-32.56, -248.45) * mm, "end": v(-30.98, -248.81) * mm});
            skLineSegment(sketch, "E2324", {"start": v(-30.98, -248.81) * mm, "end": v(-29.39, -249.17) * mm});
            skLineSegment(sketch, "E2325", {"start": v(-29.39, -249.17) * mm, "end": v(-27.8, -249.5) * mm});
            skLineSegment(sketch, "E2326", {"start": v(-27.8, -249.5) * mm, "end": v(-26.2, -249.82) * mm});
            skLineSegment(sketch, "E2327", {"start": v(-26.2, -249.82) * mm, "end": v(-24.59, -250.12) * mm});
            skLineSegment(sketch, "E2328", {"start": v(-24.59, -250.12) * mm, "end": v(-22.98, -250.41) * mm});
            skLineSegment(sketch, "E2329", {"start": v(-22.98, -250.41) * mm, "end": v(-21.36, -250.68) * mm});
            skLineSegment(sketch, "E2330", {"start": v(-21.36, -250.68) * mm, "end": v(-19.74, -250.93) * mm});
            skLineSegment(sketch, "E2331", {"start": v(-19.74, -250.93) * mm, "end": v(-18.11, -251.17) * mm});
            skLineSegment(sketch, "E2332", {"start": v(-18.11, -251.17) * mm, "end": v(-16.48, -251.39) * mm});
            skLineSegment(sketch, "E2333", {"start": v(-16.48, -251.39) * mm, "end": v(-14.85, -251.6) * mm});
            skLineSegment(sketch, "E2334", {"start": v(-14.85, -251.6) * mm, "end": v(-13.2, -251.78) * mm});
            skLineSegment(sketch, "E2335", {"start": v(-13.2, -251.78) * mm, "end": v(-11.57, -251.94) * mm});
            skLineSegment(sketch, "E2336", {"start": v(-11.57, -251.94) * mm, "end": v(-9.92, -252.1) * mm});
            skLineSegment(sketch, "E2337", {"start": v(-9.92, -252.1) * mm, "end": v(-8.26, -252.23) * mm});
            skLineSegment(sketch, "E2338", {"start": v(-8.26, -252.23) * mm, "end": v(-6.6, -252.34) * mm});
            skLineSegment(sketch, "E2339", {"start": v(-6.6, -252.34) * mm, "end": v(-4.95, -252.44) * mm});
            skLineSegment(sketch, "E2340", {"start": v(-4.95, -252.44) * mm, "end": v(-3.28, -252.52) * mm});
            skLineSegment(sketch, "E2341", {"start": v(-3.28, -252.52) * mm, "end": v(-1.62, -252.58) * mm});
            skLineSegment(sketch, "E2342", {"start": v(-1.62, -252.58) * mm, "end": v(0.06, -252.63) * mm});
            skLineSegment(sketch, "E2343", {"start": v(0.06, -252.63) * mm, "end": v(1.73, -252.66) * mm});
            skLineSegment(sketch, "E2344", {"start": v(1.73, -252.66) * mm, "end": v(3.41, -252.67) * mm});
            skLineSegment(sketch, "E2345", {"start": v(3.41, -252.67) * mm, "end": v(5.38, -252.65) * mm});
            skLineSegment(sketch, "E2346", {"start": v(5.38, -252.65) * mm, "end": v(7.35, -252.62) * mm});
            skLineSegment(sketch, "E2347", {"start": v(7.35, -252.62) * mm, "end": v(9.3, -252.55) * mm});
            skLineSegment(sketch, "E2348", {"start": v(9.3, -252.55) * mm, "end": v(11.26, -252.47) * mm});
            skLineSegment(sketch, "E2349", {"start": v(11.26, -252.47) * mm, "end": v(13.2, -252.36) * mm});
            skLineSegment(sketch, "E2350", {"start": v(13.2, -252.36) * mm, "end": v(15.15, -252.22) * mm});
            skLineSegment(sketch, "E2351", {"start": v(15.15, -252.22) * mm, "end": v(17.08, -252.06) * mm});
            skLineSegment(sketch, "E2352", {"start": v(17.08, -252.06) * mm, "end": v(19.01, -251.88) * mm});
            skLineSegment(sketch, "E2353", {"start": v(19.01, -251.88) * mm, "end": v(20.93, -251.67) * mm});
            skLineSegment(sketch, "E2354", {"start": v(20.93, -251.67) * mm, "end": v(22.84, -251.44) * mm});
            skLineSegment(sketch, "E2355", {"start": v(22.84, -251.44) * mm, "end": v(24.75, -251.19) * mm});
            skLineSegment(sketch, "E2356", {"start": v(24.75, -251.19) * mm, "end": v(26.65, -250.9) * mm});
            skLineSegment(sketch, "E2357", {"start": v(26.65, -250.9) * mm, "end": v(28.54, -250.6) * mm});
            skLineSegment(sketch, "E2358", {"start": v(28.54, -250.6) * mm, "end": v(30.42, -250.28) * mm});
            skLineSegment(sketch, "E2359", {"start": v(30.42, -250.28) * mm, "end": v(32.3, -249.94) * mm});
            skLineSegment(sketch, "E2360", {"start": v(32.3, -249.94) * mm, "end": v(34.16, -249.57) * mm});
            skLineSegment(sketch, "E2361", {"start": v(34.16, -249.57) * mm, "end": v(36.02, -249.17) * mm});
            skLineSegment(sketch, "E2362", {"start": v(36.02, -249.17) * mm, "end": v(37.87, -248.76) * mm});
            skLineSegment(sketch, "E2363", {"start": v(37.87, -248.76) * mm, "end": v(39.7, -248.32) * mm});
            skLineSegment(sketch, "E2364", {"start": v(39.7, -248.32) * mm, "end": v(41.54, -247.86) * mm});
            skLineSegment(sketch, "E2365", {"start": v(41.54, -247.86) * mm, "end": v(43.36, -247.38) * mm});
            skLineSegment(sketch, "E2366", {"start": v(43.36, -247.38) * mm, "end": v(45.18, -246.88) * mm});
            skLineSegment(sketch, "E2367", {"start": v(45.18, -246.88) * mm, "end": v(46.98, -246.35) * mm});
            skLineSegment(sketch, "E2368", {"start": v(46.98, -246.35) * mm, "end": v(48.78, -245.8) * mm});
            skLineSegment(sketch, "E2369", {"start": v(48.78, -245.8) * mm, "end": v(50.57, -245.24) * mm});
            skLineSegment(sketch, "E2370", {"start": v(50.57, -245.24) * mm, "end": v(52.34, -244.65) * mm});
            skLineSegment(sketch, "E2371", {"start": v(52.34, -244.65) * mm, "end": v(54.11, -244.04) * mm});
            skLineSegment(sketch, "E2372", {"start": v(54.11, -244.04) * mm, "end": v(55.87, -243.4) * mm});
            skLineSegment(sketch, "E2373", {"start": v(55.87, -243.4) * mm, "end": v(57.62, -242.76) * mm});
            skLineSegment(sketch, "E2374", {"start": v(57.62, -242.76) * mm, "end": v(59.35, -242.08) * mm});
            skLineSegment(sketch, "E2375", {"start": v(59.35, -242.08) * mm, "end": v(61.08, -241.4) * mm});
            skLineSegment(sketch, "E2376", {"start": v(61.08, -241.4) * mm, "end": v(62.8, -240.68) * mm});
            skLineSegment(sketch, "E2377", {"start": v(62.8, -240.68) * mm, "end": v(64.5, -239.94) * mm});
            skLineSegment(sketch, "E2378", {"start": v(64.5, -239.94) * mm, "end": v(66.2, -239.19) * mm});
            skLineSegment(sketch, "E2379", {"start": v(66.2, -239.19) * mm, "end": v(67.88, -238.41) * mm});
            skLineSegment(sketch, "E2380", {"start": v(67.88, -238.41) * mm, "end": v(69.56, -237.62) * mm});
            skLineSegment(sketch, "E2381", {"start": v(69.56, -237.62) * mm, "end": v(71.22, -236.8) * mm});
            skLineSegment(sketch, "E2382", {"start": v(71.22, -236.8) * mm, "end": v(72.87, -235.98) * mm});
            skLineSegment(sketch, "E2383", {"start": v(72.87, -235.98) * mm, "end": v(74.5, -235.12) * mm});
            skLineSegment(sketch, "E2384", {"start": v(74.5, -235.12) * mm, "end": v(76.14, -234.25) * mm});
            skLineSegment(sketch, "E2385", {"start": v(76.14, -234.25) * mm, "end": v(77.75, -233.36) * mm});
            skLineSegment(sketch, "E2386", {"start": v(77.75, -233.36) * mm, "end": v(79.35, -232.45) * mm});
            skLineSegment(sketch, "E2387", {"start": v(79.35, -232.45) * mm, "end": v(80.95, -231.52) * mm});
            skLineSegment(sketch, "E2388", {"start": v(80.95, -231.52) * mm, "end": v(82.52, -230.58) * mm});
            skLineSegment(sketch, "E2389", {"start": v(82.52, -230.58) * mm, "end": v(84.1, -229.61) * mm});
            skLineSegment(sketch, "E2390", {"start": v(84.1, -229.61) * mm, "end": v(85.64, -228.63) * mm});
            skLineSegment(sketch, "E2391", {"start": v(85.64, -228.63) * mm, "end": v(87.19, -227.63) * mm});
            skLineSegment(sketch, "E2392", {"start": v(87.19, -227.63) * mm, "end": v(88.71, -226.61) * mm});
            skLineSegment(sketch, "E2393", {"start": v(88.71, -226.61) * mm, "end": v(90.23, -225.57) * mm});
            skLineSegment(sketch, "E2394", {"start": v(90.23, -225.57) * mm, "end": v(91.73, -224.52) * mm});
            skLineSegment(sketch, "E2395", {"start": v(91.73, -224.52) * mm, "end": v(93.22, -223.45) * mm});
            skLineSegment(sketch, "E2396", {"start": v(93.22, -223.45) * mm, "end": v(94.7, -222.36) * mm});
            skLineSegment(sketch, "E2397", {"start": v(94.7, -222.36) * mm, "end": v(96.16, -221.25) * mm});
            skLineSegment(sketch, "E2398", {"start": v(96.16, -221.25) * mm, "end": v(97.6, -220.13) * mm});
            skLineSegment(sketch, "E2399", {"start": v(97.6, -220.13) * mm, "end": v(99.04, -218.98) * mm});
            skLineSegment(sketch, "E2400", {"start": v(99.04, -218.98) * mm, "end": v(100.46, -217.83) * mm});
            skLineSegment(sketch, "E2401", {"start": v(100.46, -217.83) * mm, "end": v(101.87, -216.65) * mm});
            skLineSegment(sketch, "E2402", {"start": v(101.87, -216.65) * mm, "end": v(103.26, -215.46) * mm});
            skLineSegment(sketch, "E2403", {"start": v(103.26, -215.46) * mm, "end": v(104.63, -214.26) * mm});
            skLineSegment(sketch, "E2404", {"start": v(104.63, -214.26) * mm, "end": v(106, -213.03) * mm});
            skLineSegment(sketch, "E2405", {"start": v(106, -213.03) * mm, "end": v(107.34, -211.8) * mm});
            skLineSegment(sketch, "E2406", {"start": v(107.34, -211.8) * mm, "end": v(108.68, -210.54) * mm});
            skLineSegment(sketch, "E2407", {"start": v(108.68, -210.54) * mm, "end": v(110, -209.27) * mm});
            skLineSegment(sketch, "E2408", {"start": v(110, -209.27) * mm, "end": v(111.3, -207.98) * mm});
            skLineSegment(sketch, "E2409", {"start": v(111.3, -207.98) * mm, "end": v(112.58, -206.68) * mm});
            skLineSegment(sketch, "E2410", {"start": v(112.58, -206.68) * mm, "end": v(113.85, -205.36) * mm});
            skLineSegment(sketch, "E2411", {"start": v(113.85, -205.36) * mm, "end": v(115.1, -204.03) * mm});
            skLineSegment(sketch, "E2412", {"start": v(115.1, -204.03) * mm, "end": v(116.35, -202.68) * mm});
            skLineSegment(sketch, "E2413", {"start": v(116.35, -202.68) * mm, "end": v(117.57, -201.32) * mm});
            skLineSegment(sketch, "E2414", {"start": v(117.57, -201.32) * mm, "end": v(118.78, -199.94) * mm});
            skLineSegment(sketch, "E2415", {"start": v(118.78, -199.94) * mm, "end": v(119.97, -198.55) * mm});
            skLineSegment(sketch, "E2416", {"start": v(119.97, -198.55) * mm, "end": v(121.14, -197.15) * mm});
            skLineSegment(sketch, "E2417", {"start": v(121.14, -197.15) * mm, "end": v(122.3, -195.73) * mm});
            skLineSegment(sketch, "E2418", {"start": v(122.3, -195.73) * mm, "end": v(123.44, -194.3) * mm});
            skLineSegment(sketch, "E2419", {"start": v(123.44, -194.3) * mm, "end": v(124.56, -192.84) * mm});
            skLineSegment(sketch, "E2420", {"start": v(124.56, -192.84) * mm, "end": v(125.67, -191.38) * mm});
            skLineSegment(sketch, "E2421", {"start": v(125.67, -191.38) * mm, "end": v(126.76, -189.9) * mm});
            skLineSegment(sketch, "E2422", {"start": v(126.76, -189.9) * mm, "end": v(127.83, -188.42) * mm});
            skLineSegment(sketch, "E2423", {"start": v(127.83, -188.42) * mm, "end": v(128.89, -186.92) * mm});
            skLineSegment(sketch, "E2424", {"start": v(128.89, -186.92) * mm, "end": v(129.92, -185.4) * mm});
            skLineSegment(sketch, "E2425", {"start": v(129.92, -185.4) * mm, "end": v(130.94, -183.87) * mm});
            skLineSegment(sketch, "E2426", {"start": v(130.94, -183.87) * mm, "end": v(131.94, -182.33) * mm});
            skLineSegment(sketch, "E2427", {"start": v(131.94, -182.33) * mm, "end": v(132.93, -180.78) * mm});
            skLineSegment(sketch, "E2428", {"start": v(132.93, -180.78) * mm, "end": v(133.9, -179.21) * mm});
            skLineSegment(sketch, "E2429", {"start": v(133.9, -179.21) * mm, "end": v(134.84, -177.63) * mm});
            skLineSegment(sketch, "E2430", {"start": v(134.84, -177.63) * mm, "end": v(135.77, -176.04) * mm});
            skLineSegment(sketch, "E2431", {"start": v(135.77, -176.04) * mm, "end": v(136.68, -174.44) * mm});
            skLineSegment(sketch, "E2432", {"start": v(136.68, -174.44) * mm, "end": v(137.57, -172.82) * mm});
            skLineSegment(sketch, "E2433", {"start": v(137.57, -172.82) * mm, "end": v(138.44, -171.2) * mm});
            skLineSegment(sketch, "E2434", {"start": v(138.44, -171.2) * mm, "end": v(139.29, -169.56) * mm});
            skLineSegment(sketch, "E2435", {"start": v(139.29, -169.56) * mm, "end": v(140.12, -167.9) * mm});
            skLineSegment(sketch, "E2436", {"start": v(140.12, -167.9) * mm, "end": v(140.94, -166.24) * mm});
            skLineSegment(sketch, "E2437", {"start": v(140.94, -166.24) * mm, "end": v(141.73, -164.57) * mm});
            skLineSegment(sketch, "E2438", {"start": v(141.73, -164.57) * mm, "end": v(142.5, -162.89) * mm});
            skLineSegment(sketch, "E2439", {"start": v(142.5, -162.89) * mm, "end": v(143.26, -161.2) * mm});
            skLineSegment(sketch, "E2440", {"start": v(143.26, -161.2) * mm, "end": v(144, -159.48) * mm});
            skLineSegment(sketch, "E2441", {"start": v(144, -159.48) * mm, "end": v(144.7, -157.77) * mm});
            skLineSegment(sketch, "E2442", {"start": v(144.7, -157.77) * mm, "end": v(145.4, -156.04) * mm});
            skLineSegment(sketch, "E2443", {"start": v(145.4, -156.04) * mm, "end": v(146.07, -154.3) * mm});
            skLineSegment(sketch, "E2444", {"start": v(146.07, -154.3) * mm, "end": v(146.72, -152.56) * mm});
            skLineSegment(sketch, "E2445", {"start": v(146.72, -152.56) * mm, "end": v(147.35, -150.8) * mm});
            skLineSegment(sketch, "E2446", {"start": v(147.35, -150.8) * mm, "end": v(147.96, -149.03) * mm});
            skLineSegment(sketch, "E2447", {"start": v(147.96, -149.03) * mm, "end": v(148.55, -147.25) * mm});
            skLineSegment(sketch, "E2448", {"start": v(148.55, -147.25) * mm, "end": v(149.12, -145.47) * mm});
            skLineSegment(sketch, "E2449", {"start": v(149.12, -145.47) * mm, "end": v(149.67, -143.67) * mm});
            skLineSegment(sketch, "E2450", {"start": v(149.67, -143.67) * mm, "end": v(150.2, -141.87) * mm});
            skLineSegment(sketch, "E2451", {"start": v(150.2, -141.87) * mm, "end": v(150.7, -140.05) * mm});
            skLineSegment(sketch, "E2452", {"start": v(150.7, -140.05) * mm, "end": v(151.18, -138.23) * mm});
            skLineSegment(sketch, "E2453", {"start": v(151.18, -138.23) * mm, "end": v(151.64, -136.4) * mm});
            skLineSegment(sketch, "E2454", {"start": v(151.64, -136.4) * mm, "end": v(152.07, -134.55) * mm});
            skLineSegment(sketch, "E2455", {"start": v(152.07, -134.55) * mm, "end": v(152.49, -132.7) * mm});
            skLineSegment(sketch, "E2456", {"start": v(152.49, -132.7) * mm, "end": v(152.88, -130.85) * mm});
            skLineSegment(sketch, "E2457", {"start": v(152.88, -130.85) * mm, "end": v(153.25, -128.98) * mm});
            skLineSegment(sketch, "E2458", {"start": v(153.25, -128.98) * mm, "end": v(153.6, -127.1) * mm});
            skLineSegment(sketch, "E2459", {"start": v(153.6, -127.1) * mm, "end": v(153.92, -125.22) * mm});
            skLineSegment(sketch, "E2460", {"start": v(153.92, -125.22) * mm, "end": v(154.22, -123.33) * mm});
            skLineSegment(sketch, "E2461", {"start": v(154.22, -123.33) * mm, "end": v(154.5, -121.44) * mm});
            skLineSegment(sketch, "E2462", {"start": v(154.5, -121.44) * mm, "end": v(154.75, -119.53) * mm});
            skLineSegment(sketch, "E2463", {"start": v(154.75, -119.53) * mm, "end": v(154.99, -117.62) * mm});
            skLineSegment(sketch, "E2464", {"start": v(154.99, -117.62) * mm, "end": v(155.2, -115.7) * mm});
            skLineSegment(sketch, "E2465", {"start": v(155.2, -115.7) * mm, "end": v(155.38, -113.77) * mm});
            skLineSegment(sketch, "E2466", {"start": v(155.38, -113.77) * mm, "end": v(155.54, -111.84) * mm});
            skLineSegment(sketch, "E2467", {"start": v(155.54, -111.84) * mm, "end": v(155.67, -109.9) * mm});
            skLineSegment(sketch, "E2468", {"start": v(155.67, -109.9) * mm, "end": v(155.78, -107.95) * mm});
            skLineSegment(sketch, "E2469", {"start": v(155.78, -107.95) * mm, "end": v(155.87, -106) * mm});
            skLineSegment(sketch, "E2470", {"start": v(155.87, -106) * mm, "end": v(155.93, -104.04) * mm});
            skLineSegment(sketch, "E2471", {"start": v(155.93, -104.04) * mm, "end": v(155.97, -102.07) * mm});
            skLineSegment(sketch, "E2472", {"start": v(155.97, -102.07) * mm, "end": v(155.98, -100.1) * mm});
            skLineSegment(sketch, "E2473", {"start": v(155.98, -100.1) * mm, "end": v(155.97, -98.44) * mm});
            skLineSegment(sketch, "E2474", {"start": v(155.97, -98.44) * mm, "end": v(155.94, -96.78) * mm});
            skLineSegment(sketch, "E2475", {"start": v(155.94, -96.78) * mm, "end": v(155.9, -95.13) * mm});
            skLineSegment(sketch, "E2476", {"start": v(155.9, -95.13) * mm, "end": v(155.84, -93.48) * mm});
            skLineSegment(sketch, "E2477", {"start": v(155.84, -93.48) * mm, "end": v(155.76, -91.84) * mm});
            skLineSegment(sketch, "E2478", {"start": v(155.76, -91.84) * mm, "end": v(155.66, -90.2) * mm});
            skLineSegment(sketch, "E2479", {"start": v(155.66, -90.2) * mm, "end": v(155.55, -88.57) * mm});
            skLineSegment(sketch, "E2480", {"start": v(155.55, -88.57) * mm, "end": v(155.42, -86.94) * mm});
            skLineSegment(sketch, "E2481", {"start": v(155.42, -86.94) * mm, "end": v(155.27, -85.32) * mm});
            skLineSegment(sketch, "E2482", {"start": v(155.27, -85.32) * mm, "end": v(155.1, -83.7) * mm});
            skLineSegment(sketch, "E2483", {"start": v(155.1, -83.7) * mm, "end": v(154.93, -82.08) * mm});
            skLineSegment(sketch, "E2484", {"start": v(154.93, -82.08) * mm, "end": v(154.73, -80.47) * mm});
            skLineSegment(sketch, "E2485", {"start": v(154.73, -80.47) * mm, "end": v(154.51, -78.87) * mm});
            skLineSegment(sketch, "E2486", {"start": v(154.51, -78.87) * mm, "end": v(154.28, -77.27) * mm});
            skLineSegment(sketch, "E2487", {"start": v(154.28, -77.27) * mm, "end": v(154.04, -75.68) * mm});
            skLineSegment(sketch, "E2488", {"start": v(154.04, -75.68) * mm, "end": v(153.77, -74.1) * mm});
            skLineSegment(sketch, "E2489", {"start": v(153.77, -74.1) * mm, "end": v(153.5, -72.5) * mm});
            skLineSegment(sketch, "E2490", {"start": v(153.5, -72.5) * mm, "end": v(153.2, -70.93) * mm});
            skLineSegment(sketch, "E2491", {"start": v(153.2, -70.93) * mm, "end": v(152.88, -69.36) * mm});
            skLineSegment(sketch, "E2492", {"start": v(152.88, -69.36) * mm, "end": v(152.55, -67.8) * mm});
            skLineSegment(sketch, "E2493", {"start": v(152.55, -67.8) * mm, "end": v(152.2, -66.24) * mm});
            skLineSegment(sketch, "E2494", {"start": v(152.2, -66.24) * mm, "end": v(151.85, -64.69) * mm});
            skLineSegment(sketch, "E2495", {"start": v(151.85, -64.69) * mm, "end": v(151.47, -63.14) * mm});
            skLineSegment(sketch, "E2496", {"start": v(151.47, -63.14) * mm, "end": v(151.08, -61.6) * mm});
            skLineSegment(sketch, "E2497", {"start": v(151.08, -61.6) * mm, "end": v(150.67, -60.06) * mm});
            skLineSegment(sketch, "E2498", {"start": v(150.67, -60.06) * mm, "end": v(150.25, -58.54) * mm});
            skLineSegment(sketch, "E2499", {"start": v(150.25, -58.54) * mm, "end": v(149.81, -57.02) * mm});
            skLineSegment(sketch, "E2500", {"start": v(149.81, -57.02) * mm, "end": v(149.36, -55.5) * mm});
            skLineSegment(sketch, "E2501", {"start": v(149.36, -55.5) * mm, "end": v(148.89, -54) * mm});
            skLineSegment(sketch, "E2502", {"start": v(148.89, -54) * mm, "end": v(148.4, -52.5) * mm});
            skLineSegment(sketch, "E2503", {"start": v(148.4, -52.5) * mm, "end": v(147.9, -51) * mm});
            skLineSegment(sketch, "E2504", {"start": v(147.9, -51) * mm, "end": v(147.4, -49.5) * mm});
            skLineSegment(sketch, "E2505", {"start": v(147.4, -49.5) * mm, "end": v(146.86, -48.03) * mm});
            skLineSegment(sketch, "E2506", {"start": v(146.86, -48.03) * mm, "end": v(146.32, -46.55) * mm});
            skLineSegment(sketch, "E2507", {"start": v(146.32, -46.55) * mm, "end": v(145.76, -45.09) * mm});
            skLineSegment(sketch, "E2508", {"start": v(145.76, -45.09) * mm, "end": v(145.19, -43.63) * mm});
            skLineSegment(sketch, "E2509", {"start": v(145.19, -43.63) * mm, "end": v(144.6, -42.18) * mm});
            skLineSegment(sketch, "E2510", {"start": v(144.6, -42.18) * mm, "end": v(144, -40.73) * mm});
            skLineSegment(sketch, "E2511", {"start": v(144, -40.73) * mm, "end": v(143.38, -39.3) * mm});
            skLineSegment(sketch, "E2512", {"start": v(143.38, -39.3) * mm, "end": v(142.75, -37.87) * mm});
            skLineSegment(sketch, "E2513", {"start": v(142.75, -37.87) * mm, "end": v(142.1, -36.44) * mm});
            skLineSegment(sketch, "E2514", {"start": v(142.1, -36.44) * mm, "end": v(141.45, -35.03) * mm});
            skLineSegment(sketch, "E2515", {"start": v(141.45, -35.03) * mm, "end": v(140.78, -33.63) * mm});
            skLineSegment(sketch, "E2516", {"start": v(140.78, -33.63) * mm, "end": v(140.09, -32.23) * mm});
            skLineSegment(sketch, "E2517", {"start": v(140.09, -32.23) * mm, "end": v(139.39, -30.84) * mm});
            skLineSegment(sketch, "E2518", {"start": v(139.39, -30.84) * mm, "end": v(138.67, -29.46) * mm});
            skLineSegment(sketch, "E2519", {"start": v(138.67, -29.46) * mm, "end": v(137.95, -28.08) * mm});
            skLineSegment(sketch, "E2520", {"start": v(137.95, -28.08) * mm, "end": v(137.2, -26.72) * mm});
            skLineSegment(sketch, "E2521", {"start": v(137.2, -26.72) * mm, "end": v(136.45, -25.36) * mm});
            skLineSegment(sketch, "E2522", {"start": v(136.45, -25.36) * mm, "end": v(135.68, -24.01) * mm});
            skLineSegment(sketch, "E2523", {"start": v(135.68, -24.01) * mm, "end": v(134.9, -22.67) * mm});
            skLineSegment(sketch, "E2524", {"start": v(134.9, -22.67) * mm, "end": v(134.1, -21.34) * mm});
            skLineSegment(sketch, "E2525", {"start": v(134.1, -21.34) * mm, "end": v(133.3, -20.02) * mm});
            skLineSegment(sketch, "E2526", {"start": v(133.3, -20.02) * mm, "end": v(132.48, -18.7) * mm});
            skLineSegment(sketch, "E2527", {"start": v(132.48, -18.7) * mm, "end": v(131.65, -17.4) * mm});
            skLineSegment(sketch, "E2528", {"start": v(131.65, -17.4) * mm, "end": v(130.8, -16.1) * mm});
            skLineSegment(sketch, "E2529", {"start": v(130.8, -16.1) * mm, "end": v(129.94, -14.82) * mm});
            skLineSegment(sketch, "E2530", {"start": v(129.94, -14.82) * mm, "end": v(129.07, -13.55) * mm});
            skLineSegment(sketch, "E2531", {"start": v(129.07, -13.55) * mm, "end": v(128.19, -12.28) * mm});
            skLineSegment(sketch, "E2532", {"start": v(128.19, -12.28) * mm, "end": v(127.29, -11.02) * mm});
            skLineSegment(sketch, "E2533", {"start": v(127.29, -11.02) * mm, "end": v(126.38, -9.77) * mm});
            skLineSegment(sketch, "E2534", {"start": v(126.38, -9.77) * mm, "end": v(125.46, -8.53) * mm});
            skLineSegment(sketch, "E2535", {"start": v(125.46, -8.53) * mm, "end": v(124.53, -7.3) * mm});
            skLineSegment(sketch, "E2536", {"start": v(124.53, -7.3) * mm, "end": v(123.58, -6.08) * mm});
            skLineSegment(sketch, "E2537", {"start": v(-235.61, 154.42) * mm, "end": v(-236.24, 154.43) * mm});
            skLineSegment(sketch, "E2538", {"start": v(-236.24, 154.43) * mm, "end": v(-236.86, 154.48) * mm});
            skLineSegment(sketch, "E2539", {"start": v(-236.86, 154.48) * mm, "end": v(-237.47, 154.56) * mm});
            skLineSegment(sketch, "E2540", {"start": v(-237.47, 154.56) * mm, "end": v(-238.08, 154.66) * mm});
            skLineSegment(sketch, "E2541", {"start": v(-238.08, 154.66) * mm, "end": v(-238.67, 154.8) * mm});
            skLineSegment(sketch, "E2542", {"start": v(-238.67, 154.8) * mm, "end": v(-239.25, 154.96) * mm});
            skLineSegment(sketch, "E2543", {"start": v(-239.25, 154.96) * mm, "end": v(-239.81, 155.16) * mm});
            skLineSegment(sketch, "E2544", {"start": v(-239.81, 155.16) * mm, "end": v(-240.37, 155.38) * mm});
            skLineSegment(sketch, "E2545", {"start": v(-240.37, 155.38) * mm, "end": v(-240.9, 155.62) * mm});
            skLineSegment(sketch, "E2546", {"start": v(-240.9, 155.62) * mm, "end": v(-241.43, 155.89) * mm});
            skLineSegment(sketch, "E2547", {"start": v(-241.43, 155.89) * mm, "end": v(-241.95, 156.18) * mm});
            skLineSegment(sketch, "E2548", {"start": v(-241.95, 156.18) * mm, "end": v(-242.44, 156.5) * mm});
            skLineSegment(sketch, "E2549", {"start": v(-242.44, 156.5) * mm, "end": v(-242.92, 156.84) * mm});
            skLineSegment(sketch, "E2550", {"start": v(-242.92, 156.84) * mm, "end": v(-243.38, 157.2) * mm});
            skLineSegment(sketch, "E2551", {"start": v(-243.38, 157.2) * mm, "end": v(-243.82, 157.59) * mm});
            skLineSegment(sketch, "E2552", {"start": v(-243.82, 157.59) * mm, "end": v(-244.25, 158) * mm});
            skLineSegment(sketch, "E2553", {"start": v(-244.25, 158) * mm, "end": v(-244.65, 158.42) * mm});
            skLineSegment(sketch, "E2554", {"start": v(-244.65, 158.42) * mm, "end": v(-245.04, 158.86) * mm});
            skLineSegment(sketch, "E2555", {"start": v(-245.04, 158.86) * mm, "end": v(-245.4, 159.32) * mm});
            skLineSegment(sketch, "E2556", {"start": v(-245.4, 159.32) * mm, "end": v(-245.74, 159.8) * mm});
            skLineSegment(sketch, "E2557", {"start": v(-245.74, 159.8) * mm, "end": v(-246.06, 160.3) * mm});
            skLineSegment(sketch, "E2558", {"start": v(-246.06, 160.3) * mm, "end": v(-246.35, 160.8) * mm});
            skLineSegment(sketch, "E2559", {"start": v(-246.35, 160.8) * mm, "end": v(-246.62, 161.33) * mm});
            skLineSegment(sketch, "E2560", {"start": v(-246.62, 161.33) * mm, "end": v(-246.87, 161.87) * mm});
            skLineSegment(sketch, "E2561", {"start": v(-246.87, 161.87) * mm, "end": v(-247.08, 162.43) * mm});
            skLineSegment(sketch, "E2562", {"start": v(-247.08, 162.43) * mm, "end": v(-247.28, 163) * mm});
            skLineSegment(sketch, "E2563", {"start": v(-247.28, 163) * mm, "end": v(-247.44, 163.58) * mm});
            skLineSegment(sketch, "E2564", {"start": v(-247.44, 163.58) * mm, "end": v(-247.58, 164.17) * mm});
            skLineSegment(sketch, "E2565", {"start": v(-247.58, 164.17) * mm, "end": v(-247.68, 164.77) * mm});
            skLineSegment(sketch, "E2566", {"start": v(-247.68, 164.77) * mm, "end": v(-247.76, 165.38) * mm});
            skLineSegment(sketch, "E2567", {"start": v(-247.76, 165.38) * mm, "end": v(-247.8, 166) * mm});
            skLineSegment(sketch, "E2568", {"start": v(-247.8, 166) * mm, "end": v(-247.83, 166.63) * mm});
            skLineSegment(sketch, "E2569", {"start": v(-247.83, 166.63) * mm, "end": v(-247.8, 167.26) * mm});
            skLineSegment(sketch, "E2570", {"start": v(-247.8, 167.26) * mm, "end": v(-247.76, 167.88) * mm});
            skLineSegment(sketch, "E2571", {"start": v(-247.76, 167.88) * mm, "end": v(-247.68, 168.49) * mm});
            skLineSegment(sketch, "E2572", {"start": v(-247.68, 168.49) * mm, "end": v(-247.58, 169.09) * mm});
            skLineSegment(sketch, "E2573", {"start": v(-247.58, 169.09) * mm, "end": v(-247.44, 169.68) * mm});
            skLineSegment(sketch, "E2574", {"start": v(-247.44, 169.68) * mm, "end": v(-247.28, 170.26) * mm});
            skLineSegment(sketch, "E2575", {"start": v(-247.28, 170.26) * mm, "end": v(-247.08, 170.83) * mm});
            skLineSegment(sketch, "E2576", {"start": v(-247.08, 170.83) * mm, "end": v(-246.87, 171.38) * mm});
            skLineSegment(sketch, "E2577", {"start": v(-246.87, 171.38) * mm, "end": v(-246.62, 171.92) * mm});
            skLineSegment(sketch, "E2578", {"start": v(-246.62, 171.92) * mm, "end": v(-246.35, 172.45) * mm});
            skLineSegment(sketch, "E2579", {"start": v(-246.35, 172.45) * mm, "end": v(-246.06, 172.96) * mm});
            skLineSegment(sketch, "E2580", {"start": v(-246.06, 172.96) * mm, "end": v(-245.74, 173.46) * mm});
            skLineSegment(sketch, "E2581", {"start": v(-245.74, 173.46) * mm, "end": v(-245.4, 173.93) * mm});
            skLineSegment(sketch, "E2582", {"start": v(-245.4, 173.93) * mm, "end": v(-245.04, 174.4) * mm});
            skLineSegment(sketch, "E2583", {"start": v(-245.04, 174.4) * mm, "end": v(-244.65, 174.84) * mm});
            skLineSegment(sketch, "E2584", {"start": v(-244.65, 174.84) * mm, "end": v(-244.25, 175.26) * mm});
            skLineSegment(sketch, "E2585", {"start": v(-244.25, 175.26) * mm, "end": v(-243.82, 175.67) * mm});
            skLineSegment(sketch, "E2586", {"start": v(-243.82, 175.67) * mm, "end": v(-243.38, 176.05) * mm});
            skLineSegment(sketch, "E2587", {"start": v(-243.38, 176.05) * mm, "end": v(-242.92, 176.41) * mm});
            skLineSegment(sketch, "E2588", {"start": v(-242.92, 176.41) * mm, "end": v(-242.44, 176.75) * mm});
            skLineSegment(sketch, "E2589", {"start": v(-242.44, 176.75) * mm, "end": v(-241.95, 177.07) * mm});
            skLineSegment(sketch, "E2590", {"start": v(-241.95, 177.07) * mm, "end": v(-241.43, 177.37) * mm});
            skLineSegment(sketch, "E2591", {"start": v(-241.43, 177.37) * mm, "end": v(-240.9, 177.64) * mm});
            skLineSegment(sketch, "E2592", {"start": v(-240.9, 177.64) * mm, "end": v(-240.37, 177.88) * mm});
            skLineSegment(sketch, "E2593", {"start": v(-240.37, 177.88) * mm, "end": v(-239.81, 178.1) * mm});
            skLineSegment(sketch, "E2594", {"start": v(-239.81, 178.1) * mm, "end": v(-239.25, 178.3) * mm});
            skLineSegment(sketch, "E2595", {"start": v(-239.25, 178.3) * mm, "end": v(-238.67, 178.45) * mm});
            skLineSegment(sketch, "E2596", {"start": v(-238.67, 178.45) * mm, "end": v(-238.08, 178.6) * mm});
            skLineSegment(sketch, "E2597", {"start": v(-238.08, 178.6) * mm, "end": v(-237.47, 178.7) * mm});
            skLineSegment(sketch, "E2598", {"start": v(-237.47, 178.7) * mm, "end": v(-236.86, 178.78) * mm});
            skLineSegment(sketch, "E2599", {"start": v(-236.86, 178.78) * mm, "end": v(-236.24, 178.82) * mm});
            skLineSegment(sketch, "E2600", {"start": v(-236.24, 178.82) * mm, "end": v(-235.61, 178.84) * mm});
            skLineSegment(sketch, "E2601", {"start": v(-235.61, 178.84) * mm, "end": v(-234.99, 178.82) * mm});
            skLineSegment(sketch, "E2602", {"start": v(-234.99, 178.82) * mm, "end": v(-234.37, 178.78) * mm});
            skLineSegment(sketch, "E2603", {"start": v(-234.37, 178.78) * mm, "end": v(-233.75, 178.7) * mm});
            skLineSegment(sketch, "E2604", {"start": v(-233.75, 178.7) * mm, "end": v(-233.15, 178.6) * mm});
            skLineSegment(sketch, "E2605", {"start": v(-233.15, 178.6) * mm, "end": v(-232.56, 178.45) * mm});
            skLineSegment(sketch, "E2606", {"start": v(-232.56, 178.45) * mm, "end": v(-231.98, 178.3) * mm});
            skLineSegment(sketch, "E2607", {"start": v(-231.98, 178.3) * mm, "end": v(-231.41, 178.1) * mm});
            skLineSegment(sketch, "E2608", {"start": v(-231.41, 178.1) * mm, "end": v(-230.86, 177.88) * mm});
            skLineSegment(sketch, "E2609", {"start": v(-230.86, 177.88) * mm, "end": v(-230.32, 177.64) * mm});
            skLineSegment(sketch, "E2610", {"start": v(-230.32, 177.64) * mm, "end": v(-229.8, 177.37) * mm});
            skLineSegment(sketch, "E2611", {"start": v(-229.8, 177.37) * mm, "end": v(-229.28, 177.07) * mm});
            skLineSegment(sketch, "E2612", {"start": v(-229.28, 177.07) * mm, "end": v(-228.79, 176.75) * mm});
            skLineSegment(sketch, "E2613", {"start": v(-228.79, 176.75) * mm, "end": v(-228.3, 176.41) * mm});
            skLineSegment(sketch, "E2614", {"start": v(-228.3, 176.41) * mm, "end": v(-227.85, 176.05) * mm});
            skLineSegment(sketch, "E2615", {"start": v(-227.85, 176.05) * mm, "end": v(-227.4, 175.67) * mm});
            skLineSegment(sketch, "E2616", {"start": v(-227.4, 175.67) * mm, "end": v(-226.98, 175.26) * mm});
            skLineSegment(sketch, "E2617", {"start": v(-226.98, 175.26) * mm, "end": v(-226.57, 174.84) * mm});
            skLineSegment(sketch, "E2618", {"start": v(-226.57, 174.84) * mm, "end": v(-226.19, 174.4) * mm});
            skLineSegment(sketch, "E2619", {"start": v(-226.19, 174.4) * mm, "end": v(-225.83, 173.93) * mm});
            skLineSegment(sketch, "E2620", {"start": v(-225.83, 173.93) * mm, "end": v(-225.49, 173.46) * mm});
            skLineSegment(sketch, "E2621", {"start": v(-225.49, 173.46) * mm, "end": v(-225.17, 172.96) * mm});
            skLineSegment(sketch, "E2622", {"start": v(-225.17, 172.96) * mm, "end": v(-224.87, 172.45) * mm});
            skLineSegment(sketch, "E2623", {"start": v(-224.87, 172.45) * mm, "end": v(-224.6, 171.92) * mm});
            skLineSegment(sketch, "E2624", {"start": v(-224.6, 171.92) * mm, "end": v(-224.36, 171.38) * mm});
            skLineSegment(sketch, "E2625", {"start": v(-224.36, 171.38) * mm, "end": v(-224.14, 170.83) * mm});
            skLineSegment(sketch, "E2626", {"start": v(-224.14, 170.83) * mm, "end": v(-223.95, 170.26) * mm});
            skLineSegment(sketch, "E2627", {"start": v(-223.95, 170.26) * mm, "end": v(-223.79, 169.68) * mm});
            skLineSegment(sketch, "E2628", {"start": v(-223.79, 169.68) * mm, "end": v(-223.65, 169.09) * mm});
            skLineSegment(sketch, "E2629", {"start": v(-223.65, 169.09) * mm, "end": v(-223.54, 168.49) * mm});
            skLineSegment(sketch, "E2630", {"start": v(-223.54, 168.49) * mm, "end": v(-223.46, 167.88) * mm});
            skLineSegment(sketch, "E2631", {"start": v(-223.46, 167.88) * mm, "end": v(-223.42, 167.26) * mm});
            skLineSegment(sketch, "E2632", {"start": v(-223.42, 167.26) * mm, "end": v(-223.4, 166.63) * mm});
            skLineSegment(sketch, "E2633", {"start": v(-223.4, 166.63) * mm, "end": v(-223.42, 166) * mm});
            skLineSegment(sketch, "E2634", {"start": v(-223.42, 166) * mm, "end": v(-223.46, 165.38) * mm});
            skLineSegment(sketch, "E2635", {"start": v(-223.46, 165.38) * mm, "end": v(-223.54, 164.77) * mm});
            skLineSegment(sketch, "E2636", {"start": v(-223.54, 164.77) * mm, "end": v(-223.65, 164.17) * mm});
            skLineSegment(sketch, "E2637", {"start": v(-223.65, 164.17) * mm, "end": v(-223.79, 163.58) * mm});
            skLineSegment(sketch, "E2638", {"start": v(-223.79, 163.58) * mm, "end": v(-223.95, 163) * mm});
            skLineSegment(sketch, "E2639", {"start": v(-223.95, 163) * mm, "end": v(-224.14, 162.43) * mm});
            skLineSegment(sketch, "E2640", {"start": v(-224.14, 162.43) * mm, "end": v(-224.36, 161.87) * mm});
            skLineSegment(sketch, "E2641", {"start": v(-224.36, 161.87) * mm, "end": v(-224.6, 161.33) * mm});
            skLineSegment(sketch, "E2642", {"start": v(-224.6, 161.33) * mm, "end": v(-224.87, 160.8) * mm});
            skLineSegment(sketch, "E2643", {"start": v(-224.87, 160.8) * mm, "end": v(-225.17, 160.3) * mm});
            skLineSegment(sketch, "E2644", {"start": v(-225.17, 160.3) * mm, "end": v(-225.49, 159.8) * mm});
            skLineSegment(sketch, "E2645", {"start": v(-225.49, 159.8) * mm, "end": v(-225.83, 159.32) * mm});
            skLineSegment(sketch, "E2646", {"start": v(-225.83, 159.32) * mm, "end": v(-226.19, 158.86) * mm});
            skLineSegment(sketch, "E2647", {"start": v(-226.19, 158.86) * mm, "end": v(-226.57, 158.42) * mm});
            skLineSegment(sketch, "E2648", {"start": v(-226.57, 158.42) * mm, "end": v(-226.98, 158) * mm});
            skLineSegment(sketch, "E2649", {"start": v(-226.98, 158) * mm, "end": v(-227.4, 157.59) * mm});
            skLineSegment(sketch, "E2650", {"start": v(-227.4, 157.59) * mm, "end": v(-227.85, 157.2) * mm});
            skLineSegment(sketch, "E2651", {"start": v(-227.85, 157.2) * mm, "end": v(-228.3, 156.84) * mm});
            skLineSegment(sketch, "E2652", {"start": v(-228.3, 156.84) * mm, "end": v(-228.79, 156.5) * mm});
            skLineSegment(sketch, "E2653", {"start": v(-228.79, 156.5) * mm, "end": v(-229.28, 156.18) * mm});
            skLineSegment(sketch, "E2654", {"start": v(-229.28, 156.18) * mm, "end": v(-229.8, 155.89) * mm});
            skLineSegment(sketch, "E2655", {"start": v(-229.8, 155.89) * mm, "end": v(-230.32, 155.62) * mm});
            skLineSegment(sketch, "E2656", {"start": v(-230.32, 155.62) * mm, "end": v(-230.86, 155.38) * mm});
            skLineSegment(sketch, "E2657", {"start": v(-230.86, 155.38) * mm, "end": v(-231.41, 155.16) * mm});
            skLineSegment(sketch, "E2658", {"start": v(-231.41, 155.16) * mm, "end": v(-231.98, 154.96) * mm});
            skLineSegment(sketch, "E2659", {"start": v(-231.98, 154.96) * mm, "end": v(-232.56, 154.8) * mm});
            skLineSegment(sketch, "E2660", {"start": v(-232.56, 154.8) * mm, "end": v(-233.15, 154.66) * mm});
            skLineSegment(sketch, "E2661", {"start": v(-233.15, 154.66) * mm, "end": v(-233.75, 154.56) * mm});
            skLineSegment(sketch, "E2662", {"start": v(-233.75, 154.56) * mm, "end": v(-234.37, 154.48) * mm});
            skLineSegment(sketch, "E2663", {"start": v(-234.37, 154.48) * mm, "end": v(-234.99, 154.43) * mm});
            skLineSegment(sketch, "E2664", {"start": v(-234.99, 154.43) * mm, "end": v(-235.61, 154.42) * mm});
            skLineSegment(sketch, "E2665", {"start": v(-235.61, 196.2) * mm, "end": v(-236.38, 196.19) * mm});
            skLineSegment(sketch, "E2666", {"start": v(-236.38, 196.19) * mm, "end": v(-237.13, 196.16) * mm});
            skLineSegment(sketch, "E2667", {"start": v(-237.13, 196.16) * mm, "end": v(-237.89, 196.11) * mm});
            skLineSegment(sketch, "E2668", {"start": v(-237.89, 196.11) * mm, "end": v(-238.63, 196.05) * mm});
            skLineSegment(sketch, "E2669", {"start": v(-238.63, 196.05) * mm, "end": v(-239.38, 195.96) * mm});
            skLineSegment(sketch, "E2670", {"start": v(-239.38, 195.96) * mm, "end": v(-240.11, 195.86) * mm});
            skLineSegment(sketch, "E2671", {"start": v(-240.11, 195.86) * mm, "end": v(-240.84, 195.74) * mm});
            skLineSegment(sketch, "E2672", {"start": v(-240.84, 195.74) * mm, "end": v(-241.57, 195.6) * mm});
            skLineSegment(sketch, "E2673", {"start": v(-241.57, 195.6) * mm, "end": v(-242.28, 195.44) * mm});
            skLineSegment(sketch, "E2674", {"start": v(-242.28, 195.44) * mm, "end": v(-243, 195.27) * mm});
            skLineSegment(sketch, "E2675", {"start": v(-243, 195.27) * mm, "end": v(-243.7, 195.08) * mm});
            skLineSegment(sketch, "E2676", {"start": v(-243.7, 195.08) * mm, "end": v(-244.4, 194.87) * mm});
            skLineSegment(sketch, "E2677", {"start": v(-244.4, 194.87) * mm, "end": v(-245.09, 194.64) * mm});
            skLineSegment(sketch, "E2678", {"start": v(-245.09, 194.64) * mm, "end": v(-245.77, 194.4) * mm});
            skLineSegment(sketch, "E2679", {"start": v(-245.77, 194.4) * mm, "end": v(-246.45, 194.14) * mm});
            skLineSegment(sketch, "E2680", {"start": v(-246.45, 194.14) * mm, "end": v(-247.11, 193.87) * mm});
            skLineSegment(sketch, "E2681", {"start": v(-247.11, 193.87) * mm, "end": v(-247.77, 193.58) * mm});
            skLineSegment(sketch, "E2682", {"start": v(-247.77, 193.58) * mm, "end": v(-248.42, 193.28) * mm});
            skLineSegment(sketch, "E2683", {"start": v(-248.42, 193.28) * mm, "end": v(-249.06, 192.96) * mm});
            skLineSegment(sketch, "E2684", {"start": v(-249.06, 192.96) * mm, "end": v(-249.7, 192.63) * mm});
            skLineSegment(sketch, "E2685", {"start": v(-249.7, 192.63) * mm, "end": v(-250.32, 192.28) * mm});
            skLineSegment(sketch, "E2686", {"start": v(-250.32, 192.28) * mm, "end": v(-250.94, 191.91) * mm});
            skLineSegment(sketch, "E2687", {"start": v(-250.94, 191.91) * mm, "end": v(-251.54, 191.53) * mm});
            skLineSegment(sketch, "E2688", {"start": v(-251.54, 191.53) * mm, "end": v(-252.14, 191.14) * mm});
            skLineSegment(sketch, "E2689", {"start": v(-252.14, 191.14) * mm, "end": v(-252.72, 190.74) * mm});
            skLineSegment(sketch, "E2690", {"start": v(-252.72, 190.74) * mm, "end": v(-253.3, 190.32) * mm});
            skLineSegment(sketch, "E2691", {"start": v(-253.3, 190.32) * mm, "end": v(-253.86, 189.88) * mm});
            skLineSegment(sketch, "E2692", {"start": v(-253.86, 189.88) * mm, "end": v(-254.41, 189.44) * mm});
            skLineSegment(sketch, "E2693", {"start": v(-254.41, 189.44) * mm, "end": v(-254.96, 188.98) * mm});
            skLineSegment(sketch, "E2694", {"start": v(-254.96, 188.98) * mm, "end": v(-255.49, 188.5) * mm});
            skLineSegment(sketch, "E2695", {"start": v(-255.49, 188.5) * mm, "end": v(-256, 188.02) * mm});
            skLineSegment(sketch, "E2696", {"start": v(-256, 188.02) * mm, "end": v(-256.51, 187.53) * mm});
            skLineSegment(sketch, "E2697", {"start": v(-256.51, 187.53) * mm, "end": v(-257.01, 187.02) * mm});
            skLineSegment(sketch, "E2698", {"start": v(-257.01, 187.02) * mm, "end": v(-257.5, 186.5) * mm});
            skLineSegment(sketch, "E2699", {"start": v(-257.5, 186.5) * mm, "end": v(-257.97, 185.97) * mm});
            skLineSegment(sketch, "E2700", {"start": v(-257.97, 185.97) * mm, "end": v(-258.42, 185.43) * mm});
            skLineSegment(sketch, "E2701", {"start": v(-258.42, 185.43) * mm, "end": v(-258.87, 184.87) * mm});
            skLineSegment(sketch, "E2702", {"start": v(-258.87, 184.87) * mm, "end": v(-259.3, 184.3) * mm});
            skLineSegment(sketch, "E2703", {"start": v(-259.3, 184.3) * mm, "end": v(-259.72, 183.74) * mm});
            skLineSegment(sketch, "E2704", {"start": v(-259.72, 183.74) * mm, "end": v(-260.13, 183.15) * mm});
            skLineSegment(sketch, "E2705", {"start": v(-260.13, 183.15) * mm, "end": v(-260.52, 182.56) * mm});
            skLineSegment(sketch, "E2706", {"start": v(-260.52, 182.56) * mm, "end": v(-260.9, 181.95) * mm});
            skLineSegment(sketch, "E2707", {"start": v(-260.9, 181.95) * mm, "end": v(-261.26, 181.34) * mm});
            skLineSegment(sketch, "E2708", {"start": v(-261.26, 181.34) * mm, "end": v(-261.61, 180.71) * mm});
            skLineSegment(sketch, "E2709", {"start": v(-261.61, 180.71) * mm, "end": v(-261.95, 180.08) * mm});
            skLineSegment(sketch, "E2710", {"start": v(-261.95, 180.08) * mm, "end": v(-262.26, 179.44) * mm});
            skLineSegment(sketch, "E2711", {"start": v(-262.26, 179.44) * mm, "end": v(-262.57, 178.79) * mm});
            skLineSegment(sketch, "E2712", {"start": v(-262.57, 178.79) * mm, "end": v(-262.86, 178.13) * mm});
            skLineSegment(sketch, "E2713", {"start": v(-262.86, 178.13) * mm, "end": v(-263.13, 177.46) * mm});
            skLineSegment(sketch, "E2714", {"start": v(-263.13, 177.46) * mm, "end": v(-263.39, 176.79) * mm});
            skLineSegment(sketch, "E2715", {"start": v(-263.39, 176.79) * mm, "end": v(-263.63, 176.1) * mm});
            skLineSegment(sketch, "E2716", {"start": v(-263.63, 176.1) * mm, "end": v(-263.85, 175.41) * mm});
            skLineSegment(sketch, "E2717", {"start": v(-263.85, 175.41) * mm, "end": v(-264.06, 174.71) * mm});
            skLineSegment(sketch, "E2718", {"start": v(-264.06, 174.71) * mm, "end": v(-264.25, 174) * mm});
            skLineSegment(sketch, "E2719", {"start": v(-264.25, 174) * mm, "end": v(-264.43, 173.3) * mm});
            skLineSegment(sketch, "E2720", {"start": v(-264.43, 173.3) * mm, "end": v(-264.58, 172.58) * mm});
            skLineSegment(sketch, "E2721", {"start": v(-264.58, 172.58) * mm, "end": v(-264.72, 171.86) * mm});
            skLineSegment(sketch, "E2722", {"start": v(-264.72, 171.86) * mm, "end": v(-264.84, 171.13) * mm});
            skLineSegment(sketch, "E2723", {"start": v(-264.84, 171.13) * mm, "end": v(-264.95, 170.39) * mm});
            skLineSegment(sketch, "E2724", {"start": v(-264.95, 170.39) * mm, "end": v(-265.03, 169.65) * mm});
            skLineSegment(sketch, "E2725", {"start": v(-265.03, 169.65) * mm, "end": v(-265.1, 168.9) * mm});
            skLineSegment(sketch, "E2726", {"start": v(-265.1, 168.9) * mm, "end": v(-265.15, 168.15) * mm});
            skLineSegment(sketch, "E2727", {"start": v(-265.15, 168.15) * mm, "end": v(-265.18, 167.4) * mm});
            skLineSegment(sketch, "E2728", {"start": v(-265.18, 167.4) * mm, "end": v(-265.19, 166.63) * mm});
            skLineSegment(sketch, "E2729", {"start": v(-265.19, 166.63) * mm, "end": v(-265.18, 165.87) * mm});
            skLineSegment(sketch, "E2730", {"start": v(-265.18, 165.87) * mm, "end": v(-265.15, 165.1) * mm});
            skLineSegment(sketch, "E2731", {"start": v(-265.15, 165.1) * mm, "end": v(-265.1, 164.36) * mm});
            skLineSegment(sketch, "E2732", {"start": v(-265.1, 164.36) * mm, "end": v(-265.03, 163.6) * mm});
            skLineSegment(sketch, "E2733", {"start": v(-265.03, 163.6) * mm, "end": v(-264.95, 162.87) * mm});
            skLineSegment(sketch, "E2734", {"start": v(-264.95, 162.87) * mm, "end": v(-264.84, 162.13) * mm});
            skLineSegment(sketch, "E2735", {"start": v(-264.84, 162.13) * mm, "end": v(-264.72, 161.4) * mm});
            skLineSegment(sketch, "E2736", {"start": v(-264.72, 161.4) * mm, "end": v(-264.58, 160.68) * mm});
            skLineSegment(sketch, "E2737", {"start": v(-264.58, 160.68) * mm, "end": v(-264.43, 159.96) * mm});
            skLineSegment(sketch, "E2738", {"start": v(-264.43, 159.96) * mm, "end": v(-264.25, 159.25) * mm});
            skLineSegment(sketch, "E2739", {"start": v(-264.25, 159.25) * mm, "end": v(-264.06, 158.54) * mm});
            skLineSegment(sketch, "E2740", {"start": v(-264.06, 158.54) * mm, "end": v(-263.85, 157.84) * mm});
            skLineSegment(sketch, "E2741", {"start": v(-263.85, 157.84) * mm, "end": v(-263.63, 157.15) * mm});
            skLineSegment(sketch, "E2742", {"start": v(-263.63, 157.15) * mm, "end": v(-263.39, 156.47) * mm});
            skLineSegment(sketch, "E2743", {"start": v(-263.39, 156.47) * mm, "end": v(-263.13, 155.8) * mm});
            skLineSegment(sketch, "E2744", {"start": v(-263.13, 155.8) * mm, "end": v(-262.86, 155.13) * mm});
            skLineSegment(sketch, "E2745", {"start": v(-262.86, 155.13) * mm, "end": v(-262.57, 154.47) * mm});
            skLineSegment(sketch, "E2746", {"start": v(-262.57, 154.47) * mm, "end": v(-262.26, 153.82) * mm});
            skLineSegment(sketch, "E2747", {"start": v(-262.26, 153.82) * mm, "end": v(-261.95, 153.18) * mm});
            skLineSegment(sketch, "E2748", {"start": v(-261.95, 153.18) * mm, "end": v(-261.61, 152.54) * mm});
            skLineSegment(sketch, "E2749", {"start": v(-261.61, 152.54) * mm, "end": v(-261.26, 151.92) * mm});
            skLineSegment(sketch, "E2750", {"start": v(-261.26, 151.92) * mm, "end": v(-260.9, 151.3) * mm});
            skLineSegment(sketch, "E2751", {"start": v(-260.9, 151.3) * mm, "end": v(-260.52, 150.7) * mm});
            skLineSegment(sketch, "E2752", {"start": v(-260.52, 150.7) * mm, "end": v(-260.13, 150.1) * mm});
            skLineSegment(sketch, "E2753", {"start": v(-260.13, 150.1) * mm, "end": v(-259.72, 149.52) * mm});
            skLineSegment(sketch, "E2754", {"start": v(-259.72, 149.52) * mm, "end": v(-259.3, 148.95) * mm});
            skLineSegment(sketch, "E2755", {"start": v(-259.3, 148.95) * mm, "end": v(-258.87, 148.38) * mm});
            skLineSegment(sketch, "E2756", {"start": v(-258.87, 148.38) * mm, "end": v(-258.42, 147.83) * mm});
            skLineSegment(sketch, "E2757", {"start": v(-258.42, 147.83) * mm, "end": v(-257.97, 147.29) * mm});
            skLineSegment(sketch, "E2758", {"start": v(-257.97, 147.29) * mm, "end": v(-257.5, 146.76) * mm});
            skLineSegment(sketch, "E2759", {"start": v(-257.5, 146.76) * mm, "end": v(-257.01, 146.24) * mm});
            skLineSegment(sketch, "E2760", {"start": v(-257.01, 146.24) * mm, "end": v(-256.51, 145.73) * mm});
            skLineSegment(sketch, "E2761", {"start": v(-256.51, 145.73) * mm, "end": v(-256, 145.23) * mm});
            skLineSegment(sketch, "E2762", {"start": v(-256, 145.23) * mm, "end": v(-255.49, 144.75) * mm});
            skLineSegment(sketch, "E2763", {"start": v(-255.49, 144.75) * mm, "end": v(-254.96, 144.28) * mm});
            skLineSegment(sketch, "E2764", {"start": v(-254.96, 144.28) * mm, "end": v(-254.41, 143.82) * mm});
            skLineSegment(sketch, "E2765", {"start": v(-254.41, 143.82) * mm, "end": v(-253.86, 143.37) * mm});
            skLineSegment(sketch, "E2766", {"start": v(-253.86, 143.37) * mm, "end": v(-253.3, 142.94) * mm});
            skLineSegment(sketch, "E2767", {"start": v(-253.3, 142.94) * mm, "end": v(-252.72, 142.52) * mm});
            skLineSegment(sketch, "E2768", {"start": v(-252.72, 142.52) * mm, "end": v(-252.14, 142.11) * mm});
            skLineSegment(sketch, "E2769", {"start": v(-252.14, 142.11) * mm, "end": v(-251.54, 141.72) * mm});
            skLineSegment(sketch, "E2770", {"start": v(-251.54, 141.72) * mm, "end": v(-250.94, 141.34) * mm});
            skLineSegment(sketch, "E2771", {"start": v(-250.94, 141.34) * mm, "end": v(-250.32, 140.98) * mm});
            skLineSegment(sketch, "E2772", {"start": v(-250.32, 140.98) * mm, "end": v(-249.7, 140.63) * mm});
            skLineSegment(sketch, "E2773", {"start": v(-249.7, 140.63) * mm, "end": v(-249.06, 140.3) * mm});
            skLineSegment(sketch, "E2774", {"start": v(-249.06, 140.3) * mm, "end": v(-248.42, 139.98) * mm});
            skLineSegment(sketch, "E2775", {"start": v(-248.42, 139.98) * mm, "end": v(-247.77, 139.67) * mm});
            skLineSegment(sketch, "E2776", {"start": v(-247.77, 139.67) * mm, "end": v(-247.11, 139.38) * mm});
            skLineSegment(sketch, "E2777", {"start": v(-247.11, 139.38) * mm, "end": v(-246.45, 139.11) * mm});
            skLineSegment(sketch, "E2778", {"start": v(-246.45, 139.11) * mm, "end": v(-245.77, 138.85) * mm});
            skLineSegment(sketch, "E2779", {"start": v(-245.77, 138.85) * mm, "end": v(-245.09, 138.61) * mm});
            skLineSegment(sketch, "E2780", {"start": v(-245.09, 138.61) * mm, "end": v(-244.4, 138.39) * mm});
            skLineSegment(sketch, "E2781", {"start": v(-244.4, 138.39) * mm, "end": v(-243.7, 138.18) * mm});
            skLineSegment(sketch, "E2782", {"start": v(-243.7, 138.18) * mm, "end": v(-243, 137.99) * mm});
            skLineSegment(sketch, "E2783", {"start": v(-243, 137.99) * mm, "end": v(-242.28, 137.82) * mm});
            skLineSegment(sketch, "E2784", {"start": v(-242.28, 137.82) * mm, "end": v(-241.57, 137.66) * mm});
            skLineSegment(sketch, "E2785", {"start": v(-241.57, 137.66) * mm, "end": v(-240.84, 137.52) * mm});
            skLineSegment(sketch, "E2786", {"start": v(-240.84, 137.52) * mm, "end": v(-240.11, 137.4) * mm});
            skLineSegment(sketch, "E2787", {"start": v(-240.11, 137.4) * mm, "end": v(-239.38, 137.3) * mm});
            skLineSegment(sketch, "E2788", {"start": v(-239.38, 137.3) * mm, "end": v(-238.63, 137.2) * mm});
            skLineSegment(sketch, "E2789", {"start": v(-238.63, 137.2) * mm, "end": v(-237.89, 137.14) * mm});
            skLineSegment(sketch, "E2790", {"start": v(-237.89, 137.14) * mm, "end": v(-237.13, 137.1) * mm});
            skLineSegment(sketch, "E2791", {"start": v(-237.13, 137.1) * mm, "end": v(-236.38, 137.07) * mm});
            skLineSegment(sketch, "E2792", {"start": v(-236.38, 137.07) * mm, "end": v(-235.61, 137.06) * mm});
            skLineSegment(sketch, "E2793", {"start": v(-235.61, 137.06) * mm, "end": v(-234.85, 137.07) * mm});
            skLineSegment(sketch, "E2794", {"start": v(-234.85, 137.07) * mm, "end": v(-234.1, 137.1) * mm});
            skLineSegment(sketch, "E2795", {"start": v(-234.1, 137.1) * mm, "end": v(-233.34, 137.14) * mm});
            skLineSegment(sketch, "E2796", {"start": v(-233.34, 137.14) * mm, "end": v(-232.6, 137.2) * mm});
            skLineSegment(sketch, "E2797", {"start": v(-232.6, 137.2) * mm, "end": v(-231.85, 137.3) * mm});
            skLineSegment(sketch, "E2798", {"start": v(-231.85, 137.3) * mm, "end": v(-231.12, 137.4) * mm});
            skLineSegment(sketch, "E2799", {"start": v(-231.12, 137.4) * mm, "end": v(-230.39, 137.52) * mm});
            skLineSegment(sketch, "E2800", {"start": v(-230.39, 137.52) * mm, "end": v(-229.66, 137.66) * mm});
            skLineSegment(sketch, "E2801", {"start": v(-229.66, 137.66) * mm, "end": v(-228.94, 137.82) * mm});
            skLineSegment(sketch, "E2802", {"start": v(-228.94, 137.82) * mm, "end": v(-228.23, 137.99) * mm});
            skLineSegment(sketch, "E2803", {"start": v(-228.23, 137.99) * mm, "end": v(-227.53, 138.18) * mm});
            skLineSegment(sketch, "E2804", {"start": v(-227.53, 138.18) * mm, "end": v(-226.83, 138.39) * mm});
            skLineSegment(sketch, "E2805", {"start": v(-226.83, 138.39) * mm, "end": v(-226.14, 138.61) * mm});
            skLineSegment(sketch, "E2806", {"start": v(-226.14, 138.61) * mm, "end": v(-225.46, 138.85) * mm});
            skLineSegment(sketch, "E2807", {"start": v(-225.46, 138.85) * mm, "end": v(-224.78, 139.11) * mm});
            skLineSegment(sketch, "E2808", {"start": v(-224.78, 139.11) * mm, "end": v(-224.11, 139.38) * mm});
            skLineSegment(sketch, "E2809", {"start": v(-224.11, 139.38) * mm, "end": v(-223.46, 139.67) * mm});
            skLineSegment(sketch, "E2810", {"start": v(-223.46, 139.67) * mm, "end": v(-222.8, 139.98) * mm});
            skLineSegment(sketch, "E2811", {"start": v(-222.8, 139.98) * mm, "end": v(-222.16, 140.3) * mm});
            skLineSegment(sketch, "E2812", {"start": v(-222.16, 140.3) * mm, "end": v(-221.53, 140.63) * mm});
            skLineSegment(sketch, "E2813", {"start": v(-221.53, 140.63) * mm, "end": v(-220.9, 140.98) * mm});
            skLineSegment(sketch, "E2814", {"start": v(-220.9, 140.98) * mm, "end": v(-220.3, 141.34) * mm});
            skLineSegment(sketch, "E2815", {"start": v(-220.3, 141.34) * mm, "end": v(-219.69, 141.72) * mm});
            skLineSegment(sketch, "E2816", {"start": v(-219.69, 141.72) * mm, "end": v(-219.1, 142.11) * mm});
            skLineSegment(sketch, "E2817", {"start": v(-219.1, 142.11) * mm, "end": v(-218.5, 142.52) * mm});
            skLineSegment(sketch, "E2818", {"start": v(-218.5, 142.52) * mm, "end": v(-217.93, 142.94) * mm});
            skLineSegment(sketch, "E2819", {"start": v(-217.93, 142.94) * mm, "end": v(-217.37, 143.37) * mm});
            skLineSegment(sketch, "E2820", {"start": v(-217.37, 143.37) * mm, "end": v(-216.82, 143.82) * mm});
            skLineSegment(sketch, "E2821", {"start": v(-216.82, 143.82) * mm, "end": v(-216.27, 144.28) * mm});
            skLineSegment(sketch, "E2822", {"start": v(-216.27, 144.28) * mm, "end": v(-215.74, 144.75) * mm});
            skLineSegment(sketch, "E2823", {"start": v(-215.74, 144.75) * mm, "end": v(-215.22, 145.23) * mm});
            skLineSegment(sketch, "E2824", {"start": v(-215.22, 145.23) * mm, "end": v(-214.71, 145.73) * mm});
            skLineSegment(sketch, "E2825", {"start": v(-214.71, 145.73) * mm, "end": v(-214.22, 146.24) * mm});
            skLineSegment(sketch, "E2826", {"start": v(-214.22, 146.24) * mm, "end": v(-213.73, 146.76) * mm});
            skLineSegment(sketch, "E2827", {"start": v(-213.73, 146.76) * mm, "end": v(-213.26, 147.29) * mm});
            skLineSegment(sketch, "E2828", {"start": v(-213.26, 147.29) * mm, "end": v(-212.8, 147.83) * mm});
            skLineSegment(sketch, "E2829", {"start": v(-212.8, 147.83) * mm, "end": v(-212.36, 148.38) * mm});
            skLineSegment(sketch, "E2830", {"start": v(-212.36, 148.38) * mm, "end": v(-211.93, 148.95) * mm});
            skLineSegment(sketch, "E2831", {"start": v(-211.93, 148.95) * mm, "end": v(-211.5, 149.52) * mm});
            skLineSegment(sketch, "E2832", {"start": v(-211.5, 149.52) * mm, "end": v(-211.1, 150.1) * mm});
            skLineSegment(sketch, "E2833", {"start": v(-211.1, 150.1) * mm, "end": v(-210.7, 150.7) * mm});
            skLineSegment(sketch, "E2834", {"start": v(-210.7, 150.7) * mm, "end": v(-210.33, 151.3) * mm});
            skLineSegment(sketch, "E2835", {"start": v(-210.33, 151.3) * mm, "end": v(-209.97, 151.92) * mm});
            skLineSegment(sketch, "E2836", {"start": v(-209.97, 151.92) * mm, "end": v(-209.62, 152.54) * mm});
            skLineSegment(sketch, "E2837", {"start": v(-209.62, 152.54) * mm, "end": v(-209.28, 153.18) * mm});
            skLineSegment(sketch, "E2838", {"start": v(-209.28, 153.18) * mm, "end": v(-208.96, 153.82) * mm});
            skLineSegment(sketch, "E2839", {"start": v(-208.96, 153.82) * mm, "end": v(-208.66, 154.47) * mm});
            skLineSegment(sketch, "E2840", {"start": v(-208.66, 154.47) * mm, "end": v(-208.37, 155.13) * mm});
            skLineSegment(sketch, "E2841", {"start": v(-208.37, 155.13) * mm, "end": v(-208.1, 155.8) * mm});
            skLineSegment(sketch, "E2842", {"start": v(-208.1, 155.8) * mm, "end": v(-207.84, 156.47) * mm});
            skLineSegment(sketch, "E2843", {"start": v(-207.84, 156.47) * mm, "end": v(-207.6, 157.15) * mm});
            skLineSegment(sketch, "E2844", {"start": v(-207.6, 157.15) * mm, "end": v(-207.37, 157.84) * mm});
            skLineSegment(sketch, "E2845", {"start": v(-207.37, 157.84) * mm, "end": v(-207.17, 158.54) * mm});
            skLineSegment(sketch, "E2846", {"start": v(-207.17, 158.54) * mm, "end": v(-206.98, 159.25) * mm});
            skLineSegment(sketch, "E2847", {"start": v(-206.98, 159.25) * mm, "end": v(-206.8, 159.96) * mm});
            skLineSegment(sketch, "E2848", {"start": v(-206.8, 159.96) * mm, "end": v(-206.64, 160.68) * mm});
            skLineSegment(sketch, "E2849", {"start": v(-206.64, 160.68) * mm, "end": v(-206.5, 161.4) * mm});
            skLineSegment(sketch, "E2850", {"start": v(-206.5, 161.4) * mm, "end": v(-206.38, 162.13) * mm});
            skLineSegment(sketch, "E2851", {"start": v(-206.38, 162.13) * mm, "end": v(-206.28, 162.87) * mm});
            skLineSegment(sketch, "E2852", {"start": v(-206.28, 162.87) * mm, "end": v(-206.2, 163.6) * mm});
            skLineSegment(sketch, "E2853", {"start": v(-206.2, 163.6) * mm, "end": v(-206.13, 164.36) * mm});
            skLineSegment(sketch, "E2854", {"start": v(-206.13, 164.36) * mm, "end": v(-206.08, 165.1) * mm});
            skLineSegment(sketch, "E2855", {"start": v(-206.08, 165.1) * mm, "end": v(-206.05, 165.87) * mm});
            skLineSegment(sketch, "E2856", {"start": v(-206.05, 165.87) * mm, "end": v(-206.04, 166.63) * mm});
            skLineSegment(sketch, "E2857", {"start": v(-206.04, 166.63) * mm, "end": v(-206.05, 167.4) * mm});
            skLineSegment(sketch, "E2858", {"start": v(-206.05, 167.4) * mm, "end": v(-206.08, 168.15) * mm});
            skLineSegment(sketch, "E2859", {"start": v(-206.08, 168.15) * mm, "end": v(-206.13, 168.9) * mm});
            skLineSegment(sketch, "E2860", {"start": v(-206.13, 168.9) * mm, "end": v(-206.2, 169.65) * mm});
            skLineSegment(sketch, "E2861", {"start": v(-206.2, 169.65) * mm, "end": v(-206.28, 170.39) * mm});
            skLineSegment(sketch, "E2862", {"start": v(-206.28, 170.39) * mm, "end": v(-206.38, 171.13) * mm});
            skLineSegment(sketch, "E2863", {"start": v(-206.38, 171.13) * mm, "end": v(-206.5, 171.86) * mm});
            skLineSegment(sketch, "E2864", {"start": v(-206.5, 171.86) * mm, "end": v(-206.64, 172.58) * mm});
            skLineSegment(sketch, "E2865", {"start": v(-206.64, 172.58) * mm, "end": v(-206.8, 173.3) * mm});
            skLineSegment(sketch, "E2866", {"start": v(-206.8, 173.3) * mm, "end": v(-206.98, 174) * mm});
            skLineSegment(sketch, "E2867", {"start": v(-206.98, 174) * mm, "end": v(-207.17, 174.71) * mm});
            skLineSegment(sketch, "E2868", {"start": v(-207.17, 174.71) * mm, "end": v(-207.37, 175.41) * mm});
            skLineSegment(sketch, "E2869", {"start": v(-207.37, 175.41) * mm, "end": v(-207.6, 176.1) * mm});
            skLineSegment(sketch, "E2870", {"start": v(-207.6, 176.1) * mm, "end": v(-207.84, 176.79) * mm});
            skLineSegment(sketch, "E2871", {"start": v(-207.84, 176.79) * mm, "end": v(-208.1, 177.46) * mm});
            skLineSegment(sketch, "E2872", {"start": v(-208.1, 177.46) * mm, "end": v(-208.37, 178.13) * mm});
            skLineSegment(sketch, "E2873", {"start": v(-208.37, 178.13) * mm, "end": v(-208.66, 178.79) * mm});
            skLineSegment(sketch, "E2874", {"start": v(-208.66, 178.79) * mm, "end": v(-208.96, 179.44) * mm});
            skLineSegment(sketch, "E2875", {"start": v(-208.96, 179.44) * mm, "end": v(-209.28, 180.08) * mm});
            skLineSegment(sketch, "E2876", {"start": v(-209.28, 180.08) * mm, "end": v(-209.62, 180.71) * mm});
            skLineSegment(sketch, "E2877", {"start": v(-209.62, 180.71) * mm, "end": v(-209.97, 181.34) * mm});
            skLineSegment(sketch, "E2878", {"start": v(-209.97, 181.34) * mm, "end": v(-210.33, 181.95) * mm});
            skLineSegment(sketch, "E2879", {"start": v(-210.33, 181.95) * mm, "end": v(-210.7, 182.56) * mm});
            skLineSegment(sketch, "E2880", {"start": v(-210.7, 182.56) * mm, "end": v(-211.1, 183.15) * mm});
            skLineSegment(sketch, "E2881", {"start": v(-211.1, 183.15) * mm, "end": v(-211.5, 183.74) * mm});
            skLineSegment(sketch, "E2882", {"start": v(-211.5, 183.74) * mm, "end": v(-211.93, 184.3) * mm});
            skLineSegment(sketch, "E2883", {"start": v(-211.93, 184.3) * mm, "end": v(-212.36, 184.87) * mm});
            skLineSegment(sketch, "E2884", {"start": v(-212.36, 184.87) * mm, "end": v(-212.8, 185.43) * mm});
            skLineSegment(sketch, "E2885", {"start": v(-212.8, 185.43) * mm, "end": v(-213.26, 185.97) * mm});
            skLineSegment(sketch, "E2886", {"start": v(-213.26, 185.97) * mm, "end": v(-213.73, 186.5) * mm});
            skLineSegment(sketch, "E2887", {"start": v(-213.73, 186.5) * mm, "end": v(-214.22, 187.02) * mm});
            skLineSegment(sketch, "E2888", {"start": v(-214.22, 187.02) * mm, "end": v(-214.71, 187.53) * mm});
            skLineSegment(sketch, "E2889", {"start": v(-214.71, 187.53) * mm, "end": v(-215.22, 188.02) * mm});
            skLineSegment(sketch, "E2890", {"start": v(-215.22, 188.02) * mm, "end": v(-215.74, 188.5) * mm});
            skLineSegment(sketch, "E2891", {"start": v(-215.74, 188.5) * mm, "end": v(-216.27, 188.98) * mm});
            skLineSegment(sketch, "E2892", {"start": v(-216.27, 188.98) * mm, "end": v(-216.82, 189.44) * mm});
            skLineSegment(sketch, "E2893", {"start": v(-216.82, 189.44) * mm, "end": v(-217.37, 189.88) * mm});
            skLineSegment(sketch, "E2894", {"start": v(-217.37, 189.88) * mm, "end": v(-217.93, 190.32) * mm});
            skLineSegment(sketch, "E2895", {"start": v(-217.93, 190.32) * mm, "end": v(-218.5, 190.74) * mm});
            skLineSegment(sketch, "E2896", {"start": v(-218.5, 190.74) * mm, "end": v(-219.1, 191.14) * mm});
            skLineSegment(sketch, "E2897", {"start": v(-219.1, 191.14) * mm, "end": v(-219.69, 191.53) * mm});
            skLineSegment(sketch, "E2898", {"start": v(-219.69, 191.53) * mm, "end": v(-220.3, 191.91) * mm});
            skLineSegment(sketch, "E2899", {"start": v(-220.3, 191.91) * mm, "end": v(-220.9, 192.28) * mm});
            skLineSegment(sketch, "E2900", {"start": v(-220.9, 192.28) * mm, "end": v(-221.53, 192.63) * mm});
            skLineSegment(sketch, "E2901", {"start": v(-221.53, 192.63) * mm, "end": v(-222.16, 192.96) * mm});
            skLineSegment(sketch, "E2902", {"start": v(-222.16, 192.96) * mm, "end": v(-222.8, 193.28) * mm});
            skLineSegment(sketch, "E2903", {"start": v(-222.8, 193.28) * mm, "end": v(-223.46, 193.58) * mm});
            skLineSegment(sketch, "E2904", {"start": v(-223.46, 193.58) * mm, "end": v(-224.11, 193.87) * mm});
            skLineSegment(sketch, "E2905", {"start": v(-224.11, 193.87) * mm, "end": v(-224.78, 194.14) * mm});
            skLineSegment(sketch, "E2906", {"start": v(-224.78, 194.14) * mm, "end": v(-225.46, 194.4) * mm});
            skLineSegment(sketch, "E2907", {"start": v(-225.46, 194.4) * mm, "end": v(-226.14, 194.64) * mm});
            skLineSegment(sketch, "E2908", {"start": v(-226.14, 194.64) * mm, "end": v(-226.83, 194.87) * mm});
            skLineSegment(sketch, "E2909", {"start": v(-226.83, 194.87) * mm, "end": v(-227.53, 195.08) * mm});
            skLineSegment(sketch, "E2910", {"start": v(-227.53, 195.08) * mm, "end": v(-228.23, 195.27) * mm});
            skLineSegment(sketch, "E2911", {"start": v(-228.23, 195.27) * mm, "end": v(-228.94, 195.44) * mm});
            skLineSegment(sketch, "E2912", {"start": v(-228.94, 195.44) * mm, "end": v(-229.66, 195.6) * mm});
            skLineSegment(sketch, "E2913", {"start": v(-229.66, 195.6) * mm, "end": v(-230.39, 195.74) * mm});
            skLineSegment(sketch, "E2914", {"start": v(-230.39, 195.74) * mm, "end": v(-231.12, 195.86) * mm});
            skLineSegment(sketch, "E2915", {"start": v(-231.12, 195.86) * mm, "end": v(-231.85, 195.96) * mm});
            skLineSegment(sketch, "E2916", {"start": v(-231.85, 195.96) * mm, "end": v(-232.6, 196.05) * mm});
            skLineSegment(sketch, "E2917", {"start": v(-232.6, 196.05) * mm, "end": v(-233.34, 196.11) * mm});
            skLineSegment(sketch, "E2918", {"start": v(-233.34, 196.11) * mm, "end": v(-234.1, 196.16) * mm});
            skLineSegment(sketch, "E2919", {"start": v(-234.1, 196.16) * mm, "end": v(-234.85, 196.19) * mm});
            skLineSegment(sketch, "E2920", {"start": v(-234.85, 196.19) * mm, "end": v(-235.61, 196.2) * mm});
            skLineSegment(sketch, "E2921", {"start": v(-290.23, 98.37) * mm, "end": v(-290.48, 98.36) * mm});
            skLineSegment(sketch, "E2922", {"start": v(-290.48, 98.36) * mm, "end": v(-290.73, 98.33) * mm});
            skLineSegment(sketch, "E2923", {"start": v(-290.73, 98.33) * mm, "end": v(-290.97, 98.28) * mm});
            skLineSegment(sketch, "E2924", {"start": v(-290.97, 98.28) * mm, "end": v(-291.21, 98.22) * mm});
            skLineSegment(sketch, "E2925", {"start": v(-291.21, 98.22) * mm, "end": v(-291.45, 98.13) * mm});
            skLineSegment(sketch, "E2926", {"start": v(-291.45, 98.13) * mm, "end": v(-291.67, 98.02) * mm});
            skLineSegment(sketch, "E2927", {"start": v(-291.67, 98.02) * mm, "end": v(-291.9, 97.9) * mm});
            skLineSegment(sketch, "E2928", {"start": v(-291.9, 97.9) * mm, "end": v(-292.1, 97.75) * mm});
            skLineSegment(sketch, "E2929", {"start": v(-292.1, 97.75) * mm, "end": v(-292.34, 97.55) * mm});
            skLineSegment(sketch, "E2930", {"start": v(-292.34, 97.55) * mm, "end": v(-292.56, 97.34) * mm});
            skLineSegment(sketch, "E2931", {"start": v(-292.56, 97.34) * mm, "end": v(-292.76, 97.1) * mm});
            skLineSegment(sketch, "E2932", {"start": v(-292.76, 97.1) * mm, "end": v(-292.93, 96.84) * mm});
            skLineSegment(sketch, "E2933", {"start": v(-292.93, 96.84) * mm, "end": v(-293.07, 96.57) * mm});
            skLineSegment(sketch, "E2934", {"start": v(-293.07, 96.57) * mm, "end": v(-293.19, 96.29) * mm});
            skLineSegment(sketch, "E2935", {"start": v(-293.19, 96.29) * mm, "end": v(-293.28, 96) * mm});
            skLineSegment(sketch, "E2936", {"start": v(-293.28, 96) * mm, "end": v(-293.34, 95.69) * mm});
            skLineSegment(sketch, "E2937", {"start": v(-293.34, 95.69) * mm, "end": v(-301.96, 37.48) * mm});
            skLineSegment(sketch, "E2938", {"start": v(-301.96, 37.48) * mm, "end": v(-302, 37.16) * mm});
            skLineSegment(sketch, "E2939", {"start": v(-302, 37.16) * mm, "end": v(-302, 36.84) * mm});
            skLineSegment(sketch, "E2940", {"start": v(-302, 36.84) * mm, "end": v(-301.96, 36.54) * mm});
            skLineSegment(sketch, "E2941", {"start": v(-301.96, 36.54) * mm, "end": v(-301.9, 36.23) * mm});
            skLineSegment(sketch, "E2942", {"start": v(-301.9, 36.23) * mm, "end": v(-301.8, 35.94) * mm});
            skLineSegment(sketch, "E2943", {"start": v(-301.8, 35.94) * mm, "end": v(-301.69, 35.66) * mm});
            skLineSegment(sketch, "E2944", {"start": v(-301.69, 35.66) * mm, "end": v(-301.54, 35.4) * mm});
            skLineSegment(sketch, "E2945", {"start": v(-301.54, 35.4) * mm, "end": v(-301.38, 35.15) * mm});
            skLineSegment(sketch, "E2946", {"start": v(-301.38, 35.15) * mm, "end": v(-301.18, 34.91) * mm});
            skLineSegment(sketch, "E2947", {"start": v(-301.18, 34.91) * mm, "end": v(-300.97, 34.7) * mm});
            skLineSegment(sketch, "E2948", {"start": v(-300.97, 34.7) * mm, "end": v(-300.74, 34.5) * mm});
            skLineSegment(sketch, "E2949", {"start": v(-300.74, 34.5) * mm, "end": v(-300.49, 34.33) * mm});
            skLineSegment(sketch, "E2950", {"start": v(-300.49, 34.33) * mm, "end": v(-300.22, 34.18) * mm});
            skLineSegment(sketch, "E2951", {"start": v(-300.22, 34.18) * mm, "end": v(-299.93, 34.06) * mm});
            skLineSegment(sketch, "E2952", {"start": v(-299.93, 34.06) * mm, "end": v(-299.63, 33.97) * mm});
            skLineSegment(sketch, "E2953", {"start": v(-299.63, 33.97) * mm, "end": v(-299.31, 33.9) * mm});
            skLineSegment(sketch, "E2954", {"start": v(-299.31, 33.9) * mm, "end": v(-259.28, 27.98) * mm});
            skLineSegment(sketch, "E2955", {"start": v(-259.28, 27.98) * mm, "end": v(-258.96, 27.94) * mm});
            skLineSegment(sketch, "E2956", {"start": v(-258.96, 27.94) * mm, "end": v(-258.65, 27.94) * mm});
            skLineSegment(sketch, "E2957", {"start": v(-258.65, 27.94) * mm, "end": v(-258.34, 27.97) * mm});
            skLineSegment(sketch, "E2958", {"start": v(-258.34, 27.97) * mm, "end": v(-258.04, 28.04) * mm});
            skLineSegment(sketch, "E2959", {"start": v(-258.04, 28.04) * mm, "end": v(-257.74, 28.13) * mm});
            skLineSegment(sketch, "E2960", {"start": v(-257.74, 28.13) * mm, "end": v(-257.46, 28.24) * mm});
            skLineSegment(sketch, "E2961", {"start": v(-257.46, 28.24) * mm, "end": v(-257.2, 28.39) * mm});
            skLineSegment(sketch, "E2962", {"start": v(-257.2, 28.39) * mm, "end": v(-256.95, 28.56) * mm});
            skLineSegment(sketch, "E2963", {"start": v(-256.95, 28.56) * mm, "end": v(-256.71, 28.75) * mm});
            skLineSegment(sketch, "E2964", {"start": v(-256.71, 28.75) * mm, "end": v(-256.5, 28.96) * mm});
            skLineSegment(sketch, "E2965", {"start": v(-256.5, 28.96) * mm, "end": v(-256.3, 29.2) * mm});
            skLineSegment(sketch, "E2966", {"start": v(-256.3, 29.2) * mm, "end": v(-256.13, 29.45) * mm});
            skLineSegment(sketch, "E2967", {"start": v(-256.13, 29.45) * mm, "end": v(-255.99, 29.72) * mm});
            skLineSegment(sketch, "E2968", {"start": v(-255.99, 29.72) * mm, "end": v(-255.86, 30) * mm});
            skLineSegment(sketch, "E2969", {"start": v(-255.86, 30) * mm, "end": v(-255.77, 30.31) * mm});
            skLineSegment(sketch, "E2970", {"start": v(-255.77, 30.31) * mm, "end": v(-255.7, 30.63) * mm});
            skLineSegment(sketch, "E2971", {"start": v(-255.7, 30.63) * mm, "end": v(-247.08, 88.83) * mm});
            skLineSegment(sketch, "E2972", {"start": v(-247.08, 88.83) * mm, "end": v(-247.05, 89.14) * mm});
            skLineSegment(sketch, "E2973", {"start": v(-247.05, 89.14) * mm, "end": v(-247.05, 89.45) * mm});
            skLineSegment(sketch, "E2974", {"start": v(-247.05, 89.45) * mm, "end": v(-247.08, 89.76) * mm});
            skLineSegment(sketch, "E2975", {"start": v(-247.08, 89.76) * mm, "end": v(-247.14, 90.06) * mm});
            skLineSegment(sketch, "E2976", {"start": v(-247.14, 90.06) * mm, "end": v(-247.23, 90.35) * mm});
            skLineSegment(sketch, "E2977", {"start": v(-247.23, 90.35) * mm, "end": v(-247.35, 90.64) * mm});
            skLineSegment(sketch, "E2978", {"start": v(-247.35, 90.64) * mm, "end": v(-247.5, 90.9) * mm});
            skLineSegment(sketch, "E2979", {"start": v(-247.5, 90.9) * mm, "end": v(-247.67, 91.17) * mm});
            skLineSegment(sketch, "E2980", {"start": v(-247.67, 91.17) * mm, "end": v(-247.87, 91.41) * mm});
            skLineSegment(sketch, "E2981", {"start": v(-247.87, 91.41) * mm, "end": v(-248.09, 91.63) * mm});
            skLineSegment(sketch, "E2982", {"start": v(-248.09, 91.63) * mm, "end": v(-248.33, 91.83) * mm});
            skLineSegment(sketch, "E2983", {"start": v(-248.33, 91.83) * mm, "end": v(-248.58, 92) * mm});
            skLineSegment(sketch, "E2984", {"start": v(-248.58, 92) * mm, "end": v(-248.85, 92.14) * mm});
            skLineSegment(sketch, "E2985", {"start": v(-248.85, 92.14) * mm, "end": v(-249.13, 92.26) * mm});
            skLineSegment(sketch, "E2986", {"start": v(-249.13, 92.26) * mm, "end": v(-249.43, 92.35) * mm});
            skLineSegment(sketch, "E2987", {"start": v(-249.43, 92.35) * mm, "end": v(-249.74, 92.4) * mm});
            skLineSegment(sketch, "E2988", {"start": v(-249.74, 92.4) * mm, "end": v(-289.77, 98.34) * mm});
            skLineSegment(sketch, "E2989", {"start": v(-289.77, 98.34) * mm, "end": v(-290, 98.36) * mm});
            skLineSegment(sketch, "E2990", {"start": v(-290, 98.36) * mm, "end": v(-290.23, 98.37) * mm});
            skLineSegment(sketch, "E2991", {"start": v(-258.8, 24.36) * mm, "end": v(-259.3, 24.38) * mm});
            skLineSegment(sketch, "E2992", {"start": v(-259.3, 24.38) * mm, "end": v(-259.8, 24.43) * mm});
            skLineSegment(sketch, "E2993", {"start": v(-259.8, 24.43) * mm, "end": v(-299.84, 30.37) * mm});
            skLineSegment(sketch, "E2994", {"start": v(-299.84, 30.37) * mm, "end": v(-300.18, 30.42) * mm});
            skLineSegment(sketch, "E2995", {"start": v(-300.18, 30.42) * mm, "end": v(-300.51, 30.5) * mm});
            skLineSegment(sketch, "E2996", {"start": v(-300.51, 30.5) * mm, "end": v(-300.84, 30.6) * mm});
            skLineSegment(sketch, "E2997", {"start": v(-300.84, 30.6) * mm, "end": v(-301.16, 30.7) * mm});
            skLineSegment(sketch, "E2998", {"start": v(-301.16, 30.7) * mm, "end": v(-301.47, 30.82) * mm});
            skLineSegment(sketch, "E2999", {"start": v(-301.47, 30.82) * mm, "end": v(-301.77, 30.96) * mm});
            skLineSegment(sketch, "E3000", {"start": v(-301.77, 30.96) * mm, "end": v(-302.06, 31.1) * mm});
            skLineSegment(sketch, "E3001", {"start": v(-302.06, 31.1) * mm, "end": v(-302.35, 31.27) * mm});
            skLineSegment(sketch, "E3002", {"start": v(-302.35, 31.27) * mm, "end": v(-302.62, 31.45) * mm});
            skLineSegment(sketch, "E3003", {"start": v(-302.62, 31.45) * mm, "end": v(-302.89, 31.64) * mm});
            skLineSegment(sketch, "E3004", {"start": v(-302.89, 31.64) * mm, "end": v(-303.14, 31.84) * mm});
            skLineSegment(sketch, "E3005", {"start": v(-303.14, 31.84) * mm, "end": v(-303.39, 32.05) * mm});
            skLineSegment(sketch, "E3006", {"start": v(-303.39, 32.05) * mm, "end": v(-303.62, 32.28) * mm});
            skLineSegment(sketch, "E3007", {"start": v(-303.62, 32.28) * mm, "end": v(-303.84, 32.51) * mm});
            skLineSegment(sketch, "E3008", {"start": v(-303.84, 32.51) * mm, "end": v(-304.05, 32.76) * mm});
            skLineSegment(sketch, "E3009", {"start": v(-304.05, 32.76) * mm, "end": v(-304.25, 33.01) * mm});
            skLineSegment(sketch, "E3010", {"start": v(-304.25, 33.01) * mm, "end": v(-304.44, 33.28) * mm});
            skLineSegment(sketch, "E3011", {"start": v(-304.44, 33.28) * mm, "end": v(-304.61, 33.55) * mm});
            skLineSegment(sketch, "E3012", {"start": v(-304.61, 33.55) * mm, "end": v(-304.77, 33.83) * mm});
            skLineSegment(sketch, "E3013", {"start": v(-304.77, 33.83) * mm, "end": v(-304.92, 34.12) * mm});
            skLineSegment(sketch, "E3014", {"start": v(-304.92, 34.12) * mm, "end": v(-305.05, 34.42) * mm});
            skLineSegment(sketch, "E3015", {"start": v(-305.05, 34.42) * mm, "end": v(-305.17, 34.72) * mm});
            skLineSegment(sketch, "E3016", {"start": v(-305.17, 34.72) * mm, "end": v(-305.27, 35.03) * mm});
            skLineSegment(sketch, "E3017", {"start": v(-305.27, 35.03) * mm, "end": v(-305.36, 35.34) * mm});
            skLineSegment(sketch, "E3018", {"start": v(-305.36, 35.34) * mm, "end": v(-305.44, 35.66) * mm});
            skLineSegment(sketch, "E3019", {"start": v(-305.44, 35.66) * mm, "end": v(-305.5, 35.98) * mm});
            skLineSegment(sketch, "E3020", {"start": v(-305.5, 35.98) * mm, "end": v(-305.54, 36.31) * mm});
            skLineSegment(sketch, "E3021", {"start": v(-305.54, 36.31) * mm, "end": v(-305.57, 36.65) * mm});
            skLineSegment(sketch, "E3022", {"start": v(-305.57, 36.65) * mm, "end": v(-305.58, 36.98) * mm});
            skLineSegment(sketch, "E3023", {"start": v(-305.58, 36.98) * mm, "end": v(-305.57, 37.32) * mm});
            skLineSegment(sketch, "E3024", {"start": v(-305.57, 37.32) * mm, "end": v(-305.55, 37.66) * mm});
            skLineSegment(sketch, "E3025", {"start": v(-305.55, 37.66) * mm, "end": v(-305.5, 38) * mm});
            skLineSegment(sketch, "E3026", {"start": v(-305.5, 38) * mm, "end": v(-296.88, 96.21) * mm});
            skLineSegment(sketch, "E3027", {"start": v(-296.88, 96.21) * mm, "end": v(-296.82, 96.54) * mm});
            skLineSegment(sketch, "E3028", {"start": v(-296.82, 96.54) * mm, "end": v(-296.75, 96.87) * mm});
            skLineSegment(sketch, "E3029", {"start": v(-296.75, 96.87) * mm, "end": v(-296.66, 97.19) * mm});
            skLineSegment(sketch, "E3030", {"start": v(-296.66, 97.19) * mm, "end": v(-296.56, 97.5) * mm});
            skLineSegment(sketch, "E3031", {"start": v(-296.56, 97.5) * mm, "end": v(-296.44, 97.8) * mm});
            skLineSegment(sketch, "E3032", {"start": v(-296.44, 97.8) * mm, "end": v(-296.3, 98.1) * mm});
            skLineSegment(sketch, "E3033", {"start": v(-296.3, 98.1) * mm, "end": v(-296.16, 98.4) * mm});
            skLineSegment(sketch, "E3034", {"start": v(-296.16, 98.4) * mm, "end": v(-296, 98.69) * mm});
            skLineSegment(sketch, "E3035", {"start": v(-296, 98.69) * mm, "end": v(-295.83, 98.96) * mm});
            skLineSegment(sketch, "E3036", {"start": v(-295.83, 98.96) * mm, "end": v(-295.64, 99.23) * mm});
            skLineSegment(sketch, "E3037", {"start": v(-295.64, 99.23) * mm, "end": v(-295.44, 99.49) * mm});
            skLineSegment(sketch, "E3038", {"start": v(-295.44, 99.49) * mm, "end": v(-295.22, 99.74) * mm});
            skLineSegment(sketch, "E3039", {"start": v(-295.22, 99.74) * mm, "end": v(-295, 99.97) * mm});
            skLineSegment(sketch, "E3040", {"start": v(-295, 99.97) * mm, "end": v(-294.75, 100.2) * mm});
            skLineSegment(sketch, "E3041", {"start": v(-294.75, 100.2) * mm, "end": v(-294.5, 100.42) * mm});
            skLineSegment(sketch, "E3042", {"start": v(-294.5, 100.42) * mm, "end": v(-294.24, 100.63) * mm});
            skLineSegment(sketch, "E3043", {"start": v(-294.24, 100.63) * mm, "end": v(-293.96, 100.82) * mm});
            skLineSegment(sketch, "E3044", {"start": v(-293.96, 100.82) * mm, "end": v(-293.68, 101) * mm});
            skLineSegment(sketch, "E3045", {"start": v(-293.68, 101) * mm, "end": v(-293.4, 101.16) * mm});
            skLineSegment(sketch, "E3046", {"start": v(-293.4, 101.16) * mm, "end": v(-293.1, 101.31) * mm});
            skLineSegment(sketch, "E3047", {"start": v(-293.1, 101.31) * mm, "end": v(-292.8, 101.44) * mm});
            skLineSegment(sketch, "E3048", {"start": v(-292.8, 101.44) * mm, "end": v(-292.49, 101.56) * mm});
            skLineSegment(sketch, "E3049", {"start": v(-292.49, 101.56) * mm, "end": v(-292.18, 101.67) * mm});
            skLineSegment(sketch, "E3050", {"start": v(-292.18, 101.67) * mm, "end": v(-291.86, 101.75) * mm});
            skLineSegment(sketch, "E3051", {"start": v(-291.86, 101.75) * mm, "end": v(-291.54, 101.82) * mm});
            skLineSegment(sketch, "E3052", {"start": v(-291.54, 101.82) * mm, "end": v(-291.22, 101.88) * mm});
            skLineSegment(sketch, "E3053", {"start": v(-291.22, 101.88) * mm, "end": v(-290.9, 101.92) * mm});
            skLineSegment(sketch, "E3054", {"start": v(-290.9, 101.92) * mm, "end": v(-290.57, 101.94) * mm});
            skLineSegment(sketch, "E3055", {"start": v(-290.57, 101.94) * mm, "end": v(-290.24, 101.95) * mm});
            skLineSegment(sketch, "E3056", {"start": v(-290.24, 101.95) * mm, "end": v(-289.9, 101.94) * mm});
            skLineSegment(sketch, "E3057", {"start": v(-289.9, 101.94) * mm, "end": v(-289.57, 101.92) * mm});
            skLineSegment(sketch, "E3058", {"start": v(-289.57, 101.92) * mm, "end": v(-289.24, 101.88) * mm});
            skLineSegment(sketch, "E3059", {"start": v(-289.24, 101.88) * mm, "end": v(-249.21, 95.95) * mm});
            skLineSegment(sketch, "E3060", {"start": v(-249.21, 95.95) * mm, "end": v(-248.87, 95.9) * mm});
            skLineSegment(sketch, "E3061", {"start": v(-248.87, 95.9) * mm, "end": v(-248.54, 95.82) * mm});
            skLineSegment(sketch, "E3062", {"start": v(-248.54, 95.82) * mm, "end": v(-248.21, 95.72) * mm});
            skLineSegment(sketch, "E3063", {"start": v(-248.21, 95.72) * mm, "end": v(-247.9, 95.62) * mm});
            skLineSegment(sketch, "E3064", {"start": v(-247.9, 95.62) * mm, "end": v(-247.58, 95.5) * mm});
            skLineSegment(sketch, "E3065", {"start": v(-247.58, 95.5) * mm, "end": v(-247.28, 95.36) * mm});
            skLineSegment(sketch, "E3066", {"start": v(-247.28, 95.36) * mm, "end": v(-246.99, 95.2) * mm});
            skLineSegment(sketch, "E3067", {"start": v(-246.99, 95.2) * mm, "end": v(-246.7, 95.04) * mm});
            skLineSegment(sketch, "E3068", {"start": v(-246.7, 95.04) * mm, "end": v(-246.43, 94.86) * mm});
            skLineSegment(sketch, "E3069", {"start": v(-246.43, 94.86) * mm, "end": v(-246.16, 94.68) * mm});
            skLineSegment(sketch, "E3070", {"start": v(-246.16, 94.68) * mm, "end": v(-245.9, 94.47) * mm});
            skLineSegment(sketch, "E3071", {"start": v(-245.9, 94.47) * mm, "end": v(-245.66, 94.26) * mm});
            skLineSegment(sketch, "E3072", {"start": v(-245.66, 94.26) * mm, "end": v(-245.43, 94.04) * mm});
            skLineSegment(sketch, "E3073", {"start": v(-245.43, 94.04) * mm, "end": v(-245.2, 93.8) * mm});
            skLineSegment(sketch, "E3074", {"start": v(-245.2, 93.8) * mm, "end": v(-245, 93.56) * mm});
            skLineSegment(sketch, "E3075", {"start": v(-245, 93.56) * mm, "end": v(-244.8, 93.3) * mm});
            skLineSegment(sketch, "E3076", {"start": v(-244.8, 93.3) * mm, "end": v(-244.61, 93.04) * mm});
            skLineSegment(sketch, "E3077", {"start": v(-244.61, 93.04) * mm, "end": v(-244.44, 92.76) * mm});
            skLineSegment(sketch, "E3078", {"start": v(-244.44, 92.76) * mm, "end": v(-244.28, 92.48) * mm});
            skLineSegment(sketch, "E3079", {"start": v(-244.28, 92.48) * mm, "end": v(-244.13, 92.2) * mm});
            skLineSegment(sketch, "E3080", {"start": v(-244.13, 92.2) * mm, "end": v(-244, 91.9) * mm});
            skLineSegment(sketch, "E3081", {"start": v(-244, 91.9) * mm, "end": v(-243.88, 91.6) * mm});
            skLineSegment(sketch, "E3082", {"start": v(-243.88, 91.6) * mm, "end": v(-243.77, 91.29) * mm});
            skLineSegment(sketch, "E3083", {"start": v(-243.77, 91.29) * mm, "end": v(-243.68, 90.97) * mm});
            skLineSegment(sketch, "E3084", {"start": v(-243.68, 90.97) * mm, "end": v(-243.6, 90.65) * mm});
            skLineSegment(sketch, "E3085", {"start": v(-243.6, 90.65) * mm, "end": v(-243.55, 90.33) * mm});
            skLineSegment(sketch, "E3086", {"start": v(-243.55, 90.33) * mm, "end": v(-243.5, 90) * mm});
            skLineSegment(sketch, "E3087", {"start": v(-243.5, 90) * mm, "end": v(-243.48, 89.67) * mm});
            skLineSegment(sketch, "E3088", {"start": v(-243.48, 89.67) * mm, "end": v(-243.47, 89.33) * mm});
            skLineSegment(sketch, "E3089", {"start": v(-243.47, 89.33) * mm, "end": v(-243.48, 89) * mm});
            skLineSegment(sketch, "E3090", {"start": v(-243.48, 89) * mm, "end": v(-243.5, 88.65) * mm});
            skLineSegment(sketch, "E3091", {"start": v(-243.5, 88.65) * mm, "end": v(-243.54, 88.3) * mm});
            skLineSegment(sketch, "E3092", {"start": v(-243.54, 88.3) * mm, "end": v(-252.17, 30.1) * mm});
            skLineSegment(sketch, "E3093", {"start": v(-252.17, 30.1) * mm, "end": v(-252.22, 29.77) * mm});
            skLineSegment(sketch, "E3094", {"start": v(-252.22, 29.77) * mm, "end": v(-252.3, 29.45) * mm});
            skLineSegment(sketch, "E3095", {"start": v(-252.3, 29.45) * mm, "end": v(-252.38, 29.13) * mm});
            skLineSegment(sketch, "E3096", {"start": v(-252.38, 29.13) * mm, "end": v(-252.49, 28.81) * mm});
            skLineSegment(sketch, "E3097", {"start": v(-252.49, 28.81) * mm, "end": v(-252.6, 28.5) * mm});
            skLineSegment(sketch, "E3098", {"start": v(-252.6, 28.5) * mm, "end": v(-252.74, 28.2) * mm});
            skLineSegment(sketch, "E3099", {"start": v(-252.74, 28.2) * mm, "end": v(-252.89, 27.91) * mm});
            skLineSegment(sketch, "E3100", {"start": v(-252.89, 27.91) * mm, "end": v(-253.05, 27.63) * mm});
            skLineSegment(sketch, "E3101", {"start": v(-253.05, 27.63) * mm, "end": v(-253.22, 27.35) * mm});
            skLineSegment(sketch, "E3102", {"start": v(-253.22, 27.35) * mm, "end": v(-253.4, 27.09) * mm});
            skLineSegment(sketch, "E3103", {"start": v(-253.4, 27.09) * mm, "end": v(-253.61, 26.83) * mm});
            skLineSegment(sketch, "E3104", {"start": v(-253.61, 26.83) * mm, "end": v(-253.83, 26.58) * mm});
            skLineSegment(sketch, "E3105", {"start": v(-253.83, 26.58) * mm, "end": v(-254.05, 26.34) * mm});
            skLineSegment(sketch, "E3106", {"start": v(-254.05, 26.34) * mm, "end": v(-254.3, 26.11) * mm});
            skLineSegment(sketch, "E3107", {"start": v(-254.3, 26.11) * mm, "end": v(-254.55, 25.9) * mm});
            skLineSegment(sketch, "E3108", {"start": v(-254.55, 25.9) * mm, "end": v(-254.81, 25.69) * mm});
            skLineSegment(sketch, "E3109", {"start": v(-254.81, 25.69) * mm, "end": v(-255.26, 25.38) * mm});
            skLineSegment(sketch, "E3110", {"start": v(-255.26, 25.38) * mm, "end": v(-255.73, 25.11) * mm});
            skLineSegment(sketch, "E3111", {"start": v(-255.73, 25.11) * mm, "end": v(-256.21, 24.88) * mm});
            skLineSegment(sketch, "E3112", {"start": v(-256.21, 24.88) * mm, "end": v(-256.71, 24.7) * mm});
            skLineSegment(sketch, "E3113", {"start": v(-256.71, 24.7) * mm, "end": v(-257.22, 24.55) * mm});
            skLineSegment(sketch, "E3114", {"start": v(-257.22, 24.55) * mm, "end": v(-257.74, 24.45) * mm});
            skLineSegment(sketch, "E3115", {"start": v(-257.74, 24.45) * mm, "end": v(-258.27, 24.38) * mm});
            skLineSegment(sketch, "E3116", {"start": v(-258.27, 24.38) * mm, "end": v(-258.8, 24.36) * mm});
            skLineSegment(sketch, "E3117", {"start": v(-283, 39.61) * mm, "end": v(-283.02, 39.39) * mm});
            skLineSegment(sketch, "E3118", {"start": v(-283.02, 39.39) * mm, "end": v(-280.55, 34.51) * mm});
            skLineSegment(sketch, "E3119", {"start": v(-280.55, 34.51) * mm, "end": v(-284.1, 34.99) * mm});
            skLineSegment(sketch, "E3120", {"start": v(-284.1, 34.99) * mm, "end": v(-286.7, 40.13) * mm});
            skLineSegment(sketch, "E3121", {"start": v(-286.7, 40.13) * mm, "end": v(-286.18, 43.92) * mm});
            skLineSegment(sketch, "E3122", {"start": v(-286.18, 43.92) * mm, "end": v(-268, 41.46) * mm});
            skLineSegment(sketch, "E3123", {"start": v(-268, 41.46) * mm, "end": v(-268.52, 37.66) * mm});
            skLineSegment(sketch, "E3124", {"start": v(-268.52, 37.66) * mm, "end": v(-283, 39.61) * mm});
            skLineSegment(sketch, "E3125", {"start": v(-275.37, 57.94) * mm, "end": v(-276.14, 58.03) * mm});
            skLineSegment(sketch, "E3126", {"start": v(-276.14, 58.03) * mm, "end": v(-276.87, 58.08) * mm});
            skLineSegment(sketch, "E3127", {"start": v(-276.87, 58.08) * mm, "end": v(-277.55, 58.1) * mm});
            skLineSegment(sketch, "E3128", {"start": v(-277.55, 58.1) * mm, "end": v(-278.2, 58.09) * mm});
            skLineSegment(sketch, "E3129", {"start": v(-278.2, 58.09) * mm, "end": v(-278.78, 58.04) * mm});
            skLineSegment(sketch, "E3130", {"start": v(-278.78, 58.04) * mm, "end": v(-279.33, 57.95) * mm});
            skLineSegment(sketch, "E3131", {"start": v(-279.33, 57.95) * mm, "end": v(-279.83, 57.84) * mm});
            skLineSegment(sketch, "E3132", {"start": v(-279.83, 57.84) * mm, "end": v(-280.29, 57.69) * mm});
            skLineSegment(sketch, "E3133", {"start": v(-280.29, 57.69) * mm, "end": v(-280.7, 57.5) * mm});
            skLineSegment(sketch, "E3134", {"start": v(-280.7, 57.5) * mm, "end": v(-281.06, 57.3) * mm});
            skLineSegment(sketch, "E3135", {"start": v(-281.06, 57.3) * mm, "end": v(-281.38, 57.06) * mm});
            skLineSegment(sketch, "E3136", {"start": v(-281.38, 57.06) * mm, "end": v(-281.64, 56.8) * mm});
            skLineSegment(sketch, "E3137", {"start": v(-281.64, 56.8) * mm, "end": v(-281.86, 56.5) * mm});
            skLineSegment(sketch, "E3138", {"start": v(-281.86, 56.5) * mm, "end": v(-282.04, 56.17) * mm});
            skLineSegment(sketch, "E3139", {"start": v(-282.04, 56.17) * mm, "end": v(-282.16, 55.82) * mm});
            skLineSegment(sketch, "E3140", {"start": v(-282.16, 55.82) * mm, "end": v(-282.24, 55.45) * mm});
            skLineSegment(sketch, "E3141", {"start": v(-282.24, 55.45) * mm, "end": v(-282.27, 55.06) * mm});
            skLineSegment(sketch, "E3142", {"start": v(-282.27, 55.06) * mm, "end": v(-282.24, 54.7) * mm});
            skLineSegment(sketch, "E3143", {"start": v(-282.24, 54.7) * mm, "end": v(-282.16, 54.34) * mm});
            skLineSegment(sketch, "E3144", {"start": v(-282.16, 54.34) * mm, "end": v(-282.02, 54) * mm});
            skLineSegment(sketch, "E3145", {"start": v(-282.02, 54) * mm, "end": v(-281.83, 53.66) * mm});
            skLineSegment(sketch, "E3146", {"start": v(-281.83, 53.66) * mm, "end": v(-281.6, 53.35) * mm});
            skLineSegment(sketch, "E3147", {"start": v(-281.6, 53.35) * mm, "end": v(-281.3, 53.05) * mm});
            skLineSegment(sketch, "E3148", {"start": v(-281.3, 53.05) * mm, "end": v(-280.95, 52.77) * mm});
            skLineSegment(sketch, "E3149", {"start": v(-280.95, 52.77) * mm, "end": v(-280.55, 52.5) * mm});
            skLineSegment(sketch, "E3150", {"start": v(-280.55, 52.5) * mm, "end": v(-280.1, 52.26) * mm});
            skLineSegment(sketch, "E3151", {"start": v(-280.1, 52.26) * mm, "end": v(-279.6, 52.03) * mm});
            skLineSegment(sketch, "E3152", {"start": v(-279.6, 52.03) * mm, "end": v(-279.03, 51.83) * mm});
            skLineSegment(sketch, "E3153", {"start": v(-279.03, 51.83) * mm, "end": v(-278.42, 51.64) * mm});
            skLineSegment(sketch, "E3154", {"start": v(-278.42, 51.64) * mm, "end": v(-277.76, 51.48) * mm});
            skLineSegment(sketch, "E3155", {"start": v(-277.76, 51.48) * mm, "end": v(-277.05, 51.33) * mm});
            skLineSegment(sketch, "E3156", {"start": v(-277.05, 51.33) * mm, "end": v(-276.28, 51.21) * mm});
            skLineSegment(sketch, "E3157", {"start": v(-276.28, 51.21) * mm, "end": v(-275.5, 51.13) * mm});
            skLineSegment(sketch, "E3158", {"start": v(-275.5, 51.13) * mm, "end": v(-274.78, 51.07) * mm});
            skLineSegment(sketch, "E3159", {"start": v(-274.78, 51.07) * mm, "end": v(-274.09, 51.05) * mm});
            skLineSegment(sketch, "E3160", {"start": v(-274.09, 51.05) * mm, "end": v(-273.45, 51.07) * mm});
            skLineSegment(sketch, "E3161", {"start": v(-273.45, 51.07) * mm, "end": v(-272.85, 51.12) * mm});
            skLineSegment(sketch, "E3162", {"start": v(-272.85, 51.12) * mm, "end": v(-272.3, 51.2) * mm});
            skLineSegment(sketch, "E3163", {"start": v(-272.3, 51.2) * mm, "end": v(-271.79, 51.32) * mm});
            skLineSegment(sketch, "E3164", {"start": v(-271.79, 51.32) * mm, "end": v(-271.32, 51.46) * mm});
            skLineSegment(sketch, "E3165", {"start": v(-271.32, 51.46) * mm, "end": v(-270.9, 51.64) * mm});
            skLineSegment(sketch, "E3166", {"start": v(-270.9, 51.64) * mm, "end": v(-270.54, 51.85) * mm});
            skLineSegment(sketch, "E3167", {"start": v(-270.54, 51.85) * mm, "end": v(-270.22, 52.09) * mm});
            skLineSegment(sketch, "E3168", {"start": v(-270.22, 52.09) * mm, "end": v(-269.94, 52.35) * mm});
            skLineSegment(sketch, "E3169", {"start": v(-269.94, 52.35) * mm, "end": v(-269.72, 52.65) * mm});
            skLineSegment(sketch, "E3170", {"start": v(-269.72, 52.65) * mm, "end": v(-269.54, 52.97) * mm});
            skLineSegment(sketch, "E3171", {"start": v(-269.54, 52.97) * mm, "end": v(-269.42, 53.32) * mm});
            skLineSegment(sketch, "E3172", {"start": v(-269.42, 53.32) * mm, "end": v(-269.34, 53.7) * mm});
            skLineSegment(sketch, "E3173", {"start": v(-269.34, 53.7) * mm, "end": v(-269.31, 54.09) * mm});
            skLineSegment(sketch, "E3174", {"start": v(-269.31, 54.09) * mm, "end": v(-269.34, 54.46) * mm});
            skLineSegment(sketch, "E3175", {"start": v(-269.34, 54.46) * mm, "end": v(-269.43, 54.82) * mm});
            skLineSegment(sketch, "E3176", {"start": v(-269.43, 54.82) * mm, "end": v(-269.56, 55.16) * mm});
            skLineSegment(sketch, "E3177", {"start": v(-269.56, 55.16) * mm, "end": v(-269.75, 55.5) * mm});
            skLineSegment(sketch, "E3178", {"start": v(-269.75, 55.5) * mm, "end": v(-270, 55.81) * mm});
            skLineSegment(sketch, "E3179", {"start": v(-270, 55.81) * mm, "end": v(-270.3, 56.1) * mm});
            skLineSegment(sketch, "E3180", {"start": v(-270.3, 56.1) * mm, "end": v(-270.65, 56.4) * mm});
            skLineSegment(sketch, "E3181", {"start": v(-270.65, 56.4) * mm, "end": v(-271.06, 56.65) * mm});
            skLineSegment(sketch, "E3182", {"start": v(-271.06, 56.65) * mm, "end": v(-271.52, 56.9) * mm});
            skLineSegment(sketch, "E3183", {"start": v(-271.52, 56.9) * mm, "end": v(-272.03, 57.12) * mm});
            skLineSegment(sketch, "E3184", {"start": v(-272.03, 57.12) * mm, "end": v(-272.6, 57.33) * mm});
            skLineSegment(sketch, "E3185", {"start": v(-272.6, 57.33) * mm, "end": v(-273.2, 57.52) * mm});
            skLineSegment(sketch, "E3186", {"start": v(-273.2, 57.52) * mm, "end": v(-273.88, 57.68) * mm});
            skLineSegment(sketch, "E3187", {"start": v(-273.88, 57.68) * mm, "end": v(-274.6, 57.82) * mm});
            skLineSegment(sketch, "E3188", {"start": v(-274.6, 57.82) * mm, "end": v(-275.37, 57.94) * mm});
            skLineSegment(sketch, "E3189", {"start": v(-276.8, 47.36) * mm, "end": v(-277.36, 47.44) * mm});
            skLineSegment(sketch, "E3190", {"start": v(-277.36, 47.44) * mm, "end": v(-277.9, 47.54) * mm});
            skLineSegment(sketch, "E3191", {"start": v(-277.9, 47.54) * mm, "end": v(-278.42, 47.65) * mm});
            skLineSegment(sketch, "E3192", {"start": v(-278.42, 47.65) * mm, "end": v(-278.93, 47.78) * mm});
            skLineSegment(sketch, "E3193", {"start": v(-278.93, 47.78) * mm, "end": v(-279.41, 47.91) * mm});
            skLineSegment(sketch, "E3194", {"start": v(-279.41, 47.91) * mm, "end": v(-279.88, 48.07) * mm});
            skLineSegment(sketch, "E3195", {"start": v(-279.88, 48.07) * mm, "end": v(-280.33, 48.23) * mm});
            skLineSegment(sketch, "E3196", {"start": v(-280.33, 48.23) * mm, "end": v(-280.77, 48.4) * mm});
            skLineSegment(sketch, "E3197", {"start": v(-280.77, 48.4) * mm, "end": v(-281.18, 48.6) * mm});
            skLineSegment(sketch, "E3198", {"start": v(-281.18, 48.6) * mm, "end": v(-281.58, 48.8) * mm});
            skLineSegment(sketch, "E3199", {"start": v(-281.58, 48.8) * mm, "end": v(-281.96, 49) * mm});
            skLineSegment(sketch, "E3200", {"start": v(-281.96, 49) * mm, "end": v(-282.31, 49.23) * mm});
            skLineSegment(sketch, "E3201", {"start": v(-282.31, 49.23) * mm, "end": v(-282.66, 49.47) * mm});
            skLineSegment(sketch, "E3202", {"start": v(-282.66, 49.47) * mm, "end": v(-282.98, 49.71) * mm});
            skLineSegment(sketch, "E3203", {"start": v(-282.98, 49.71) * mm, "end": v(-283.28, 49.97) * mm});
            skLineSegment(sketch, "E3204", {"start": v(-283.28, 49.97) * mm, "end": v(-283.56, 50.24) * mm});
            skLineSegment(sketch, "E3205", {"start": v(-283.56, 50.24) * mm, "end": v(-283.83, 50.52) * mm});
            skLineSegment(sketch, "E3206", {"start": v(-283.83, 50.52) * mm, "end": v(-284.07, 50.81) * mm});
            skLineSegment(sketch, "E3207", {"start": v(-284.07, 50.81) * mm, "end": v(-284.3, 51.11) * mm});
            skLineSegment(sketch, "E3208", {"start": v(-284.3, 51.11) * mm, "end": v(-284.5, 51.43) * mm});
            skLineSegment(sketch, "E3209", {"start": v(-284.5, 51.43) * mm, "end": v(-284.69, 51.75) * mm});
            skLineSegment(sketch, "E3210", {"start": v(-284.69, 51.75) * mm, "end": v(-284.85, 52.08) * mm});
            skLineSegment(sketch, "E3211", {"start": v(-284.85, 52.08) * mm, "end": v(-285, 52.42) * mm});
            skLineSegment(sketch, "E3212", {"start": v(-285, 52.42) * mm, "end": v(-285.12, 52.77) * mm});
            skLineSegment(sketch, "E3213", {"start": v(-285.12, 52.77) * mm, "end": v(-285.22, 53.12) * mm});
            skLineSegment(sketch, "E3214", {"start": v(-285.22, 53.12) * mm, "end": v(-285.3, 53.5) * mm});
            skLineSegment(sketch, "E3215", {"start": v(-285.3, 53.5) * mm, "end": v(-285.36, 53.87) * mm});
            skLineSegment(sketch, "E3216", {"start": v(-285.36, 53.87) * mm, "end": v(-285.4, 54.25) * mm});
            skLineSegment(sketch, "E3217", {"start": v(-285.4, 54.25) * mm, "end": v(-285.42, 54.64) * mm});
            skLineSegment(sketch, "E3218", {"start": v(-285.42, 54.64) * mm, "end": v(-285.42, 55.04) * mm});
            skLineSegment(sketch, "E3219", {"start": v(-285.42, 55.04) * mm, "end": v(-285.4, 55.45) * mm});
            skLineSegment(sketch, "E3220", {"start": v(-285.4, 55.45) * mm, "end": v(-285.35, 55.87) * mm});
            skLineSegment(sketch, "E3221", {"start": v(-285.35, 55.87) * mm, "end": v(-285.28, 56.28) * mm});
            skLineSegment(sketch, "E3222", {"start": v(-285.28, 56.28) * mm, "end": v(-285.2, 56.68) * mm});
            skLineSegment(sketch, "E3223", {"start": v(-285.2, 56.68) * mm, "end": v(-285.1, 57.06) * mm});
            skLineSegment(sketch, "E3224", {"start": v(-285.1, 57.06) * mm, "end": v(-284.97, 57.44) * mm});
            skLineSegment(sketch, "E3225", {"start": v(-284.97, 57.44) * mm, "end": v(-284.83, 57.8) * mm});
            skLineSegment(sketch, "E3226", {"start": v(-284.83, 57.8) * mm, "end": v(-284.67, 58.14) * mm});
            skLineSegment(sketch, "E3227", {"start": v(-284.67, 58.14) * mm, "end": v(-284.5, 58.47) * mm});
            skLineSegment(sketch, "E3228", {"start": v(-284.5, 58.47) * mm, "end": v(-284.3, 58.79) * mm});
            skLineSegment(sketch, "E3229", {"start": v(-284.3, 58.79) * mm, "end": v(-284.09, 59.1) * mm});
            skLineSegment(sketch, "E3230", {"start": v(-284.09, 59.1) * mm, "end": v(-283.86, 59.38) * mm});
            skLineSegment(sketch, "E3231", {"start": v(-283.86, 59.38) * mm, "end": v(-283.61, 59.66) * mm});
            skLineSegment(sketch, "E3232", {"start": v(-283.61, 59.66) * mm, "end": v(-283.35, 59.92) * mm});
            skLineSegment(sketch, "E3233", {"start": v(-283.35, 59.92) * mm, "end": v(-283.07, 60.16) * mm});
            skLineSegment(sketch, "E3234", {"start": v(-283.07, 60.16) * mm, "end": v(-282.77, 60.4) * mm});
            skLineSegment(sketch, "E3235", {"start": v(-282.77, 60.4) * mm, "end": v(-282.46, 60.61) * mm});
            skLineSegment(sketch, "E3236", {"start": v(-282.46, 60.61) * mm, "end": v(-282.13, 60.81) * mm});
            skLineSegment(sketch, "E3237", {"start": v(-282.13, 60.81) * mm, "end": v(-281.79, 61) * mm});
            skLineSegment(sketch, "E3238", {"start": v(-281.79, 61) * mm, "end": v(-281.42, 61.16) * mm});
            skLineSegment(sketch, "E3239", {"start": v(-281.42, 61.16) * mm, "end": v(-281.05, 61.32) * mm});
            skLineSegment(sketch, "E3240", {"start": v(-281.05, 61.32) * mm, "end": v(-280.66, 61.46) * mm});
            skLineSegment(sketch, "E3241", {"start": v(-280.66, 61.46) * mm, "end": v(-280.25, 61.58) * mm});
            skLineSegment(sketch, "E3242", {"start": v(-280.25, 61.58) * mm, "end": v(-279.83, 61.68) * mm});
            skLineSegment(sketch, "E3243", {"start": v(-279.83, 61.68) * mm, "end": v(-279.4, 61.77) * mm});
            skLineSegment(sketch, "E3244", {"start": v(-279.4, 61.77) * mm, "end": v(-278.94, 61.84) * mm});
            skLineSegment(sketch, "E3245", {"start": v(-278.94, 61.84) * mm, "end": v(-278.48, 61.9) * mm});
            skLineSegment(sketch, "E3246", {"start": v(-278.48, 61.9) * mm, "end": v(-278, 61.93) * mm});
            skLineSegment(sketch, "E3247", {"start": v(-278, 61.93) * mm, "end": v(-277.5, 61.96) * mm});
            skLineSegment(sketch, "E3248", {"start": v(-277.5, 61.96) * mm, "end": v(-277, 61.96) * mm});
            skLineSegment(sketch, "E3249", {"start": v(-277, 61.96) * mm, "end": v(-276.48, 61.94) * mm});
            skLineSegment(sketch, "E3250", {"start": v(-276.48, 61.94) * mm, "end": v(-275.94, 61.91) * mm});
            skLineSegment(sketch, "E3251", {"start": v(-275.94, 61.91) * mm, "end": v(-275.4, 61.86) * mm});
            skLineSegment(sketch, "E3252", {"start": v(-275.4, 61.86) * mm, "end": v(-274.84, 61.8) * mm});
            skLineSegment(sketch, "E3253", {"start": v(-274.84, 61.8) * mm, "end": v(-274.28, 61.71) * mm});
            skLineSegment(sketch, "E3254", {"start": v(-274.28, 61.71) * mm, "end": v(-273.74, 61.62) * mm});
            skLineSegment(sketch, "E3255", {"start": v(-273.74, 61.62) * mm, "end": v(-273.22, 61.5) * mm});
            skLineSegment(sketch, "E3256", {"start": v(-273.22, 61.5) * mm, "end": v(-272.72, 61.38) * mm});
            skLineSegment(sketch, "E3257", {"start": v(-272.72, 61.38) * mm, "end": v(-272.23, 61.24) * mm});
            skLineSegment(sketch, "E3258", {"start": v(-272.23, 61.24) * mm, "end": v(-271.76, 61.1) * mm});
            skLineSegment(sketch, "E3259", {"start": v(-271.76, 61.1) * mm, "end": v(-271.3, 60.93) * mm});
            skLineSegment(sketch, "E3260", {"start": v(-271.3, 60.93) * mm, "end": v(-270.87, 60.76) * mm});
            skLineSegment(sketch, "E3261", {"start": v(-270.87, 60.76) * mm, "end": v(-270.46, 60.57) * mm});
            skLineSegment(sketch, "E3262", {"start": v(-270.46, 60.57) * mm, "end": v(-270.06, 60.37) * mm});
            skLineSegment(sketch, "E3263", {"start": v(-270.06, 60.37) * mm, "end": v(-269.68, 60.15) * mm});
            skLineSegment(sketch, "E3264", {"start": v(-269.68, 60.15) * mm, "end": v(-269.31, 59.93) * mm});
            skLineSegment(sketch, "E3265", {"start": v(-269.31, 59.93) * mm, "end": v(-268.97, 59.7) * mm});
            skLineSegment(sketch, "E3266", {"start": v(-268.97, 59.7) * mm, "end": v(-268.65, 59.45) * mm});
            skLineSegment(sketch, "E3267", {"start": v(-268.65, 59.45) * mm, "end": v(-268.34, 59.19) * mm});
            skLineSegment(sketch, "E3268", {"start": v(-268.34, 59.19) * mm, "end": v(-268.06, 58.92) * mm});
            skLineSegment(sketch, "E3269", {"start": v(-268.06, 58.92) * mm, "end": v(-267.79, 58.64) * mm});
            skLineSegment(sketch, "E3270", {"start": v(-267.79, 58.64) * mm, "end": v(-267.54, 58.35) * mm});
            skLineSegment(sketch, "E3271", {"start": v(-267.54, 58.35) * mm, "end": v(-267.31, 58.05) * mm});
            skLineSegment(sketch, "E3272", {"start": v(-267.31, 58.05) * mm, "end": v(-267.1, 57.74) * mm});
            skLineSegment(sketch, "E3273", {"start": v(-267.1, 57.74) * mm, "end": v(-266.92, 57.42) * mm});
            skLineSegment(sketch, "E3274", {"start": v(-266.92, 57.42) * mm, "end": v(-266.75, 57.09) * mm});
            skLineSegment(sketch, "E3275", {"start": v(-266.75, 57.09) * mm, "end": v(-266.6, 56.74) * mm});
            skLineSegment(sketch, "E3276", {"start": v(-266.6, 56.74) * mm, "end": v(-266.48, 56.4) * mm});
            skLineSegment(sketch, "E3277", {"start": v(-266.48, 56.4) * mm, "end": v(-266.37, 56.04) * mm});
            skLineSegment(sketch, "E3278", {"start": v(-266.37, 56.04) * mm, "end": v(-266.3, 55.67) * mm});
            skLineSegment(sketch, "E3279", {"start": v(-266.3, 55.67) * mm, "end": v(-266.23, 55.3) * mm});
            skLineSegment(sketch, "E3280", {"start": v(-266.23, 55.3) * mm, "end": v(-266.19, 54.9) * mm});
            skLineSegment(sketch, "E3281", {"start": v(-266.19, 54.9) * mm, "end": v(-266.17, 54.51) * mm});
            skLineSegment(sketch, "E3282", {"start": v(-266.17, 54.51) * mm, "end": v(-266.17, 54.1) * mm});
            skLineSegment(sketch, "E3283", {"start": v(-266.17, 54.1) * mm, "end": v(-266.2, 53.7) * mm});
            skLineSegment(sketch, "E3284", {"start": v(-266.2, 53.7) * mm, "end": v(-266.24, 53.28) * mm});
            skLineSegment(sketch, "E3285", {"start": v(-266.24, 53.28) * mm, "end": v(-266.3, 52.86) * mm});
            skLineSegment(sketch, "E3286", {"start": v(-266.3, 52.86) * mm, "end": v(-266.4, 52.46) * mm});
            skLineSegment(sketch, "E3287", {"start": v(-266.4, 52.46) * mm, "end": v(-266.5, 52.08) * mm});
            skLineSegment(sketch, "E3288", {"start": v(-266.5, 52.08) * mm, "end": v(-266.62, 51.7) * mm});
            skLineSegment(sketch, "E3289", {"start": v(-266.62, 51.7) * mm, "end": v(-266.76, 51.34) * mm});
            skLineSegment(sketch, "E3290", {"start": v(-266.76, 51.34) * mm, "end": v(-266.92, 51) * mm});
            skLineSegment(sketch, "E3291", {"start": v(-266.92, 51) * mm, "end": v(-267.1, 50.66) * mm});
            skLineSegment(sketch, "E3292", {"start": v(-267.1, 50.66) * mm, "end": v(-267.3, 50.34) * mm});
            skLineSegment(sketch, "E3293", {"start": v(-267.3, 50.34) * mm, "end": v(-267.51, 50.04) * mm});
            skLineSegment(sketch, "E3294", {"start": v(-267.51, 50.04) * mm, "end": v(-267.74, 49.75) * mm});
            skLineSegment(sketch, "E3295", {"start": v(-267.74, 49.75) * mm, "end": v(-268, 49.48) * mm});
            skLineSegment(sketch, "E3296", {"start": v(-268, 49.48) * mm, "end": v(-268.26, 49.22) * mm});
            skLineSegment(sketch, "E3297", {"start": v(-268.26, 49.22) * mm, "end": v(-268.54, 48.97) * mm});
            skLineSegment(sketch, "E3298", {"start": v(-268.54, 48.97) * mm, "end": v(-268.84, 48.74) * mm});
            skLineSegment(sketch, "E3299", {"start": v(-268.84, 48.74) * mm, "end": v(-269.15, 48.53) * mm});
            skLineSegment(sketch, "E3300", {"start": v(-269.15, 48.53) * mm, "end": v(-269.49, 48.33) * mm});
            skLineSegment(sketch, "E3301", {"start": v(-269.49, 48.33) * mm, "end": v(-269.83, 48.14) * mm});
            skLineSegment(sketch, "E3302", {"start": v(-269.83, 48.14) * mm, "end": v(-270.2, 47.98) * mm});
            skLineSegment(sketch, "E3303", {"start": v(-270.2, 47.98) * mm, "end": v(-270.58, 47.82) * mm});
            skLineSegment(sketch, "E3304", {"start": v(-270.58, 47.82) * mm, "end": v(-270.97, 47.69) * mm});
            skLineSegment(sketch, "E3305", {"start": v(-270.97, 47.69) * mm, "end": v(-271.38, 47.57) * mm});
            skLineSegment(sketch, "E3306", {"start": v(-271.38, 47.57) * mm, "end": v(-271.8, 47.47) * mm});
            skLineSegment(sketch, "E3307", {"start": v(-271.8, 47.47) * mm, "end": v(-272.24, 47.38) * mm});
            skLineSegment(sketch, "E3308", {"start": v(-272.24, 47.38) * mm, "end": v(-272.7, 47.3) * mm});
            skLineSegment(sketch, "E3309", {"start": v(-272.7, 47.3) * mm, "end": v(-273.16, 47.26) * mm});
            skLineSegment(sketch, "E3310", {"start": v(-273.16, 47.26) * mm, "end": v(-273.64, 47.22) * mm});
            skLineSegment(sketch, "E3311", {"start": v(-273.64, 47.22) * mm, "end": v(-274.13, 47.2) * mm});
            skLineSegment(sketch, "E3312", {"start": v(-274.13, 47.2) * mm, "end": v(-274.64, 47.2) * mm});
            skLineSegment(sketch, "E3313", {"start": v(-274.64, 47.2) * mm, "end": v(-275.16, 47.21) * mm});
            skLineSegment(sketch, "E3314", {"start": v(-275.16, 47.21) * mm, "end": v(-275.7, 47.24) * mm});
            skLineSegment(sketch, "E3315", {"start": v(-275.7, 47.24) * mm, "end": v(-276.24, 47.3) * mm});
            skLineSegment(sketch, "E3316", {"start": v(-276.24, 47.3) * mm, "end": v(-276.8, 47.36) * mm});
            skLineSegment(sketch, "E3317", {"start": v(-272.82, 75.14) * mm, "end": v(-273.6, 75.23) * mm});
            skLineSegment(sketch, "E3318", {"start": v(-273.6, 75.23) * mm, "end": v(-274.32, 75.28) * mm});
            skLineSegment(sketch, "E3319", {"start": v(-274.32, 75.28) * mm, "end": v(-275, 75.3) * mm});
            skLineSegment(sketch, "E3320", {"start": v(-275, 75.3) * mm, "end": v(-275.64, 75.28) * mm});
            skLineSegment(sketch, "E3321", {"start": v(-275.64, 75.28) * mm, "end": v(-276.24, 75.23) * mm});
            skLineSegment(sketch, "E3322", {"start": v(-276.24, 75.23) * mm, "end": v(-276.78, 75.15) * mm});
            skLineSegment(sketch, "E3323", {"start": v(-276.78, 75.15) * mm, "end": v(-277.28, 75.03) * mm});
            skLineSegment(sketch, "E3324", {"start": v(-277.28, 75.03) * mm, "end": v(-277.74, 74.89) * mm});
            skLineSegment(sketch, "E3325", {"start": v(-277.74, 74.89) * mm, "end": v(-278.15, 74.7) * mm});
            skLineSegment(sketch, "E3326", {"start": v(-278.15, 74.7) * mm, "end": v(-278.51, 74.5) * mm});
            skLineSegment(sketch, "E3327", {"start": v(-278.51, 74.5) * mm, "end": v(-278.83, 74.26) * mm});
            skLineSegment(sketch, "E3328", {"start": v(-278.83, 74.26) * mm, "end": v(-279.1, 74) * mm});
            skLineSegment(sketch, "E3329", {"start": v(-279.1, 74) * mm, "end": v(-279.32, 73.7) * mm});
            skLineSegment(sketch, "E3330", {"start": v(-279.32, 73.7) * mm, "end": v(-279.49, 73.37) * mm});
            skLineSegment(sketch, "E3331", {"start": v(-279.49, 73.37) * mm, "end": v(-279.62, 73.02) * mm});
            skLineSegment(sketch, "E3332", {"start": v(-279.62, 73.02) * mm, "end": v(-279.7, 72.65) * mm});
            skLineSegment(sketch, "E3333", {"start": v(-279.7, 72.65) * mm, "end": v(-279.72, 72.26) * mm});
            skLineSegment(sketch, "E3334", {"start": v(-279.72, 72.26) * mm, "end": v(-279.69, 71.9) * mm});
            skLineSegment(sketch, "E3335", {"start": v(-279.69, 71.9) * mm, "end": v(-279.6, 71.54) * mm});
            skLineSegment(sketch, "E3336", {"start": v(-279.6, 71.54) * mm, "end": v(-279.47, 71.2) * mm});
            skLineSegment(sketch, "E3337", {"start": v(-279.47, 71.2) * mm, "end": v(-279.28, 70.86) * mm});
            skLineSegment(sketch, "E3338", {"start": v(-279.28, 70.86) * mm, "end": v(-279.04, 70.55) * mm});
            skLineSegment(sketch, "E3339", {"start": v(-279.04, 70.55) * mm, "end": v(-278.75, 70.25) * mm});
            skLineSegment(sketch, "E3340", {"start": v(-278.75, 70.25) * mm, "end": v(-278.4, 69.97) * mm});
            skLineSegment(sketch, "E3341", {"start": v(-278.4, 69.97) * mm, "end": v(-278, 69.7) * mm});
            skLineSegment(sketch, "E3342", {"start": v(-278, 69.7) * mm, "end": v(-277.55, 69.46) * mm});
            skLineSegment(sketch, "E3343", {"start": v(-277.55, 69.46) * mm, "end": v(-277.04, 69.23) * mm});
            skLineSegment(sketch, "E3344", {"start": v(-277.04, 69.23) * mm, "end": v(-276.48, 69.03) * mm});
            skLineSegment(sketch, "E3345", {"start": v(-276.48, 69.03) * mm, "end": v(-275.88, 68.84) * mm});
            skLineSegment(sketch, "E3346", {"start": v(-275.88, 68.84) * mm, "end": v(-275.21, 68.67) * mm});
            skLineSegment(sketch, "E3347", {"start": v(-275.21, 68.67) * mm, "end": v(-274.5, 68.53) * mm});
            skLineSegment(sketch, "E3348", {"start": v(-274.5, 68.53) * mm, "end": v(-273.73, 68.41) * mm});
            skLineSegment(sketch, "E3349", {"start": v(-273.73, 68.41) * mm, "end": v(-272.96, 68.32) * mm});
            skLineSegment(sketch, "E3350", {"start": v(-272.96, 68.32) * mm, "end": v(-272.23, 68.27) * mm});
            skLineSegment(sketch, "E3351", {"start": v(-272.23, 68.27) * mm, "end": v(-271.54, 68.25) * mm});
            skLineSegment(sketch, "E3352", {"start": v(-271.54, 68.25) * mm, "end": v(-270.9, 68.27) * mm});
            skLineSegment(sketch, "E3353", {"start": v(-270.9, 68.27) * mm, "end": v(-270.3, 68.32) * mm});
            skLineSegment(sketch, "E3354", {"start": v(-270.3, 68.32) * mm, "end": v(-269.74, 68.4) * mm});
            skLineSegment(sketch, "E3355", {"start": v(-269.74, 68.4) * mm, "end": v(-269.24, 68.51) * mm});
            skLineSegment(sketch, "E3356", {"start": v(-269.24, 68.51) * mm, "end": v(-268.78, 68.66) * mm});
            skLineSegment(sketch, "E3357", {"start": v(-268.78, 68.66) * mm, "end": v(-268.36, 68.84) * mm});
            skLineSegment(sketch, "E3358", {"start": v(-268.36, 68.84) * mm, "end": v(-268, 69.05) * mm});
            skLineSegment(sketch, "E3359", {"start": v(-268, 69.05) * mm, "end": v(-267.67, 69.29) * mm});
            skLineSegment(sketch, "E3360", {"start": v(-267.67, 69.29) * mm, "end": v(-267.4, 69.55) * mm});
            skLineSegment(sketch, "E3361", {"start": v(-267.4, 69.55) * mm, "end": v(-267.17, 69.85) * mm});
            skLineSegment(sketch, "E3362", {"start": v(-267.17, 69.85) * mm, "end": v(-267, 70.17) * mm});
            skLineSegment(sketch, "E3363", {"start": v(-267, 70.17) * mm, "end": v(-266.87, 70.52) * mm});
            skLineSegment(sketch, "E3364", {"start": v(-266.87, 70.52) * mm, "end": v(-266.8, 70.9) * mm});
            skLineSegment(sketch, "E3365", {"start": v(-266.8, 70.9) * mm, "end": v(-266.76, 71.29) * mm});
            skLineSegment(sketch, "E3366", {"start": v(-266.76, 71.29) * mm, "end": v(-266.8, 71.66) * mm});
            skLineSegment(sketch, "E3367", {"start": v(-266.8, 71.66) * mm, "end": v(-266.88, 72.02) * mm});
            skLineSegment(sketch, "E3368", {"start": v(-266.88, 72.02) * mm, "end": v(-267.01, 72.36) * mm});
            skLineSegment(sketch, "E3369", {"start": v(-267.01, 72.36) * mm, "end": v(-267.2, 72.7) * mm});
            skLineSegment(sketch, "E3370", {"start": v(-267.2, 72.7) * mm, "end": v(-267.45, 73) * mm});
            skLineSegment(sketch, "E3371", {"start": v(-267.45, 73) * mm, "end": v(-267.75, 73.3) * mm});
            skLineSegment(sketch, "E3372", {"start": v(-267.75, 73.3) * mm, "end": v(-268.1, 73.59) * mm});
            skLineSegment(sketch, "E3373", {"start": v(-268.1, 73.59) * mm, "end": v(-268.5, 73.85) * mm});
            skLineSegment(sketch, "E3374", {"start": v(-268.5, 73.85) * mm, "end": v(-268.97, 74.1) * mm});
            skLineSegment(sketch, "E3375", {"start": v(-268.97, 74.1) * mm, "end": v(-269.48, 74.32) * mm});
            skLineSegment(sketch, "E3376", {"start": v(-269.48, 74.32) * mm, "end": v(-270.04, 74.53) * mm});
            skLineSegment(sketch, "E3377", {"start": v(-270.04, 74.53) * mm, "end": v(-270.66, 74.71) * mm});
            skLineSegment(sketch, "E3378", {"start": v(-270.66, 74.71) * mm, "end": v(-271.33, 74.88) * mm});
            skLineSegment(sketch, "E3379", {"start": v(-271.33, 74.88) * mm, "end": v(-272.05, 75.02) * mm});
            skLineSegment(sketch, "E3380", {"start": v(-272.05, 75.02) * mm, "end": v(-272.82, 75.14) * mm});
            skLineSegment(sketch, "E3381", {"start": v(-274.26, 64.56) * mm, "end": v(-274.81, 64.64) * mm});
            skLineSegment(sketch, "E3382", {"start": v(-274.81, 64.64) * mm, "end": v(-275.35, 64.74) * mm});
            skLineSegment(sketch, "E3383", {"start": v(-275.35, 64.74) * mm, "end": v(-275.87, 64.85) * mm});
            skLineSegment(sketch, "E3384", {"start": v(-275.87, 64.85) * mm, "end": v(-276.38, 64.97) * mm});
            skLineSegment(sketch, "E3385", {"start": v(-276.38, 64.97) * mm, "end": v(-276.86, 65.11) * mm});
            skLineSegment(sketch, "E3386", {"start": v(-276.86, 65.11) * mm, "end": v(-277.33, 65.26) * mm});
            skLineSegment(sketch, "E3387", {"start": v(-277.33, 65.26) * mm, "end": v(-277.78, 65.43) * mm});
            skLineSegment(sketch, "E3388", {"start": v(-277.78, 65.43) * mm, "end": v(-278.22, 65.6) * mm});
            skLineSegment(sketch, "E3389", {"start": v(-278.22, 65.6) * mm, "end": v(-278.63, 65.8) * mm});
            skLineSegment(sketch, "E3390", {"start": v(-278.63, 65.8) * mm, "end": v(-279.03, 66) * mm});
            skLineSegment(sketch, "E3391", {"start": v(-279.03, 66) * mm, "end": v(-279.4, 66.2) * mm});
            skLineSegment(sketch, "E3392", {"start": v(-279.4, 66.2) * mm, "end": v(-279.77, 66.43) * mm});
            skLineSegment(sketch, "E3393", {"start": v(-279.77, 66.43) * mm, "end": v(-280.1, 66.67) * mm});
            skLineSegment(sketch, "E3394", {"start": v(-280.1, 66.67) * mm, "end": v(-280.43, 66.91) * mm});
            skLineSegment(sketch, "E3395", {"start": v(-280.43, 66.91) * mm, "end": v(-280.73, 67.17) * mm});
            skLineSegment(sketch, "E3396", {"start": v(-280.73, 67.17) * mm, "end": v(-281.02, 67.44) * mm});
            skLineSegment(sketch, "E3397", {"start": v(-281.02, 67.44) * mm, "end": v(-281.28, 67.72) * mm});
            skLineSegment(sketch, "E3398", {"start": v(-281.28, 67.72) * mm, "end": v(-281.52, 68.01) * mm});
            skLineSegment(sketch, "E3399", {"start": v(-281.52, 68.01) * mm, "end": v(-281.75, 68.31) * mm});
            skLineSegment(sketch, "E3400", {"start": v(-281.75, 68.31) * mm, "end": v(-281.95, 68.62) * mm});
            skLineSegment(sketch, "E3401", {"start": v(-281.95, 68.62) * mm, "end": v(-282.14, 68.94) * mm});
            skLineSegment(sketch, "E3402", {"start": v(-282.14, 68.94) * mm, "end": v(-282.3, 69.28) * mm});
            skLineSegment(sketch, "E3403", {"start": v(-282.3, 69.28) * mm, "end": v(-282.45, 69.62) * mm});
            skLineSegment(sketch, "E3404", {"start": v(-282.45, 69.62) * mm, "end": v(-282.57, 69.96) * mm});
            skLineSegment(sketch, "E3405", {"start": v(-282.57, 69.96) * mm, "end": v(-282.67, 70.32) * mm});
            skLineSegment(sketch, "E3406", {"start": v(-282.67, 70.32) * mm, "end": v(-282.76, 70.69) * mm});
            skLineSegment(sketch, "E3407", {"start": v(-282.76, 70.69) * mm, "end": v(-282.82, 71.07) * mm});
            skLineSegment(sketch, "E3408", {"start": v(-282.82, 71.07) * mm, "end": v(-282.86, 71.45) * mm});
            skLineSegment(sketch, "E3409", {"start": v(-282.86, 71.45) * mm, "end": v(-282.88, 71.84) * mm});
            skLineSegment(sketch, "E3410", {"start": v(-282.88, 71.84) * mm, "end": v(-282.87, 72.24) * mm});
            skLineSegment(sketch, "E3411", {"start": v(-282.87, 72.24) * mm, "end": v(-282.85, 72.65) * mm});
            skLineSegment(sketch, "E3412", {"start": v(-282.85, 72.65) * mm, "end": v(-282.8, 73.06) * mm});
            skLineSegment(sketch, "E3413", {"start": v(-282.8, 73.06) * mm, "end": v(-282.74, 73.48) * mm});
            skLineSegment(sketch, "E3414", {"start": v(-282.74, 73.48) * mm, "end": v(-282.65, 73.88) * mm});
            skLineSegment(sketch, "E3415", {"start": v(-282.65, 73.88) * mm, "end": v(-282.55, 74.26) * mm});
            skLineSegment(sketch, "E3416", {"start": v(-282.55, 74.26) * mm, "end": v(-282.43, 74.63) * mm});
            skLineSegment(sketch, "E3417", {"start": v(-282.43, 74.63) * mm, "end": v(-282.28, 75) * mm});
            skLineSegment(sketch, "E3418", {"start": v(-282.28, 75) * mm, "end": v(-282.13, 75.34) * mm});
            skLineSegment(sketch, "E3419", {"start": v(-282.13, 75.34) * mm, "end": v(-281.95, 75.67) * mm});
            skLineSegment(sketch, "E3420", {"start": v(-281.95, 75.67) * mm, "end": v(-281.75, 75.99) * mm});
            skLineSegment(sketch, "E3421", {"start": v(-281.75, 75.99) * mm, "end": v(-281.54, 76.3) * mm});
            skLineSegment(sketch, "E3422", {"start": v(-281.54, 76.3) * mm, "end": v(-281.31, 76.58) * mm});
            skLineSegment(sketch, "E3423", {"start": v(-281.31, 76.58) * mm, "end": v(-281.07, 76.86) * mm});
            skLineSegment(sketch, "E3424", {"start": v(-281.07, 76.86) * mm, "end": v(-280.8, 77.12) * mm});
            skLineSegment(sketch, "E3425", {"start": v(-280.8, 77.12) * mm, "end": v(-280.52, 77.36) * mm});
            skLineSegment(sketch, "E3426", {"start": v(-280.52, 77.36) * mm, "end": v(-280.22, 77.6) * mm});
            skLineSegment(sketch, "E3427", {"start": v(-280.22, 77.6) * mm, "end": v(-279.91, 77.8) * mm});
            skLineSegment(sketch, "E3428", {"start": v(-279.91, 77.8) * mm, "end": v(-279.58, 78) * mm});
            skLineSegment(sketch, "E3429", {"start": v(-279.58, 78) * mm, "end": v(-279.24, 78.2) * mm});
            skLineSegment(sketch, "E3430", {"start": v(-279.24, 78.2) * mm, "end": v(-278.88, 78.36) * mm});
            skLineSegment(sketch, "E3431", {"start": v(-278.88, 78.36) * mm, "end": v(-278.5, 78.52) * mm});
            skLineSegment(sketch, "E3432", {"start": v(-278.5, 78.52) * mm, "end": v(-278.1, 78.65) * mm});
            skLineSegment(sketch, "E3433", {"start": v(-278.1, 78.65) * mm, "end": v(-277.7, 78.77) * mm});
            skLineSegment(sketch, "E3434", {"start": v(-277.7, 78.77) * mm, "end": v(-277.28, 78.88) * mm});
            skLineSegment(sketch, "E3435", {"start": v(-277.28, 78.88) * mm, "end": v(-276.84, 78.97) * mm});
            skLineSegment(sketch, "E3436", {"start": v(-276.84, 78.97) * mm, "end": v(-276.4, 79.04) * mm});
            skLineSegment(sketch, "E3437", {"start": v(-276.4, 79.04) * mm, "end": v(-275.93, 79.1) * mm});
            skLineSegment(sketch, "E3438", {"start": v(-275.93, 79.1) * mm, "end": v(-275.45, 79.13) * mm});
            skLineSegment(sketch, "E3439", {"start": v(-275.45, 79.13) * mm, "end": v(-274.95, 79.15) * mm});
            skLineSegment(sketch, "E3440", {"start": v(-274.95, 79.15) * mm, "end": v(-274.45, 79.16) * mm});
            skLineSegment(sketch, "E3441", {"start": v(-274.45, 79.16) * mm, "end": v(-273.93, 79.14) * mm});
            skLineSegment(sketch, "E3442", {"start": v(-273.93, 79.14) * mm, "end": v(-273.4, 79.11) * mm});
            skLineSegment(sketch, "E3443", {"start": v(-273.4, 79.11) * mm, "end": v(-272.85, 79.06) * mm});
            skLineSegment(sketch, "E3444", {"start": v(-272.85, 79.06) * mm, "end": v(-272.29, 79) * mm});
            skLineSegment(sketch, "E3445", {"start": v(-272.29, 79) * mm, "end": v(-271.73, 78.91) * mm});
            skLineSegment(sketch, "E3446", {"start": v(-271.73, 78.91) * mm, "end": v(-271.2, 78.81) * mm});
            skLineSegment(sketch, "E3447", {"start": v(-271.2, 78.81) * mm, "end": v(-270.67, 78.7) * mm});
            skLineSegment(sketch, "E3448", {"start": v(-270.67, 78.7) * mm, "end": v(-270.17, 78.58) * mm});
            skLineSegment(sketch, "E3449", {"start": v(-270.17, 78.58) * mm, "end": v(-269.68, 78.44) * mm});
            skLineSegment(sketch, "E3450", {"start": v(-269.68, 78.44) * mm, "end": v(-269.21, 78.3) * mm});
            skLineSegment(sketch, "E3451", {"start": v(-269.21, 78.3) * mm, "end": v(-268.76, 78.13) * mm});
            skLineSegment(sketch, "E3452", {"start": v(-268.76, 78.13) * mm, "end": v(-268.32, 77.95) * mm});
            skLineSegment(sketch, "E3453", {"start": v(-268.32, 77.95) * mm, "end": v(-267.9, 77.77) * mm});
            skLineSegment(sketch, "E3454", {"start": v(-267.9, 77.77) * mm, "end": v(-267.5, 77.57) * mm});
            skLineSegment(sketch, "E3455", {"start": v(-267.5, 77.57) * mm, "end": v(-267.13, 77.35) * mm});
            skLineSegment(sketch, "E3456", {"start": v(-267.13, 77.35) * mm, "end": v(-266.77, 77.13) * mm});
            skLineSegment(sketch, "E3457", {"start": v(-266.77, 77.13) * mm, "end": v(-266.42, 76.9) * mm});
            skLineSegment(sketch, "E3458", {"start": v(-266.42, 76.9) * mm, "end": v(-266.1, 76.65) * mm});
            skLineSegment(sketch, "E3459", {"start": v(-266.1, 76.65) * mm, "end": v(-265.8, 76.39) * mm});
            skLineSegment(sketch, "E3460", {"start": v(-265.8, 76.39) * mm, "end": v(-265.5, 76.12) * mm});
            skLineSegment(sketch, "E3461", {"start": v(-265.5, 76.12) * mm, "end": v(-265.24, 75.84) * mm});
            skLineSegment(sketch, "E3462", {"start": v(-265.24, 75.84) * mm, "end": v(-265, 75.55) * mm});
            skLineSegment(sketch, "E3463", {"start": v(-265, 75.55) * mm, "end": v(-264.77, 75.25) * mm});
            skLineSegment(sketch, "E3464", {"start": v(-264.77, 75.25) * mm, "end": v(-264.56, 74.94) * mm});
            skLineSegment(sketch, "E3465", {"start": v(-264.56, 74.94) * mm, "end": v(-264.37, 74.61) * mm});
            skLineSegment(sketch, "E3466", {"start": v(-264.37, 74.61) * mm, "end": v(-264.2, 74.28) * mm});
            skLineSegment(sketch, "E3467", {"start": v(-264.2, 74.28) * mm, "end": v(-264.06, 73.94) * mm});
            skLineSegment(sketch, "E3468", {"start": v(-264.06, 73.94) * mm, "end": v(-263.93, 73.6) * mm});
            skLineSegment(sketch, "E3469", {"start": v(-263.93, 73.6) * mm, "end": v(-263.83, 73.23) * mm});
            skLineSegment(sketch, "E3470", {"start": v(-263.83, 73.23) * mm, "end": v(-263.74, 72.87) * mm});
            skLineSegment(sketch, "E3471", {"start": v(-263.74, 72.87) * mm, "end": v(-263.68, 72.49) * mm});
            skLineSegment(sketch, "E3472", {"start": v(-263.68, 72.49) * mm, "end": v(-263.64, 72.1) * mm});
            skLineSegment(sketch, "E3473", {"start": v(-263.64, 72.1) * mm, "end": v(-263.62, 71.7) * mm});
            skLineSegment(sketch, "E3474", {"start": v(-263.62, 71.7) * mm, "end": v(-263.62, 71.3) * mm});
            skLineSegment(sketch, "E3475", {"start": v(-263.62, 71.3) * mm, "end": v(-263.64, 70.9) * mm});
            skLineSegment(sketch, "E3476", {"start": v(-263.64, 70.9) * mm, "end": v(-263.7, 70.48) * mm});
            skLineSegment(sketch, "E3477", {"start": v(-263.7, 70.48) * mm, "end": v(-263.76, 70.06) * mm});
            skLineSegment(sketch, "E3478", {"start": v(-263.76, 70.06) * mm, "end": v(-263.84, 69.66) * mm});
            skLineSegment(sketch, "E3479", {"start": v(-263.84, 69.66) * mm, "end": v(-263.95, 69.27) * mm});
            skLineSegment(sketch, "E3480", {"start": v(-263.95, 69.27) * mm, "end": v(-264.07, 68.9) * mm});
            skLineSegment(sketch, "E3481", {"start": v(-264.07, 68.9) * mm, "end": v(-264.21, 68.54) * mm});
            skLineSegment(sketch, "E3482", {"start": v(-264.21, 68.54) * mm, "end": v(-264.37, 68.2) * mm});
            skLineSegment(sketch, "E3483", {"start": v(-264.37, 68.2) * mm, "end": v(-264.55, 67.86) * mm});
            skLineSegment(sketch, "E3484", {"start": v(-264.55, 67.86) * mm, "end": v(-264.75, 67.54) * mm});
            skLineSegment(sketch, "E3485", {"start": v(-264.75, 67.54) * mm, "end": v(-264.96, 67.24) * mm});
            skLineSegment(sketch, "E3486", {"start": v(-264.96, 67.24) * mm, "end": v(-265.2, 66.95) * mm});
            skLineSegment(sketch, "E3487", {"start": v(-265.2, 66.95) * mm, "end": v(-265.44, 66.67) * mm});
            skLineSegment(sketch, "E3488", {"start": v(-265.44, 66.67) * mm, "end": v(-265.7, 66.41) * mm});
            skLineSegment(sketch, "E3489", {"start": v(-265.7, 66.41) * mm, "end": v(-266, 66.17) * mm});
            skLineSegment(sketch, "E3490", {"start": v(-266, 66.17) * mm, "end": v(-266.3, 65.94) * mm});
            skLineSegment(sketch, "E3491", {"start": v(-266.3, 65.94) * mm, "end": v(-266.6, 65.72) * mm});
            skLineSegment(sketch, "E3492", {"start": v(-266.6, 65.72) * mm, "end": v(-266.94, 65.53) * mm});
            skLineSegment(sketch, "E3493", {"start": v(-266.94, 65.53) * mm, "end": v(-267.29, 65.34) * mm});
            skLineSegment(sketch, "E3494", {"start": v(-267.29, 65.34) * mm, "end": v(-267.65, 65.17) * mm});
            skLineSegment(sketch, "E3495", {"start": v(-267.65, 65.17) * mm, "end": v(-268.03, 65.02) * mm});
            skLineSegment(sketch, "E3496", {"start": v(-268.03, 65.02) * mm, "end": v(-268.42, 64.89) * mm});
            skLineSegment(sketch, "E3497", {"start": v(-268.42, 64.89) * mm, "end": v(-268.83, 64.77) * mm});
            skLineSegment(sketch, "E3498", {"start": v(-268.83, 64.77) * mm, "end": v(-269.25, 64.66) * mm});
            skLineSegment(sketch, "E3499", {"start": v(-269.25, 64.66) * mm, "end": v(-269.7, 64.58) * mm});
            skLineSegment(sketch, "E3500", {"start": v(-269.7, 64.58) * mm, "end": v(-270.14, 64.5) * mm});
            skLineSegment(sketch, "E3501", {"start": v(-270.14, 64.5) * mm, "end": v(-270.61, 64.45) * mm});
            skLineSegment(sketch, "E3502", {"start": v(-270.61, 64.45) * mm, "end": v(-271.1, 64.42) * mm});
            skLineSegment(sketch, "E3503", {"start": v(-271.1, 64.42) * mm, "end": v(-271.59, 64.4) * mm});
            skLineSegment(sketch, "E3504", {"start": v(-271.59, 64.4) * mm, "end": v(-272.1, 64.4) * mm});
            skLineSegment(sketch, "E3505", {"start": v(-272.1, 64.4) * mm, "end": v(-272.61, 64.4) * mm});
            skLineSegment(sketch, "E3506", {"start": v(-272.61, 64.4) * mm, "end": v(-273.15, 64.44) * mm});
            skLineSegment(sketch, "E3507", {"start": v(-273.15, 64.44) * mm, "end": v(-273.7, 64.5) * mm});
            skLineSegment(sketch, "E3508", {"start": v(-273.7, 64.5) * mm, "end": v(-274.26, 64.56) * mm});
            skLineSegment(sketch, "E3509", {"start": v(-275.94, 86.82) * mm, "end": v(-275.97, 86.6) * mm});
            skLineSegment(sketch, "E3510", {"start": v(-275.97, 86.6) * mm, "end": v(-273.5, 81.72) * mm});
            skLineSegment(sketch, "E3511", {"start": v(-273.5, 81.72) * mm, "end": v(-277.04, 82.2) * mm});
            skLineSegment(sketch, "E3512", {"start": v(-277.04, 82.2) * mm, "end": v(-279.64, 87.33) * mm});
            skLineSegment(sketch, "E3513", {"start": v(-279.64, 87.33) * mm, "end": v(-279.13, 91.12) * mm});
            skLineSegment(sketch, "E3514", {"start": v(-279.13, 91.12) * mm, "end": v(-260.95, 88.66) * mm});
            skLineSegment(sketch, "E3515", {"start": v(-260.95, 88.66) * mm, "end": v(-261.47, 84.86) * mm});
            skLineSegment(sketch, "E3516", {"start": v(-261.47, 84.86) * mm, "end": v(-275.94, 86.82) * mm});
            skLineSegment(sketch, "E3517", {"start": v(-30.88, -7.56) * mm, "end": v(-31.45, -7.67) * mm});
            skLineSegment(sketch, "E3518", {"start": v(-31.45, -7.67) * mm, "end": v(-32.01, -7.74) * mm});
            skLineSegment(sketch, "E3519", {"start": v(-32.01, -7.74) * mm, "end": v(-32.58, -7.79) * mm});
            skLineSegment(sketch, "E3520", {"start": v(-32.58, -7.79) * mm, "end": v(-33.14, -7.8) * mm});
            skLineSegment(sketch, "E3521", {"start": v(-33.14, -7.8) * mm, "end": v(-33.6, -7.8) * mm});
            skLineSegment(sketch, "E3522", {"start": v(-33.6, -7.8) * mm, "end": v(-34.06, -7.76) * mm});
            skLineSegment(sketch, "E3523", {"start": v(-34.06, -7.76) * mm, "end": v(-34.52, -7.71) * mm});
            skLineSegment(sketch, "E3524", {"start": v(-34.52, -7.71) * mm, "end": v(-34.97, -7.65) * mm});
            skLineSegment(sketch, "E3525", {"start": v(-34.97, -7.65) * mm, "end": v(-35.41, -7.56) * mm});
            skLineSegment(sketch, "E3526", {"start": v(-35.41, -7.56) * mm, "end": v(-35.85, -7.45) * mm});
            skLineSegment(sketch, "E3527", {"start": v(-35.85, -7.45) * mm, "end": v(-36.29, -7.33) * mm});
            skLineSegment(sketch, "E3528", {"start": v(-36.29, -7.33) * mm, "end": v(-36.72, -7.19) * mm});
            skLineSegment(sketch, "E3529", {"start": v(-36.72, -7.19) * mm, "end": v(-37.14, -7.03) * mm});
            skLineSegment(sketch, "E3530", {"start": v(-37.14, -7.03) * mm, "end": v(-37.55, -6.85) * mm});
            skLineSegment(sketch, "E3531", {"start": v(-37.55, -6.85) * mm, "end": v(-37.96, -6.66) * mm});
            skLineSegment(sketch, "E3532", {"start": v(-37.96, -6.66) * mm, "end": v(-38.35, -6.45) * mm});
            skLineSegment(sketch, "E3533", {"start": v(-38.35, -6.45) * mm, "end": v(-38.74, -6.22) * mm});
            skLineSegment(sketch, "E3534", {"start": v(-38.74, -6.22) * mm, "end": v(-39.12, -5.98) * mm});
            skLineSegment(sketch, "E3535", {"start": v(-39.12, -5.98) * mm, "end": v(-39.48, -5.72) * mm});
            skLineSegment(sketch, "E3536", {"start": v(-39.48, -5.72) * mm, "end": v(-39.84, -5.45) * mm});
            skLineSegment(sketch, "E3537", {"start": v(-39.84, -5.45) * mm, "end": v(-40.18, -5.16) * mm});
            skLineSegment(sketch, "E3538", {"start": v(-40.18, -5.16) * mm, "end": v(-40.52, -4.86) * mm});
            skLineSegment(sketch, "E3539", {"start": v(-40.52, -4.86) * mm, "end": v(-40.84, -4.54) * mm});
            skLineSegment(sketch, "E3540", {"start": v(-40.84, -4.54) * mm, "end": v(-41.14, -4.21) * mm});
            skLineSegment(sketch, "E3541", {"start": v(-41.14, -4.21) * mm, "end": v(-41.44, -3.87) * mm});
            skLineSegment(sketch, "E3542", {"start": v(-41.44, -3.87) * mm, "end": v(-41.72, -3.51) * mm});
            skLineSegment(sketch, "E3543", {"start": v(-41.72, -3.51) * mm, "end": v(-41.98, -3.15) * mm});
            skLineSegment(sketch, "E3544", {"start": v(-41.98, -3.15) * mm, "end": v(-42.23, -2.76) * mm});
            skLineSegment(sketch, "E3545", {"start": v(-42.23, -2.76) * mm, "end": v(-42.47, -2.37) * mm});
            skLineSegment(sketch, "E3546", {"start": v(-42.47, -2.37) * mm, "end": v(-42.69, -1.97) * mm});
            skLineSegment(sketch, "E3547", {"start": v(-42.69, -1.97) * mm, "end": v(-42.89, -1.55) * mm});
            skLineSegment(sketch, "E3548", {"start": v(-42.89, -1.55) * mm, "end": v(-43.07, -1.12) * mm});
            skLineSegment(sketch, "E3549", {"start": v(-43.07, -1.12) * mm, "end": v(-43.24, -0.69) * mm});
            skLineSegment(sketch, "E3550", {"start": v(-43.24, -0.69) * mm, "end": v(-43.39, -0.24) * mm});
            skLineSegment(sketch, "E3551", {"start": v(-43.39, -0.24) * mm, "end": v(-43.52, 0.22) * mm});
            skLineSegment(sketch, "E3552", {"start": v(-43.52, 0.22) * mm, "end": v(-43.63, 0.69) * mm});
            skLineSegment(sketch, "E3553", {"start": v(-43.63, 0.69) * mm, "end": v(-56.64, 61.39) * mm});
            skLineSegment(sketch, "E3554", {"start": v(-56.64, 61.39) * mm, "end": v(-99.83, 61.39) * mm});
            skLineSegment(sketch, "E3555", {"start": v(-99.83, 61.39) * mm, "end": v(-124.33, 36.59) * mm});
            skLineSegment(sketch, "E3556", {"start": v(-124.33, 36.59) * mm, "end": v(-127.19, -4.84) * mm});
            skLineSegment(sketch, "E3557", {"start": v(-127.19, -4.84) * mm, "end": v(-67.53, -21.99) * mm});
            skLineSegment(sketch, "E3558", {"start": v(-67.53, -21.99) * mm, "end": v(-67, -22.15) * mm});
            skLineSegment(sketch, "E3559", {"start": v(-67, -22.15) * mm, "end": v(-66.49, -22.34) * mm});
            skLineSegment(sketch, "E3560", {"start": v(-66.49, -22.34) * mm, "end": v(-65.99, -22.56) * mm});
            skLineSegment(sketch, "E3561", {"start": v(-65.99, -22.56) * mm, "end": v(-65.5, -22.8) * mm});
            skLineSegment(sketch, "E3562", {"start": v(-65.5, -22.8) * mm, "end": v(-65.04, -23.05) * mm});
            skLineSegment(sketch, "E3563", {"start": v(-65.04, -23.05) * mm, "end": v(-64.6, -23.33) * mm});
            skLineSegment(sketch, "E3564", {"start": v(-64.6, -23.33) * mm, "end": v(-64.16, -23.63) * mm});
            skLineSegment(sketch, "E3565", {"start": v(-64.16, -23.63) * mm, "end": v(-63.74, -23.95) * mm});
            skLineSegment(sketch, "E3566", {"start": v(-63.74, -23.95) * mm, "end": v(-63.34, -24.3) * mm});
            skLineSegment(sketch, "E3567", {"start": v(-63.34, -24.3) * mm, "end": v(-62.96, -24.65) * mm});
            skLineSegment(sketch, "E3568", {"start": v(-62.96, -24.65) * mm, "end": v(-62.6, -25.02) * mm});
            skLineSegment(sketch, "E3569", {"start": v(-62.6, -25.02) * mm, "end": v(-62.26, -25.4) * mm});
            skLineSegment(sketch, "E3570", {"start": v(-62.26, -25.4) * mm, "end": v(-61.94, -25.81) * mm});
            skLineSegment(sketch, "E3571", {"start": v(-61.94, -25.81) * mm, "end": v(-61.64, -26.23) * mm});
            skLineSegment(sketch, "E3572", {"start": v(-61.64, -26.23) * mm, "end": v(-61.36, -26.66) * mm});
            skLineSegment(sketch, "E3573", {"start": v(-61.36, -26.66) * mm, "end": v(-61.1, -27.1) * mm});
            skLineSegment(sketch, "E3574", {"start": v(-61.1, -27.1) * mm, "end": v(-60.86, -27.57) * mm});
            skLineSegment(sketch, "E3575", {"start": v(-60.86, -27.57) * mm, "end": v(-60.64, -28.03) * mm});
            skLineSegment(sketch, "E3576", {"start": v(-60.64, -28.03) * mm, "end": v(-60.45, -28.51) * mm});
            skLineSegment(sketch, "E3577", {"start": v(-60.45, -28.51) * mm, "end": v(-60.28, -29) * mm});
            skLineSegment(sketch, "E3578", {"start": v(-60.28, -29) * mm, "end": v(-60.13, -29.5) * mm});
            skLineSegment(sketch, "E3579", {"start": v(-60.13, -29.5) * mm, "end": v(-60, -30) * mm});
            skLineSegment(sketch, "E3580", {"start": v(-60, -30) * mm, "end": v(-59.9, -30.51) * mm});
            skLineSegment(sketch, "E3581", {"start": v(-59.9, -30.51) * mm, "end": v(-59.83, -31.03) * mm});
            skLineSegment(sketch, "E3582", {"start": v(-59.83, -31.03) * mm, "end": v(-59.78, -31.55) * mm});
            skLineSegment(sketch, "E3583", {"start": v(-59.78, -31.55) * mm, "end": v(-59.75, -32.07) * mm});
            skLineSegment(sketch, "E3584", {"start": v(-59.75, -32.07) * mm, "end": v(-59.75, -32.6) * mm});
            skLineSegment(sketch, "E3585", {"start": v(-59.75, -32.6) * mm, "end": v(-59.78, -33.14) * mm});
            skLineSegment(sketch, "E3586", {"start": v(-59.78, -33.14) * mm, "end": v(-59.84, -33.67) * mm});
            skLineSegment(sketch, "E3587", {"start": v(-59.84, -33.67) * mm, "end": v(-59.92, -34.2) * mm});
            skLineSegment(sketch, "E3588", {"start": v(-59.92, -34.2) * mm, "end": v(-60.03, -34.74) * mm});
            skLineSegment(sketch, "E3589", {"start": v(-60.03, -34.74) * mm, "end": v(-60.17, -35.28) * mm});
            skLineSegment(sketch, "E3590", {"start": v(-60.17, -35.28) * mm, "end": v(-60.3, -35.71) * mm});
            skLineSegment(sketch, "E3591", {"start": v(-60.3, -35.71) * mm, "end": v(-60.46, -36.14) * mm});
            skLineSegment(sketch, "E3592", {"start": v(-60.46, -36.14) * mm, "end": v(-60.63, -36.56) * mm});
            skLineSegment(sketch, "E3593", {"start": v(-60.63, -36.56) * mm, "end": v(-60.81, -36.96) * mm});
            skLineSegment(sketch, "E3594", {"start": v(-60.81, -36.96) * mm, "end": v(-61.01, -37.36) * mm});
            skLineSegment(sketch, "E3595", {"start": v(-61.01, -37.36) * mm, "end": v(-61.23, -37.74) * mm});
            skLineSegment(sketch, "E3596", {"start": v(-61.23, -37.74) * mm, "end": v(-61.45, -38.12) * mm});
            skLineSegment(sketch, "E3597", {"start": v(-61.45, -38.12) * mm, "end": v(-61.7, -38.48) * mm});
            skLineSegment(sketch, "E3598", {"start": v(-61.7, -38.48) * mm, "end": v(-61.95, -38.83) * mm});
            skLineSegment(sketch, "E3599", {"start": v(-61.95, -38.83) * mm, "end": v(-62.22, -39.17) * mm});
            skLineSegment(sketch, "E3600", {"start": v(-62.22, -39.17) * mm, "end": v(-62.5, -39.5) * mm});
            skLineSegment(sketch, "E3601", {"start": v(-62.5, -39.5) * mm, "end": v(-62.8, -39.8) * mm});
            skLineSegment(sketch, "E3602", {"start": v(-62.8, -39.8) * mm, "end": v(-63.1, -40.1) * mm});
            skLineSegment(sketch, "E3603", {"start": v(-63.1, -40.1) * mm, "end": v(-63.42, -40.4) * mm});
            skLineSegment(sketch, "E3604", {"start": v(-63.42, -40.4) * mm, "end": v(-63.75, -40.67) * mm});
            skLineSegment(sketch, "E3605", {"start": v(-63.75, -40.67) * mm, "end": v(-64.09, -40.93) * mm});
            skLineSegment(sketch, "E3606", {"start": v(-64.09, -40.93) * mm, "end": v(-64.43, -41.18) * mm});
            skLineSegment(sketch, "E3607", {"start": v(-64.43, -41.18) * mm, "end": v(-64.8, -41.41) * mm});
            skLineSegment(sketch, "E3608", {"start": v(-64.8, -41.41) * mm, "end": v(-65.16, -41.63) * mm});
            skLineSegment(sketch, "E3609", {"start": v(-65.16, -41.63) * mm, "end": v(-65.53, -41.84) * mm});
            skLineSegment(sketch, "E3610", {"start": v(-65.53, -41.84) * mm, "end": v(-65.91, -42.02) * mm});
            skLineSegment(sketch, "E3611", {"start": v(-65.91, -42.02) * mm, "end": v(-66.3, -42.2) * mm});
            skLineSegment(sketch, "E3612", {"start": v(-66.3, -42.2) * mm, "end": v(-66.7, -42.36) * mm});
            skLineSegment(sketch, "E3613", {"start": v(-66.7, -42.36) * mm, "end": v(-67.1, -42.5) * mm});
            skLineSegment(sketch, "E3614", {"start": v(-67.1, -42.5) * mm, "end": v(-67.5, -42.63) * mm});
            skLineSegment(sketch, "E3615", {"start": v(-67.5, -42.63) * mm, "end": v(-67.92, -42.74) * mm});
            skLineSegment(sketch, "E3616", {"start": v(-67.92, -42.74) * mm, "end": v(-68.34, -42.83) * mm});
            skLineSegment(sketch, "E3617", {"start": v(-68.34, -42.83) * mm, "end": v(-68.76, -42.91) * mm});
            skLineSegment(sketch, "E3618", {"start": v(-68.76, -42.91) * mm, "end": v(-69.19, -42.97) * mm});
            skLineSegment(sketch, "E3619", {"start": v(-69.19, -42.97) * mm, "end": v(-69.62, -43.02) * mm});
            skLineSegment(sketch, "E3620", {"start": v(-69.62, -43.02) * mm, "end": v(-70.05, -43.05) * mm});
            skLineSegment(sketch, "E3621", {"start": v(-70.05, -43.05) * mm, "end": v(-70.49, -43.05) * mm});
            skLineSegment(sketch, "E3622", {"start": v(-70.49, -43.05) * mm, "end": v(-71.23, -43.03) * mm});
            skLineSegment(sketch, "E3623", {"start": v(-71.23, -43.03) * mm, "end": v(-71.97, -42.95) * mm});
            skLineSegment(sketch, "E3624", {"start": v(-71.97, -42.95) * mm, "end": v(-72.72, -42.82) * mm});
            skLineSegment(sketch, "E3625", {"start": v(-72.72, -42.82) * mm, "end": v(-73.46, -42.63) * mm});
            skLineSegment(sketch, "E3626", {"start": v(-73.46, -42.63) * mm, "end": v(-141.47, -23.08) * mm});
            skLineSegment(sketch, "E3627", {"start": v(-141.47, -23.08) * mm, "end": v(-141.92, -22.94) * mm});
            skLineSegment(sketch, "E3628", {"start": v(-141.92, -22.94) * mm, "end": v(-142.36, -22.79) * mm});
            skLineSegment(sketch, "E3629", {"start": v(-142.36, -22.79) * mm, "end": v(-142.79, -22.6) * mm});
            skLineSegment(sketch, "E3630", {"start": v(-142.79, -22.6) * mm, "end": v(-143.21, -22.41) * mm});
            skLineSegment(sketch, "E3631", {"start": v(-143.21, -22.41) * mm, "end": v(-143.62, -22.2) * mm});
            skLineSegment(sketch, "E3632", {"start": v(-143.62, -22.2) * mm, "end": v(-144.02, -21.98) * mm});
            skLineSegment(sketch, "E3633", {"start": v(-144.02, -21.98) * mm, "end": v(-144.4, -21.73) * mm});
            skLineSegment(sketch, "E3634", {"start": v(-144.4, -21.73) * mm, "end": v(-144.78, -21.48) * mm});
            skLineSegment(sketch, "E3635", {"start": v(-144.78, -21.48) * mm, "end": v(-145.14, -21.2) * mm});
            skLineSegment(sketch, "E3636", {"start": v(-145.14, -21.2) * mm, "end": v(-145.5, -20.92) * mm});
            skLineSegment(sketch, "E3637", {"start": v(-145.5, -20.92) * mm, "end": v(-145.83, -20.62) * mm});
            skLineSegment(sketch, "E3638", {"start": v(-145.83, -20.62) * mm, "end": v(-146.15, -20.3) * mm});
            skLineSegment(sketch, "E3639", {"start": v(-146.15, -20.3) * mm, "end": v(-146.46, -19.97) * mm});
            skLineSegment(sketch, "E3640", {"start": v(-146.46, -19.97) * mm, "end": v(-146.75, -19.64) * mm});
            skLineSegment(sketch, "E3641", {"start": v(-146.75, -19.64) * mm, "end": v(-147.03, -19.29) * mm});
            skLineSegment(sketch, "E3642", {"start": v(-147.03, -19.29) * mm, "end": v(-147.3, -18.92) * mm});
            skLineSegment(sketch, "E3643", {"start": v(-147.3, -18.92) * mm, "end": v(-147.55, -18.55) * mm});
            skLineSegment(sketch, "E3644", {"start": v(-147.55, -18.55) * mm, "end": v(-147.78, -18.17) * mm});
            skLineSegment(sketch, "E3645", {"start": v(-147.78, -18.17) * mm, "end": v(-148, -17.78) * mm});
            skLineSegment(sketch, "E3646", {"start": v(-148, -17.78) * mm, "end": v(-148.2, -17.37) * mm});
            skLineSegment(sketch, "E3647", {"start": v(-148.2, -17.37) * mm, "end": v(-148.38, -16.96) * mm});
            skLineSegment(sketch, "E3648", {"start": v(-148.38, -16.96) * mm, "end": v(-148.55, -16.54) * mm});
            skLineSegment(sketch, "E3649", {"start": v(-148.55, -16.54) * mm, "end": v(-148.7, -16.12) * mm});
            skLineSegment(sketch, "E3650", {"start": v(-148.7, -16.12) * mm, "end": v(-148.83, -15.69) * mm});
            skLineSegment(sketch, "E3651", {"start": v(-148.83, -15.69) * mm, "end": v(-148.95, -15.24) * mm});
            skLineSegment(sketch, "E3652", {"start": v(-148.95, -15.24) * mm, "end": v(-149.05, -14.8) * mm});
            skLineSegment(sketch, "E3653", {"start": v(-149.05, -14.8) * mm, "end": v(-149.12, -14.35) * mm});
            skLineSegment(sketch, "E3654", {"start": v(-149.12, -14.35) * mm, "end": v(-149.18, -13.89) * mm});
            skLineSegment(sketch, "E3655", {"start": v(-149.18, -13.89) * mm, "end": v(-149.22, -13.43) * mm});
            skLineSegment(sketch, "E3656", {"start": v(-149.22, -13.43) * mm, "end": v(-149.24, -12.96) * mm});
            skLineSegment(sketch, "E3657", {"start": v(-149.24, -12.96) * mm, "end": v(-149.24, -12.5) * mm});
            skLineSegment(sketch, "E3658", {"start": v(-149.24, -12.5) * mm, "end": v(-149.21, -12.02) * mm});
            skLineSegment(sketch, "E3659", {"start": v(-149.21, -12.02) * mm, "end": v(-146.17, 32.14) * mm});
            skLineSegment(sketch, "E3660", {"start": v(-146.17, 32.14) * mm, "end": v(-166.35, 52.07) * mm});
            skLineSegment(sketch, "E3661", {"start": v(-166.35, 52.07) * mm, "end": v(-166.66, 52.4) * mm});
            skLineSegment(sketch, "E3662", {"start": v(-166.66, 52.4) * mm, "end": v(-166.95, 52.76) * mm});
            skLineSegment(sketch, "E3663", {"start": v(-166.95, 52.76) * mm, "end": v(-167.2, 53.13) * mm});
            skLineSegment(sketch, "E3664", {"start": v(-167.2, 53.13) * mm, "end": v(-167.43, 53.52) * mm});
            skLineSegment(sketch, "E3665", {"start": v(-167.43, 53.52) * mm, "end": v(-167.63, 53.92) * mm});
            skLineSegment(sketch, "E3666", {"start": v(-167.63, 53.92) * mm, "end": v(-167.8, 54.33) * mm});
            skLineSegment(sketch, "E3667", {"start": v(-167.8, 54.33) * mm, "end": v(-167.93, 54.75) * mm});
            skLineSegment(sketch, "E3668", {"start": v(-167.93, 54.75) * mm, "end": v(-168.04, 55.18) * mm});
            skLineSegment(sketch, "E3669", {"start": v(-168.04, 55.18) * mm, "end": v(-168.12, 55.61) * mm});
            skLineSegment(sketch, "E3670", {"start": v(-168.12, 55.61) * mm, "end": v(-168.16, 56.05) * mm});
            skLineSegment(sketch, "E3671", {"start": v(-168.16, 56.05) * mm, "end": v(-168.17, 56.5) * mm});
            skLineSegment(sketch, "E3672", {"start": v(-168.17, 56.5) * mm, "end": v(-168.15, 56.94) * mm});
            skLineSegment(sketch, "E3673", {"start": v(-168.15, 56.94) * mm, "end": v(-168.1, 57.39) * mm});
            skLineSegment(sketch, "E3674", {"start": v(-168.1, 57.39) * mm, "end": v(-168, 57.83) * mm});
            skLineSegment(sketch, "E3675", {"start": v(-168, 57.83) * mm, "end": v(-167.89, 58.27) * mm});
            skLineSegment(sketch, "E3676", {"start": v(-167.89, 58.27) * mm, "end": v(-167.74, 58.7) * mm});
            skLineSegment(sketch, "E3677", {"start": v(-167.74, 58.7) * mm, "end": v(-164.22, 67.53) * mm});
            skLineSegment(sketch, "E3678", {"start": v(-164.22, 67.53) * mm, "end": v(-164, 68.02) * mm});
            skLineSegment(sketch, "E3679", {"start": v(-164, 68.02) * mm, "end": v(-163.73, 68.48) * mm});
            skLineSegment(sketch, "E3680", {"start": v(-163.73, 68.48) * mm, "end": v(-163.42, 68.92) * mm});
            skLineSegment(sketch, "E3681", {"start": v(-163.42, 68.92) * mm, "end": v(-163.07, 69.34) * mm});
            skLineSegment(sketch, "E3682", {"start": v(-163.07, 69.34) * mm, "end": v(-201.05, 106.85) * mm});
            skLineSegment(sketch, "E3683", {"start": v(-201.05, 106.85) * mm, "end": v(-199.9, 107.51) * mm});
            skLineSegment(sketch, "E3684", {"start": v(-199.9, 107.51) * mm, "end": v(-198.75, 108.2) * mm});
            skLineSegment(sketch, "E3685", {"start": v(-198.75, 108.2) * mm, "end": v(-197.62, 108.9) * mm});
            skLineSegment(sketch, "E3686", {"start": v(-197.62, 108.9) * mm, "end": v(-196.51, 109.62) * mm});
            skLineSegment(sketch, "E3687", {"start": v(-196.51, 109.62) * mm, "end": v(-195.41, 110.37) * mm});
            skLineSegment(sketch, "E3688", {"start": v(-195.41, 110.37) * mm, "end": v(-194.33, 111.13) * mm});
            skLineSegment(sketch, "E3689", {"start": v(-194.33, 111.13) * mm, "end": v(-193.27, 111.92) * mm});
            skLineSegment(sketch, "E3690", {"start": v(-193.27, 111.92) * mm, "end": v(-192.22, 112.73) * mm});
            skLineSegment(sketch, "E3691", {"start": v(-192.22, 112.73) * mm, "end": v(-191.19, 113.56) * mm});
            skLineSegment(sketch, "E3692", {"start": v(-191.19, 113.56) * mm, "end": v(-190.17, 114.4) * mm});
            skLineSegment(sketch, "E3693", {"start": v(-190.17, 114.4) * mm, "end": v(-189.18, 115.27) * mm});
            skLineSegment(sketch, "E3694", {"start": v(-189.18, 115.27) * mm, "end": v(-188.2, 116.16) * mm});
            skLineSegment(sketch, "E3695", {"start": v(-188.2, 116.16) * mm, "end": v(-187.23, 117.07) * mm});
            skLineSegment(sketch, "E3696", {"start": v(-187.23, 117.07) * mm, "end": v(-186.29, 118) * mm});
            skLineSegment(sketch, "E3697", {"start": v(-186.29, 118) * mm, "end": v(-185.36, 118.94) * mm});
            skLineSegment(sketch, "E3698", {"start": v(-185.36, 118.94) * mm, "end": v(-184.46, 119.9) * mm});
            skLineSegment(sketch, "E3699", {"start": v(-184.46, 119.9) * mm, "end": v(-183.57, 120.88) * mm});
            skLineSegment(sketch, "E3700", {"start": v(-183.57, 120.88) * mm, "end": v(-182.7, 121.88) * mm});
            skLineSegment(sketch, "E3701", {"start": v(-182.7, 121.88) * mm, "end": v(-181.85, 122.9) * mm});
            skLineSegment(sketch, "E3702", {"start": v(-181.85, 122.9) * mm, "end": v(-181.02, 123.92) * mm});
            skLineSegment(sketch, "E3703", {"start": v(-181.02, 123.92) * mm, "end": v(-180.21, 124.97) * mm});
            skLineSegment(sketch, "E3704", {"start": v(-180.21, 124.97) * mm, "end": v(-179.42, 126.04) * mm});
            skLineSegment(sketch, "E3705", {"start": v(-179.42, 126.04) * mm, "end": v(-178.66, 127.12) * mm});
            skLineSegment(sketch, "E3706", {"start": v(-178.66, 127.12) * mm, "end": v(-177.91, 128.21) * mm});
            skLineSegment(sketch, "E3707", {"start": v(-177.91, 128.21) * mm, "end": v(-177.19, 129.32) * mm});
            skLineSegment(sketch, "E3708", {"start": v(-177.19, 129.32) * mm, "end": v(-176.48, 130.45) * mm});
            skLineSegment(sketch, "E3709", {"start": v(-176.48, 130.45) * mm, "end": v(-175.8, 131.6) * mm});
            skLineSegment(sketch, "E3710", {"start": v(-175.8, 131.6) * mm, "end": v(-175.14, 132.75) * mm});
            skLineSegment(sketch, "E3711", {"start": v(-175.14, 132.75) * mm, "end": v(-174.5, 133.92) * mm});
            skLineSegment(sketch, "E3712", {"start": v(-174.5, 133.92) * mm, "end": v(-173.89, 135.1) * mm});
            skLineSegment(sketch, "E3713", {"start": v(-173.89, 135.1) * mm, "end": v(-173.3, 136.3) * mm});
            skLineSegment(sketch, "E3714", {"start": v(-173.3, 136.3) * mm, "end": v(-172.73, 137.52) * mm});
            skLineSegment(sketch, "E3715", {"start": v(-172.73, 137.52) * mm, "end": v(-171.23, 139.03) * mm});
            skLineSegment(sketch, "E3716", {"start": v(-171.23, 139.03) * mm, "end": v(-132.3, 100.57) * mm});
            skLineSegment(sketch, "E3717", {"start": v(-132.3, 100.57) * mm, "end": v(-132, 100.75) * mm});
            skLineSegment(sketch, "E3718", {"start": v(-132, 100.75) * mm, "end": v(-131.7, 100.9) * mm});
            skLineSegment(sketch, "E3719", {"start": v(-131.7, 100.9) * mm, "end": v(-131.4, 101.04) * mm});
            skLineSegment(sketch, "E3720", {"start": v(-131.4, 101.04) * mm, "end": v(-131.07, 101.17) * mm});
            skLineSegment(sketch, "E3721", {"start": v(-131.07, 101.17) * mm, "end": v(-123.16, 103.96) * mm});
            skLineSegment(sketch, "E3722", {"start": v(-123.16, 103.96) * mm, "end": v(-122.75, 104.09) * mm});
            skLineSegment(sketch, "E3723", {"start": v(-122.75, 104.09) * mm, "end": v(-122.32, 104.18) * mm});
            skLineSegment(sketch, "E3724", {"start": v(-122.32, 104.18) * mm, "end": v(-121.9, 104.25) * mm});
            skLineSegment(sketch, "E3725", {"start": v(-121.9, 104.25) * mm, "end": v(-121.47, 104.3) * mm});
            skLineSegment(sketch, "E3726", {"start": v(-121.47, 104.3) * mm, "end": v(-121.05, 104.3) * mm});
            skLineSegment(sketch, "E3727", {"start": v(-121.05, 104.3) * mm, "end": v(-120.63, 104.28) * mm});
            skLineSegment(sketch, "E3728", {"start": v(-120.63, 104.28) * mm, "end": v(-120.2, 104.23) * mm});
            skLineSegment(sketch, "E3729", {"start": v(-120.2, 104.23) * mm, "end": v(-119.79, 104.15) * mm});
            skLineSegment(sketch, "E3730", {"start": v(-119.79, 104.15) * mm, "end": v(-119.38, 104.05) * mm});
            skLineSegment(sketch, "E3731", {"start": v(-119.38, 104.05) * mm, "end": v(-118.98, 103.91) * mm});
            skLineSegment(sketch, "E3732", {"start": v(-118.98, 103.91) * mm, "end": v(-118.59, 103.75) * mm});
            skLineSegment(sketch, "E3733", {"start": v(-118.59, 103.75) * mm, "end": v(-118.2, 103.56) * mm});
            skLineSegment(sketch, "E3734", {"start": v(-118.2, 103.56) * mm, "end": v(-117.84, 103.34) * mm});
            skLineSegment(sketch, "E3735", {"start": v(-117.84, 103.34) * mm, "end": v(-117.48, 103.1) * mm});
            skLineSegment(sketch, "E3736", {"start": v(-117.48, 103.1) * mm, "end": v(-117.15, 102.83) * mm});
            skLineSegment(sketch, "E3737", {"start": v(-117.15, 102.83) * mm, "end": v(-116.82, 102.53) * mm});
            skLineSegment(sketch, "E3738", {"start": v(-116.82, 102.53) * mm, "end": v(-96.92, 82.87) * mm});
            skLineSegment(sketch, "E3739", {"start": v(-96.92, 82.87) * mm, "end": v(-47.95, 82.87) * mm});
            skLineSegment(sketch, "E3740", {"start": v(-47.95, 82.87) * mm, "end": v(-47.48, 82.86) * mm});
            skLineSegment(sketch, "E3741", {"start": v(-47.48, 82.86) * mm, "end": v(-47.01, 82.83) * mm});
            skLineSegment(sketch, "E3742", {"start": v(-47.01, 82.83) * mm, "end": v(-46.55, 82.78) * mm});
            skLineSegment(sketch, "E3743", {"start": v(-46.55, 82.78) * mm, "end": v(-46.09, 82.7) * mm});
            skLineSegment(sketch, "E3744", {"start": v(-46.09, 82.7) * mm, "end": v(-45.64, 82.62) * mm});
            skLineSegment(sketch, "E3745", {"start": v(-45.64, 82.62) * mm, "end": v(-45.2, 82.5) * mm});
            skLineSegment(sketch, "E3746", {"start": v(-45.2, 82.5) * mm, "end": v(-44.75, 82.38) * mm});
            skLineSegment(sketch, "E3747", {"start": v(-44.75, 82.38) * mm, "end": v(-44.32, 82.24) * mm});
            skLineSegment(sketch, "E3748", {"start": v(-44.32, 82.24) * mm, "end": v(-43.9, 82.07) * mm});
            skLineSegment(sketch, "E3749", {"start": v(-43.9, 82.07) * mm, "end": v(-43.49, 81.9) * mm});
            skLineSegment(sketch, "E3750", {"start": v(-43.49, 81.9) * mm, "end": v(-43.08, 81.7) * mm});
            skLineSegment(sketch, "E3751", {"start": v(-43.08, 81.7) * mm, "end": v(-42.68, 81.49) * mm});
            skLineSegment(sketch, "E3752", {"start": v(-42.68, 81.49) * mm, "end": v(-42.3, 81.26) * mm});
            skLineSegment(sketch, "E3753", {"start": v(-42.3, 81.26) * mm, "end": v(-41.92, 81.01) * mm});
            skLineSegment(sketch, "E3754", {"start": v(-41.92, 81.01) * mm, "end": v(-41.55, 80.75) * mm});
            skLineSegment(sketch, "E3755", {"start": v(-41.55, 80.75) * mm, "end": v(-41.2, 80.48) * mm});
            skLineSegment(sketch, "E3756", {"start": v(-41.2, 80.48) * mm, "end": v(-40.86, 80.2) * mm});
            skLineSegment(sketch, "E3757", {"start": v(-40.86, 80.2) * mm, "end": v(-40.53, 79.89) * mm});
            skLineSegment(sketch, "E3758", {"start": v(-40.53, 79.89) * mm, "end": v(-40.2, 79.57) * mm});
            skLineSegment(sketch, "E3759", {"start": v(-40.2, 79.57) * mm, "end": v(-39.9, 79.24) * mm});
            skLineSegment(sketch, "E3760", {"start": v(-39.9, 79.24) * mm, "end": v(-39.61, 78.9) * mm});
            skLineSegment(sketch, "E3761", {"start": v(-39.61, 78.9) * mm, "end": v(-39.34, 78.54) * mm});
            skLineSegment(sketch, "E3762", {"start": v(-39.34, 78.54) * mm, "end": v(-39.07, 78.17) * mm});
            skLineSegment(sketch, "E3763", {"start": v(-39.07, 78.17) * mm, "end": v(-38.83, 77.8) * mm});
            skLineSegment(sketch, "E3764", {"start": v(-38.83, 77.8) * mm, "end": v(-38.6, 77.4) * mm});
            skLineSegment(sketch, "E3765", {"start": v(-38.6, 77.4) * mm, "end": v(-38.38, 77) * mm});
            skLineSegment(sketch, "E3766", {"start": v(-38.38, 77) * mm, "end": v(-38.18, 76.59) * mm});
            skLineSegment(sketch, "E3767", {"start": v(-38.18, 76.59) * mm, "end": v(-38, 76.16) * mm});
            skLineSegment(sketch, "E3768", {"start": v(-38, 76.16) * mm, "end": v(-37.83, 75.73) * mm});
            skLineSegment(sketch, "E3769", {"start": v(-37.83, 75.73) * mm, "end": v(-37.69, 75.29) * mm});
            skLineSegment(sketch, "E3770", {"start": v(-37.69, 75.29) * mm, "end": v(-37.56, 74.84) * mm});
            skLineSegment(sketch, "E3771", {"start": v(-37.56, 74.84) * mm, "end": v(-37.45, 74.38) * mm});
            skLineSegment(sketch, "E3772", {"start": v(-37.45, 74.38) * mm, "end": v(-22.63, 5.2) * mm});
            skLineSegment(sketch, "E3773", {"start": v(-22.63, 5.2) * mm, "end": v(-22.52, 4.65) * mm});
            skLineSegment(sketch, "E3774", {"start": v(-22.52, 4.65) * mm, "end": v(-22.45, 4.1) * mm});
            skLineSegment(sketch, "E3775", {"start": v(-22.45, 4.1) * mm, "end": v(-22.4, 3.57) * mm});
            skLineSegment(sketch, "E3776", {"start": v(-22.4, 3.57) * mm, "end": v(-22.39, 3.03) * mm});
            skLineSegment(sketch, "E3777", {"start": v(-22.39, 3.03) * mm, "end": v(-22.4, 2.5) * mm});
            skLineSegment(sketch, "E3778", {"start": v(-22.4, 2.5) * mm, "end": v(-22.43, 1.97) * mm});
            skLineSegment(sketch, "E3779", {"start": v(-22.43, 1.97) * mm, "end": v(-22.49, 1.44) * mm});
            skLineSegment(sketch, "E3780", {"start": v(-22.49, 1.44) * mm, "end": v(-22.58, 0.93) * mm});
            skLineSegment(sketch, "E3781", {"start": v(-22.58, 0.93) * mm, "end": v(-22.69, 0.42) * mm});
            skLineSegment(sketch, "E3782", {"start": v(-22.69, 0.42) * mm, "end": v(-22.82, -0.09) * mm});
            skLineSegment(sketch, "E3783", {"start": v(-22.82, -0.09) * mm, "end": v(-22.98, -0.58) * mm});
            skLineSegment(sketch, "E3784", {"start": v(-22.98, -0.58) * mm, "end": v(-23.16, -1.07) * mm});
            skLineSegment(sketch, "E3785", {"start": v(-23.16, -1.07) * mm, "end": v(-23.37, -1.54) * mm});
            skLineSegment(sketch, "E3786", {"start": v(-23.37, -1.54) * mm, "end": v(-23.6, -2) * mm});
            skLineSegment(sketch, "E3787", {"start": v(-23.6, -2) * mm, "end": v(-23.84, -2.46) * mm});
            skLineSegment(sketch, "E3788", {"start": v(-23.84, -2.46) * mm, "end": v(-24.11, -2.9) * mm});
            skLineSegment(sketch, "E3789", {"start": v(-24.11, -2.9) * mm, "end": v(-24.4, -3.32) * mm});
            skLineSegment(sketch, "E3790", {"start": v(-24.4, -3.32) * mm, "end": v(-24.71, -3.73) * mm});
            skLineSegment(sketch, "E3791", {"start": v(-24.71, -3.73) * mm, "end": v(-25.04, -4.13) * mm});
            skLineSegment(sketch, "E3792", {"start": v(-25.04, -4.13) * mm, "end": v(-25.39, -4.51) * mm});
            skLineSegment(sketch, "E3793", {"start": v(-25.39, -4.51) * mm, "end": v(-25.76, -4.88) * mm});
            skLineSegment(sketch, "E3794", {"start": v(-25.76, -4.88) * mm, "end": v(-26.14, -5.22) * mm});
            skLineSegment(sketch, "E3795", {"start": v(-26.14, -5.22) * mm, "end": v(-26.55, -5.55) * mm});
            skLineSegment(sketch, "E3796", {"start": v(-26.55, -5.55) * mm, "end": v(-26.97, -5.86) * mm});
            skLineSegment(sketch, "E3797", {"start": v(-26.97, -5.86) * mm, "end": v(-27.4, -6.15) * mm});
            skLineSegment(sketch, "E3798", {"start": v(-27.4, -6.15) * mm, "end": v(-27.86, -6.42) * mm});
            skLineSegment(sketch, "E3799", {"start": v(-27.86, -6.42) * mm, "end": v(-28.32, -6.67) * mm});
            skLineSegment(sketch, "E3800", {"start": v(-28.32, -6.67) * mm, "end": v(-28.8, -6.9) * mm});
            skLineSegment(sketch, "E3801", {"start": v(-28.8, -6.9) * mm, "end": v(-29.3, -7.1) * mm});
            skLineSegment(sketch, "E3802", {"start": v(-29.3, -7.1) * mm, "end": v(-29.82, -7.28) * mm});
            skLineSegment(sketch, "E3803", {"start": v(-29.82, -7.28) * mm, "end": v(-30.34, -7.43) * mm});
            skLineSegment(sketch, "E3804", {"start": v(-30.34, -7.43) * mm, "end": v(-30.88, -7.56) * mm});
            skLineSegment(sketch, "E3805", {"start": v(-235.61, 117.96) * mm, "end": v(-236.87, 117.98) * mm});
            skLineSegment(sketch, "E3806", {"start": v(-236.87, 117.98) * mm, "end": v(-238.11, 118.02) * mm});
            skLineSegment(sketch, "E3807", {"start": v(-238.11, 118.02) * mm, "end": v(-239.35, 118.1) * mm});
            skLineSegment(sketch, "E3808", {"start": v(-239.35, 118.1) * mm, "end": v(-240.58, 118.21) * mm});
            skLineSegment(sketch, "E3809", {"start": v(-240.58, 118.21) * mm, "end": v(-241.8, 118.35) * mm});
            skLineSegment(sketch, "E3810", {"start": v(-241.8, 118.35) * mm, "end": v(-243.02, 118.52) * mm});
            skLineSegment(sketch, "E3811", {"start": v(-243.02, 118.52) * mm, "end": v(-244.22, 118.72) * mm});
            skLineSegment(sketch, "E3812", {"start": v(-244.22, 118.72) * mm, "end": v(-245.4, 118.95) * mm});
            skLineSegment(sketch, "E3813", {"start": v(-245.4, 118.95) * mm, "end": v(-246.6, 119.2) * mm});
            skLineSegment(sketch, "E3814", {"start": v(-246.6, 119.2) * mm, "end": v(-247.76, 119.5) * mm});
            skLineSegment(sketch, "E3815", {"start": v(-247.76, 119.5) * mm, "end": v(-248.92, 119.8) * mm});
            skLineSegment(sketch, "E3816", {"start": v(-248.92, 119.8) * mm, "end": v(-250.07, 120.15) * mm});
            skLineSegment(sketch, "E3817", {"start": v(-250.07, 120.15) * mm, "end": v(-251.2, 120.52) * mm});
            skLineSegment(sketch, "E3818", {"start": v(-251.2, 120.52) * mm, "end": v(-252.33, 120.92) * mm});
            skLineSegment(sketch, "E3819", {"start": v(-252.33, 120.92) * mm, "end": v(-253.44, 121.34) * mm});
            skLineSegment(sketch, "E3820", {"start": v(-253.44, 121.34) * mm, "end": v(-254.54, 121.8) * mm});
            skLineSegment(sketch, "E3821", {"start": v(-254.54, 121.8) * mm, "end": v(-255.62, 122.27) * mm});
            skLineSegment(sketch, "E3822", {"start": v(-255.62, 122.27) * mm, "end": v(-256.7, 122.77) * mm});
            skLineSegment(sketch, "E3823", {"start": v(-256.7, 122.77) * mm, "end": v(-257.75, 123.3) * mm});
            skLineSegment(sketch, "E3824", {"start": v(-257.75, 123.3) * mm, "end": v(-258.8, 123.84) * mm});
            skLineSegment(sketch, "E3825", {"start": v(-258.8, 123.84) * mm, "end": v(-259.82, 124.42) * mm});
            skLineSegment(sketch, "E3826", {"start": v(-259.82, 124.42) * mm, "end": v(-260.83, 125.02) * mm});
            skLineSegment(sketch, "E3827", {"start": v(-260.83, 125.02) * mm, "end": v(-261.83, 125.64) * mm});
            skLineSegment(sketch, "E3828", {"start": v(-261.83, 125.64) * mm, "end": v(-262.8, 126.28) * mm});
            skLineSegment(sketch, "E3829", {"start": v(-262.8, 126.28) * mm, "end": v(-263.77, 126.95) * mm});
            skLineSegment(sketch, "E3830", {"start": v(-263.77, 126.95) * mm, "end": v(-264.71, 127.64) * mm});
            skLineSegment(sketch, "E3831", {"start": v(-264.71, 127.64) * mm, "end": v(-265.64, 128.35) * mm});
            skLineSegment(sketch, "E3832", {"start": v(-265.64, 128.35) * mm, "end": v(-266.55, 129.09) * mm});
            skLineSegment(sketch, "E3833", {"start": v(-266.55, 129.09) * mm, "end": v(-267.44, 129.84) * mm});
            skLineSegment(sketch, "E3834", {"start": v(-267.44, 129.84) * mm, "end": v(-268.32, 130.62) * mm});
            skLineSegment(sketch, "E3835", {"start": v(-268.32, 130.62) * mm, "end": v(-269.17, 131.42) * mm});
            skLineSegment(sketch, "E3836", {"start": v(-269.17, 131.42) * mm, "end": v(-270, 132.23) * mm});
            skLineSegment(sketch, "E3837", {"start": v(-270, 132.23) * mm, "end": v(-270.83, 133.07) * mm});
            skLineSegment(sketch, "E3838", {"start": v(-270.83, 133.07) * mm, "end": v(-271.62, 133.92) * mm});
            skLineSegment(sketch, "E3839", {"start": v(-271.62, 133.92) * mm, "end": v(-272.4, 134.8) * mm});
            skLineSegment(sketch, "E3840", {"start": v(-272.4, 134.8) * mm, "end": v(-273.15, 135.69) * mm});
            skLineSegment(sketch, "E3841", {"start": v(-273.15, 135.69) * mm, "end": v(-273.89, 136.6) * mm});
            skLineSegment(sketch, "E3842", {"start": v(-273.89, 136.6) * mm, "end": v(-274.6, 137.53) * mm});
            skLineSegment(sketch, "E3843", {"start": v(-274.6, 137.53) * mm, "end": v(-275.29, 138.47) * mm});
            skLineSegment(sketch, "E3844", {"start": v(-275.29, 138.47) * mm, "end": v(-275.96, 139.44) * mm});
            skLineSegment(sketch, "E3845", {"start": v(-275.96, 139.44) * mm, "end": v(-276.6, 140.42) * mm});
            skLineSegment(sketch, "E3846", {"start": v(-276.6, 140.42) * mm, "end": v(-277.22, 141.41) * mm});
            skLineSegment(sketch, "E3847", {"start": v(-277.22, 141.41) * mm, "end": v(-277.82, 142.42) * mm});
            skLineSegment(sketch, "E3848", {"start": v(-277.82, 142.42) * mm, "end": v(-278.4, 143.45) * mm});
            skLineSegment(sketch, "E3849", {"start": v(-278.4, 143.45) * mm, "end": v(-278.95, 144.5) * mm});
            skLineSegment(sketch, "E3850", {"start": v(-278.95, 144.5) * mm, "end": v(-279.47, 145.55) * mm});
            skLineSegment(sketch, "E3851", {"start": v(-279.47, 145.55) * mm, "end": v(-279.97, 146.62) * mm});
            skLineSegment(sketch, "E3852", {"start": v(-279.97, 146.62) * mm, "end": v(-280.45, 147.7) * mm});
            skLineSegment(sketch, "E3853", {"start": v(-280.45, 147.7) * mm, "end": v(-280.9, 148.8) * mm});
            skLineSegment(sketch, "E3854", {"start": v(-280.9, 148.8) * mm, "end": v(-281.32, 149.91) * mm});
            skLineSegment(sketch, "E3855", {"start": v(-281.32, 149.91) * mm, "end": v(-281.72, 151.04) * mm});
            skLineSegment(sketch, "E3856", {"start": v(-281.72, 151.04) * mm, "end": v(-282.09, 152.17) * mm});
            skLineSegment(sketch, "E3857", {"start": v(-282.09, 152.17) * mm, "end": v(-282.43, 153.32) * mm});
            skLineSegment(sketch, "E3858", {"start": v(-282.43, 153.32) * mm, "end": v(-282.75, 154.48) * mm});
            skLineSegment(sketch, "E3859", {"start": v(-282.75, 154.48) * mm, "end": v(-283.03, 155.65) * mm});
            skLineSegment(sketch, "E3860", {"start": v(-283.03, 155.65) * mm, "end": v(-283.3, 156.83) * mm});
            skLineSegment(sketch, "E3861", {"start": v(-283.3, 156.83) * mm, "end": v(-283.52, 158.02) * mm});
            skLineSegment(sketch, "E3862", {"start": v(-283.52, 158.02) * mm, "end": v(-283.72, 159.23) * mm});
            skLineSegment(sketch, "E3863", {"start": v(-283.72, 159.23) * mm, "end": v(-283.89, 160.44) * mm});
            skLineSegment(sketch, "E3864", {"start": v(-283.89, 160.44) * mm, "end": v(-284.03, 161.66) * mm});
            skLineSegment(sketch, "E3865", {"start": v(-284.03, 161.66) * mm, "end": v(-284.14, 162.89) * mm});
            skLineSegment(sketch, "E3866", {"start": v(-284.14, 162.89) * mm, "end": v(-284.22, 164.13) * mm});
            skLineSegment(sketch, "E3867", {"start": v(-284.22, 164.13) * mm, "end": v(-284.26, 165.37) * mm});
            skLineSegment(sketch, "E3868", {"start": v(-284.26, 165.37) * mm, "end": v(-284.28, 166.63) * mm});
            skLineSegment(sketch, "E3869", {"start": v(-284.28, 166.63) * mm, "end": v(-284.26, 167.88) * mm});
            skLineSegment(sketch, "E3870", {"start": v(-284.26, 167.88) * mm, "end": v(-284.22, 169.13) * mm});
            skLineSegment(sketch, "E3871", {"start": v(-284.22, 169.13) * mm, "end": v(-284.14, 170.37) * mm});
            skLineSegment(sketch, "E3872", {"start": v(-284.14, 170.37) * mm, "end": v(-284.03, 171.6) * mm});
            skLineSegment(sketch, "E3873", {"start": v(-284.03, 171.6) * mm, "end": v(-283.89, 172.82) * mm});
            skLineSegment(sketch, "E3874", {"start": v(-283.89, 172.82) * mm, "end": v(-283.72, 174.03) * mm});
            skLineSegment(sketch, "E3875", {"start": v(-283.72, 174.03) * mm, "end": v(-283.52, 175.23) * mm});
            skLineSegment(sketch, "E3876", {"start": v(-283.52, 175.23) * mm, "end": v(-283.3, 176.42) * mm});
            skLineSegment(sketch, "E3877", {"start": v(-283.3, 176.42) * mm, "end": v(-283.03, 177.6) * mm});
            skLineSegment(sketch, "E3878", {"start": v(-283.03, 177.6) * mm, "end": v(-282.75, 178.78) * mm});
            skLineSegment(sketch, "E3879", {"start": v(-282.75, 178.78) * mm, "end": v(-282.43, 179.94) * mm});
            skLineSegment(sketch, "E3880", {"start": v(-282.43, 179.94) * mm, "end": v(-282.09, 181.08) * mm});
            skLineSegment(sketch, "E3881", {"start": v(-282.09, 181.08) * mm, "end": v(-281.72, 182.22) * mm});
            skLineSegment(sketch, "E3882", {"start": v(-281.72, 182.22) * mm, "end": v(-281.32, 183.34) * mm});
            skLineSegment(sketch, "E3883", {"start": v(-281.32, 183.34) * mm, "end": v(-280.9, 184.45) * mm});
            skLineSegment(sketch, "E3884", {"start": v(-280.9, 184.45) * mm, "end": v(-280.45, 185.55) * mm});
            skLineSegment(sketch, "E3885", {"start": v(-280.45, 185.55) * mm, "end": v(-279.97, 186.64) * mm});
            skLineSegment(sketch, "E3886", {"start": v(-279.97, 186.64) * mm, "end": v(-279.47, 187.7) * mm});
            skLineSegment(sketch, "E3887", {"start": v(-279.47, 187.7) * mm, "end": v(-278.95, 188.76) * mm});
            skLineSegment(sketch, "E3888", {"start": v(-278.95, 188.76) * mm, "end": v(-278.4, 189.8) * mm});
            skLineSegment(sketch, "E3889", {"start": v(-278.4, 189.8) * mm, "end": v(-277.82, 190.83) * mm});
            skLineSegment(sketch, "E3890", {"start": v(-277.82, 190.83) * mm, "end": v(-277.22, 191.84) * mm});
            skLineSegment(sketch, "E3891", {"start": v(-277.22, 191.84) * mm, "end": v(-276.6, 192.84) * mm});
            skLineSegment(sketch, "E3892", {"start": v(-276.6, 192.84) * mm, "end": v(-275.96, 193.82) * mm});
            skLineSegment(sketch, "E3893", {"start": v(-275.96, 193.82) * mm, "end": v(-275.29, 194.78) * mm});
            skLineSegment(sketch, "E3894", {"start": v(-275.29, 194.78) * mm, "end": v(-274.6, 195.73) * mm});
            skLineSegment(sketch, "E3895", {"start": v(-274.6, 195.73) * mm, "end": v(-273.89, 196.66) * mm});
            skLineSegment(sketch, "E3896", {"start": v(-273.89, 196.66) * mm, "end": v(-273.15, 197.57) * mm});
            skLineSegment(sketch, "E3897", {"start": v(-273.15, 197.57) * mm, "end": v(-272.4, 198.46) * mm});
            skLineSegment(sketch, "E3898", {"start": v(-272.4, 198.46) * mm, "end": v(-271.62, 199.33) * mm});
            skLineSegment(sketch, "E3899", {"start": v(-271.62, 199.33) * mm, "end": v(-270.83, 200.19) * mm});
            skLineSegment(sketch, "E3900", {"start": v(-270.83, 200.19) * mm, "end": v(-270, 201.02) * mm});
            skLineSegment(sketch, "E3901", {"start": v(-270, 201.02) * mm, "end": v(-269.17, 201.84) * mm});
            skLineSegment(sketch, "E3902", {"start": v(-269.17, 201.84) * mm, "end": v(-268.32, 202.64) * mm});
            skLineSegment(sketch, "E3903", {"start": v(-268.32, 202.64) * mm, "end": v(-267.44, 203.41) * mm});
            skLineSegment(sketch, "E3904", {"start": v(-267.44, 203.41) * mm, "end": v(-266.55, 204.17) * mm});
            skLineSegment(sketch, "E3905", {"start": v(-266.55, 204.17) * mm, "end": v(-265.64, 204.9) * mm});
            skLineSegment(sketch, "E3906", {"start": v(-265.64, 204.9) * mm, "end": v(-264.71, 205.61) * mm});
            skLineSegment(sketch, "E3907", {"start": v(-264.71, 205.61) * mm, "end": v(-263.77, 206.3) * mm});
            skLineSegment(sketch, "E3908", {"start": v(-263.77, 206.3) * mm, "end": v(-262.8, 206.97) * mm});
            skLineSegment(sketch, "E3909", {"start": v(-262.8, 206.97) * mm, "end": v(-261.83, 207.62) * mm});
            skLineSegment(sketch, "E3910", {"start": v(-261.83, 207.62) * mm, "end": v(-260.83, 208.24) * mm});
            skLineSegment(sketch, "E3911", {"start": v(-260.83, 208.24) * mm, "end": v(-259.82, 208.84) * mm});
            skLineSegment(sketch, "E3912", {"start": v(-259.82, 208.84) * mm, "end": v(-258.8, 209.41) * mm});
            skLineSegment(sketch, "E3913", {"start": v(-258.8, 209.41) * mm, "end": v(-257.75, 209.96) * mm});
            skLineSegment(sketch, "E3914", {"start": v(-257.75, 209.96) * mm, "end": v(-256.7, 210.49) * mm});
            skLineSegment(sketch, "E3915", {"start": v(-256.7, 210.49) * mm, "end": v(-255.62, 210.99) * mm});
            skLineSegment(sketch, "E3916", {"start": v(-255.62, 210.99) * mm, "end": v(-254.54, 211.46) * mm});
            skLineSegment(sketch, "E3917", {"start": v(-254.54, 211.46) * mm, "end": v(-253.44, 211.91) * mm});
            skLineSegment(sketch, "E3918", {"start": v(-253.44, 211.91) * mm, "end": v(-252.33, 212.34) * mm});
            skLineSegment(sketch, "E3919", {"start": v(-252.33, 212.34) * mm, "end": v(-251.2, 212.73) * mm});
            skLineSegment(sketch, "E3920", {"start": v(-251.2, 212.73) * mm, "end": v(-250.07, 213.1) * mm});
            skLineSegment(sketch, "E3921", {"start": v(-250.07, 213.1) * mm, "end": v(-248.92, 213.45) * mm});
            skLineSegment(sketch, "E3922", {"start": v(-248.92, 213.45) * mm, "end": v(-247.76, 213.76) * mm});
            skLineSegment(sketch, "E3923", {"start": v(-247.76, 213.76) * mm, "end": v(-246.6, 214.05) * mm});
            skLineSegment(sketch, "E3924", {"start": v(-246.6, 214.05) * mm, "end": v(-245.4, 214.3) * mm});
            skLineSegment(sketch, "E3925", {"start": v(-245.4, 214.3) * mm, "end": v(-244.22, 214.53) * mm});
            skLineSegment(sketch, "E3926", {"start": v(-244.22, 214.53) * mm, "end": v(-243.02, 214.73) * mm});
            skLineSegment(sketch, "E3927", {"start": v(-243.02, 214.73) * mm, "end": v(-241.8, 214.9) * mm});
            skLineSegment(sketch, "E3928", {"start": v(-241.8, 214.9) * mm, "end": v(-240.58, 215.04) * mm});
            skLineSegment(sketch, "E3929", {"start": v(-240.58, 215.04) * mm, "end": v(-239.35, 215.15) * mm});
            skLineSegment(sketch, "E3930", {"start": v(-239.35, 215.15) * mm, "end": v(-238.11, 215.23) * mm});
            skLineSegment(sketch, "E3931", {"start": v(-238.11, 215.23) * mm, "end": v(-236.87, 215.28) * mm});
            skLineSegment(sketch, "E3932", {"start": v(-236.87, 215.28) * mm, "end": v(-235.61, 215.3) * mm});
            skLineSegment(sketch, "E3933", {"start": v(-235.61, 215.3) * mm, "end": v(-234.36, 215.28) * mm});
            skLineSegment(sketch, "E3934", {"start": v(-234.36, 215.28) * mm, "end": v(-233.11, 215.23) * mm});
            skLineSegment(sketch, "E3935", {"start": v(-233.11, 215.23) * mm, "end": v(-231.87, 215.15) * mm});
            skLineSegment(sketch, "E3936", {"start": v(-231.87, 215.15) * mm, "end": v(-230.64, 215.04) * mm});
            skLineSegment(sketch, "E3937", {"start": v(-230.64, 215.04) * mm, "end": v(-229.42, 214.9) * mm});
            skLineSegment(sketch, "E3938", {"start": v(-229.42, 214.9) * mm, "end": v(-228.21, 214.73) * mm});
            skLineSegment(sketch, "E3939", {"start": v(-228.21, 214.73) * mm, "end": v(-227, 214.53) * mm});
            skLineSegment(sketch, "E3940", {"start": v(-227, 214.53) * mm, "end": v(-225.82, 214.3) * mm});
            skLineSegment(sketch, "E3941", {"start": v(-225.82, 214.3) * mm, "end": v(-224.64, 214.05) * mm});
            skLineSegment(sketch, "E3942", {"start": v(-224.64, 214.05) * mm, "end": v(-223.47, 213.76) * mm});
            skLineSegment(sketch, "E3943", {"start": v(-223.47, 213.76) * mm, "end": v(-222.3, 213.45) * mm});
            skLineSegment(sketch, "E3944", {"start": v(-222.3, 213.45) * mm, "end": v(-221.16, 213.1) * mm});
            skLineSegment(sketch, "E3945", {"start": v(-221.16, 213.1) * mm, "end": v(-220.02, 212.73) * mm});
            skLineSegment(sketch, "E3946", {"start": v(-220.02, 212.73) * mm, "end": v(-218.9, 212.34) * mm});
            skLineSegment(sketch, "E3947", {"start": v(-218.9, 212.34) * mm, "end": v(-217.79, 211.91) * mm});
            skLineSegment(sketch, "E3948", {"start": v(-217.79, 211.91) * mm, "end": v(-216.69, 211.46) * mm});
            skLineSegment(sketch, "E3949", {"start": v(-216.69, 211.46) * mm, "end": v(-215.6, 210.99) * mm});
            skLineSegment(sketch, "E3950", {"start": v(-215.6, 210.99) * mm, "end": v(-214.53, 210.49) * mm});
            skLineSegment(sketch, "E3951", {"start": v(-214.53, 210.49) * mm, "end": v(-213.48, 209.96) * mm});
            skLineSegment(sketch, "E3952", {"start": v(-213.48, 209.96) * mm, "end": v(-212.43, 209.41) * mm});
            skLineSegment(sketch, "E3953", {"start": v(-212.43, 209.41) * mm, "end": v(-211.4, 208.84) * mm});
            skLineSegment(sketch, "E3954", {"start": v(-211.4, 208.84) * mm, "end": v(-210.4, 208.24) * mm});
            skLineSegment(sketch, "E3955", {"start": v(-210.4, 208.24) * mm, "end": v(-209.4, 207.62) * mm});
            skLineSegment(sketch, "E3956", {"start": v(-209.4, 207.62) * mm, "end": v(-208.42, 206.97) * mm});
            skLineSegment(sketch, "E3957", {"start": v(-208.42, 206.97) * mm, "end": v(-207.46, 206.3) * mm});
            skLineSegment(sketch, "E3958", {"start": v(-207.46, 206.3) * mm, "end": v(-206.51, 205.61) * mm});
            skLineSegment(sketch, "E3959", {"start": v(-206.51, 205.61) * mm, "end": v(-205.59, 204.9) * mm});
            skLineSegment(sketch, "E3960", {"start": v(-205.59, 204.9) * mm, "end": v(-204.67, 204.17) * mm});
            skLineSegment(sketch, "E3961", {"start": v(-204.67, 204.17) * mm, "end": v(-203.78, 203.41) * mm});
            skLineSegment(sketch, "E3962", {"start": v(-203.78, 203.41) * mm, "end": v(-202.9, 202.64) * mm});
            skLineSegment(sketch, "E3963", {"start": v(-202.9, 202.64) * mm, "end": v(-202.05, 201.84) * mm});
            skLineSegment(sketch, "E3964", {"start": v(-202.05, 201.84) * mm, "end": v(-201.22, 201.02) * mm});
            skLineSegment(sketch, "E3965", {"start": v(-201.22, 201.02) * mm, "end": v(-200.4, 200.19) * mm});
            skLineSegment(sketch, "E3966", {"start": v(-200.4, 200.19) * mm, "end": v(-199.6, 199.33) * mm});
            skLineSegment(sketch, "E3967", {"start": v(-199.6, 199.33) * mm, "end": v(-198.83, 198.46) * mm});
            skLineSegment(sketch, "E3968", {"start": v(-198.83, 198.46) * mm, "end": v(-198.07, 197.57) * mm});
            skLineSegment(sketch, "E3969", {"start": v(-198.07, 197.57) * mm, "end": v(-197.34, 196.66) * mm});
            skLineSegment(sketch, "E3970", {"start": v(-197.34, 196.66) * mm, "end": v(-196.63, 195.73) * mm});
            skLineSegment(sketch, "E3971", {"start": v(-196.63, 195.73) * mm, "end": v(-195.94, 194.78) * mm});
            skLineSegment(sketch, "E3972", {"start": v(-195.94, 194.78) * mm, "end": v(-195.27, 193.82) * mm});
            skLineSegment(sketch, "E3973", {"start": v(-195.27, 193.82) * mm, "end": v(-194.62, 192.84) * mm});
            skLineSegment(sketch, "E3974", {"start": v(-194.62, 192.84) * mm, "end": v(-194, 191.84) * mm});
            skLineSegment(sketch, "E3975", {"start": v(-194, 191.84) * mm, "end": v(-193.4, 190.83) * mm});
            skLineSegment(sketch, "E3976", {"start": v(-193.4, 190.83) * mm, "end": v(-192.83, 189.8) * mm});
            skLineSegment(sketch, "E3977", {"start": v(-192.83, 189.8) * mm, "end": v(-192.28, 188.76) * mm});
            skLineSegment(sketch, "E3978", {"start": v(-192.28, 188.76) * mm, "end": v(-191.75, 187.7) * mm});
            skLineSegment(sketch, "E3979", {"start": v(-191.75, 187.7) * mm, "end": v(-191.25, 186.64) * mm});
            skLineSegment(sketch, "E3980", {"start": v(-191.25, 186.64) * mm, "end": v(-190.78, 185.55) * mm});
            skLineSegment(sketch, "E3981", {"start": v(-190.78, 185.55) * mm, "end": v(-190.33, 184.45) * mm});
            skLineSegment(sketch, "E3982", {"start": v(-190.33, 184.45) * mm, "end": v(-189.9, 183.34) * mm});
            skLineSegment(sketch, "E3983", {"start": v(-189.9, 183.34) * mm, "end": v(-189.5, 182.22) * mm});
            skLineSegment(sketch, "E3984", {"start": v(-189.5, 182.22) * mm, "end": v(-189.14, 181.08) * mm});
            skLineSegment(sketch, "E3985", {"start": v(-189.14, 181.08) * mm, "end": v(-188.8, 179.94) * mm});
            skLineSegment(sketch, "E3986", {"start": v(-188.8, 179.94) * mm, "end": v(-188.48, 178.78) * mm});
            skLineSegment(sketch, "E3987", {"start": v(-188.48, 178.78) * mm, "end": v(-188.2, 177.6) * mm});
            skLineSegment(sketch, "E3988", {"start": v(-188.2, 177.6) * mm, "end": v(-187.94, 176.42) * mm});
            skLineSegment(sketch, "E3989", {"start": v(-187.94, 176.42) * mm, "end": v(-187.7, 175.23) * mm});
            skLineSegment(sketch, "E3990", {"start": v(-187.7, 175.23) * mm, "end": v(-187.5, 174.03) * mm});
            skLineSegment(sketch, "E3991", {"start": v(-187.5, 174.03) * mm, "end": v(-187.34, 172.82) * mm});
            skLineSegment(sketch, "E3992", {"start": v(-187.34, 172.82) * mm, "end": v(-187.2, 171.6) * mm});
            skLineSegment(sketch, "E3993", {"start": v(-187.2, 171.6) * mm, "end": v(-187.09, 170.37) * mm});
            skLineSegment(sketch, "E3994", {"start": v(-187.09, 170.37) * mm, "end": v(-187.01, 169.13) * mm});
            skLineSegment(sketch, "E3995", {"start": v(-187.01, 169.13) * mm, "end": v(-186.96, 167.88) * mm});
            skLineSegment(sketch, "E3996", {"start": v(-186.96, 167.88) * mm, "end": v(-186.95, 166.63) * mm});
            skLineSegment(sketch, "E3997", {"start": v(-186.95, 166.63) * mm, "end": v(-186.96, 165.37) * mm});
            skLineSegment(sketch, "E3998", {"start": v(-186.96, 165.37) * mm, "end": v(-187.01, 164.13) * mm});
            skLineSegment(sketch, "E3999", {"start": v(-187.01, 164.13) * mm, "end": v(-187.09, 162.89) * mm});
            skLineSegment(sketch, "E4000", {"start": v(-187.09, 162.89) * mm, "end": v(-187.2, 161.66) * mm});
            skLineSegment(sketch, "E4001", {"start": v(-187.2, 161.66) * mm, "end": v(-187.34, 160.44) * mm});
            skLineSegment(sketch, "E4002", {"start": v(-187.34, 160.44) * mm, "end": v(-187.5, 159.23) * mm});
            skLineSegment(sketch, "E4003", {"start": v(-187.5, 159.23) * mm, "end": v(-187.7, 158.02) * mm});
            skLineSegment(sketch, "E4004", {"start": v(-187.7, 158.02) * mm, "end": v(-187.94, 156.83) * mm});
            skLineSegment(sketch, "E4005", {"start": v(-187.94, 156.83) * mm, "end": v(-188.2, 155.65) * mm});
            skLineSegment(sketch, "E4006", {"start": v(-188.2, 155.65) * mm, "end": v(-188.48, 154.48) * mm});
            skLineSegment(sketch, "E4007", {"start": v(-188.48, 154.48) * mm, "end": v(-188.8, 153.32) * mm});
            skLineSegment(sketch, "E4008", {"start": v(-188.8, 153.32) * mm, "end": v(-189.14, 152.17) * mm});
            skLineSegment(sketch, "E4009", {"start": v(-189.14, 152.17) * mm, "end": v(-189.5, 151.04) * mm});
            skLineSegment(sketch, "E4010", {"start": v(-189.5, 151.04) * mm, "end": v(-189.9, 149.91) * mm});
            skLineSegment(sketch, "E4011", {"start": v(-189.9, 149.91) * mm, "end": v(-190.33, 148.8) * mm});
            skLineSegment(sketch, "E4012", {"start": v(-190.33, 148.8) * mm, "end": v(-190.78, 147.7) * mm});
            skLineSegment(sketch, "E4013", {"start": v(-190.78, 147.7) * mm, "end": v(-191.25, 146.62) * mm});
            skLineSegment(sketch, "E4014", {"start": v(-191.25, 146.62) * mm, "end": v(-191.75, 145.55) * mm});
            skLineSegment(sketch, "E4015", {"start": v(-191.75, 145.55) * mm, "end": v(-192.28, 144.5) * mm});
            skLineSegment(sketch, "E4016", {"start": v(-192.28, 144.5) * mm, "end": v(-192.83, 143.45) * mm});
            skLineSegment(sketch, "E4017", {"start": v(-192.83, 143.45) * mm, "end": v(-193.4, 142.42) * mm});
            skLineSegment(sketch, "E4018", {"start": v(-193.4, 142.42) * mm, "end": v(-194, 141.41) * mm});
            skLineSegment(sketch, "E4019", {"start": v(-194, 141.41) * mm, "end": v(-194.62, 140.42) * mm});
            skLineSegment(sketch, "E4020", {"start": v(-194.62, 140.42) * mm, "end": v(-195.27, 139.44) * mm});
            skLineSegment(sketch, "E4021", {"start": v(-195.27, 139.44) * mm, "end": v(-195.94, 138.47) * mm});
            skLineSegment(sketch, "E4022", {"start": v(-195.94, 138.47) * mm, "end": v(-196.63, 137.53) * mm});
            skLineSegment(sketch, "E4023", {"start": v(-196.63, 137.53) * mm, "end": v(-197.34, 136.6) * mm});
            skLineSegment(sketch, "E4024", {"start": v(-197.34, 136.6) * mm, "end": v(-198.07, 135.69) * mm});
            skLineSegment(sketch, "E4025", {"start": v(-198.07, 135.69) * mm, "end": v(-198.83, 134.8) * mm});
            skLineSegment(sketch, "E4026", {"start": v(-198.83, 134.8) * mm, "end": v(-199.6, 133.92) * mm});
            skLineSegment(sketch, "E4027", {"start": v(-199.6, 133.92) * mm, "end": v(-200.4, 133.07) * mm});
            skLineSegment(sketch, "E4028", {"start": v(-200.4, 133.07) * mm, "end": v(-201.22, 132.23) * mm});
            skLineSegment(sketch, "E4029", {"start": v(-201.22, 132.23) * mm, "end": v(-202.05, 131.42) * mm});
            skLineSegment(sketch, "E4030", {"start": v(-202.05, 131.42) * mm, "end": v(-202.9, 130.62) * mm});
            skLineSegment(sketch, "E4031", {"start": v(-202.9, 130.62) * mm, "end": v(-203.78, 129.84) * mm});
            skLineSegment(sketch, "E4032", {"start": v(-203.78, 129.84) * mm, "end": v(-204.67, 129.09) * mm});
            skLineSegment(sketch, "E4033", {"start": v(-204.67, 129.09) * mm, "end": v(-205.59, 128.35) * mm});
            skLineSegment(sketch, "E4034", {"start": v(-205.59, 128.35) * mm, "end": v(-206.51, 127.64) * mm});
            skLineSegment(sketch, "E4035", {"start": v(-206.51, 127.64) * mm, "end": v(-207.46, 126.95) * mm});
            skLineSegment(sketch, "E4036", {"start": v(-207.46, 126.95) * mm, "end": v(-208.42, 126.28) * mm});
            skLineSegment(sketch, "E4037", {"start": v(-208.42, 126.28) * mm, "end": v(-209.4, 125.64) * mm});
            skLineSegment(sketch, "E4038", {"start": v(-209.4, 125.64) * mm, "end": v(-210.4, 125.02) * mm});
            skLineSegment(sketch, "E4039", {"start": v(-210.4, 125.02) * mm, "end": v(-211.4, 124.42) * mm});
            skLineSegment(sketch, "E4040", {"start": v(-211.4, 124.42) * mm, "end": v(-212.43, 123.84) * mm});
            skLineSegment(sketch, "E4041", {"start": v(-212.43, 123.84) * mm, "end": v(-213.48, 123.3) * mm});
            skLineSegment(sketch, "E4042", {"start": v(-213.48, 123.3) * mm, "end": v(-214.53, 122.77) * mm});
            skLineSegment(sketch, "E4043", {"start": v(-214.53, 122.77) * mm, "end": v(-215.6, 122.27) * mm});
            skLineSegment(sketch, "E4044", {"start": v(-215.6, 122.27) * mm, "end": v(-216.69, 121.8) * mm});
            skLineSegment(sketch, "E4045", {"start": v(-216.69, 121.8) * mm, "end": v(-217.79, 121.34) * mm});
            skLineSegment(sketch, "E4046", {"start": v(-217.79, 121.34) * mm, "end": v(-218.9, 120.92) * mm});
            skLineSegment(sketch, "E4047", {"start": v(-218.9, 120.92) * mm, "end": v(-220.02, 120.52) * mm});
            skLineSegment(sketch, "E4048", {"start": v(-220.02, 120.52) * mm, "end": v(-221.16, 120.15) * mm});
            skLineSegment(sketch, "E4049", {"start": v(-221.16, 120.15) * mm, "end": v(-222.3, 119.8) * mm});
            skLineSegment(sketch, "E4050", {"start": v(-222.3, 119.8) * mm, "end": v(-223.47, 119.5) * mm});
            skLineSegment(sketch, "E4051", {"start": v(-223.47, 119.5) * mm, "end": v(-224.64, 119.2) * mm});
            skLineSegment(sketch, "E4052", {"start": v(-224.64, 119.2) * mm, "end": v(-225.82, 118.95) * mm});
            skLineSegment(sketch, "E4053", {"start": v(-225.82, 118.95) * mm, "end": v(-227, 118.72) * mm});
            skLineSegment(sketch, "E4054", {"start": v(-227, 118.72) * mm, "end": v(-228.21, 118.52) * mm});
            skLineSegment(sketch, "E4055", {"start": v(-228.21, 118.52) * mm, "end": v(-229.42, 118.35) * mm});
            skLineSegment(sketch, "E4056", {"start": v(-229.42, 118.35) * mm, "end": v(-230.64, 118.21) * mm});
            skLineSegment(sketch, "E4057", {"start": v(-230.64, 118.21) * mm, "end": v(-231.87, 118.1) * mm});
            skLineSegment(sketch, "E4058", {"start": v(-231.87, 118.1) * mm, "end": v(-233.11, 118.02) * mm});
            skLineSegment(sketch, "E4059", {"start": v(-233.11, 118.02) * mm, "end": v(-234.36, 117.98) * mm});
            skLineSegment(sketch, "E4060", {"start": v(-234.36, 117.98) * mm, "end": v(-235.61, 117.96) * mm});
            skLineSegment(sketch, "E4061", {"start": v(-245, 1.99) * mm, "end": v(-246.16, 3.2) * mm});
            skLineSegment(sketch, "E4062", {"start": v(-246.16, 3.2) * mm, "end": v(-247.35, 4.4) * mm});
            skLineSegment(sketch, "E4063", {"start": v(-247.35, 4.4) * mm, "end": v(-248.57, 5.56) * mm});
            skLineSegment(sketch, "E4064", {"start": v(-248.57, 5.56) * mm, "end": v(-249.81, 6.7) * mm});
            skLineSegment(sketch, "E4065", {"start": v(-249.81, 6.7) * mm, "end": v(-251.09, 7.8) * mm});
            skLineSegment(sketch, "E4066", {"start": v(-251.09, 7.8) * mm, "end": v(-252.39, 8.86) * mm});
            skLineSegment(sketch, "E4067", {"start": v(-252.39, 8.86) * mm, "end": v(-253.72, 9.9) * mm});
            skLineSegment(sketch, "E4068", {"start": v(-253.72, 9.9) * mm, "end": v(-255.07, 10.9) * mm});
            skLineSegment(sketch, "E4069", {"start": v(-255.07, 10.9) * mm, "end": v(-256.45, 11.86) * mm});
            skLineSegment(sketch, "E4070", {"start": v(-256.45, 11.86) * mm, "end": v(-257.86, 12.8) * mm});
            skLineSegment(sketch, "E4071", {"start": v(-257.86, 12.8) * mm, "end": v(-259.3, 13.7) * mm});
            skLineSegment(sketch, "E4072", {"start": v(-259.3, 13.7) * mm, "end": v(-260.75, 14.56) * mm});
            skLineSegment(sketch, "E4073", {"start": v(-260.75, 14.56) * mm, "end": v(-262.22, 15.38) * mm});
            skLineSegment(sketch, "E4074", {"start": v(-262.22, 15.38) * mm, "end": v(-263.72, 16.18) * mm});
            skLineSegment(sketch, "E4075", {"start": v(-263.72, 16.18) * mm, "end": v(-265.25, 16.93) * mm});
            skLineSegment(sketch, "E4076", {"start": v(-265.25, 16.93) * mm, "end": v(-266.8, 17.64) * mm});
            skLineSegment(sketch, "E4077", {"start": v(-266.8, 17.64) * mm, "end": v(-268.36, 18.32) * mm});
            skLineSegment(sketch, "E4078", {"start": v(-268.36, 18.32) * mm, "end": v(-269.94, 18.96) * mm});
            skLineSegment(sketch, "E4079", {"start": v(-269.94, 18.96) * mm, "end": v(-271.55, 19.55) * mm});
            skLineSegment(sketch, "E4080", {"start": v(-271.55, 19.55) * mm, "end": v(-273.18, 20.11) * mm});
            skLineSegment(sketch, "E4081", {"start": v(-273.18, 20.11) * mm, "end": v(-274.82, 20.63) * mm});
            skLineSegment(sketch, "E4082", {"start": v(-274.82, 20.63) * mm, "end": v(-276.48, 21.1) * mm});
            skLineSegment(sketch, "E4083", {"start": v(-276.48, 21.1) * mm, "end": v(-278.16, 21.53) * mm});
            skLineSegment(sketch, "E4084", {"start": v(-278.16, 21.53) * mm, "end": v(-279.86, 21.92) * mm});
            skLineSegment(sketch, "E4085", {"start": v(-279.86, 21.92) * mm, "end": v(-281.57, 22.27) * mm});
            skLineSegment(sketch, "E4086", {"start": v(-281.57, 22.27) * mm, "end": v(-283.3, 22.57) * mm});
            skLineSegment(sketch, "E4087", {"start": v(-283.3, 22.57) * mm, "end": v(-285.04, 22.83) * mm});
            skLineSegment(sketch, "E4088", {"start": v(-285.04, 22.83) * mm, "end": v(-286.8, 23.04) * mm});
            skLineSegment(sketch, "E4089", {"start": v(-286.8, 23.04) * mm, "end": v(-288.57, 23.2) * mm});
            skLineSegment(sketch, "E4090", {"start": v(-288.57, 23.2) * mm, "end": v(-290.35, 23.32) * mm});
            skLineSegment(sketch, "E4091", {"start": v(-290.35, 23.32) * mm, "end": v(-292.15, 23.4) * mm});
            skLineSegment(sketch, "E4092", {"start": v(-292.15, 23.4) * mm, "end": v(-293.96, 23.42) * mm});
            skLineSegment(sketch, "E4093", {"start": v(-293.96, 23.42) * mm, "end": v(-295.38, 23.4) * mm});
            skLineSegment(sketch, "E4094", {"start": v(-295.38, 23.4) * mm, "end": v(-296.8, 23.36) * mm});
            skLineSegment(sketch, "E4095", {"start": v(-296.8, 23.36) * mm, "end": v(-298.2, 23.28) * mm});
            skLineSegment(sketch, "E4096", {"start": v(-298.2, 23.28) * mm, "end": v(-299.6, 23.18) * mm});
            skLineSegment(sketch, "E4097", {"start": v(-299.6, 23.18) * mm, "end": v(-301, 23.05) * mm});
            skLineSegment(sketch, "E4098", {"start": v(-301, 23.05) * mm, "end": v(-302.38, 22.88) * mm});
            skLineSegment(sketch, "E4099", {"start": v(-302.38, 22.88) * mm, "end": v(-303.76, 22.7) * mm});
            skLineSegment(sketch, "E4100", {"start": v(-303.76, 22.7) * mm, "end": v(-305.13, 22.48) * mm});
            skLineSegment(sketch, "E4101", {"start": v(-305.13, 22.48) * mm, "end": v(-306.48, 22.23) * mm});
            skLineSegment(sketch, "E4102", {"start": v(-306.48, 22.23) * mm, "end": v(-307.83, 21.96) * mm});
            skLineSegment(sketch, "E4103", {"start": v(-307.83, 21.96) * mm, "end": v(-309.17, 21.66) * mm});
            skLineSegment(sketch, "E4104", {"start": v(-309.17, 21.66) * mm, "end": v(-310.5, 21.33) * mm});
            skLineSegment(sketch, "E4105", {"start": v(-310.5, 21.33) * mm, "end": v(-311.81, 20.98) * mm});
            skLineSegment(sketch, "E4106", {"start": v(-311.81, 20.98) * mm, "end": v(-313.12, 20.6) * mm});
            skLineSegment(sketch, "E4107", {"start": v(-313.12, 20.6) * mm, "end": v(-314.41, 20.2) * mm});
            skLineSegment(sketch, "E4108", {"start": v(-314.41, 20.2) * mm, "end": v(-315.7, 19.77) * mm});
            skLineSegment(sketch, "E4109", {"start": v(-315.7, 19.77) * mm, "end": v(-298.53, 151) * mm});
            skLineSegment(sketch, "E4110", {"start": v(-298.53, 151) * mm, "end": v(-298.22, 149.6) * mm});
            skLineSegment(sketch, "E4111", {"start": v(-298.22, 149.6) * mm, "end": v(-297.87, 148.2) * mm});
            skLineSegment(sketch, "E4112", {"start": v(-297.87, 148.2) * mm, "end": v(-297.5, 146.83) * mm});
            skLineSegment(sketch, "E4113", {"start": v(-297.5, 146.83) * mm, "end": v(-297.09, 145.46) * mm});
            skLineSegment(sketch, "E4114", {"start": v(-297.09, 145.46) * mm, "end": v(-296.65, 144.1) * mm});
            skLineSegment(sketch, "E4115", {"start": v(-296.65, 144.1) * mm, "end": v(-296.2, 142.77) * mm});
            skLineSegment(sketch, "E4116", {"start": v(-296.2, 142.77) * mm, "end": v(-295.7, 141.44) * mm});
            skLineSegment(sketch, "E4117", {"start": v(-295.7, 141.44) * mm, "end": v(-295.18, 140.12) * mm});
            skLineSegment(sketch, "E4118", {"start": v(-295.18, 140.12) * mm, "end": v(-294.64, 138.82) * mm});
            skLineSegment(sketch, "E4119", {"start": v(-294.64, 138.82) * mm, "end": v(-294.07, 137.54) * mm});
            skLineSegment(sketch, "E4120", {"start": v(-294.07, 137.54) * mm, "end": v(-293.48, 136.26) * mm});
            skLineSegment(sketch, "E4121", {"start": v(-293.48, 136.26) * mm, "end": v(-292.85, 135) * mm});
            skLineSegment(sketch, "E4122", {"start": v(-292.85, 135) * mm, "end": v(-292.2, 133.76) * mm});
            skLineSegment(sketch, "E4123", {"start": v(-292.2, 133.76) * mm, "end": v(-291.53, 132.53) * mm});
            skLineSegment(sketch, "E4124", {"start": v(-291.53, 132.53) * mm, "end": v(-290.84, 131.32) * mm});
            skLineSegment(sketch, "E4125", {"start": v(-290.84, 131.32) * mm, "end": v(-290.12, 130.13) * mm});
            skLineSegment(sketch, "E4126", {"start": v(-290.12, 130.13) * mm, "end": v(-289.37, 128.95) * mm});
            skLineSegment(sketch, "E4127", {"start": v(-289.37, 128.95) * mm, "end": v(-288.6, 127.79) * mm});
            skLineSegment(sketch, "E4128", {"start": v(-288.6, 127.79) * mm, "end": v(-287.8, 126.64) * mm});
            skLineSegment(sketch, "E4129", {"start": v(-287.8, 126.64) * mm, "end": v(-287, 125.52) * mm});
            skLineSegment(sketch, "E4130", {"start": v(-287, 125.52) * mm, "end": v(-286.15, 124.4) * mm});
            skLineSegment(sketch, "E4131", {"start": v(-286.15, 124.4) * mm, "end": v(-285.29, 123.31) * mm});
            skLineSegment(sketch, "E4132", {"start": v(-285.29, 123.31) * mm, "end": v(-284.4, 122.24) * mm});
            skLineSegment(sketch, "E4133", {"start": v(-284.4, 122.24) * mm, "end": v(-283.5, 121.19) * mm});
            skLineSegment(sketch, "E4134", {"start": v(-283.5, 121.19) * mm, "end": v(-282.57, 120.15) * mm});
            skLineSegment(sketch, "E4135", {"start": v(-282.57, 120.15) * mm, "end": v(-281.63, 119.14) * mm});
            skLineSegment(sketch, "E4136", {"start": v(-281.63, 119.14) * mm, "end": v(-280.66, 118.14) * mm});
            skLineSegment(sketch, "E4137", {"start": v(-280.66, 118.14) * mm, "end": v(-279.67, 117.17) * mm});
            skLineSegment(sketch, "E4138", {"start": v(-279.67, 117.17) * mm, "end": v(-278.66, 116.22) * mm});
            skLineSegment(sketch, "E4139", {"start": v(-278.66, 116.22) * mm, "end": v(-277.63, 115.28) * mm});
            skLineSegment(sketch, "E4140", {"start": v(-277.63, 115.28) * mm, "end": v(-276.58, 114.37) * mm});
            skLineSegment(sketch, "E4141", {"start": v(-276.58, 114.37) * mm, "end": v(-275.52, 113.48) * mm});
            skLineSegment(sketch, "E4142", {"start": v(-275.52, 113.48) * mm, "end": v(-274.43, 112.61) * mm});
            skLineSegment(sketch, "E4143", {"start": v(-274.43, 112.61) * mm, "end": v(-273.33, 111.77) * mm});
            skLineSegment(sketch, "E4144", {"start": v(-273.33, 111.77) * mm, "end": v(-272.2, 110.94) * mm});
            skLineSegment(sketch, "E4145", {"start": v(-272.2, 110.94) * mm, "end": v(-271.07, 110.14) * mm});
            skLineSegment(sketch, "E4146", {"start": v(-271.07, 110.14) * mm, "end": v(-269.91, 109.37) * mm});
            skLineSegment(sketch, "E4147", {"start": v(-269.91, 109.37) * mm, "end": v(-268.74, 108.61) * mm});
            skLineSegment(sketch, "E4148", {"start": v(-268.74, 108.61) * mm, "end": v(-267.55, 107.89) * mm});
            skLineSegment(sketch, "E4149", {"start": v(-267.55, 107.89) * mm, "end": v(-266.34, 107.18) * mm});
            skLineSegment(sketch, "E4150", {"start": v(-266.34, 107.18) * mm, "end": v(-265.12, 106.5) * mm});
            skLineSegment(sketch, "E4151", {"start": v(-265.12, 106.5) * mm, "end": v(-263.88, 105.85) * mm});
            skLineSegment(sketch, "E4152", {"start": v(-263.88, 105.85) * mm, "end": v(-262.63, 105.22) * mm});
            skLineSegment(sketch, "E4153", {"start": v(-262.63, 105.22) * mm, "end": v(-261.36, 104.61) * mm});
            skLineSegment(sketch, "E4154", {"start": v(-261.36, 104.61) * mm, "end": v(-260.08, 104.04) * mm});
            skLineSegment(sketch, "E4155", {"start": v(-260.08, 104.04) * mm, "end": v(-258.78, 103.49) * mm});
            skLineSegment(sketch, "E4156", {"start": v(-258.78, 103.49) * mm, "end": v(-257.47, 102.96) * mm});
            skLineSegment(sketch, "E4157", {"start": v(-257.47, 102.96) * mm, "end": v(-256.14, 102.46) * mm});
            skLineSegment(sketch, "E4158", {"start": v(-256.14, 102.46) * mm, "end": v(-254.8, 102) * mm});
            skLineSegment(sketch, "E4159", {"start": v(-254.8, 102) * mm, "end": v(-253.46, 101.55) * mm});
            skLineSegment(sketch, "E4160", {"start": v(-253.46, 101.55) * mm, "end": v(-252.1, 101.14) * mm});
            skLineSegment(sketch, "E4161", {"start": v(-252.1, 101.14) * mm, "end": v(-250.72, 100.75) * mm});
            skLineSegment(sketch, "E4162", {"start": v(-250.72, 100.75) * mm, "end": v(-249.33, 100.4) * mm});
            skLineSegment(sketch, "E4163", {"start": v(-249.33, 100.4) * mm, "end": v(-247.93, 100.07) * mm});
            skLineSegment(sketch, "E4164", {"start": v(-247.93, 100.07) * mm, "end": v(-246.52, 99.77) * mm});
            skLineSegment(sketch, "E4165", {"start": v(-246.52, 99.77) * mm, "end": v(-245.1, 99.5) * mm});
            skLineSegment(sketch, "E4166", {"start": v(-245.1, 99.5) * mm, "end": v(-243.67, 99.27) * mm});
            skLineSegment(sketch, "E4167", {"start": v(-243.67, 99.27) * mm, "end": v(-242.23, 99.06) * mm});
            skLineSegment(sketch, "E4168", {"start": v(-242.23, 99.06) * mm, "end": v(-240.78, 98.88) * mm});
            skLineSegment(sketch, "E4169", {"start": v(-240.78, 98.88) * mm, "end": v(-239.32, 98.74) * mm});
            skLineSegment(sketch, "E4170", {"start": v(-239.32, 98.74) * mm, "end": v(-237.85, 98.63) * mm});
            skLineSegment(sketch, "E4171", {"start": v(-237.85, 98.63) * mm, "end": v(-236.37, 98.55) * mm});
            skLineSegment(sketch, "E4172", {"start": v(-236.37, 98.55) * mm, "end": v(-234.89, 98.5) * mm});
            skLineSegment(sketch, "E4173", {"start": v(-234.89, 98.5) * mm, "end": v(-233.4, 98.48) * mm});
            skLineSegment(sketch, "E4174", {"start": v(-233.4, 98.48) * mm, "end": v(-232.39, 98.5) * mm});
            skLineSegment(sketch, "E4175", {"start": v(-232.39, 98.5) * mm, "end": v(-245, 1.99) * mm});
            skLineSegment(sketch, "E4176", {"start": v(-293.96, -87.6) * mm, "end": v(-295.24, -87.58) * mm});
            skLineSegment(sketch, "E4177", {"start": v(-295.24, -87.58) * mm, "end": v(-296.5, -87.54) * mm});
            skLineSegment(sketch, "E4178", {"start": v(-296.5, -87.54) * mm, "end": v(-297.77, -87.46) * mm});
            skLineSegment(sketch, "E4179", {"start": v(-297.77, -87.46) * mm, "end": v(-299.02, -87.34) * mm});
            skLineSegment(sketch, "E4180", {"start": v(-299.02, -87.34) * mm, "end": v(-300.26, -87.2) * mm});
            skLineSegment(sketch, "E4181", {"start": v(-300.26, -87.2) * mm, "end": v(-301.5, -87.03) * mm});
            skLineSegment(sketch, "E4182", {"start": v(-301.5, -87.03) * mm, "end": v(-302.72, -86.83) * mm});
            skLineSegment(sketch, "E4183", {"start": v(-302.72, -86.83) * mm, "end": v(-303.94, -86.6) * mm});
            skLineSegment(sketch, "E4184", {"start": v(-303.94, -86.6) * mm, "end": v(-305.14, -86.33) * mm});
            skLineSegment(sketch, "E4185", {"start": v(-305.14, -86.33) * mm, "end": v(-306.33, -86.04) * mm});
            skLineSegment(sketch, "E4186", {"start": v(-306.33, -86.04) * mm, "end": v(-307.51, -85.72) * mm});
            skLineSegment(sketch, "E4187", {"start": v(-307.51, -85.72) * mm, "end": v(-308.68, -85.37) * mm});
            skLineSegment(sketch, "E4188", {"start": v(-308.68, -85.37) * mm, "end": v(-309.84, -85) * mm});
            skLineSegment(sketch, "E4189", {"start": v(-309.84, -85) * mm, "end": v(-310.98, -84.6) * mm});
            skLineSegment(sketch, "E4190", {"start": v(-310.98, -84.6) * mm, "end": v(-312.11, -84.17) * mm});
            skLineSegment(sketch, "E4191", {"start": v(-312.11, -84.17) * mm, "end": v(-313.23, -83.7) * mm});
            skLineSegment(sketch, "E4192", {"start": v(-313.23, -83.7) * mm, "end": v(-314.33, -83.23) * mm});
            skLineSegment(sketch, "E4193", {"start": v(-314.33, -83.23) * mm, "end": v(-315.42, -82.72) * mm});
            skLineSegment(sketch, "E4194", {"start": v(-315.42, -82.72) * mm, "end": v(-316.5, -82.18) * mm});
            skLineSegment(sketch, "E4195", {"start": v(-316.5, -82.18) * mm, "end": v(-317.56, -81.62) * mm});
            skLineSegment(sketch, "E4196", {"start": v(-317.56, -81.62) * mm, "end": v(-318.6, -81.04) * mm});
            skLineSegment(sketch, "E4197", {"start": v(-318.6, -81.04) * mm, "end": v(-319.63, -80.43) * mm});
            skLineSegment(sketch, "E4198", {"start": v(-319.63, -80.43) * mm, "end": v(-320.65, -79.8) * mm});
            skLineSegment(sketch, "E4199", {"start": v(-320.65, -79.8) * mm, "end": v(-321.64, -79.14) * mm});
            skLineSegment(sketch, "E4200", {"start": v(-321.64, -79.14) * mm, "end": v(-322.62, -78.46) * mm});
            skLineSegment(sketch, "E4201", {"start": v(-322.62, -78.46) * mm, "end": v(-323.58, -77.76) * mm});
            skLineSegment(sketch, "E4202", {"start": v(-323.58, -77.76) * mm, "end": v(-324.53, -77.04) * mm});
            skLineSegment(sketch, "E4203", {"start": v(-324.53, -77.04) * mm, "end": v(-325.45, -76.3) * mm});
            skLineSegment(sketch, "E4204", {"start": v(-325.45, -76.3) * mm, "end": v(-326.36, -75.53) * mm});
            skLineSegment(sketch, "E4205", {"start": v(-326.36, -75.53) * mm, "end": v(-327.25, -74.74) * mm});
            skLineSegment(sketch, "E4206", {"start": v(-327.25, -74.74) * mm, "end": v(-328.12, -73.93) * mm});
            skLineSegment(sketch, "E4207", {"start": v(-328.12, -73.93) * mm, "end": v(-328.97, -73.1) * mm});
            skLineSegment(sketch, "E4208", {"start": v(-328.97, -73.1) * mm, "end": v(-329.8, -72.25) * mm});
            skLineSegment(sketch, "E4209", {"start": v(-329.8, -72.25) * mm, "end": v(-330.6, -71.38) * mm});
            skLineSegment(sketch, "E4210", {"start": v(-330.6, -71.38) * mm, "end": v(-331.4, -70.49) * mm});
            skLineSegment(sketch, "E4211", {"start": v(-331.4, -70.49) * mm, "end": v(-332.17, -69.58) * mm});
            skLineSegment(sketch, "E4212", {"start": v(-332.17, -69.58) * mm, "end": v(-332.91, -68.65) * mm});
            skLineSegment(sketch, "E4213", {"start": v(-332.91, -68.65) * mm, "end": v(-333.64, -67.71) * mm});
            skLineSegment(sketch, "E4214", {"start": v(-333.64, -67.71) * mm, "end": v(-334.34, -66.75) * mm});
            skLineSegment(sketch, "E4215", {"start": v(-334.34, -66.75) * mm, "end": v(-335.02, -65.77) * mm});
            skLineSegment(sketch, "E4216", {"start": v(-335.02, -65.77) * mm, "end": v(-335.67, -64.77) * mm});
            skLineSegment(sketch, "E4217", {"start": v(-335.67, -64.77) * mm, "end": v(-336.3, -63.76) * mm});
            skLineSegment(sketch, "E4218", {"start": v(-336.3, -63.76) * mm, "end": v(-336.91, -62.73) * mm});
            skLineSegment(sketch, "E4219", {"start": v(-336.91, -62.73) * mm, "end": v(-337.5, -61.69) * mm});
            skLineSegment(sketch, "E4220", {"start": v(-337.5, -61.69) * mm, "end": v(-338.06, -60.63) * mm});
            skLineSegment(sketch, "E4221", {"start": v(-338.06, -60.63) * mm, "end": v(-338.59, -59.55) * mm});
            skLineSegment(sketch, "E4222", {"start": v(-338.59, -59.55) * mm, "end": v(-339.1, -58.46) * mm});
            skLineSegment(sketch, "E4223", {"start": v(-339.1, -58.46) * mm, "end": v(-339.58, -57.36) * mm});
            skLineSegment(sketch, "E4224", {"start": v(-339.58, -57.36) * mm, "end": v(-340.04, -56.24) * mm});
            skLineSegment(sketch, "E4225", {"start": v(-340.04, -56.24) * mm, "end": v(-340.47, -55.1) * mm});
            skLineSegment(sketch, "E4226", {"start": v(-340.47, -55.1) * mm, "end": v(-340.87, -53.97) * mm});
            skLineSegment(sketch, "E4227", {"start": v(-340.87, -53.97) * mm, "end": v(-341.25, -52.8) * mm});
            skLineSegment(sketch, "E4228", {"start": v(-341.25, -52.8) * mm, "end": v(-341.6, -51.64) * mm});
            skLineSegment(sketch, "E4229", {"start": v(-341.6, -51.64) * mm, "end": v(-341.91, -50.46) * mm});
            skLineSegment(sketch, "E4230", {"start": v(-341.91, -50.46) * mm, "end": v(-342.2, -49.27) * mm});
            skLineSegment(sketch, "E4231", {"start": v(-342.2, -49.27) * mm, "end": v(-342.47, -48.06) * mm});
            skLineSegment(sketch, "E4232", {"start": v(-342.47, -48.06) * mm, "end": v(-342.7, -46.85) * mm});
            skLineSegment(sketch, "E4233", {"start": v(-342.7, -46.85) * mm, "end": v(-342.9, -45.62) * mm});
            skLineSegment(sketch, "E4234", {"start": v(-342.9, -45.62) * mm, "end": v(-343.07, -44.4) * mm});
            skLineSegment(sketch, "E4235", {"start": v(-343.07, -44.4) * mm, "end": v(-343.22, -43.15) * mm});
            skLineSegment(sketch, "E4236", {"start": v(-343.22, -43.15) * mm, "end": v(-343.33, -41.9) * mm});
            skLineSegment(sketch, "E4237", {"start": v(-343.33, -41.9) * mm, "end": v(-343.4, -40.63) * mm});
            skLineSegment(sketch, "E4238", {"start": v(-343.4, -40.63) * mm, "end": v(-343.46, -39.36) * mm});
            skLineSegment(sketch, "E4239", {"start": v(-343.46, -39.36) * mm, "end": v(-343.47, -38.08) * mm});
            skLineSegment(sketch, "E4240", {"start": v(-343.47, -38.08) * mm, "end": v(-343.46, -36.8) * mm});
            skLineSegment(sketch, "E4241", {"start": v(-343.46, -36.8) * mm, "end": v(-343.4, -35.54) * mm});
            skLineSegment(sketch, "E4242", {"start": v(-343.4, -35.54) * mm, "end": v(-343.33, -34.27) * mm});
            skLineSegment(sketch, "E4243", {"start": v(-343.33, -34.27) * mm, "end": v(-343.22, -33.02) * mm});
            skLineSegment(sketch, "E4244", {"start": v(-343.22, -33.02) * mm, "end": v(-343.07, -31.78) * mm});
            skLineSegment(sketch, "E4245", {"start": v(-343.07, -31.78) * mm, "end": v(-342.9, -30.54) * mm});
            skLineSegment(sketch, "E4246", {"start": v(-342.9, -30.54) * mm, "end": v(-342.7, -29.32) * mm});
            skLineSegment(sketch, "E4247", {"start": v(-342.7, -29.32) * mm, "end": v(-342.47, -28.1) * mm});
            skLineSegment(sketch, "E4248", {"start": v(-342.47, -28.1) * mm, "end": v(-342.2, -26.9) * mm});
            skLineSegment(sketch, "E4249", {"start": v(-342.2, -26.9) * mm, "end": v(-341.91, -25.7) * mm});
            skLineSegment(sketch, "E4250", {"start": v(-341.91, -25.7) * mm, "end": v(-341.6, -24.53) * mm});
            skLineSegment(sketch, "E4251", {"start": v(-341.6, -24.53) * mm, "end": v(-341.25, -23.36) * mm});
            skLineSegment(sketch, "E4252", {"start": v(-341.25, -23.36) * mm, "end": v(-340.87, -22.2) * mm});
            skLineSegment(sketch, "E4253", {"start": v(-340.87, -22.2) * mm, "end": v(-340.47, -21.06) * mm});
            skLineSegment(sketch, "E4254", {"start": v(-340.47, -21.06) * mm, "end": v(-340.04, -19.93) * mm});
            skLineSegment(sketch, "E4255", {"start": v(-340.04, -19.93) * mm, "end": v(-339.58, -18.81) * mm});
            skLineSegment(sketch, "E4256", {"start": v(-339.58, -18.81) * mm, "end": v(-339.1, -17.7) * mm});
            skLineSegment(sketch, "E4257", {"start": v(-339.1, -17.7) * mm, "end": v(-338.59, -16.62) * mm});
            skLineSegment(sketch, "E4258", {"start": v(-338.59, -16.62) * mm, "end": v(-338.06, -15.54) * mm});
            skLineSegment(sketch, "E4259", {"start": v(-338.06, -15.54) * mm, "end": v(-337.5, -14.48) * mm});
            skLineSegment(sketch, "E4260", {"start": v(-337.5, -14.48) * mm, "end": v(-336.91, -13.44) * mm});
            skLineSegment(sketch, "E4261", {"start": v(-336.91, -13.44) * mm, "end": v(-336.3, -12.4) * mm});
            skLineSegment(sketch, "E4262", {"start": v(-336.3, -12.4) * mm, "end": v(-335.67, -11.4) * mm});
            skLineSegment(sketch, "E4263", {"start": v(-335.67, -11.4) * mm, "end": v(-335.02, -10.4) * mm});
            skLineSegment(sketch, "E4264", {"start": v(-335.02, -10.4) * mm, "end": v(-334.34, -9.42) * mm});
            skLineSegment(sketch, "E4265", {"start": v(-334.34, -9.42) * mm, "end": v(-333.64, -8.46) * mm});
            skLineSegment(sketch, "E4266", {"start": v(-333.64, -8.46) * mm, "end": v(-332.91, -7.51) * mm});
            skLineSegment(sketch, "E4267", {"start": v(-332.91, -7.51) * mm, "end": v(-332.17, -6.59) * mm});
            skLineSegment(sketch, "E4268", {"start": v(-332.17, -6.59) * mm, "end": v(-331.4, -5.68) * mm});
            skLineSegment(sketch, "E4269", {"start": v(-331.4, -5.68) * mm, "end": v(-330.6, -4.8) * mm});
            skLineSegment(sketch, "E4270", {"start": v(-330.6, -4.8) * mm, "end": v(-329.8, -3.92) * mm});
            skLineSegment(sketch, "E4271", {"start": v(-329.8, -3.92) * mm, "end": v(-328.97, -3.07) * mm});
            skLineSegment(sketch, "E4272", {"start": v(-328.97, -3.07) * mm, "end": v(-328.12, -2.24) * mm});
            skLineSegment(sketch, "E4273", {"start": v(-328.12, -2.24) * mm, "end": v(-327.25, -1.43) * mm});
            skLineSegment(sketch, "E4274", {"start": v(-327.25, -1.43) * mm, "end": v(-326.36, -0.64) * mm});
            skLineSegment(sketch, "E4275", {"start": v(-326.36, -0.64) * mm, "end": v(-325.45, 0.12) * mm});
            skLineSegment(sketch, "E4276", {"start": v(-325.45, 0.12) * mm, "end": v(-324.53, 0.87) * mm});
            skLineSegment(sketch, "E4277", {"start": v(-324.53, 0.87) * mm, "end": v(-323.58, 1.6) * mm});
            skLineSegment(sketch, "E4278", {"start": v(-323.58, 1.6) * mm, "end": v(-322.62, 2.3) * mm});
            skLineSegment(sketch, "E4279", {"start": v(-322.62, 2.3) * mm, "end": v(-321.64, 2.97) * mm});
            skLineSegment(sketch, "E4280", {"start": v(-321.64, 2.97) * mm, "end": v(-320.65, 3.63) * mm});
            skLineSegment(sketch, "E4281", {"start": v(-320.65, 3.63) * mm, "end": v(-319.63, 4.26) * mm});
            skLineSegment(sketch, "E4282", {"start": v(-319.63, 4.26) * mm, "end": v(-318.6, 4.87) * mm});
            skLineSegment(sketch, "E4283", {"start": v(-318.6, 4.87) * mm, "end": v(-317.56, 5.45) * mm});
            skLineSegment(sketch, "E4284", {"start": v(-317.56, 5.45) * mm, "end": v(-316.5, 6.01) * mm});
            skLineSegment(sketch, "E4285", {"start": v(-316.5, 6.01) * mm, "end": v(-315.42, 6.55) * mm});
            skLineSegment(sketch, "E4286", {"start": v(-315.42, 6.55) * mm, "end": v(-314.33, 7.06) * mm});
            skLineSegment(sketch, "E4287", {"start": v(-314.33, 7.06) * mm, "end": v(-313.23, 7.54) * mm});
            skLineSegment(sketch, "E4288", {"start": v(-313.23, 7.54) * mm, "end": v(-312.11, 8) * mm});
            skLineSegment(sketch, "E4289", {"start": v(-312.11, 8) * mm, "end": v(-310.98, 8.43) * mm});
            skLineSegment(sketch, "E4290", {"start": v(-310.98, 8.43) * mm, "end": v(-309.84, 8.83) * mm});
            skLineSegment(sketch, "E4291", {"start": v(-309.84, 8.83) * mm, "end": v(-308.68, 9.2) * mm});
            skLineSegment(sketch, "E4292", {"start": v(-308.68, 9.2) * mm, "end": v(-307.51, 9.55) * mm});
            skLineSegment(sketch, "E4293", {"start": v(-307.51, 9.55) * mm, "end": v(-306.33, 9.87) * mm});
            skLineSegment(sketch, "E4294", {"start": v(-306.33, 9.87) * mm, "end": v(-305.14, 10.16) * mm});
            skLineSegment(sketch, "E4295", {"start": v(-305.14, 10.16) * mm, "end": v(-303.94, 10.42) * mm});
            skLineSegment(sketch, "E4296", {"start": v(-303.94, 10.42) * mm, "end": v(-302.72, 10.66) * mm});
            skLineSegment(sketch, "E4297", {"start": v(-302.72, 10.66) * mm, "end": v(-301.5, 10.86) * mm});
            skLineSegment(sketch, "E4298", {"start": v(-301.5, 10.86) * mm, "end": v(-300.26, 11.03) * mm});
            skLineSegment(sketch, "E4299", {"start": v(-300.26, 11.03) * mm, "end": v(-299.02, 11.17) * mm});
            skLineSegment(sketch, "E4300", {"start": v(-299.02, 11.17) * mm, "end": v(-297.77, 11.29) * mm});
            skLineSegment(sketch, "E4301", {"start": v(-297.77, 11.29) * mm, "end": v(-296.5, 11.37) * mm});
            skLineSegment(sketch, "E4302", {"start": v(-296.5, 11.37) * mm, "end": v(-295.24, 11.41) * mm});
            skLineSegment(sketch, "E4303", {"start": v(-295.24, 11.41) * mm, "end": v(-293.96, 11.43) * mm});
            skLineSegment(sketch, "E4304", {"start": v(-293.96, 11.43) * mm, "end": v(-292.68, 11.41) * mm});
            skLineSegment(sketch, "E4305", {"start": v(-292.68, 11.41) * mm, "end": v(-291.4, 11.37) * mm});
            skLineSegment(sketch, "E4306", {"start": v(-291.4, 11.37) * mm, "end": v(-290.15, 11.29) * mm});
            skLineSegment(sketch, "E4307", {"start": v(-290.15, 11.29) * mm, "end": v(-288.9, 11.17) * mm});
            skLineSegment(sketch, "E4308", {"start": v(-288.9, 11.17) * mm, "end": v(-287.65, 11.03) * mm});
            skLineSegment(sketch, "E4309", {"start": v(-287.65, 11.03) * mm, "end": v(-286.42, 10.86) * mm});
            skLineSegment(sketch, "E4310", {"start": v(-286.42, 10.86) * mm, "end": v(-285.2, 10.66) * mm});
            skLineSegment(sketch, "E4311", {"start": v(-285.2, 10.66) * mm, "end": v(-283.98, 10.42) * mm});
            skLineSegment(sketch, "E4312", {"start": v(-283.98, 10.42) * mm, "end": v(-282.78, 10.16) * mm});
            skLineSegment(sketch, "E4313", {"start": v(-282.78, 10.16) * mm, "end": v(-281.58, 9.87) * mm});
            skLineSegment(sketch, "E4314", {"start": v(-281.58, 9.87) * mm, "end": v(-280.4, 9.55) * mm});
            skLineSegment(sketch, "E4315", {"start": v(-280.4, 9.55) * mm, "end": v(-279.23, 9.2) * mm});
            skLineSegment(sketch, "E4316", {"start": v(-279.23, 9.2) * mm, "end": v(-278.08, 8.83) * mm});
            skLineSegment(sketch, "E4317", {"start": v(-278.08, 8.83) * mm, "end": v(-276.93, 8.43) * mm});
            skLineSegment(sketch, "E4318", {"start": v(-276.93, 8.43) * mm, "end": v(-275.8, 8) * mm});
            skLineSegment(sketch, "E4319", {"start": v(-275.8, 8) * mm, "end": v(-274.68, 7.54) * mm});
            skLineSegment(sketch, "E4320", {"start": v(-274.68, 7.54) * mm, "end": v(-273.58, 7.06) * mm});
            skLineSegment(sketch, "E4321", {"start": v(-273.58, 7.06) * mm, "end": v(-272.5, 6.55) * mm});
            skLineSegment(sketch, "E4322", {"start": v(-272.5, 6.55) * mm, "end": v(-271.42, 6.01) * mm});
            skLineSegment(sketch, "E4323", {"start": v(-271.42, 6.01) * mm, "end": v(-270.36, 5.45) * mm});
            skLineSegment(sketch, "E4324", {"start": v(-270.36, 5.45) * mm, "end": v(-269.31, 4.87) * mm});
            skLineSegment(sketch, "E4325", {"start": v(-269.31, 4.87) * mm, "end": v(-268.28, 4.26) * mm});
            skLineSegment(sketch, "E4326", {"start": v(-268.28, 4.26) * mm, "end": v(-267.27, 3.63) * mm});
            skLineSegment(sketch, "E4327", {"start": v(-267.27, 3.63) * mm, "end": v(-266.27, 2.97) * mm});
            skLineSegment(sketch, "E4328", {"start": v(-266.27, 2.97) * mm, "end": v(-265.3, 2.3) * mm});
            skLineSegment(sketch, "E4329", {"start": v(-265.3, 2.3) * mm, "end": v(-264.33, 1.6) * mm});
            skLineSegment(sketch, "E4330", {"start": v(-264.33, 1.6) * mm, "end": v(-263.39, 0.87) * mm});
            skLineSegment(sketch, "E4331", {"start": v(-263.39, 0.87) * mm, "end": v(-262.46, 0.12) * mm});
            skLineSegment(sketch, "E4332", {"start": v(-262.46, 0.12) * mm, "end": v(-261.55, -0.64) * mm});
            skLineSegment(sketch, "E4333", {"start": v(-261.55, -0.64) * mm, "end": v(-260.66, -1.43) * mm});
            skLineSegment(sketch, "E4334", {"start": v(-260.66, -1.43) * mm, "end": v(-259.8, -2.24) * mm});
            skLineSegment(sketch, "E4335", {"start": v(-259.8, -2.24) * mm, "end": v(-258.94, -3.07) * mm});
            skLineSegment(sketch, "E4336", {"start": v(-258.94, -3.07) * mm, "end": v(-258.11, -3.92) * mm});
            skLineSegment(sketch, "E4337", {"start": v(-258.11, -3.92) * mm, "end": v(-257.3, -4.8) * mm});
            skLineSegment(sketch, "E4338", {"start": v(-257.3, -4.8) * mm, "end": v(-256.52, -5.68) * mm});
            skLineSegment(sketch, "E4339", {"start": v(-256.52, -5.68) * mm, "end": v(-255.75, -6.59) * mm});
            skLineSegment(sketch, "E4340", {"start": v(-255.75, -6.59) * mm, "end": v(-255, -7.51) * mm});
            skLineSegment(sketch, "E4341", {"start": v(-255, -7.51) * mm, "end": v(-254.28, -8.46) * mm});
            skLineSegment(sketch, "E4342", {"start": v(-254.28, -8.46) * mm, "end": v(-253.58, -9.42) * mm});
            skLineSegment(sketch, "E4343", {"start": v(-253.58, -9.42) * mm, "end": v(-252.9, -10.4) * mm});
            skLineSegment(sketch, "E4344", {"start": v(-252.9, -10.4) * mm, "end": v(-252.24, -11.4) * mm});
            skLineSegment(sketch, "E4345", {"start": v(-252.24, -11.4) * mm, "end": v(-251.61, -12.4) * mm});
            skLineSegment(sketch, "E4346", {"start": v(-251.61, -12.4) * mm, "end": v(-251, -13.44) * mm});
            skLineSegment(sketch, "E4347", {"start": v(-251, -13.44) * mm, "end": v(-250.42, -14.48) * mm});
            skLineSegment(sketch, "E4348", {"start": v(-250.42, -14.48) * mm, "end": v(-249.86, -15.54) * mm});
            skLineSegment(sketch, "E4349", {"start": v(-249.86, -15.54) * mm, "end": v(-249.32, -16.62) * mm});
            skLineSegment(sketch, "E4350", {"start": v(-249.32, -16.62) * mm, "end": v(-248.82, -17.7) * mm});
            skLineSegment(sketch, "E4351", {"start": v(-248.82, -17.7) * mm, "end": v(-248.33, -18.81) * mm});
            skLineSegment(sketch, "E4352", {"start": v(-248.33, -18.81) * mm, "end": v(-247.88, -19.93) * mm});
            skLineSegment(sketch, "E4353", {"start": v(-247.88, -19.93) * mm, "end": v(-247.45, -21.06) * mm});
            skLineSegment(sketch, "E4354", {"start": v(-247.45, -21.06) * mm, "end": v(-247.04, -22.2) * mm});
            skLineSegment(sketch, "E4355", {"start": v(-247.04, -22.2) * mm, "end": v(-246.67, -23.36) * mm});
            skLineSegment(sketch, "E4356", {"start": v(-246.67, -23.36) * mm, "end": v(-246.32, -24.53) * mm});
            skLineSegment(sketch, "E4357", {"start": v(-246.32, -24.53) * mm, "end": v(-246, -25.7) * mm});
            skLineSegment(sketch, "E4358", {"start": v(-246, -25.7) * mm, "end": v(-245.7, -26.9) * mm});
            skLineSegment(sketch, "E4359", {"start": v(-245.7, -26.9) * mm, "end": v(-245.45, -28.1) * mm});
            skLineSegment(sketch, "E4360", {"start": v(-245.45, -28.1) * mm, "end": v(-245.21, -29.32) * mm});
            skLineSegment(sketch, "E4361", {"start": v(-245.21, -29.32) * mm, "end": v(-245.01, -30.54) * mm});
            skLineSegment(sketch, "E4362", {"start": v(-245.01, -30.54) * mm, "end": v(-244.84, -31.78) * mm});
            skLineSegment(sketch, "E4363", {"start": v(-244.84, -31.78) * mm, "end": v(-244.7, -33.02) * mm});
            skLineSegment(sketch, "E4364", {"start": v(-244.7, -33.02) * mm, "end": v(-244.59, -34.27) * mm});
            skLineSegment(sketch, "E4365", {"start": v(-244.59, -34.27) * mm, "end": v(-244.5, -35.54) * mm});
            skLineSegment(sketch, "E4366", {"start": v(-244.5, -35.54) * mm, "end": v(-244.46, -36.8) * mm});
            skLineSegment(sketch, "E4367", {"start": v(-244.46, -36.8) * mm, "end": v(-244.44, -38.08) * mm});
            skLineSegment(sketch, "E4368", {"start": v(-244.44, -38.08) * mm, "end": v(-244.46, -39.36) * mm});
            skLineSegment(sketch, "E4369", {"start": v(-244.46, -39.36) * mm, "end": v(-244.5, -40.63) * mm});
            skLineSegment(sketch, "E4370", {"start": v(-244.5, -40.63) * mm, "end": v(-244.59, -41.9) * mm});
            skLineSegment(sketch, "E4371", {"start": v(-244.59, -41.9) * mm, "end": v(-244.7, -43.15) * mm});
            skLineSegment(sketch, "E4372", {"start": v(-244.7, -43.15) * mm, "end": v(-244.84, -44.4) * mm});
            skLineSegment(sketch, "E4373", {"start": v(-244.84, -44.4) * mm, "end": v(-245.01, -45.62) * mm});
            skLineSegment(sketch, "E4374", {"start": v(-245.01, -45.62) * mm, "end": v(-245.21, -46.85) * mm});
            skLineSegment(sketch, "E4375", {"start": v(-245.21, -46.85) * mm, "end": v(-245.45, -48.06) * mm});
            skLineSegment(sketch, "E4376", {"start": v(-245.45, -48.06) * mm, "end": v(-245.7, -49.27) * mm});
            skLineSegment(sketch, "E4377", {"start": v(-245.7, -49.27) * mm, "end": v(-246, -50.46) * mm});
            skLineSegment(sketch, "E4378", {"start": v(-246, -50.46) * mm, "end": v(-246.32, -51.64) * mm});
            skLineSegment(sketch, "E4379", {"start": v(-246.32, -51.64) * mm, "end": v(-246.67, -52.8) * mm});
            skLineSegment(sketch, "E4380", {"start": v(-246.67, -52.8) * mm, "end": v(-247.04, -53.97) * mm});
            skLineSegment(sketch, "E4381", {"start": v(-247.04, -53.97) * mm, "end": v(-247.45, -55.1) * mm});
            skLineSegment(sketch, "E4382", {"start": v(-247.45, -55.1) * mm, "end": v(-247.88, -56.24) * mm});
            skLineSegment(sketch, "E4383", {"start": v(-247.88, -56.24) * mm, "end": v(-248.33, -57.36) * mm});
            skLineSegment(sketch, "E4384", {"start": v(-248.33, -57.36) * mm, "end": v(-248.82, -58.46) * mm});
            skLineSegment(sketch, "E4385", {"start": v(-248.82, -58.46) * mm, "end": v(-249.32, -59.55) * mm});
            skLineSegment(sketch, "E4386", {"start": v(-249.32, -59.55) * mm, "end": v(-249.86, -60.63) * mm});
            skLineSegment(sketch, "E4387", {"start": v(-249.86, -60.63) * mm, "end": v(-250.42, -61.69) * mm});
            skLineSegment(sketch, "E4388", {"start": v(-250.42, -61.69) * mm, "end": v(-251, -62.73) * mm});
            skLineSegment(sketch, "E4389", {"start": v(-251, -62.73) * mm, "end": v(-251.61, -63.76) * mm});
            skLineSegment(sketch, "E4390", {"start": v(-251.61, -63.76) * mm, "end": v(-252.24, -64.77) * mm});
            skLineSegment(sketch, "E4391", {"start": v(-252.24, -64.77) * mm, "end": v(-252.9, -65.77) * mm});
            skLineSegment(sketch, "E4392", {"start": v(-252.9, -65.77) * mm, "end": v(-253.58, -66.75) * mm});
            skLineSegment(sketch, "E4393", {"start": v(-253.58, -66.75) * mm, "end": v(-254.28, -67.71) * mm});
            skLineSegment(sketch, "E4394", {"start": v(-254.28, -67.71) * mm, "end": v(-255, -68.65) * mm});
            skLineSegment(sketch, "E4395", {"start": v(-255, -68.65) * mm, "end": v(-255.75, -69.58) * mm});
            skLineSegment(sketch, "E4396", {"start": v(-255.75, -69.58) * mm, "end": v(-256.52, -70.49) * mm});
            skLineSegment(sketch, "E4397", {"start": v(-256.52, -70.49) * mm, "end": v(-257.3, -71.38) * mm});
            skLineSegment(sketch, "E4398", {"start": v(-257.3, -71.38) * mm, "end": v(-258.11, -72.25) * mm});
            skLineSegment(sketch, "E4399", {"start": v(-258.11, -72.25) * mm, "end": v(-258.94, -73.1) * mm});
            skLineSegment(sketch, "E4400", {"start": v(-258.94, -73.1) * mm, "end": v(-259.8, -73.93) * mm});
            skLineSegment(sketch, "E4401", {"start": v(-259.8, -73.93) * mm, "end": v(-260.66, -74.74) * mm});
            skLineSegment(sketch, "E4402", {"start": v(-260.66, -74.74) * mm, "end": v(-261.55, -75.53) * mm});
            skLineSegment(sketch, "E4403", {"start": v(-261.55, -75.53) * mm, "end": v(-262.46, -76.3) * mm});
            skLineSegment(sketch, "E4404", {"start": v(-262.46, -76.3) * mm, "end": v(-263.39, -77.04) * mm});
            skLineSegment(sketch, "E4405", {"start": v(-263.39, -77.04) * mm, "end": v(-264.33, -77.76) * mm});
            skLineSegment(sketch, "E4406", {"start": v(-264.33, -77.76) * mm, "end": v(-265.3, -78.46) * mm});
            skLineSegment(sketch, "E4407", {"start": v(-265.3, -78.46) * mm, "end": v(-266.27, -79.14) * mm});
            skLineSegment(sketch, "E4408", {"start": v(-266.27, -79.14) * mm, "end": v(-267.27, -79.8) * mm});
            skLineSegment(sketch, "E4409", {"start": v(-267.27, -79.8) * mm, "end": v(-268.28, -80.43) * mm});
            skLineSegment(sketch, "E4410", {"start": v(-268.28, -80.43) * mm, "end": v(-269.31, -81.04) * mm});
            skLineSegment(sketch, "E4411", {"start": v(-269.31, -81.04) * mm, "end": v(-270.36, -81.62) * mm});
            skLineSegment(sketch, "E4412", {"start": v(-270.36, -81.62) * mm, "end": v(-271.42, -82.18) * mm});
            skLineSegment(sketch, "E4413", {"start": v(-271.42, -82.18) * mm, "end": v(-272.5, -82.72) * mm});
            skLineSegment(sketch, "E4414", {"start": v(-272.5, -82.72) * mm, "end": v(-273.58, -83.23) * mm});
            skLineSegment(sketch, "E4415", {"start": v(-273.58, -83.23) * mm, "end": v(-274.68, -83.7) * mm});
            skLineSegment(sketch, "E4416", {"start": v(-274.68, -83.7) * mm, "end": v(-275.8, -84.17) * mm});
            skLineSegment(sketch, "E4417", {"start": v(-275.8, -84.17) * mm, "end": v(-276.93, -84.6) * mm});
            skLineSegment(sketch, "E4418", {"start": v(-276.93, -84.6) * mm, "end": v(-278.08, -85) * mm});
            skLineSegment(sketch, "E4419", {"start": v(-278.08, -85) * mm, "end": v(-279.23, -85.37) * mm});
            skLineSegment(sketch, "E4420", {"start": v(-279.23, -85.37) * mm, "end": v(-280.4, -85.72) * mm});
            skLineSegment(sketch, "E4421", {"start": v(-280.4, -85.72) * mm, "end": v(-281.58, -86.04) * mm});
            skLineSegment(sketch, "E4422", {"start": v(-281.58, -86.04) * mm, "end": v(-282.78, -86.33) * mm});
            skLineSegment(sketch, "E4423", {"start": v(-282.78, -86.33) * mm, "end": v(-283.98, -86.6) * mm});
            skLineSegment(sketch, "E4424", {"start": v(-283.98, -86.6) * mm, "end": v(-285.2, -86.83) * mm});
            skLineSegment(sketch, "E4425", {"start": v(-285.2, -86.83) * mm, "end": v(-286.42, -87.03) * mm});
            skLineSegment(sketch, "E4426", {"start": v(-286.42, -87.03) * mm, "end": v(-287.65, -87.2) * mm});
            skLineSegment(sketch, "E4427", {"start": v(-287.65, -87.2) * mm, "end": v(-288.9, -87.34) * mm});
            skLineSegment(sketch, "E4428", {"start": v(-288.9, -87.34) * mm, "end": v(-290.15, -87.46) * mm});
            skLineSegment(sketch, "E4429", {"start": v(-290.15, -87.46) * mm, "end": v(-291.4, -87.54) * mm});
            skLineSegment(sketch, "E4430", {"start": v(-291.4, -87.54) * mm, "end": v(-292.68, -87.58) * mm});
            skLineSegment(sketch, "E4431", {"start": v(-292.68, -87.58) * mm, "end": v(-293.96, -87.6) * mm});
            skLineSegment(sketch, "E4432", {"start": v(-516.32, -407.33) * mm, "end": v(-516.32, -361.92) * mm});
            skLineSegment(sketch, "E4433", {"start": v(-516.32, -361.92) * mm, "end": v(-505.12, -361.92) * mm});
            skLineSegment(sketch, "E4434", {"start": v(-505.12, -361.92) * mm, "end": v(-492.56, -392.44) * mm});
            skLineSegment(sketch, "E4435", {"start": v(-492.56, -392.44) * mm, "end": v(-492, -392.44) * mm});
            skLineSegment(sketch, "E4436", {"start": v(-492, -392.44) * mm, "end": v(-479.4, -361.92) * mm});
            skLineSegment(sketch, "E4437", {"start": v(-479.4, -361.92) * mm, "end": v(-468.24, -361.92) * mm});
            skLineSegment(sketch, "E4438", {"start": v(-468.24, -361.92) * mm, "end": v(-468.24, -407.33) * mm});
            skLineSegment(sketch, "E4439", {"start": v(-468.24, -407.33) * mm, "end": v(-477.05, -407.33) * mm});
            skLineSegment(sketch, "E4440", {"start": v(-477.05, -407.33) * mm, "end": v(-477.05, -376.96) * mm});
            skLineSegment(sketch, "E4441", {"start": v(-477.05, -376.96) * mm, "end": v(-477.55, -376.96) * mm});
            skLineSegment(sketch, "E4442", {"start": v(-477.55, -376.96) * mm, "end": v(-489.1, -404.72) * mm});
            skLineSegment(sketch, "E4443", {"start": v(-489.1, -404.72) * mm, "end": v(-495.43, -404.72) * mm});
            skLineSegment(sketch, "E4444", {"start": v(-495.43, -404.72) * mm, "end": v(-507, -376.96) * mm});
            skLineSegment(sketch, "E4445", {"start": v(-507, -376.96) * mm, "end": v(-507.51, -376.96) * mm});
            skLineSegment(sketch, "E4446", {"start": v(-507.51, -376.96) * mm, "end": v(-507.51, -407.33) * mm});
            skLineSegment(sketch, "E4447", {"start": v(-507.51, -407.33) * mm, "end": v(-516.32, -407.33) * mm});
            skLineSegment(sketch, "E4448", {"start": v(-408.95, -371.36) * mm, "end": v(-408.39, -371.36) * mm});
            skLineSegment(sketch, "E4449", {"start": v(-408.39, -371.36) * mm, "end": v(-402.76, -389.17) * mm});
            skLineSegment(sketch, "E4450", {"start": v(-402.76, -389.17) * mm, "end": v(-414.65, -389.17) * mm});
            skLineSegment(sketch, "E4451", {"start": v(-414.65, -389.17) * mm, "end": v(-408.95, -371.36) * mm});
            skLineSegment(sketch, "E4452", {"start": v(-400.74, -396.5) * mm, "end": v(-416.7, -396.5) * mm});
            skLineSegment(sketch, "E4453", {"start": v(-416.7, -396.5) * mm, "end": v(-420.19, -407.33) * mm});
            skLineSegment(sketch, "E4454", {"start": v(-420.19, -407.33) * mm, "end": v(-429.72, -407.33) * mm});
            skLineSegment(sketch, "E4455", {"start": v(-429.72, -407.33) * mm, "end": v(-413.96, -361.92) * mm});
            skLineSegment(sketch, "E4456", {"start": v(-413.96, -361.92) * mm, "end": v(-402.79, -361.92) * mm});
            skLineSegment(sketch, "E4457", {"start": v(-402.79, -361.92) * mm, "end": v(-387.02, -407.33) * mm});
            skLineSegment(sketch, "E4458", {"start": v(-387.02, -407.33) * mm, "end": v(-397.31, -407.33) * mm});
            skLineSegment(sketch, "E4459", {"start": v(-397.31, -407.33) * mm, "end": v(-400.74, -396.5) * mm});
            skLineSegment(sketch, "E4460", {"start": v(-348.54, -407.33) * mm, "end": v(-348.54, -361.92) * mm});
            skLineSegment(sketch, "E4461", {"start": v(-348.54, -361.92) * mm, "end": v(-339.03, -361.92) * mm});
            skLineSegment(sketch, "E4462", {"start": v(-339.03, -361.92) * mm, "end": v(-339.03, -382.16) * mm});
            skLineSegment(sketch, "E4463", {"start": v(-339.03, -382.16) * mm, "end": v(-338.47, -382.16) * mm});
            skLineSegment(sketch, "E4464", {"start": v(-338.47, -382.16) * mm, "end": v(-321.7, -361.92) * mm});
            skLineSegment(sketch, "E4465", {"start": v(-321.7, -361.92) * mm, "end": v(-311.12, -361.92) * mm});
            skLineSegment(sketch, "E4466", {"start": v(-311.12, -361.92) * mm, "end": v(-327.67, -381.84) * mm});
            skLineSegment(sketch, "E4467", {"start": v(-327.67, -381.84) * mm, "end": v(-309.96, -407.33) * mm});
            skLineSegment(sketch, "E4468", {"start": v(-309.96, -407.33) * mm, "end": v(-321.35, -407.33) * mm});
            skLineSegment(sketch, "E4469", {"start": v(-321.35, -407.33) * mm, "end": v(-334.53, -388.32) * mm});
            skLineSegment(sketch, "E4470", {"start": v(-334.53, -388.32) * mm, "end": v(-339.03, -393.64) * mm});
            skLineSegment(sketch, "E4471", {"start": v(-339.03, -393.64) * mm, "end": v(-339.03, -407.33) * mm});
            skLineSegment(sketch, "E4472", {"start": v(-339.03, -407.33) * mm, "end": v(-348.54, -407.33) * mm});
            skLineSegment(sketch, "E4473", {"start": v(-241.99, -407.33) * mm, "end": v(-272.07, -407.33) * mm});
            skLineSegment(sketch, "E4474", {"start": v(-272.07, -407.33) * mm, "end": v(-272.07, -361.92) * mm});
            skLineSegment(sketch, "E4475", {"start": v(-272.07, -361.92) * mm, "end": v(-241.99, -361.92) * mm});
            skLineSegment(sketch, "E4476", {"start": v(-241.99, -361.92) * mm, "end": v(-241.99, -370.04) * mm});
            skLineSegment(sketch, "E4477", {"start": v(-241.99, -370.04) * mm, "end": v(-262.57, -370.04) * mm});
            skLineSegment(sketch, "E4478", {"start": v(-262.57, -370.04) * mm, "end": v(-262.57, -380.64) * mm});
            skLineSegment(sketch, "E4479", {"start": v(-262.57, -380.64) * mm, "end": v(-243.15, -380.64) * mm});
            skLineSegment(sketch, "E4480", {"start": v(-243.15, -380.64) * mm, "end": v(-243.15, -388.16) * mm});
            skLineSegment(sketch, "E4481", {"start": v(-243.15, -388.16) * mm, "end": v(-262.57, -388.16) * mm});
            skLineSegment(sketch, "E4482", {"start": v(-262.57, -388.16) * mm, "end": v(-262.57, -399.21) * mm});
            skLineSegment(sketch, "E4483", {"start": v(-262.57, -399.21) * mm, "end": v(-241.99, -399.21) * mm});
            skLineSegment(sketch, "E4484", {"start": v(-241.99, -399.21) * mm, "end": v(-241.99, -407.33) * mm});
            skLineSegment(sketch, "E4485", {"start": v(-191.73, -369.6) * mm, "end": v(-183.49, -369.6) * mm});
            skLineSegment(sketch, "E4486", {"start": v(-183.49, -369.6) * mm, "end": v(-183.05, -369.6) * mm});
            skLineSegment(sketch, "E4487", {"start": v(-183.05, -369.6) * mm, "end": v(-182.63, -369.63) * mm});
            skLineSegment(sketch, "E4488", {"start": v(-182.63, -369.63) * mm, "end": v(-182.2, -369.67) * mm});
            skLineSegment(sketch, "E4489", {"start": v(-182.2, -369.67) * mm, "end": v(-181.8, -369.72) * mm});
            skLineSegment(sketch, "E4490", {"start": v(-181.8, -369.72) * mm, "end": v(-181.41, -369.8) * mm});
            skLineSegment(sketch, "E4491", {"start": v(-181.41, -369.8) * mm, "end": v(-181.03, -369.88) * mm});
            skLineSegment(sketch, "E4492", {"start": v(-181.03, -369.88) * mm, "end": v(-180.66, -369.98) * mm});
            skLineSegment(sketch, "E4493", {"start": v(-180.66, -369.98) * mm, "end": v(-180.3, -370.09) * mm});
            skLineSegment(sketch, "E4494", {"start": v(-180.3, -370.09) * mm, "end": v(-179.95, -370.22) * mm});
            skLineSegment(sketch, "E4495", {"start": v(-179.95, -370.22) * mm, "end": v(-179.62, -370.36) * mm});
            skLineSegment(sketch, "E4496", {"start": v(-179.62, -370.36) * mm, "end": v(-179.3, -370.51) * mm});
            skLineSegment(sketch, "E4497", {"start": v(-179.3, -370.51) * mm, "end": v(-178.99, -370.68) * mm});
            skLineSegment(sketch, "E4498", {"start": v(-178.99, -370.68) * mm, "end": v(-178.69, -370.86) * mm});
            skLineSegment(sketch, "E4499", {"start": v(-178.69, -370.86) * mm, "end": v(-178.4, -371.06) * mm});
            skLineSegment(sketch, "E4500", {"start": v(-178.4, -371.06) * mm, "end": v(-178.14, -371.27) * mm});
            skLineSegment(sketch, "E4501", {"start": v(-178.14, -371.27) * mm, "end": v(-177.88, -371.5) * mm});
            skLineSegment(sketch, "E4502", {"start": v(-177.88, -371.5) * mm, "end": v(-177.64, -371.72) * mm});
            skLineSegment(sketch, "E4503", {"start": v(-177.64, -371.72) * mm, "end": v(-177.41, -371.97) * mm});
            skLineSegment(sketch, "E4504", {"start": v(-177.41, -371.97) * mm, "end": v(-177.2, -372.23) * mm});
            skLineSegment(sketch, "E4505", {"start": v(-177.2, -372.23) * mm, "end": v(-177, -372.5) * mm});
            skLineSegment(sketch, "E4506", {"start": v(-177, -372.5) * mm, "end": v(-176.81, -372.78) * mm});
            skLineSegment(sketch, "E4507", {"start": v(-176.81, -372.78) * mm, "end": v(-176.64, -373.08) * mm});
            skLineSegment(sketch, "E4508", {"start": v(-176.64, -373.08) * mm, "end": v(-176.49, -373.38) * mm});
            skLineSegment(sketch, "E4509", {"start": v(-176.49, -373.38) * mm, "end": v(-176.35, -373.7) * mm});
            skLineSegment(sketch, "E4510", {"start": v(-176.35, -373.7) * mm, "end": v(-176.22, -374.03) * mm});
            skLineSegment(sketch, "E4511", {"start": v(-176.22, -374.03) * mm, "end": v(-176.12, -374.37) * mm});
            skLineSegment(sketch, "E4512", {"start": v(-176.12, -374.37) * mm, "end": v(-176.02, -374.72) * mm});
            skLineSegment(sketch, "E4513", {"start": v(-176.02, -374.72) * mm, "end": v(-175.95, -375.08) * mm});
            skLineSegment(sketch, "E4514", {"start": v(-175.95, -375.08) * mm, "end": v(-175.89, -375.45) * mm});
            skLineSegment(sketch, "E4515", {"start": v(-175.89, -375.45) * mm, "end": v(-175.85, -375.83) * mm});
            skLineSegment(sketch, "E4516", {"start": v(-175.85, -375.83) * mm, "end": v(-175.82, -376.22) * mm});
            skLineSegment(sketch, "E4517", {"start": v(-175.82, -376.22) * mm, "end": v(-175.81, -376.61) * mm});
            skLineSegment(sketch, "E4518", {"start": v(-175.81, -376.61) * mm, "end": v(-175.82, -377.02) * mm});
            skLineSegment(sketch, "E4519", {"start": v(-175.82, -377.02) * mm, "end": v(-175.85, -377.41) * mm});
            skLineSegment(sketch, "E4520", {"start": v(-175.85, -377.41) * mm, "end": v(-175.89, -377.8) * mm});
            skLineSegment(sketch, "E4521", {"start": v(-175.89, -377.8) * mm, "end": v(-175.94, -378.17) * mm});
            skLineSegment(sketch, "E4522", {"start": v(-175.94, -378.17) * mm, "end": v(-176.01, -378.53) * mm});
            skLineSegment(sketch, "E4523", {"start": v(-176.01, -378.53) * mm, "end": v(-176.1, -378.88) * mm});
            skLineSegment(sketch, "E4524", {"start": v(-176.1, -378.88) * mm, "end": v(-176.2, -379.22) * mm});
            skLineSegment(sketch, "E4525", {"start": v(-176.2, -379.22) * mm, "end": v(-176.32, -379.55) * mm});
            skLineSegment(sketch, "E4526", {"start": v(-176.32, -379.55) * mm, "end": v(-176.46, -379.86) * mm});
            skLineSegment(sketch, "E4527", {"start": v(-176.46, -379.86) * mm, "end": v(-176.6, -380.17) * mm});
            skLineSegment(sketch, "E4528", {"start": v(-176.6, -380.17) * mm, "end": v(-176.77, -380.46) * mm});
            skLineSegment(sketch, "E4529", {"start": v(-176.77, -380.46) * mm, "end": v(-176.95, -380.74) * mm});
            skLineSegment(sketch, "E4530", {"start": v(-176.95, -380.74) * mm, "end": v(-177.14, -381) * mm});
            skLineSegment(sketch, "E4531", {"start": v(-177.14, -381) * mm, "end": v(-177.35, -381.26) * mm});
            skLineSegment(sketch, "E4532", {"start": v(-177.35, -381.26) * mm, "end": v(-177.57, -381.5) * mm});
            skLineSegment(sketch, "E4533", {"start": v(-177.57, -381.5) * mm, "end": v(-177.8, -381.73) * mm});
            skLineSegment(sketch, "E4534", {"start": v(-177.8, -381.73) * mm, "end": v(-178.06, -381.95) * mm});
            skLineSegment(sketch, "E4535", {"start": v(-178.06, -381.95) * mm, "end": v(-178.32, -382.15) * mm});
            skLineSegment(sketch, "E4536", {"start": v(-178.32, -382.15) * mm, "end": v(-178.6, -382.35) * mm});
            skLineSegment(sketch, "E4537", {"start": v(-178.6, -382.35) * mm, "end": v(-178.9, -382.52) * mm});
            skLineSegment(sketch, "E4538", {"start": v(-178.9, -382.52) * mm, "end": v(-179.2, -382.69) * mm});
            skLineSegment(sketch, "E4539", {"start": v(-179.2, -382.69) * mm, "end": v(-179.52, -382.84) * mm});
            skLineSegment(sketch, "E4540", {"start": v(-179.52, -382.84) * mm, "end": v(-179.85, -382.98) * mm});
            skLineSegment(sketch, "E4541", {"start": v(-179.85, -382.98) * mm, "end": v(-180.2, -383.1) * mm});
            skLineSegment(sketch, "E4542", {"start": v(-180.2, -383.1) * mm, "end": v(-180.55, -383.2) * mm});
            skLineSegment(sketch, "E4543", {"start": v(-180.55, -383.2) * mm, "end": v(-180.92, -383.3) * mm});
            skLineSegment(sketch, "E4544", {"start": v(-180.92, -383.3) * mm, "end": v(-181.3, -383.38) * mm});
            skLineSegment(sketch, "E4545", {"start": v(-181.3, -383.38) * mm, "end": v(-181.7, -383.45) * mm});
            skLineSegment(sketch, "E4546", {"start": v(-181.7, -383.45) * mm, "end": v(-182.1, -383.5) * mm});
            skLineSegment(sketch, "E4547", {"start": v(-182.1, -383.5) * mm, "end": v(-182.52, -383.54) * mm});
            skLineSegment(sketch, "E4548", {"start": v(-182.52, -383.54) * mm, "end": v(-182.95, -383.56) * mm});
            skLineSegment(sketch, "E4549", {"start": v(-182.95, -383.56) * mm, "end": v(-183.4, -383.57) * mm});
            skLineSegment(sketch, "E4550", {"start": v(-183.4, -383.57) * mm, "end": v(-191.73, -383.57) * mm});
            skLineSegment(sketch, "E4551", {"start": v(-191.73, -383.57) * mm, "end": v(-191.73, -369.6) * mm});
            skLineSegment(sketch, "E4552", {"start": v(-191.73, -407.33) * mm, "end": v(-201.24, -407.33) * mm});
            skLineSegment(sketch, "E4553", {"start": v(-201.24, -407.33) * mm, "end": v(-201.24, -361.92) * mm});
            skLineSegment(sketch, "E4554", {"start": v(-201.24, -361.92) * mm, "end": v(-182.17, -361.92) * mm});
            skLineSegment(sketch, "E4555", {"start": v(-182.17, -361.92) * mm, "end": v(-181.24, -361.94) * mm});
            skLineSegment(sketch, "E4556", {"start": v(-181.24, -361.94) * mm, "end": v(-180.34, -361.99) * mm});
            skLineSegment(sketch, "E4557", {"start": v(-180.34, -361.99) * mm, "end": v(-179.46, -362.07) * mm});
            skLineSegment(sketch, "E4558", {"start": v(-179.46, -362.07) * mm, "end": v(-178.6, -362.18) * mm});
            skLineSegment(sketch, "E4559", {"start": v(-178.6, -362.18) * mm, "end": v(-177.78, -362.32) * mm});
            skLineSegment(sketch, "E4560", {"start": v(-177.78, -362.32) * mm, "end": v(-176.97, -362.5) * mm});
            skLineSegment(sketch, "E4561", {"start": v(-176.97, -362.5) * mm, "end": v(-176.2, -362.7) * mm});
            skLineSegment(sketch, "E4562", {"start": v(-176.2, -362.7) * mm, "end": v(-175.44, -362.93) * mm});
            skLineSegment(sketch, "E4563", {"start": v(-175.44, -362.93) * mm, "end": v(-174.71, -363.19) * mm});
            skLineSegment(sketch, "E4564", {"start": v(-174.71, -363.19) * mm, "end": v(-174, -363.48) * mm});
            skLineSegment(sketch, "E4565", {"start": v(-174, -363.48) * mm, "end": v(-173.33, -363.8) * mm});
            skLineSegment(sketch, "E4566", {"start": v(-173.33, -363.8) * mm, "end": v(-172.68, -364.15) * mm});
            skLineSegment(sketch, "E4567", {"start": v(-172.68, -364.15) * mm, "end": v(-172.06, -364.53) * mm});
            skLineSegment(sketch, "E4568", {"start": v(-172.06, -364.53) * mm, "end": v(-171.47, -364.93) * mm});
            skLineSegment(sketch, "E4569", {"start": v(-171.47, -364.93) * mm, "end": v(-170.9, -365.36) * mm});
            skLineSegment(sketch, "E4570", {"start": v(-170.9, -365.36) * mm, "end": v(-170.37, -365.82) * mm});
            skLineSegment(sketch, "E4571", {"start": v(-170.37, -365.82) * mm, "end": v(-169.86, -366.3) * mm});
            skLineSegment(sketch, "E4572", {"start": v(-169.86, -366.3) * mm, "end": v(-169.39, -366.81) * mm});
            skLineSegment(sketch, "E4573", {"start": v(-169.39, -366.81) * mm, "end": v(-168.94, -367.35) * mm});
            skLineSegment(sketch, "E4574", {"start": v(-168.94, -367.35) * mm, "end": v(-168.52, -367.91) * mm});
            skLineSegment(sketch, "E4575", {"start": v(-168.52, -367.91) * mm, "end": v(-168.14, -368.5) * mm});
            skLineSegment(sketch, "E4576", {"start": v(-168.14, -368.5) * mm, "end": v(-167.78, -369.1) * mm});
            skLineSegment(sketch, "E4577", {"start": v(-167.78, -369.1) * mm, "end": v(-167.46, -369.74) * mm});
            skLineSegment(sketch, "E4578", {"start": v(-167.46, -369.74) * mm, "end": v(-167.17, -370.4) * mm});
            skLineSegment(sketch, "E4579", {"start": v(-167.17, -370.4) * mm, "end": v(-166.91, -371.09) * mm});
            skLineSegment(sketch, "E4580", {"start": v(-166.91, -371.09) * mm, "end": v(-166.69, -371.8) * mm});
            skLineSegment(sketch, "E4581", {"start": v(-166.69, -371.8) * mm, "end": v(-166.5, -372.52) * mm});
            skLineSegment(sketch, "E4582", {"start": v(-166.5, -372.52) * mm, "end": v(-166.34, -373.27) * mm});
            skLineSegment(sketch, "E4583", {"start": v(-166.34, -373.27) * mm, "end": v(-166.21, -374.04) * mm});
            skLineSegment(sketch, "E4584", {"start": v(-166.21, -374.04) * mm, "end": v(-166.13, -374.84) * mm});
            skLineSegment(sketch, "E4585", {"start": v(-166.13, -374.84) * mm, "end": v(-166.07, -375.65) * mm});
            skLineSegment(sketch, "E4586", {"start": v(-166.07, -375.65) * mm, "end": v(-166.05, -376.49) * mm});
            skLineSegment(sketch, "E4587", {"start": v(-166.05, -376.49) * mm, "end": v(-166.06, -377.03) * mm});
            skLineSegment(sketch, "E4588", {"start": v(-166.06, -377.03) * mm, "end": v(-166.09, -377.56) * mm});
            skLineSegment(sketch, "E4589", {"start": v(-166.09, -377.56) * mm, "end": v(-166.13, -378.1) * mm});
            skLineSegment(sketch, "E4590", {"start": v(-166.13, -378.1) * mm, "end": v(-166.2, -378.62) * mm});
            skLineSegment(sketch, "E4591", {"start": v(-166.2, -378.62) * mm, "end": v(-166.27, -379.14) * mm});
            skLineSegment(sketch, "E4592", {"start": v(-166.27, -379.14) * mm, "end": v(-166.37, -379.65) * mm});
            skLineSegment(sketch, "E4593", {"start": v(-166.37, -379.65) * mm, "end": v(-166.48, -380.16) * mm});
            skLineSegment(sketch, "E4594", {"start": v(-166.48, -380.16) * mm, "end": v(-166.6, -380.66) * mm});
            skLineSegment(sketch, "E4595", {"start": v(-166.6, -380.66) * mm, "end": v(-166.75, -381.15) * mm});
            skLineSegment(sketch, "E4596", {"start": v(-166.75, -381.15) * mm, "end": v(-166.91, -381.63) * mm});
            skLineSegment(sketch, "E4597", {"start": v(-166.91, -381.63) * mm, "end": v(-167.1, -382.1) * mm});
            skLineSegment(sketch, "E4598", {"start": v(-167.1, -382.1) * mm, "end": v(-167.29, -382.57) * mm});
            skLineSegment(sketch, "E4599", {"start": v(-167.29, -382.57) * mm, "end": v(-167.5, -383.02) * mm});
            skLineSegment(sketch, "E4600", {"start": v(-167.5, -383.02) * mm, "end": v(-167.72, -383.47) * mm});
            skLineSegment(sketch, "E4601", {"start": v(-167.72, -383.47) * mm, "end": v(-167.96, -383.9) * mm});
            skLineSegment(sketch, "E4602", {"start": v(-167.96, -383.9) * mm, "end": v(-168.22, -384.33) * mm});
            skLineSegment(sketch, "E4603", {"start": v(-168.22, -384.33) * mm, "end": v(-168.49, -384.75) * mm});
            skLineSegment(sketch, "E4604", {"start": v(-168.49, -384.75) * mm, "end": v(-168.78, -385.15) * mm});
            skLineSegment(sketch, "E4605", {"start": v(-168.78, -385.15) * mm, "end": v(-169.08, -385.54) * mm});
            skLineSegment(sketch, "E4606", {"start": v(-169.08, -385.54) * mm, "end": v(-169.4, -385.92) * mm});
            skLineSegment(sketch, "E4607", {"start": v(-169.4, -385.92) * mm, "end": v(-169.73, -386.3) * mm});
            skLineSegment(sketch, "E4608", {"start": v(-169.73, -386.3) * mm, "end": v(-170.07, -386.64) * mm});
            skLineSegment(sketch, "E4609", {"start": v(-170.07, -386.64) * mm, "end": v(-170.43, -386.99) * mm});
            skLineSegment(sketch, "E4610", {"start": v(-170.43, -386.99) * mm, "end": v(-170.8, -387.31) * mm});
            skLineSegment(sketch, "E4611", {"start": v(-170.8, -387.31) * mm, "end": v(-171.2, -387.63) * mm});
            skLineSegment(sketch, "E4612", {"start": v(-171.2, -387.63) * mm, "end": v(-171.6, -387.92) * mm});
            skLineSegment(sketch, "E4613", {"start": v(-171.6, -387.92) * mm, "end": v(-172.02, -388.2) * mm});
            skLineSegment(sketch, "E4614", {"start": v(-172.02, -388.2) * mm, "end": v(-172.45, -388.48) * mm});
            skLineSegment(sketch, "E4615", {"start": v(-172.45, -388.48) * mm, "end": v(-172.9, -388.73) * mm});
            skLineSegment(sketch, "E4616", {"start": v(-172.9, -388.73) * mm, "end": v(-173.35, -388.97) * mm});
            skLineSegment(sketch, "E4617", {"start": v(-173.35, -388.97) * mm, "end": v(-173.82, -389.19) * mm});
            skLineSegment(sketch, "E4618", {"start": v(-173.82, -389.19) * mm, "end": v(-174.3, -389.4) * mm});
            skLineSegment(sketch, "E4619", {"start": v(-174.3, -389.4) * mm, "end": v(-164.73, -407.33) * mm});
            skLineSegment(sketch, "E4620", {"start": v(-164.73, -407.33) * mm, "end": v(-175.5, -407.33) * mm});
            skLineSegment(sketch, "E4621", {"start": v(-175.5, -407.33) * mm, "end": v(-183.96, -390.87) * mm});
            skLineSegment(sketch, "E4622", {"start": v(-183.96, -390.87) * mm, "end": v(-191.73, -390.87) * mm});
            skLineSegment(sketch, "E4623", {"start": v(-191.73, -390.87) * mm, "end": v(-191.73, -407.33) * mm});
            skLineSegment(sketch, "E4624", {"start": v(-118.6, -394.7) * mm, "end": v(-118.55, -395.05) * mm});
            skLineSegment(sketch, "E4625", {"start": v(-118.55, -395.05) * mm, "end": v(-118.48, -395.38) * mm});
            skLineSegment(sketch, "E4626", {"start": v(-118.48, -395.38) * mm, "end": v(-118.4, -395.7) * mm});
            skLineSegment(sketch, "E4627", {"start": v(-118.4, -395.7) * mm, "end": v(-118.29, -396.03) * mm});
            skLineSegment(sketch, "E4628", {"start": v(-118.29, -396.03) * mm, "end": v(-118.16, -396.33) * mm});
            skLineSegment(sketch, "E4629", {"start": v(-118.16, -396.33) * mm, "end": v(-118.02, -396.63) * mm});
            skLineSegment(sketch, "E4630", {"start": v(-118.02, -396.63) * mm, "end": v(-117.86, -396.92) * mm});
            skLineSegment(sketch, "E4631", {"start": v(-117.86, -396.92) * mm, "end": v(-117.69, -397.2) * mm});
            skLineSegment(sketch, "E4632", {"start": v(-117.69, -397.2) * mm, "end": v(-117.5, -397.48) * mm});
            skLineSegment(sketch, "E4633", {"start": v(-117.5, -397.48) * mm, "end": v(-117.28, -397.74) * mm});
            skLineSegment(sketch, "E4634", {"start": v(-117.28, -397.74) * mm, "end": v(-117.06, -398) * mm});
            skLineSegment(sketch, "E4635", {"start": v(-117.06, -398) * mm, "end": v(-116.81, -398.24) * mm});
            skLineSegment(sketch, "E4636", {"start": v(-116.81, -398.24) * mm, "end": v(-116.56, -398.47) * mm});
            skLineSegment(sketch, "E4637", {"start": v(-116.56, -398.47) * mm, "end": v(-116.28, -398.7) * mm});
            skLineSegment(sketch, "E4638", {"start": v(-116.28, -398.7) * mm, "end": v(-116, -398.9) * mm});
            skLineSegment(sketch, "E4639", {"start": v(-116, -398.9) * mm, "end": v(-115.7, -399.11) * mm});
            skLineSegment(sketch, "E4640", {"start": v(-115.7, -399.11) * mm, "end": v(-115.38, -399.3) * mm});
            skLineSegment(sketch, "E4641", {"start": v(-115.38, -399.3) * mm, "end": v(-115.05, -399.48) * mm});
            skLineSegment(sketch, "E4642", {"start": v(-115.05, -399.48) * mm, "end": v(-114.7, -399.65) * mm});
            skLineSegment(sketch, "E4643", {"start": v(-114.7, -399.65) * mm, "end": v(-114.34, -399.81) * mm});
            skLineSegment(sketch, "E4644", {"start": v(-114.34, -399.81) * mm, "end": v(-113.97, -399.96) * mm});
            skLineSegment(sketch, "E4645", {"start": v(-113.97, -399.96) * mm, "end": v(-113.59, -400.1) * mm});
            skLineSegment(sketch, "E4646", {"start": v(-113.59, -400.1) * mm, "end": v(-113.19, -400.21) * mm});
            skLineSegment(sketch, "E4647", {"start": v(-113.19, -400.21) * mm, "end": v(-112.78, -400.33) * mm});
            skLineSegment(sketch, "E4648", {"start": v(-112.78, -400.33) * mm, "end": v(-111.93, -400.5) * mm});
            skLineSegment(sketch, "E4649", {"start": v(-111.93, -400.5) * mm, "end": v(-111.03, -400.64) * mm});
            skLineSegment(sketch, "E4650", {"start": v(-111.03, -400.64) * mm, "end": v(-110.08, -400.72) * mm});
            skLineSegment(sketch, "E4651", {"start": v(-110.08, -400.72) * mm, "end": v(-109.1, -400.75) * mm});
            skLineSegment(sketch, "E4652", {"start": v(-109.1, -400.75) * mm, "end": v(-108.2, -400.72) * mm});
            skLineSegment(sketch, "E4653", {"start": v(-108.2, -400.72) * mm, "end": v(-107.32, -400.64) * mm});
            skLineSegment(sketch, "E4654", {"start": v(-107.32, -400.64) * mm, "end": v(-106.49, -400.5) * mm});
            skLineSegment(sketch, "E4655", {"start": v(-106.49, -400.5) * mm, "end": v(-105.7, -400.32) * mm});
            skLineSegment(sketch, "E4656", {"start": v(-105.7, -400.32) * mm, "end": v(-104.96, -400.1) * mm});
            skLineSegment(sketch, "E4657", {"start": v(-104.96, -400.1) * mm, "end": v(-104.6, -399.96) * mm});
            skLineSegment(sketch, "E4658", {"start": v(-104.6, -399.96) * mm, "end": v(-104.26, -399.81) * mm});
            skLineSegment(sketch, "E4659", {"start": v(-104.26, -399.81) * mm, "end": v(-103.93, -399.66) * mm});
            skLineSegment(sketch, "E4660", {"start": v(-103.93, -399.66) * mm, "end": v(-103.62, -399.5) * mm});
            skLineSegment(sketch, "E4661", {"start": v(-103.62, -399.5) * mm, "end": v(-103.32, -399.31) * mm});
            skLineSegment(sketch, "E4662", {"start": v(-103.32, -399.31) * mm, "end": v(-103.03, -399.13) * mm});
            skLineSegment(sketch, "E4663", {"start": v(-103.03, -399.13) * mm, "end": v(-102.76, -398.93) * mm});
            skLineSegment(sketch, "E4664", {"start": v(-102.76, -398.93) * mm, "end": v(-102.5, -398.72) * mm});
            skLineSegment(sketch, "E4665", {"start": v(-102.5, -398.72) * mm, "end": v(-102.26, -398.5) * mm});
            skLineSegment(sketch, "E4666", {"start": v(-102.26, -398.5) * mm, "end": v(-102.03, -398.28) * mm});
            skLineSegment(sketch, "E4667", {"start": v(-102.03, -398.28) * mm, "end": v(-101.82, -398.04) * mm});
            skLineSegment(sketch, "E4668", {"start": v(-101.82, -398.04) * mm, "end": v(-101.63, -397.8) * mm});
            skLineSegment(sketch, "E4669", {"start": v(-101.63, -397.8) * mm, "end": v(-101.45, -397.55) * mm});
            skLineSegment(sketch, "E4670", {"start": v(-101.45, -397.55) * mm, "end": v(-101.29, -397.29) * mm});
            skLineSegment(sketch, "E4671", {"start": v(-101.29, -397.29) * mm, "end": v(-101.15, -397.02) * mm});
            skLineSegment(sketch, "E4672", {"start": v(-101.15, -397.02) * mm, "end": v(-101.02, -396.74) * mm});
            skLineSegment(sketch, "E4673", {"start": v(-101.02, -396.74) * mm, "end": v(-100.92, -396.46) * mm});
            skLineSegment(sketch, "E4674", {"start": v(-100.92, -396.46) * mm, "end": v(-100.83, -396.16) * mm});
            skLineSegment(sketch, "E4675", {"start": v(-100.83, -396.16) * mm, "end": v(-100.76, -395.87) * mm});
            skLineSegment(sketch, "E4676", {"start": v(-100.76, -395.87) * mm, "end": v(-100.7, -395.56) * mm});
            skLineSegment(sketch, "E4677", {"start": v(-100.7, -395.56) * mm, "end": v(-100.68, -395.25) * mm});
            skLineSegment(sketch, "E4678", {"start": v(-100.68, -395.25) * mm, "end": v(-100.67, -394.93) * mm});
            skLineSegment(sketch, "E4679", {"start": v(-100.67, -394.93) * mm, "end": v(-100.7, -394.4) * mm});
            skLineSegment(sketch, "E4680", {"start": v(-100.7, -394.4) * mm, "end": v(-100.78, -393.9) * mm});
            skLineSegment(sketch, "E4681", {"start": v(-100.78, -393.9) * mm, "end": v(-100.84, -393.66) * mm});
            skLineSegment(sketch, "E4682", {"start": v(-100.84, -393.66) * mm, "end": v(-100.91, -393.43) * mm});
            skLineSegment(sketch, "E4683", {"start": v(-100.91, -393.43) * mm, "end": v(-101, -393.2) * mm});
            skLineSegment(sketch, "E4684", {"start": v(-101, -393.2) * mm, "end": v(-101.1, -392.98) * mm});
            skLineSegment(sketch, "E4685", {"start": v(-101.1, -392.98) * mm, "end": v(-101.23, -392.76) * mm});
            skLineSegment(sketch, "E4686", {"start": v(-101.23, -392.76) * mm, "end": v(-101.36, -392.55) * mm});
            skLineSegment(sketch, "E4687", {"start": v(-101.36, -392.55) * mm, "end": v(-101.51, -392.35) * mm});
            skLineSegment(sketch, "E4688", {"start": v(-101.51, -392.35) * mm, "end": v(-101.68, -392.15) * mm});
            skLineSegment(sketch, "E4689", {"start": v(-101.68, -392.15) * mm, "end": v(-102.05, -391.77) * mm});
            skLineSegment(sketch, "E4690", {"start": v(-102.05, -391.77) * mm, "end": v(-102.5, -391.41) * mm});
            skLineSegment(sketch, "E4691", {"start": v(-102.5, -391.41) * mm, "end": v(-103, -391.08) * mm});
            skLineSegment(sketch, "E4692", {"start": v(-103, -391.08) * mm, "end": v(-103.57, -390.76) * mm});
            skLineSegment(sketch, "E4693", {"start": v(-103.57, -390.76) * mm, "end": v(-104.22, -390.45) * mm});
            skLineSegment(sketch, "E4694", {"start": v(-104.22, -390.45) * mm, "end": v(-104.93, -390.17) * mm});
            skLineSegment(sketch, "E4695", {"start": v(-104.93, -390.17) * mm, "end": v(-105.7, -389.9) * mm});
            skLineSegment(sketch, "E4696", {"start": v(-105.7, -389.9) * mm, "end": v(-106.57, -389.64) * mm});
            skLineSegment(sketch, "E4697", {"start": v(-106.57, -389.64) * mm, "end": v(-107.5, -389.4) * mm});
            skLineSegment(sketch, "E4698", {"start": v(-107.5, -389.4) * mm, "end": v(-108.5, -389.17) * mm});
            skLineSegment(sketch, "E4699", {"start": v(-108.5, -389.17) * mm, "end": v(-114.42, -387.91) * mm});
            skLineSegment(sketch, "E4700", {"start": v(-114.42, -387.91) * mm, "end": v(-115.18, -387.74) * mm});
            skLineSegment(sketch, "E4701", {"start": v(-115.18, -387.74) * mm, "end": v(-115.92, -387.56) * mm});
            skLineSegment(sketch, "E4702", {"start": v(-115.92, -387.56) * mm, "end": v(-116.63, -387.36) * mm});
            skLineSegment(sketch, "E4703", {"start": v(-116.63, -387.36) * mm, "end": v(-117.32, -387.14) * mm});
            skLineSegment(sketch, "E4704", {"start": v(-117.32, -387.14) * mm, "end": v(-117.99, -386.91) * mm});
            skLineSegment(sketch, "E4705", {"start": v(-117.99, -386.91) * mm, "end": v(-118.63, -386.67) * mm});
            skLineSegment(sketch, "E4706", {"start": v(-118.63, -386.67) * mm, "end": v(-119.25, -386.4) * mm});
            skLineSegment(sketch, "E4707", {"start": v(-119.25, -386.4) * mm, "end": v(-119.84, -386.13) * mm});
            skLineSegment(sketch, "E4708", {"start": v(-119.84, -386.13) * mm, "end": v(-120.4, -385.84) * mm});
            skLineSegment(sketch, "E4709", {"start": v(-120.4, -385.84) * mm, "end": v(-120.95, -385.53) * mm});
            skLineSegment(sketch, "E4710", {"start": v(-120.95, -385.53) * mm, "end": v(-121.46, -385.21) * mm});
            skLineSegment(sketch, "E4711", {"start": v(-121.46, -385.21) * mm, "end": v(-121.96, -384.87) * mm});
            skLineSegment(sketch, "E4712", {"start": v(-121.96, -384.87) * mm, "end": v(-122.43, -384.52) * mm});
            skLineSegment(sketch, "E4713", {"start": v(-122.43, -384.52) * mm, "end": v(-122.87, -384.16) * mm});
            skLineSegment(sketch, "E4714", {"start": v(-122.87, -384.16) * mm, "end": v(-123.3, -383.77) * mm});
            skLineSegment(sketch, "E4715", {"start": v(-123.3, -383.77) * mm, "end": v(-123.69, -383.38) * mm});
            skLineSegment(sketch, "E4716", {"start": v(-123.69, -383.38) * mm, "end": v(-124.06, -382.96) * mm});
            skLineSegment(sketch, "E4717", {"start": v(-124.06, -382.96) * mm, "end": v(-124.4, -382.54) * mm});
            skLineSegment(sketch, "E4718", {"start": v(-124.4, -382.54) * mm, "end": v(-124.73, -382.1) * mm});
            skLineSegment(sketch, "E4719", {"start": v(-124.73, -382.1) * mm, "end": v(-125.03, -381.63) * mm});
            skLineSegment(sketch, "E4720", {"start": v(-125.03, -381.63) * mm, "end": v(-125.3, -381.16) * mm});
            skLineSegment(sketch, "E4721", {"start": v(-125.3, -381.16) * mm, "end": v(-125.56, -380.67) * mm});
            skLineSegment(sketch, "E4722", {"start": v(-125.56, -380.67) * mm, "end": v(-125.79, -380.17) * mm});
            skLineSegment(sketch, "E4723", {"start": v(-125.79, -380.17) * mm, "end": v(-125.99, -379.65) * mm});
            skLineSegment(sketch, "E4724", {"start": v(-125.99, -379.65) * mm, "end": v(-126.17, -379.12) * mm});
            skLineSegment(sketch, "E4725", {"start": v(-126.17, -379.12) * mm, "end": v(-126.32, -378.57) * mm});
            skLineSegment(sketch, "E4726", {"start": v(-126.32, -378.57) * mm, "end": v(-126.46, -378) * mm});
            skLineSegment(sketch, "E4727", {"start": v(-126.46, -378) * mm, "end": v(-126.56, -377.42) * mm});
            skLineSegment(sketch, "E4728", {"start": v(-126.56, -377.42) * mm, "end": v(-126.65, -376.82) * mm});
            skLineSegment(sketch, "E4729", {"start": v(-126.65, -376.82) * mm, "end": v(-126.7, -376.21) * mm});
            skLineSegment(sketch, "E4730", {"start": v(-126.7, -376.21) * mm, "end": v(-126.74, -375.59) * mm});
            skLineSegment(sketch, "E4731", {"start": v(-126.74, -375.59) * mm, "end": v(-126.75, -374.95) * mm});
            skLineSegment(sketch, "E4732", {"start": v(-126.75, -374.95) * mm, "end": v(-126.73, -374.15) * mm});
            skLineSegment(sketch, "E4733", {"start": v(-126.73, -374.15) * mm, "end": v(-126.67, -373.38) * mm});
            skLineSegment(sketch, "E4734", {"start": v(-126.67, -373.38) * mm, "end": v(-126.57, -372.62) * mm});
            skLineSegment(sketch, "E4735", {"start": v(-126.57, -372.62) * mm, "end": v(-126.44, -371.88) * mm});
            skLineSegment(sketch, "E4736", {"start": v(-126.44, -371.88) * mm, "end": v(-126.26, -371.16) * mm});
            skLineSegment(sketch, "E4737", {"start": v(-126.26, -371.16) * mm, "end": v(-126.05, -370.46) * mm});
            skLineSegment(sketch, "E4738", {"start": v(-126.05, -370.46) * mm, "end": v(-125.8, -369.78) * mm});
            skLineSegment(sketch, "E4739", {"start": v(-125.8, -369.78) * mm, "end": v(-125.51, -369.12) * mm});
            skLineSegment(sketch, "E4740", {"start": v(-125.51, -369.12) * mm, "end": v(-125.2, -368.48) * mm});
            skLineSegment(sketch, "E4741", {"start": v(-125.2, -368.48) * mm, "end": v(-124.84, -367.86) * mm});
            skLineSegment(sketch, "E4742", {"start": v(-124.84, -367.86) * mm, "end": v(-124.44, -367.27) * mm});
            skLineSegment(sketch, "E4743", {"start": v(-124.44, -367.27) * mm, "end": v(-124.02, -366.7) * mm});
            skLineSegment(sketch, "E4744", {"start": v(-124.02, -366.7) * mm, "end": v(-123.56, -366.15) * mm});
            skLineSegment(sketch, "E4745", {"start": v(-123.56, -366.15) * mm, "end": v(-123.07, -365.62) * mm});
            skLineSegment(sketch, "E4746", {"start": v(-123.07, -365.62) * mm, "end": v(-122.55, -365.12) * mm});
            skLineSegment(sketch, "E4747", {"start": v(-122.55, -365.12) * mm, "end": v(-122, -364.64) * mm});
            skLineSegment(sketch, "E4748", {"start": v(-122, -364.64) * mm, "end": v(-121.41, -364.19) * mm});
            skLineSegment(sketch, "E4749", {"start": v(-121.41, -364.19) * mm, "end": v(-120.8, -363.76) * mm});
            skLineSegment(sketch, "E4750", {"start": v(-120.8, -363.76) * mm, "end": v(-120.16, -363.36) * mm});
            skLineSegment(sketch, "E4751", {"start": v(-120.16, -363.36) * mm, "end": v(-119.48, -362.99) * mm});
            skLineSegment(sketch, "E4752", {"start": v(-119.48, -362.99) * mm, "end": v(-118.78, -362.64) * mm});
            skLineSegment(sketch, "E4753", {"start": v(-118.78, -362.64) * mm, "end": v(-118.06, -362.32) * mm});
            skLineSegment(sketch, "E4754", {"start": v(-118.06, -362.32) * mm, "end": v(-117.3, -362.03) * mm});
            skLineSegment(sketch, "E4755", {"start": v(-117.3, -362.03) * mm, "end": v(-116.52, -361.77) * mm});
            skLineSegment(sketch, "E4756", {"start": v(-116.52, -361.77) * mm, "end": v(-115.71, -361.54) * mm});
            skLineSegment(sketch, "E4757", {"start": v(-115.71, -361.54) * mm, "end": v(-114.88, -361.33) * mm});
            skLineSegment(sketch, "E4758", {"start": v(-114.88, -361.33) * mm, "end": v(-114.02, -361.16) * mm});
            skLineSegment(sketch, "E4759", {"start": v(-114.02, -361.16) * mm, "end": v(-113.14, -361.01) * mm});
            skLineSegment(sketch, "E4760", {"start": v(-113.14, -361.01) * mm, "end": v(-112.23, -360.9) * mm});
            skLineSegment(sketch, "E4761", {"start": v(-112.23, -360.9) * mm, "end": v(-111.3, -360.82) * mm});
            skLineSegment(sketch, "E4762", {"start": v(-111.3, -360.82) * mm, "end": v(-110.35, -360.77) * mm});
            skLineSegment(sketch, "E4763", {"start": v(-110.35, -360.77) * mm, "end": v(-109.38, -360.76) * mm});
            skLineSegment(sketch, "E4764", {"start": v(-109.38, -360.76) * mm, "end": v(-108.45, -360.77) * mm});
            skLineSegment(sketch, "E4765", {"start": v(-108.45, -360.77) * mm, "end": v(-107.54, -360.82) * mm});
            skLineSegment(sketch, "E4766", {"start": v(-107.54, -360.82) * mm, "end": v(-106.65, -360.9) * mm});
            skLineSegment(sketch, "E4767", {"start": v(-106.65, -360.9) * mm, "end": v(-105.78, -361.01) * mm});
            skLineSegment(sketch, "E4768", {"start": v(-105.78, -361.01) * mm, "end": v(-104.92, -361.15) * mm});
            skLineSegment(sketch, "E4769", {"start": v(-104.92, -361.15) * mm, "end": v(-104.09, -361.33) * mm});
            skLineSegment(sketch, "E4770", {"start": v(-104.09, -361.33) * mm, "end": v(-103.28, -361.53) * mm});
            skLineSegment(sketch, "E4771", {"start": v(-103.28, -361.53) * mm, "end": v(-102.49, -361.76) * mm});
            skLineSegment(sketch, "E4772", {"start": v(-102.49, -361.76) * mm, "end": v(-101.72, -362.02) * mm});
            skLineSegment(sketch, "E4773", {"start": v(-101.72, -362.02) * mm, "end": v(-100.98, -362.3) * mm});
            skLineSegment(sketch, "E4774", {"start": v(-100.98, -362.3) * mm, "end": v(-100.26, -362.61) * mm});
            skLineSegment(sketch, "E4775", {"start": v(-100.26, -362.61) * mm, "end": v(-99.56, -362.95) * mm});
            skLineSegment(sketch, "E4776", {"start": v(-99.56, -362.95) * mm, "end": v(-98.9, -363.32) * mm});
            skLineSegment(sketch, "E4777", {"start": v(-98.9, -363.32) * mm, "end": v(-98.25, -363.71) * mm});
            skLineSegment(sketch, "E4778", {"start": v(-98.25, -363.71) * mm, "end": v(-97.64, -364.13) * mm});
            skLineSegment(sketch, "E4779", {"start": v(-97.64, -364.13) * mm, "end": v(-97.05, -364.57) * mm});
            skLineSegment(sketch, "E4780", {"start": v(-97.05, -364.57) * mm, "end": v(-96.5, -365.03) * mm});
            skLineSegment(sketch, "E4781", {"start": v(-96.5, -365.03) * mm, "end": v(-95.96, -365.52) * mm});
            skLineSegment(sketch, "E4782", {"start": v(-95.96, -365.52) * mm, "end": v(-95.46, -366.03) * mm});
            skLineSegment(sketch, "E4783", {"start": v(-95.46, -366.03) * mm, "end": v(-95, -366.56) * mm});
            skLineSegment(sketch, "E4784", {"start": v(-95, -366.56) * mm, "end": v(-94.56, -367.11) * mm});
            skLineSegment(sketch, "E4785", {"start": v(-94.56, -367.11) * mm, "end": v(-94.15, -367.69) * mm});
            skLineSegment(sketch, "E4786", {"start": v(-94.15, -367.69) * mm, "end": v(-93.78, -368.28) * mm});
            skLineSegment(sketch, "E4787", {"start": v(-93.78, -368.28) * mm, "end": v(-93.44, -368.9) * mm});
            skLineSegment(sketch, "E4788", {"start": v(-93.44, -368.9) * mm, "end": v(-93.13, -369.53) * mm});
            skLineSegment(sketch, "E4789", {"start": v(-93.13, -369.53) * mm, "end": v(-92.86, -370.18) * mm});
            skLineSegment(sketch, "E4790", {"start": v(-92.86, -370.18) * mm, "end": v(-92.63, -370.85) * mm});
            skLineSegment(sketch, "E4791", {"start": v(-92.63, -370.85) * mm, "end": v(-92.43, -371.53) * mm});
            skLineSegment(sketch, "E4792", {"start": v(-92.43, -371.53) * mm, "end": v(-92.27, -372.24) * mm});
            skLineSegment(sketch, "E4793", {"start": v(-92.27, -372.24) * mm, "end": v(-92.14, -372.96) * mm});
            skLineSegment(sketch, "E4794", {"start": v(-92.14, -372.96) * mm, "end": v(-92.06, -373.7) * mm});
            skLineSegment(sketch, "E4795", {"start": v(-92.06, -373.7) * mm, "end": v(-92.01, -374.44) * mm});
            skLineSegment(sketch, "E4796", {"start": v(-92.01, -374.44) * mm, "end": v(-100.95, -374.44) * mm});
            skLineSegment(sketch, "E4797", {"start": v(-100.95, -374.44) * mm, "end": v(-101, -374.11) * mm});
            skLineSegment(sketch, "E4798", {"start": v(-101, -374.11) * mm, "end": v(-101.07, -373.79) * mm});
            skLineSegment(sketch, "E4799", {"start": v(-101.07, -373.79) * mm, "end": v(-101.15, -373.47) * mm});
            skLineSegment(sketch, "E4800", {"start": v(-101.15, -373.47) * mm, "end": v(-101.25, -373.16) * mm});
            skLineSegment(sketch, "E4801", {"start": v(-101.25, -373.16) * mm, "end": v(-101.36, -372.85) * mm});
            skLineSegment(sketch, "E4802", {"start": v(-101.36, -372.85) * mm, "end": v(-101.5, -372.56) * mm});
            skLineSegment(sketch, "E4803", {"start": v(-101.5, -372.56) * mm, "end": v(-101.64, -372.27) * mm});
            skLineSegment(sketch, "E4804", {"start": v(-101.64, -372.27) * mm, "end": v(-101.8, -372) * mm});
            skLineSegment(sketch, "E4805", {"start": v(-101.8, -372) * mm, "end": v(-101.97, -371.73) * mm});
            skLineSegment(sketch, "E4806", {"start": v(-101.97, -371.73) * mm, "end": v(-102.16, -371.47) * mm});
            skLineSegment(sketch, "E4807", {"start": v(-102.16, -371.47) * mm, "end": v(-102.36, -371.22) * mm});
            skLineSegment(sketch, "E4808", {"start": v(-102.36, -371.22) * mm, "end": v(-102.58, -370.98) * mm});
            skLineSegment(sketch, "E4809", {"start": v(-102.58, -370.98) * mm, "end": v(-102.81, -370.74) * mm});
            skLineSegment(sketch, "E4810", {"start": v(-102.81, -370.74) * mm, "end": v(-103.05, -370.52) * mm});
            skLineSegment(sketch, "E4811", {"start": v(-103.05, -370.52) * mm, "end": v(-103.3, -370.31) * mm});
            skLineSegment(sketch, "E4812", {"start": v(-103.3, -370.31) * mm, "end": v(-103.58, -370.1) * mm});
            skLineSegment(sketch, "E4813", {"start": v(-103.58, -370.1) * mm, "end": v(-103.86, -369.92) * mm});
            skLineSegment(sketch, "E4814", {"start": v(-103.86, -369.92) * mm, "end": v(-104.15, -369.74) * mm});
            skLineSegment(sketch, "E4815", {"start": v(-104.15, -369.74) * mm, "end": v(-104.45, -369.57) * mm});
            skLineSegment(sketch, "E4816", {"start": v(-104.45, -369.57) * mm, "end": v(-104.77, -369.41) * mm});
            skLineSegment(sketch, "E4817", {"start": v(-104.77, -369.41) * mm, "end": v(-105.43, -369.13) * mm});
            skLineSegment(sketch, "E4818", {"start": v(-105.43, -369.13) * mm, "end": v(-106.14, -368.9) * mm});
            skLineSegment(sketch, "E4819", {"start": v(-106.14, -368.9) * mm, "end": v(-106.88, -368.7) * mm});
            skLineSegment(sketch, "E4820", {"start": v(-106.88, -368.7) * mm, "end": v(-107.66, -368.57) * mm});
            skLineSegment(sketch, "E4821", {"start": v(-107.66, -368.57) * mm, "end": v(-108.47, -368.5) * mm});
            skLineSegment(sketch, "E4822", {"start": v(-108.47, -368.5) * mm, "end": v(-109.32, -368.46) * mm});
            skLineSegment(sketch, "E4823", {"start": v(-109.32, -368.46) * mm, "end": v(-110.2, -368.5) * mm});
            skLineSegment(sketch, "E4824", {"start": v(-110.2, -368.5) * mm, "end": v(-111.02, -368.57) * mm});
            skLineSegment(sketch, "E4825", {"start": v(-111.02, -368.57) * mm, "end": v(-111.81, -368.7) * mm});
            skLineSegment(sketch, "E4826", {"start": v(-111.81, -368.7) * mm, "end": v(-112.56, -368.86) * mm});
            skLineSegment(sketch, "E4827", {"start": v(-112.56, -368.86) * mm, "end": v(-113.26, -369.08) * mm});
            skLineSegment(sketch, "E4828", {"start": v(-113.26, -369.08) * mm, "end": v(-113.9, -369.34) * mm});
            skLineSegment(sketch, "E4829", {"start": v(-113.9, -369.34) * mm, "end": v(-114.21, -369.5) * mm});
            skLineSegment(sketch, "E4830", {"start": v(-114.21, -369.5) * mm, "end": v(-114.5, -369.65) * mm});
            skLineSegment(sketch, "E4831", {"start": v(-114.5, -369.65) * mm, "end": v(-114.79, -369.82) * mm});
            skLineSegment(sketch, "E4832", {"start": v(-114.79, -369.82) * mm, "end": v(-115.05, -370) * mm});
            skLineSegment(sketch, "E4833", {"start": v(-115.05, -370) * mm, "end": v(-115.3, -370.19) * mm});
            skLineSegment(sketch, "E4834", {"start": v(-115.3, -370.19) * mm, "end": v(-115.54, -370.39) * mm});
            skLineSegment(sketch, "E4835", {"start": v(-115.54, -370.39) * mm, "end": v(-115.76, -370.6) * mm});
            skLineSegment(sketch, "E4836", {"start": v(-115.76, -370.6) * mm, "end": v(-115.97, -370.82) * mm});
            skLineSegment(sketch, "E4837", {"start": v(-115.97, -370.82) * mm, "end": v(-116.17, -371.04) * mm});
            skLineSegment(sketch, "E4838", {"start": v(-116.17, -371.04) * mm, "end": v(-116.34, -371.28) * mm});
            skLineSegment(sketch, "E4839", {"start": v(-116.34, -371.28) * mm, "end": v(-116.5, -371.53) * mm});
            skLineSegment(sketch, "E4840", {"start": v(-116.5, -371.53) * mm, "end": v(-116.65, -371.78) * mm});
            skLineSegment(sketch, "E4841", {"start": v(-116.65, -371.78) * mm, "end": v(-116.78, -372.05) * mm});
            skLineSegment(sketch, "E4842", {"start": v(-116.78, -372.05) * mm, "end": v(-116.9, -372.32) * mm});
            skLineSegment(sketch, "E4843", {"start": v(-116.9, -372.32) * mm, "end": v(-117, -372.6) * mm});
            skLineSegment(sketch, "E4844", {"start": v(-117, -372.6) * mm, "end": v(-117.07, -372.9) * mm});
            skLineSegment(sketch, "E4845", {"start": v(-117.07, -372.9) * mm, "end": v(-117.14, -373.19) * mm});
            skLineSegment(sketch, "E4846", {"start": v(-117.14, -373.19) * mm, "end": v(-117.18, -373.5) * mm});
            skLineSegment(sketch, "E4847", {"start": v(-117.18, -373.5) * mm, "end": v(-117.2, -373.8) * mm});
            skLineSegment(sketch, "E4848", {"start": v(-117.2, -373.8) * mm, "end": v(-117.22, -374.13) * mm});
            skLineSegment(sketch, "E4849", {"start": v(-117.22, -374.13) * mm, "end": v(-117.2, -374.64) * mm});
            skLineSegment(sketch, "E4850", {"start": v(-117.2, -374.64) * mm, "end": v(-117.11, -375.12) * mm});
            skLineSegment(sketch, "E4851", {"start": v(-117.11, -375.12) * mm, "end": v(-116.98, -375.58) * mm});
            skLineSegment(sketch, "E4852", {"start": v(-116.98, -375.58) * mm, "end": v(-116.9, -375.8) * mm});
            skLineSegment(sketch, "E4853", {"start": v(-116.9, -375.8) * mm, "end": v(-116.8, -376.02) * mm});
            skLineSegment(sketch, "E4854", {"start": v(-116.8, -376.02) * mm, "end": v(-116.68, -376.22) * mm});
            skLineSegment(sketch, "E4855", {"start": v(-116.68, -376.22) * mm, "end": v(-116.55, -376.43) * mm});
            skLineSegment(sketch, "E4856", {"start": v(-116.55, -376.43) * mm, "end": v(-116.4, -376.62) * mm});
            skLineSegment(sketch, "E4857", {"start": v(-116.4, -376.62) * mm, "end": v(-116.25, -376.81) * mm});
            skLineSegment(sketch, "E4858", {"start": v(-116.25, -376.81) * mm, "end": v(-115.9, -377.18) * mm});
            skLineSegment(sketch, "E4859", {"start": v(-115.9, -377.18) * mm, "end": v(-115.47, -377.52) * mm});
            skLineSegment(sketch, "E4860", {"start": v(-115.47, -377.52) * mm, "end": v(-114.98, -377.85) * mm});
            skLineSegment(sketch, "E4861", {"start": v(-114.98, -377.85) * mm, "end": v(-114.44, -378.16) * mm});
            skLineSegment(sketch, "E4862", {"start": v(-114.44, -378.16) * mm, "end": v(-113.82, -378.45) * mm});
            skLineSegment(sketch, "E4863", {"start": v(-113.82, -378.45) * mm, "end": v(-113.14, -378.72) * mm});
            skLineSegment(sketch, "E4864", {"start": v(-113.14, -378.72) * mm, "end": v(-112.4, -378.98) * mm});
            skLineSegment(sketch, "E4865", {"start": v(-112.4, -378.98) * mm, "end": v(-111.58, -379.22) * mm});
            skLineSegment(sketch, "E4866", {"start": v(-111.58, -379.22) * mm, "end": v(-110.7, -379.45) * mm});
            skLineSegment(sketch, "E4867", {"start": v(-110.7, -379.45) * mm, "end": v(-109.73, -379.67) * mm});
            skLineSegment(sketch, "E4868", {"start": v(-109.73, -379.67) * mm, "end": v(-104.25, -380.83) * mm});
            skLineSegment(sketch, "E4869", {"start": v(-104.25, -380.83) * mm, "end": v(-103.41, -381.02) * mm});
            skLineSegment(sketch, "E4870", {"start": v(-103.41, -381.02) * mm, "end": v(-102.6, -381.22) * mm});
            skLineSegment(sketch, "E4871", {"start": v(-102.6, -381.22) * mm, "end": v(-101.82, -381.43) * mm});
            skLineSegment(sketch, "E4872", {"start": v(-101.82, -381.43) * mm, "end": v(-101.07, -381.65) * mm});
            skLineSegment(sketch, "E4873", {"start": v(-101.07, -381.65) * mm, "end": v(-100.35, -381.88) * mm});
            skLineSegment(sketch, "E4874", {"start": v(-100.35, -381.88) * mm, "end": v(-99.66, -382.13) * mm});
            skLineSegment(sketch, "E4875", {"start": v(-99.66, -382.13) * mm, "end": v(-99, -382.4) * mm});
            skLineSegment(sketch, "E4876", {"start": v(-99, -382.4) * mm, "end": v(-98.36, -382.67) * mm});
            skLineSegment(sketch, "E4877", {"start": v(-98.36, -382.67) * mm, "end": v(-97.76, -382.95) * mm});
            skLineSegment(sketch, "E4878", {"start": v(-97.76, -382.95) * mm, "end": v(-97.18, -383.26) * mm});
            skLineSegment(sketch, "E4879", {"start": v(-97.18, -383.26) * mm, "end": v(-96.63, -383.57) * mm});
            skLineSegment(sketch, "E4880", {"start": v(-96.63, -383.57) * mm, "end": v(-96.11, -383.9) * mm});
            skLineSegment(sketch, "E4881", {"start": v(-96.11, -383.9) * mm, "end": v(-95.62, -384.24) * mm});
            skLineSegment(sketch, "E4882", {"start": v(-95.62, -384.24) * mm, "end": v(-95.15, -384.6) * mm});
            skLineSegment(sketch, "E4883", {"start": v(-95.15, -384.6) * mm, "end": v(-94.71, -384.97) * mm});
            skLineSegment(sketch, "E4884", {"start": v(-94.71, -384.97) * mm, "end": v(-94.3, -385.36) * mm});
            skLineSegment(sketch, "E4885", {"start": v(-94.3, -385.36) * mm, "end": v(-93.92, -385.76) * mm});
            skLineSegment(sketch, "E4886", {"start": v(-93.92, -385.76) * mm, "end": v(-93.56, -386.18) * mm});
            skLineSegment(sketch, "E4887", {"start": v(-93.56, -386.18) * mm, "end": v(-93.23, -386.61) * mm});
            skLineSegment(sketch, "E4888", {"start": v(-93.23, -386.61) * mm, "end": v(-92.92, -387.06) * mm});
            skLineSegment(sketch, "E4889", {"start": v(-92.92, -387.06) * mm, "end": v(-92.64, -387.53) * mm});
            skLineSegment(sketch, "E4890", {"start": v(-92.64, -387.53) * mm, "end": v(-92.39, -388) * mm});
            skLineSegment(sketch, "E4891", {"start": v(-92.39, -388) * mm, "end": v(-92.16, -388.5) * mm});
            skLineSegment(sketch, "E4892", {"start": v(-92.16, -388.5) * mm, "end": v(-91.95, -389.02) * mm});
            skLineSegment(sketch, "E4893", {"start": v(-91.95, -389.02) * mm, "end": v(-91.77, -389.54) * mm});
            skLineSegment(sketch, "E4894", {"start": v(-91.77, -389.54) * mm, "end": v(-91.62, -390.1) * mm});
            skLineSegment(sketch, "E4895", {"start": v(-91.62, -390.1) * mm, "end": v(-91.49, -390.65) * mm});
            skLineSegment(sketch, "E4896", {"start": v(-91.49, -390.65) * mm, "end": v(-91.38, -391.24) * mm});
            skLineSegment(sketch, "E4897", {"start": v(-91.38, -391.24) * mm, "end": v(-91.3, -391.83) * mm});
            skLineSegment(sketch, "E4898", {"start": v(-91.3, -391.83) * mm, "end": v(-91.24, -392.45) * mm});
            skLineSegment(sketch, "E4899", {"start": v(-91.24, -392.45) * mm, "end": v(-91.2, -393.08) * mm});
            skLineSegment(sketch, "E4900", {"start": v(-91.2, -393.08) * mm, "end": v(-91.2, -393.73) * mm});
            skLineSegment(sketch, "E4901", {"start": v(-91.2, -393.73) * mm, "end": v(-91.22, -394.58) * mm});
            skLineSegment(sketch, "E4902", {"start": v(-91.22, -394.58) * mm, "end": v(-91.28, -395.4) * mm});
            skLineSegment(sketch, "E4903", {"start": v(-91.28, -395.4) * mm, "end": v(-91.38, -396.21) * mm});
            skLineSegment(sketch, "E4904", {"start": v(-91.38, -396.21) * mm, "end": v(-91.52, -397) * mm});
            skLineSegment(sketch, "E4905", {"start": v(-91.52, -397) * mm, "end": v(-91.7, -397.76) * mm});
            skLineSegment(sketch, "E4906", {"start": v(-91.7, -397.76) * mm, "end": v(-91.92, -398.5) * mm});
            skLineSegment(sketch, "E4907", {"start": v(-91.92, -398.5) * mm, "end": v(-92.18, -399.21) * mm});
            skLineSegment(sketch, "E4908", {"start": v(-92.18, -399.21) * mm, "end": v(-92.47, -399.9) * mm});
            skLineSegment(sketch, "E4909", {"start": v(-92.47, -399.9) * mm, "end": v(-92.8, -400.57) * mm});
            skLineSegment(sketch, "E4910", {"start": v(-92.8, -400.57) * mm, "end": v(-93.17, -401.22) * mm});
            skLineSegment(sketch, "E4911", {"start": v(-93.17, -401.22) * mm, "end": v(-93.58, -401.84) * mm});
            skLineSegment(sketch, "E4912", {"start": v(-93.58, -401.84) * mm, "end": v(-94.02, -402.43) * mm});
            skLineSegment(sketch, "E4913", {"start": v(-94.02, -402.43) * mm, "end": v(-94.5, -403) * mm});
            skLineSegment(sketch, "E4914", {"start": v(-94.5, -403) * mm, "end": v(-95, -403.54) * mm});
            skLineSegment(sketch, "E4915", {"start": v(-95, -403.54) * mm, "end": v(-95.55, -404.06) * mm});
            skLineSegment(sketch, "E4916", {"start": v(-95.55, -404.06) * mm, "end": v(-96.13, -404.55) * mm});
            skLineSegment(sketch, "E4917", {"start": v(-96.13, -404.55) * mm, "end": v(-96.74, -405.01) * mm});
            skLineSegment(sketch, "E4918", {"start": v(-96.74, -405.01) * mm, "end": v(-97.39, -405.45) * mm});
            skLineSegment(sketch, "E4919", {"start": v(-97.39, -405.45) * mm, "end": v(-98.06, -405.86) * mm});
            skLineSegment(sketch, "E4920", {"start": v(-98.06, -405.86) * mm, "end": v(-98.77, -406.24) * mm});
            skLineSegment(sketch, "E4921", {"start": v(-98.77, -406.24) * mm, "end": v(-99.51, -406.6) * mm});
            skLineSegment(sketch, "E4922", {"start": v(-99.51, -406.6) * mm, "end": v(-100.29, -406.92) * mm});
            skLineSegment(sketch, "E4923", {"start": v(-100.29, -406.92) * mm, "end": v(-101.09, -407.21) * mm});
            skLineSegment(sketch, "E4924", {"start": v(-101.09, -407.21) * mm, "end": v(-101.92, -407.48) * mm});
            skLineSegment(sketch, "E4925", {"start": v(-101.92, -407.48) * mm, "end": v(-102.78, -407.71) * mm});
            skLineSegment(sketch, "E4926", {"start": v(-102.78, -407.71) * mm, "end": v(-103.68, -407.92) * mm});
            skLineSegment(sketch, "E4927", {"start": v(-103.68, -407.92) * mm, "end": v(-104.6, -408.1) * mm});
            skLineSegment(sketch, "E4928", {"start": v(-104.6, -408.1) * mm, "end": v(-105.54, -408.24) * mm});
            skLineSegment(sketch, "E4929", {"start": v(-105.54, -408.24) * mm, "end": v(-106.52, -408.35) * mm});
            skLineSegment(sketch, "E4930", {"start": v(-106.52, -408.35) * mm, "end": v(-107.52, -408.43) * mm});
            skLineSegment(sketch, "E4931", {"start": v(-107.52, -408.43) * mm, "end": v(-108.55, -408.48) * mm});
            skLineSegment(sketch, "E4932", {"start": v(-108.55, -408.48) * mm, "end": v(-109.6, -408.5) * mm});
            skLineSegment(sketch, "E4933", {"start": v(-109.6, -408.5) * mm, "end": v(-110.6, -408.48) * mm});
            skLineSegment(sketch, "E4934", {"start": v(-110.6, -408.48) * mm, "end": v(-111.59, -408.43) * mm});
            skLineSegment(sketch, "E4935", {"start": v(-111.59, -408.43) * mm, "end": v(-112.55, -408.36) * mm});
            skLineSegment(sketch, "E4936", {"start": v(-112.55, -408.36) * mm, "end": v(-113.48, -408.25) * mm});
            skLineSegment(sketch, "E4937", {"start": v(-113.48, -408.25) * mm, "end": v(-114.39, -408.11) * mm});
            skLineSegment(sketch, "E4938", {"start": v(-114.39, -408.11) * mm, "end": v(-115.27, -407.95) * mm});
            skLineSegment(sketch, "E4939", {"start": v(-115.27, -407.95) * mm, "end": v(-116.13, -407.75) * mm});
            skLineSegment(sketch, "E4940", {"start": v(-116.13, -407.75) * mm, "end": v(-116.96, -407.53) * mm});
            skLineSegment(sketch, "E4941", {"start": v(-116.96, -407.53) * mm, "end": v(-117.77, -407.28) * mm});
            skLineSegment(sketch, "E4942", {"start": v(-117.77, -407.28) * mm, "end": v(-118.55, -407) * mm});
            skLineSegment(sketch, "E4943", {"start": v(-118.55, -407) * mm, "end": v(-119.3, -406.7) * mm});
            skLineSegment(sketch, "E4944", {"start": v(-119.3, -406.7) * mm, "end": v(-120.03, -406.37) * mm});
            skLineSegment(sketch, "E4945", {"start": v(-120.03, -406.37) * mm, "end": v(-120.72, -406) * mm});
            skLineSegment(sketch, "E4946", {"start": v(-120.72, -406) * mm, "end": v(-121.39, -405.62) * mm});
            skLineSegment(sketch, "E4947", {"start": v(-121.39, -405.62) * mm, "end": v(-122.02, -405.21) * mm});
            skLineSegment(sketch, "E4948", {"start": v(-122.02, -405.21) * mm, "end": v(-122.63, -404.78) * mm});
            skLineSegment(sketch, "E4949", {"start": v(-122.63, -404.78) * mm, "end": v(-123.2, -404.32) * mm});
            skLineSegment(sketch, "E4950", {"start": v(-123.2, -404.32) * mm, "end": v(-123.75, -403.83) * mm});
            skLineSegment(sketch, "E4951", {"start": v(-123.75, -403.83) * mm, "end": v(-124.26, -403.32) * mm});
            skLineSegment(sketch, "E4952", {"start": v(-124.26, -403.32) * mm, "end": v(-124.74, -402.8) * mm});
            skLineSegment(sketch, "E4953", {"start": v(-124.74, -402.8) * mm, "end": v(-125.19, -402.24) * mm});
            skLineSegment(sketch, "E4954", {"start": v(-125.19, -402.24) * mm, "end": v(-125.6, -401.66) * mm});
            skLineSegment(sketch, "E4955", {"start": v(-125.6, -401.66) * mm, "end": v(-125.98, -401.06) * mm});
            skLineSegment(sketch, "E4956", {"start": v(-125.98, -401.06) * mm, "end": v(-126.33, -400.43) * mm});
            skLineSegment(sketch, "E4957", {"start": v(-126.33, -400.43) * mm, "end": v(-126.64, -399.8) * mm});
            skLineSegment(sketch, "E4958", {"start": v(-126.64, -399.8) * mm, "end": v(-126.91, -399.12) * mm});
            skLineSegment(sketch, "E4959", {"start": v(-126.91, -399.12) * mm, "end": v(-127.15, -398.44) * mm});
            skLineSegment(sketch, "E4960", {"start": v(-127.15, -398.44) * mm, "end": v(-127.36, -397.73) * mm});
            skLineSegment(sketch, "E4961", {"start": v(-127.36, -397.73) * mm, "end": v(-127.52, -397) * mm});
            skLineSegment(sketch, "E4962", {"start": v(-127.52, -397) * mm, "end": v(-127.65, -396.26) * mm});
            skLineSegment(sketch, "E4963", {"start": v(-127.65, -396.26) * mm, "end": v(-127.74, -395.5) * mm});
            skLineSegment(sketch, "E4964", {"start": v(-127.74, -395.5) * mm, "end": v(-127.8, -394.7) * mm});
            skLineSegment(sketch, "E4965", {"start": v(-127.8, -394.7) * mm, "end": v(-118.6, -394.7) * mm});
            skLineSegment(sketch, "E4966", {"start": v(13.4, -371.36) * mm, "end": v(13.97, -371.36) * mm});
            skLineSegment(sketch, "E4967", {"start": v(13.97, -371.36) * mm, "end": v(19.6, -389.17) * mm});
            skLineSegment(sketch, "E4968", {"start": v(19.6, -389.17) * mm, "end": v(7.7, -389.17) * mm});
            skLineSegment(sketch, "E4969", {"start": v(7.7, -389.17) * mm, "end": v(13.4, -371.36) * mm});
            skLineSegment(sketch, "E4970", {"start": v(21.62, -396.5) * mm, "end": v(5.66, -396.5) * mm});
            skLineSegment(sketch, "E4971", {"start": v(5.66, -396.5) * mm, "end": v(2.17, -407.33) * mm});
            skLineSegment(sketch, "E4972", {"start": v(2.17, -407.33) * mm, "end": v(-7.37, -407.33) * mm});
            skLineSegment(sketch, "E4973", {"start": v(-7.37, -407.33) * mm, "end": v(8.4, -361.92) * mm});
            skLineSegment(sketch, "E4974", {"start": v(8.4, -361.92) * mm, "end": v(19.57, -361.92) * mm});
            skLineSegment(sketch, "E4975", {"start": v(19.57, -361.92) * mm, "end": v(35.34, -407.33) * mm});
            skLineSegment(sketch, "E4976", {"start": v(35.34, -407.33) * mm, "end": v(25.05, -407.33) * mm});
            skLineSegment(sketch, "E4977", {"start": v(25.05, -407.33) * mm, "end": v(21.62, -396.5) * mm});
            skLineSegment(sketch, "E4978", {"start": v(69.76, -384.6) * mm, "end": v(69.78, -383.24) * mm});
            skLineSegment(sketch, "E4979", {"start": v(69.78, -383.24) * mm, "end": v(69.85, -381.9) * mm});
            skLineSegment(sketch, "E4980", {"start": v(69.85, -381.9) * mm, "end": v(69.97, -380.61) * mm});
            skLineSegment(sketch, "E4981", {"start": v(69.97, -380.61) * mm, "end": v(70.13, -379.35) * mm});
            skLineSegment(sketch, "E4982", {"start": v(70.13, -379.35) * mm, "end": v(70.34, -378.12) * mm});
            skLineSegment(sketch, "E4983", {"start": v(70.34, -378.12) * mm, "end": v(70.6, -376.93) * mm});
            skLineSegment(sketch, "E4984", {"start": v(70.6, -376.93) * mm, "end": v(70.9, -375.77) * mm});
            skLineSegment(sketch, "E4985", {"start": v(70.9, -375.77) * mm, "end": v(71.23, -374.66) * mm});
            skLineSegment(sketch, "E4986", {"start": v(71.23, -374.66) * mm, "end": v(71.62, -373.58) * mm});
            skLineSegment(sketch, "E4987", {"start": v(71.62, -373.58) * mm, "end": v(72.04, -372.54) * mm});
            skLineSegment(sketch, "E4988", {"start": v(72.04, -372.54) * mm, "end": v(72.51, -371.54) * mm});
            skLineSegment(sketch, "E4989", {"start": v(72.51, -371.54) * mm, "end": v(73.02, -370.58) * mm});
            skLineSegment(sketch, "E4990", {"start": v(73.02, -370.58) * mm, "end": v(73.57, -369.66) * mm});
            skLineSegment(sketch, "E4991", {"start": v(73.57, -369.66) * mm, "end": v(74.16, -368.78) * mm});
            skLineSegment(sketch, "E4992", {"start": v(74.16, -368.78) * mm, "end": v(74.8, -367.94) * mm});
            skLineSegment(sketch, "E4993", {"start": v(74.8, -367.94) * mm, "end": v(75.47, -367.15) * mm});
            skLineSegment(sketch, "E4994", {"start": v(75.47, -367.15) * mm, "end": v(76.17, -366.4) * mm});
            skLineSegment(sketch, "E4995", {"start": v(76.17, -366.4) * mm, "end": v(76.92, -365.7) * mm});
            skLineSegment(sketch, "E4996", {"start": v(76.92, -365.7) * mm, "end": v(77.7, -365.03) * mm});
            skLineSegment(sketch, "E4997", {"start": v(77.7, -365.03) * mm, "end": v(78.53, -364.41) * mm});
            skLineSegment(sketch, "E4998", {"start": v(78.53, -364.41) * mm, "end": v(79.39, -363.84) * mm});
            skLineSegment(sketch, "E4999", {"start": v(79.39, -363.84) * mm, "end": v(80.28, -363.32) * mm});
            skLineSegment(sketch, "E5000", {"start": v(80.28, -363.32) * mm, "end": v(81.2, -362.84) * mm});
            skLineSegment(sketch, "E5001", {"start": v(81.2, -362.84) * mm, "end": v(82.17, -362.4) * mm});
            skLineSegment(sketch, "E5002", {"start": v(82.17, -362.4) * mm, "end": v(83.17, -362.03) * mm});
            skLineSegment(sketch, "E5003", {"start": v(83.17, -362.03) * mm, "end": v(84.2, -361.7) * mm});
            skLineSegment(sketch, "E5004", {"start": v(84.2, -361.7) * mm, "end": v(85.26, -361.4) * mm});
            skLineSegment(sketch, "E5005", {"start": v(85.26, -361.4) * mm, "end": v(86.36, -361.17) * mm});
            skLineSegment(sketch, "E5006", {"start": v(86.36, -361.17) * mm, "end": v(87.5, -361) * mm});
            skLineSegment(sketch, "E5007", {"start": v(87.5, -361) * mm, "end": v(88.65, -360.86) * mm});
            skLineSegment(sketch, "E5008", {"start": v(88.65, -360.86) * mm, "end": v(89.84, -360.78) * mm});
            skLineSegment(sketch, "E5009", {"start": v(89.84, -360.78) * mm, "end": v(91.06, -360.76) * mm});
            skLineSegment(sketch, "E5010", {"start": v(91.06, -360.76) * mm, "end": v(92.06, -360.78) * mm});
            skLineSegment(sketch, "E5011", {"start": v(92.06, -360.78) * mm, "end": v(93.05, -360.84) * mm});
            skLineSegment(sketch, "E5012", {"start": v(93.05, -360.84) * mm, "end": v(94.02, -360.94) * mm});
            skLineSegment(sketch, "E5013", {"start": v(94.02, -360.94) * mm, "end": v(94.97, -361.08) * mm});
            skLineSegment(sketch, "E5014", {"start": v(94.97, -361.08) * mm, "end": v(95.9, -361.26) * mm});
            skLineSegment(sketch, "E5015", {"start": v(95.9, -361.26) * mm, "end": v(96.82, -361.48) * mm});
            skLineSegment(sketch, "E5016", {"start": v(96.82, -361.48) * mm, "end": v(97.71, -361.73) * mm});
            skLineSegment(sketch, "E5017", {"start": v(97.71, -361.73) * mm, "end": v(98.58, -362.03) * mm});
            skLineSegment(sketch, "E5018", {"start": v(98.58, -362.03) * mm, "end": v(99.43, -362.35) * mm});
            skLineSegment(sketch, "E5019", {"start": v(99.43, -362.35) * mm, "end": v(100.26, -362.71) * mm});
            skLineSegment(sketch, "E5020", {"start": v(100.26, -362.71) * mm, "end": v(101.06, -363.1) * mm});
            skLineSegment(sketch, "E5021", {"start": v(101.06, -363.1) * mm, "end": v(101.84, -363.54) * mm});
            skLineSegment(sketch, "E5022", {"start": v(101.84, -363.54) * mm, "end": v(102.6, -364) * mm});
            skLineSegment(sketch, "E5023", {"start": v(102.6, -364) * mm, "end": v(103.32, -364.49) * mm});
            skLineSegment(sketch, "E5024", {"start": v(103.32, -364.49) * mm, "end": v(104.02, -365) * mm});
            skLineSegment(sketch, "E5025", {"start": v(104.02, -365) * mm, "end": v(104.69, -365.56) * mm});
            skLineSegment(sketch, "E5026", {"start": v(104.69, -365.56) * mm, "end": v(105.33, -366.14) * mm});
            skLineSegment(sketch, "E5027", {"start": v(105.33, -366.14) * mm, "end": v(105.94, -366.75) * mm});
            skLineSegment(sketch, "E5028", {"start": v(105.94, -366.75) * mm, "end": v(106.52, -367.39) * mm});
            skLineSegment(sketch, "E5029", {"start": v(106.52, -367.39) * mm, "end": v(107.06, -368.05) * mm});
            skLineSegment(sketch, "E5030", {"start": v(107.06, -368.05) * mm, "end": v(107.58, -368.74) * mm});
            skLineSegment(sketch, "E5031", {"start": v(107.58, -368.74) * mm, "end": v(108.05, -369.45) * mm});
            skLineSegment(sketch, "E5032", {"start": v(108.05, -369.45) * mm, "end": v(108.5, -370.19) * mm});
            skLineSegment(sketch, "E5033", {"start": v(108.5, -370.19) * mm, "end": v(108.9, -370.95) * mm});
            skLineSegment(sketch, "E5034", {"start": v(108.9, -370.95) * mm, "end": v(109.28, -371.73) * mm});
            skLineSegment(sketch, "E5035", {"start": v(109.28, -371.73) * mm, "end": v(109.61, -372.54) * mm});
            skLineSegment(sketch, "E5036", {"start": v(109.61, -372.54) * mm, "end": v(109.9, -373.36) * mm});
            skLineSegment(sketch, "E5037", {"start": v(109.9, -373.36) * mm, "end": v(110.16, -374.21) * mm});
            skLineSegment(sketch, "E5038", {"start": v(110.16, -374.21) * mm, "end": v(110.37, -375.08) * mm});
            skLineSegment(sketch, "E5039", {"start": v(110.37, -375.08) * mm, "end": v(110.55, -375.96) * mm});
            skLineSegment(sketch, "E5040", {"start": v(110.55, -375.96) * mm, "end": v(110.68, -376.86) * mm});
            skLineSegment(sketch, "E5041", {"start": v(110.68, -376.86) * mm, "end": v(110.76, -377.78) * mm});
            skLineSegment(sketch, "E5042", {"start": v(110.76, -377.78) * mm, "end": v(101.51, -377.78) * mm});
            skLineSegment(sketch, "E5043", {"start": v(101.51, -377.78) * mm, "end": v(101.42, -377.3) * mm});
            skLineSegment(sketch, "E5044", {"start": v(101.42, -377.3) * mm, "end": v(101.3, -376.82) * mm});
            skLineSegment(sketch, "E5045", {"start": v(101.3, -376.82) * mm, "end": v(101.17, -376.36) * mm});
            skLineSegment(sketch, "E5046", {"start": v(101.17, -376.36) * mm, "end": v(101.02, -375.9) * mm});
            skLineSegment(sketch, "E5047", {"start": v(101.02, -375.9) * mm, "end": v(100.86, -375.47) * mm});
            skLineSegment(sketch, "E5048", {"start": v(100.86, -375.47) * mm, "end": v(100.67, -375.04) * mm});
            skLineSegment(sketch, "E5049", {"start": v(100.67, -375.04) * mm, "end": v(100.47, -374.63) * mm});
            skLineSegment(sketch, "E5050", {"start": v(100.47, -374.63) * mm, "end": v(100.25, -374.22) * mm});
            skLineSegment(sketch, "E5051", {"start": v(100.25, -374.22) * mm, "end": v(100.02, -373.83) * mm});
            skLineSegment(sketch, "E5052", {"start": v(100.02, -373.83) * mm, "end": v(99.77, -373.46) * mm});
            skLineSegment(sketch, "E5053", {"start": v(99.77, -373.46) * mm, "end": v(99.5, -373.1) * mm});
            skLineSegment(sketch, "E5054", {"start": v(99.5, -373.1) * mm, "end": v(99.23, -372.75) * mm});
            skLineSegment(sketch, "E5055", {"start": v(99.23, -372.75) * mm, "end": v(98.94, -372.41) * mm});
            skLineSegment(sketch, "E5056", {"start": v(98.94, -372.41) * mm, "end": v(98.63, -372.09) * mm});
            skLineSegment(sketch, "E5057", {"start": v(98.63, -372.09) * mm, "end": v(98.3, -371.78) * mm});
            skLineSegment(sketch, "E5058", {"start": v(98.3, -371.78) * mm, "end": v(97.97, -371.5) * mm});
            skLineSegment(sketch, "E5059", {"start": v(97.97, -371.5) * mm, "end": v(97.63, -371.22) * mm});
            skLineSegment(sketch, "E5060", {"start": v(97.63, -371.22) * mm, "end": v(97.26, -370.96) * mm});
            skLineSegment(sketch, "E5061", {"start": v(97.26, -370.96) * mm, "end": v(96.9, -370.71) * mm});
            skLineSegment(sketch, "E5062", {"start": v(96.9, -370.71) * mm, "end": v(96.5, -370.49) * mm});
            skLineSegment(sketch, "E5063", {"start": v(96.5, -370.49) * mm, "end": v(96.1, -370.27) * mm});
            skLineSegment(sketch, "E5064", {"start": v(96.1, -370.27) * mm, "end": v(95.7, -370.08) * mm});
            skLineSegment(sketch, "E5065", {"start": v(95.7, -370.08) * mm, "end": v(95.28, -369.9) * mm});
            skLineSegment(sketch, "E5066", {"start": v(95.28, -369.9) * mm, "end": v(94.85, -369.74) * mm});
            skLineSegment(sketch, "E5067", {"start": v(94.85, -369.74) * mm, "end": v(94.4, -369.6) * mm});
            skLineSegment(sketch, "E5068", {"start": v(94.4, -369.6) * mm, "end": v(93.96, -369.48) * mm});
            skLineSegment(sketch, "E5069", {"start": v(93.96, -369.48) * mm, "end": v(93.5, -369.37) * mm});
            skLineSegment(sketch, "E5070", {"start": v(93.5, -369.37) * mm, "end": v(93.03, -369.28) * mm});
            skLineSegment(sketch, "E5071", {"start": v(93.03, -369.28) * mm, "end": v(92.55, -369.21) * mm});
            skLineSegment(sketch, "E5072", {"start": v(92.55, -369.21) * mm, "end": v(92.06, -369.16) * mm});
            skLineSegment(sketch, "E5073", {"start": v(92.06, -369.16) * mm, "end": v(91.57, -369.13) * mm});
            skLineSegment(sketch, "E5074", {"start": v(91.57, -369.13) * mm, "end": v(91.06, -369.12) * mm});
            skLineSegment(sketch, "E5075", {"start": v(91.06, -369.12) * mm, "end": v(90.4, -369.14) * mm});
            skLineSegment(sketch, "E5076", {"start": v(90.4, -369.14) * mm, "end": v(89.76, -369.2) * mm});
            skLineSegment(sketch, "E5077", {"start": v(89.76, -369.2) * mm, "end": v(89.13, -369.28) * mm});
            skLineSegment(sketch, "E5078", {"start": v(89.13, -369.28) * mm, "end": v(88.51, -369.4) * mm});
            skLineSegment(sketch, "E5079", {"start": v(88.51, -369.4) * mm, "end": v(87.92, -369.55) * mm});
            skLineSegment(sketch, "E5080", {"start": v(87.92, -369.55) * mm, "end": v(87.34, -369.73) * mm});
            skLineSegment(sketch, "E5081", {"start": v(87.34, -369.73) * mm, "end": v(86.78, -369.95) * mm});
            skLineSegment(sketch, "E5082", {"start": v(86.78, -369.95) * mm, "end": v(86.24, -370.2) * mm});
            skLineSegment(sketch, "E5083", {"start": v(86.24, -370.2) * mm, "end": v(85.72, -370.48) * mm});
            skLineSegment(sketch, "E5084", {"start": v(85.72, -370.48) * mm, "end": v(85.21, -370.79) * mm});
            skLineSegment(sketch, "E5085", {"start": v(85.21, -370.79) * mm, "end": v(84.73, -371.13) * mm});
            skLineSegment(sketch, "E5086", {"start": v(84.73, -371.13) * mm, "end": v(84.26, -371.5) * mm});
            skLineSegment(sketch, "E5087", {"start": v(84.26, -371.5) * mm, "end": v(83.81, -371.9) * mm});
            skLineSegment(sketch, "E5088", {"start": v(83.81, -371.9) * mm, "end": v(83.39, -372.33) * mm});
            skLineSegment(sketch, "E5089", {"start": v(83.39, -372.33) * mm, "end": v(82.98, -372.8) * mm});
            skLineSegment(sketch, "E5090", {"start": v(82.98, -372.8) * mm, "end": v(82.6, -373.28) * mm});
            skLineSegment(sketch, "E5091", {"start": v(82.6, -373.28) * mm, "end": v(82.23, -373.8) * mm});
            skLineSegment(sketch, "E5092", {"start": v(82.23, -373.8) * mm, "end": v(81.89, -374.34) * mm});
            skLineSegment(sketch, "E5093", {"start": v(81.89, -374.34) * mm, "end": v(81.56, -374.9) * mm});
            skLineSegment(sketch, "E5094", {"start": v(81.56, -374.9) * mm, "end": v(81.26, -375.5) * mm});
            skLineSegment(sketch, "E5095", {"start": v(81.26, -375.5) * mm, "end": v(80.98, -376.13) * mm});
            skLineSegment(sketch, "E5096", {"start": v(80.98, -376.13) * mm, "end": v(80.73, -376.78) * mm});
            skLineSegment(sketch, "E5097", {"start": v(80.73, -376.78) * mm, "end": v(80.5, -377.45) * mm});
            skLineSegment(sketch, "E5098", {"start": v(80.5, -377.45) * mm, "end": v(80.29, -378.15) * mm});
            skLineSegment(sketch, "E5099", {"start": v(80.29, -378.15) * mm, "end": v(80.1, -378.88) * mm});
            skLineSegment(sketch, "E5100", {"start": v(80.1, -378.88) * mm, "end": v(79.94, -379.63) * mm});
            skLineSegment(sketch, "E5101", {"start": v(79.94, -379.63) * mm, "end": v(79.8, -380.4) * mm});
            skLineSegment(sketch, "E5102", {"start": v(79.8, -380.4) * mm, "end": v(79.69, -381.2) * mm});
            skLineSegment(sketch, "E5103", {"start": v(79.69, -381.2) * mm, "end": v(79.6, -382.02) * mm});
            skLineSegment(sketch, "E5104", {"start": v(79.6, -382.02) * mm, "end": v(79.53, -382.86) * mm});
            skLineSegment(sketch, "E5105", {"start": v(79.53, -382.86) * mm, "end": v(79.5, -383.72) * mm});
            skLineSegment(sketch, "E5106", {"start": v(79.5, -383.72) * mm, "end": v(79.48, -384.6) * mm});
            skLineSegment(sketch, "E5107", {"start": v(79.48, -384.6) * mm, "end": v(79.5, -385.5) * mm});
            skLineSegment(sketch, "E5108", {"start": v(79.5, -385.5) * mm, "end": v(79.53, -386.36) * mm});
            skLineSegment(sketch, "E5109", {"start": v(79.53, -386.36) * mm, "end": v(79.6, -387.2) * mm});
            skLineSegment(sketch, "E5110", {"start": v(79.6, -387.2) * mm, "end": v(79.69, -388.02) * mm});
            skLineSegment(sketch, "E5111", {"start": v(79.69, -388.02) * mm, "end": v(79.8, -388.82) * mm});
            skLineSegment(sketch, "E5112", {"start": v(79.8, -388.82) * mm, "end": v(79.94, -389.6) * mm});
            skLineSegment(sketch, "E5113", {"start": v(79.94, -389.6) * mm, "end": v(80.1, -390.34) * mm});
            skLineSegment(sketch, "E5114", {"start": v(80.1, -390.34) * mm, "end": v(80.29, -391.07) * mm});
            skLineSegment(sketch, "E5115", {"start": v(80.29, -391.07) * mm, "end": v(80.5, -391.77) * mm});
            skLineSegment(sketch, "E5116", {"start": v(80.5, -391.77) * mm, "end": v(80.73, -392.45) * mm});
            skLineSegment(sketch, "E5117", {"start": v(80.73, -392.45) * mm, "end": v(80.99, -393.1) * mm});
            skLineSegment(sketch, "E5118", {"start": v(80.99, -393.1) * mm, "end": v(81.26, -393.72) * mm});
            skLineSegment(sketch, "E5119", {"start": v(81.26, -393.72) * mm, "end": v(81.57, -394.32) * mm});
            skLineSegment(sketch, "E5120", {"start": v(81.57, -394.32) * mm, "end": v(81.89, -394.9) * mm});
            skLineSegment(sketch, "E5121", {"start": v(81.89, -394.9) * mm, "end": v(82.23, -395.44) * mm});
            skLineSegment(sketch, "E5122", {"start": v(82.23, -395.44) * mm, "end": v(82.6, -395.95) * mm});
            skLineSegment(sketch, "E5123", {"start": v(82.6, -395.95) * mm, "end": v(82.98, -396.44) * mm});
            skLineSegment(sketch, "E5124", {"start": v(82.98, -396.44) * mm, "end": v(83.4, -396.9) * mm});
            skLineSegment(sketch, "E5125", {"start": v(83.4, -396.9) * mm, "end": v(83.82, -397.33) * mm});
            skLineSegment(sketch, "E5126", {"start": v(83.82, -397.33) * mm, "end": v(84.27, -397.74) * mm});
            skLineSegment(sketch, "E5127", {"start": v(84.27, -397.74) * mm, "end": v(84.74, -398.1) * mm});
            skLineSegment(sketch, "E5128", {"start": v(84.74, -398.1) * mm, "end": v(85.22, -398.45) * mm});
            skLineSegment(sketch, "E5129", {"start": v(85.22, -398.45) * mm, "end": v(85.73, -398.76) * mm});
            skLineSegment(sketch, "E5130", {"start": v(85.73, -398.76) * mm, "end": v(86.25, -399.04) * mm});
            skLineSegment(sketch, "E5131", {"start": v(86.25, -399.04) * mm, "end": v(86.8, -399.3) * mm});
            skLineSegment(sketch, "E5132", {"start": v(86.8, -399.3) * mm, "end": v(87.36, -399.5) * mm});
            skLineSegment(sketch, "E5133", {"start": v(87.36, -399.5) * mm, "end": v(87.94, -399.7) * mm});
            skLineSegment(sketch, "E5134", {"start": v(87.94, -399.7) * mm, "end": v(88.54, -399.85) * mm});
            skLineSegment(sketch, "E5135", {"start": v(88.54, -399.85) * mm, "end": v(89.15, -399.97) * mm});
            skLineSegment(sketch, "E5136", {"start": v(89.15, -399.97) * mm, "end": v(89.78, -400.05) * mm});
            skLineSegment(sketch, "E5137", {"start": v(89.78, -400.05) * mm, "end": v(90.43, -400.1) * mm});
            skLineSegment(sketch, "E5138", {"start": v(90.43, -400.1) * mm, "end": v(91.1, -400.12) * mm});
            skLineSegment(sketch, "E5139", {"start": v(91.1, -400.12) * mm, "end": v(91.6, -400.11) * mm});
            skLineSegment(sketch, "E5140", {"start": v(91.6, -400.11) * mm, "end": v(92.1, -400.08) * mm});
            skLineSegment(sketch, "E5141", {"start": v(92.1, -400.08) * mm, "end": v(92.6, -400.04) * mm});
            skLineSegment(sketch, "E5142", {"start": v(92.6, -400.04) * mm, "end": v(93.07, -399.97) * mm});
            skLineSegment(sketch, "E5143", {"start": v(93.07, -399.97) * mm, "end": v(93.54, -399.9) * mm});
            skLineSegment(sketch, "E5144", {"start": v(93.54, -399.9) * mm, "end": v(94, -399.8) * mm});
            skLineSegment(sketch, "E5145", {"start": v(94, -399.8) * mm, "end": v(94.45, -399.68) * mm});
            skLineSegment(sketch, "E5146", {"start": v(94.45, -399.68) * mm, "end": v(94.9, -399.54) * mm});
            skLineSegment(sketch, "E5147", {"start": v(94.9, -399.54) * mm, "end": v(95.33, -399.4) * mm});
            skLineSegment(sketch, "E5148", {"start": v(95.33, -399.4) * mm, "end": v(95.75, -399.23) * mm});
            skLineSegment(sketch, "E5149", {"start": v(95.75, -399.23) * mm, "end": v(96.16, -399.04) * mm});
            skLineSegment(sketch, "E5150", {"start": v(96.16, -399.04) * mm, "end": v(96.55, -398.84) * mm});
            skLineSegment(sketch, "E5151", {"start": v(96.55, -398.84) * mm, "end": v(96.94, -398.63) * mm});
            skLineSegment(sketch, "E5152", {"start": v(96.94, -398.63) * mm, "end": v(97.31, -398.4) * mm});
            skLineSegment(sketch, "E5153", {"start": v(97.31, -398.4) * mm, "end": v(97.67, -398.15) * mm});
            skLineSegment(sketch, "E5154", {"start": v(97.67, -398.15) * mm, "end": v(98.02, -397.9) * mm});
            skLineSegment(sketch, "E5155", {"start": v(98.02, -397.9) * mm, "end": v(98.35, -397.62) * mm});
            skLineSegment(sketch, "E5156", {"start": v(98.35, -397.62) * mm, "end": v(98.67, -397.33) * mm});
            skLineSegment(sketch, "E5157", {"start": v(98.67, -397.33) * mm, "end": v(98.98, -397.02) * mm});
            skLineSegment(sketch, "E5158", {"start": v(98.98, -397.02) * mm, "end": v(99.27, -396.7) * mm});
            skLineSegment(sketch, "E5159", {"start": v(99.27, -396.7) * mm, "end": v(99.55, -396.38) * mm});
            skLineSegment(sketch, "E5160", {"start": v(99.55, -396.38) * mm, "end": v(99.81, -396.03) * mm});
            skLineSegment(sketch, "E5161", {"start": v(99.81, -396.03) * mm, "end": v(100.06, -395.67) * mm});
            skLineSegment(sketch, "E5162", {"start": v(100.06, -395.67) * mm, "end": v(100.3, -395.3) * mm});
            skLineSegment(sketch, "E5163", {"start": v(100.3, -395.3) * mm, "end": v(100.5, -394.92) * mm});
            skLineSegment(sketch, "E5164", {"start": v(100.5, -394.92) * mm, "end": v(100.7, -394.53) * mm});
            skLineSegment(sketch, "E5165", {"start": v(100.7, -394.53) * mm, "end": v(100.89, -394.12) * mm});
            skLineSegment(sketch, "E5166", {"start": v(100.89, -394.12) * mm, "end": v(101.05, -393.7) * mm});
            skLineSegment(sketch, "E5167", {"start": v(101.05, -393.7) * mm, "end": v(101.2, -393.27) * mm});
            skLineSegment(sketch, "E5168", {"start": v(101.2, -393.27) * mm, "end": v(101.33, -392.83) * mm});
            skLineSegment(sketch, "E5169", {"start": v(101.33, -392.83) * mm, "end": v(101.45, -392.37) * mm});
            skLineSegment(sketch, "E5170", {"start": v(101.45, -392.37) * mm, "end": v(101.54, -391.9) * mm});
            skLineSegment(sketch, "E5171", {"start": v(101.54, -391.9) * mm, "end": v(110.8, -391.9) * mm});
            skLineSegment(sketch, "E5172", {"start": v(110.8, -391.9) * mm, "end": v(110.7, -392.82) * mm});
            skLineSegment(sketch, "E5173", {"start": v(110.7, -392.82) * mm, "end": v(110.56, -393.71) * mm});
            skLineSegment(sketch, "E5174", {"start": v(110.56, -393.71) * mm, "end": v(110.38, -394.59) * mm});
            skLineSegment(sketch, "E5175", {"start": v(110.38, -394.59) * mm, "end": v(110.17, -395.44) * mm});
            skLineSegment(sketch, "E5176", {"start": v(110.17, -395.44) * mm, "end": v(109.91, -396.27) * mm});
            skLineSegment(sketch, "E5177", {"start": v(109.91, -396.27) * mm, "end": v(109.62, -397.09) * mm});
            skLineSegment(sketch, "E5178", {"start": v(109.62, -397.09) * mm, "end": v(109.29, -397.88) * mm});
            skLineSegment(sketch, "E5179", {"start": v(109.29, -397.88) * mm, "end": v(108.92, -398.64) * mm});
            skLineSegment(sketch, "E5180", {"start": v(108.92, -398.64) * mm, "end": v(108.51, -399.39) * mm});
            skLineSegment(sketch, "E5181", {"start": v(108.51, -399.39) * mm, "end": v(108.07, -400.1) * mm});
            skLineSegment(sketch, "E5182", {"start": v(108.07, -400.1) * mm, "end": v(107.6, -400.8) * mm});
            skLineSegment(sketch, "E5183", {"start": v(107.6, -400.8) * mm, "end": v(107.1, -401.47) * mm});
            skLineSegment(sketch, "E5184", {"start": v(107.1, -401.47) * mm, "end": v(106.55, -402.12) * mm});
            skLineSegment(sketch, "E5185", {"start": v(106.55, -402.12) * mm, "end": v(105.98, -402.73) * mm});
            skLineSegment(sketch, "E5186", {"start": v(105.98, -402.73) * mm, "end": v(105.37, -403.32) * mm});
            skLineSegment(sketch, "E5187", {"start": v(105.37, -403.32) * mm, "end": v(104.74, -403.88) * mm});
            skLineSegment(sketch, "E5188", {"start": v(104.74, -403.88) * mm, "end": v(104.08, -404.42) * mm});
            skLineSegment(sketch, "E5189", {"start": v(104.08, -404.42) * mm, "end": v(103.38, -404.92) * mm});
            skLineSegment(sketch, "E5190", {"start": v(103.38, -404.92) * mm, "end": v(102.66, -405.4) * mm});
            skLineSegment(sketch, "E5191", {"start": v(102.66, -405.4) * mm, "end": v(101.91, -405.84) * mm});
            skLineSegment(sketch, "E5192", {"start": v(101.91, -405.84) * mm, "end": v(101.14, -406.25) * mm});
            skLineSegment(sketch, "E5193", {"start": v(101.14, -406.25) * mm, "end": v(100.33, -406.63) * mm});
            skLineSegment(sketch, "E5194", {"start": v(100.33, -406.63) * mm, "end": v(99.5, -406.97) * mm});
            skLineSegment(sketch, "E5195", {"start": v(99.5, -406.97) * mm, "end": v(98.66, -407.28) * mm});
            skLineSegment(sketch, "E5196", {"start": v(98.66, -407.28) * mm, "end": v(97.78, -407.56) * mm});
            skLineSegment(sketch, "E5197", {"start": v(97.78, -407.56) * mm, "end": v(96.88, -407.8) * mm});
            skLineSegment(sketch, "E5198", {"start": v(96.88, -407.8) * mm, "end": v(95.96, -408.01) * mm});
            skLineSegment(sketch, "E5199", {"start": v(95.96, -408.01) * mm, "end": v(95.02, -408.19) * mm});
            skLineSegment(sketch, "E5200", {"start": v(95.02, -408.19) * mm, "end": v(94.06, -408.32) * mm});
            skLineSegment(sketch, "E5201", {"start": v(94.06, -408.32) * mm, "end": v(93.08, -408.42) * mm});
            skLineSegment(sketch, "E5202", {"start": v(93.08, -408.42) * mm, "end": v(92.08, -408.48) * mm});
            skLineSegment(sketch, "E5203", {"start": v(92.08, -408.48) * mm, "end": v(91.06, -408.5) * mm});
            skLineSegment(sketch, "E5204", {"start": v(91.06, -408.5) * mm, "end": v(89.84, -408.47) * mm});
            skLineSegment(sketch, "E5205", {"start": v(89.84, -408.47) * mm, "end": v(88.66, -408.39) * mm});
            skLineSegment(sketch, "E5206", {"start": v(88.66, -408.39) * mm, "end": v(87.5, -408.26) * mm});
            skLineSegment(sketch, "E5207", {"start": v(87.5, -408.26) * mm, "end": v(86.37, -408.08) * mm});
            skLineSegment(sketch, "E5208", {"start": v(86.37, -408.08) * mm, "end": v(85.28, -407.84) * mm});
            skLineSegment(sketch, "E5209", {"start": v(85.28, -407.84) * mm, "end": v(84.21, -407.56) * mm});
            skLineSegment(sketch, "E5210", {"start": v(84.21, -407.56) * mm, "end": v(83.18, -407.23) * mm});
            skLineSegment(sketch, "E5211", {"start": v(83.18, -407.23) * mm, "end": v(82.18, -406.84) * mm});
            skLineSegment(sketch, "E5212", {"start": v(82.18, -406.84) * mm, "end": v(81.22, -406.41) * mm});
            skLineSegment(sketch, "E5213", {"start": v(81.22, -406.41) * mm, "end": v(80.3, -405.93) * mm});
            skLineSegment(sketch, "E5214", {"start": v(80.3, -405.93) * mm, "end": v(79.4, -405.4) * mm});
            skLineSegment(sketch, "E5215", {"start": v(79.4, -405.4) * mm, "end": v(78.54, -404.84) * mm});
            skLineSegment(sketch, "E5216", {"start": v(78.54, -404.84) * mm, "end": v(77.72, -404.22) * mm});
            skLineSegment(sketch, "E5217", {"start": v(77.72, -404.22) * mm, "end": v(76.93, -403.56) * mm});
            skLineSegment(sketch, "E5218", {"start": v(76.93, -403.56) * mm, "end": v(76.19, -402.85) * mm});
            skLineSegment(sketch, "E5219", {"start": v(76.19, -402.85) * mm, "end": v(75.48, -402.1) * mm});
            skLineSegment(sketch, "E5220", {"start": v(75.48, -402.1) * mm, "end": v(74.8, -401.3) * mm});
            skLineSegment(sketch, "E5221", {"start": v(74.8, -401.3) * mm, "end": v(74.17, -400.47) * mm});
            skLineSegment(sketch, "E5222", {"start": v(74.17, -400.47) * mm, "end": v(73.58, -399.59) * mm});
            skLineSegment(sketch, "E5223", {"start": v(73.58, -399.59) * mm, "end": v(73.03, -398.67) * mm});
            skLineSegment(sketch, "E5224", {"start": v(73.03, -398.67) * mm, "end": v(72.52, -397.7) * mm});
            skLineSegment(sketch, "E5225", {"start": v(72.52, -397.7) * mm, "end": v(72.05, -396.7) * mm});
            skLineSegment(sketch, "E5226", {"start": v(72.05, -396.7) * mm, "end": v(71.62, -395.66) * mm});
            skLineSegment(sketch, "E5227", {"start": v(71.62, -395.66) * mm, "end": v(71.24, -394.58) * mm});
            skLineSegment(sketch, "E5228", {"start": v(71.24, -394.58) * mm, "end": v(70.9, -393.46) * mm});
            skLineSegment(sketch, "E5229", {"start": v(70.9, -393.46) * mm, "end": v(70.6, -392.3) * mm});
            skLineSegment(sketch, "E5230", {"start": v(70.6, -392.3) * mm, "end": v(70.34, -391.11) * mm});
            skLineSegment(sketch, "E5231", {"start": v(70.34, -391.11) * mm, "end": v(70.13, -389.88) * mm});
            skLineSegment(sketch, "E5232", {"start": v(70.13, -389.88) * mm, "end": v(69.97, -388.62) * mm});
            skLineSegment(sketch, "E5233", {"start": v(69.97, -388.62) * mm, "end": v(69.85, -387.31) * mm});
            skLineSegment(sketch, "E5234", {"start": v(69.85, -387.31) * mm, "end": v(69.78, -385.98) * mm});
            skLineSegment(sketch, "E5235", {"start": v(69.78, -385.98) * mm, "end": v(69.76, -384.6) * mm});
            skLineSegment(sketch, "E5236", {"start": v(166.4, -371.36) * mm, "end": v(166.96, -371.36) * mm});
            skLineSegment(sketch, "E5237", {"start": v(166.96, -371.36) * mm, "end": v(172.6, -389.17) * mm});
            skLineSegment(sketch, "E5238", {"start": v(172.6, -389.17) * mm, "end": v(160.7, -389.17) * mm});
            skLineSegment(sketch, "E5239", {"start": v(160.7, -389.17) * mm, "end": v(166.4, -371.36) * mm});
            skLineSegment(sketch, "E5240", {"start": v(174.61, -396.5) * mm, "end": v(158.66, -396.5) * mm});
            skLineSegment(sketch, "E5241", {"start": v(158.66, -396.5) * mm, "end": v(155.16, -407.33) * mm});
            skLineSegment(sketch, "E5242", {"start": v(155.16, -407.33) * mm, "end": v(145.63, -407.33) * mm});
            skLineSegment(sketch, "E5243", {"start": v(145.63, -407.33) * mm, "end": v(161.4, -361.92) * mm});
            skLineSegment(sketch, "E5244", {"start": v(161.4, -361.92) * mm, "end": v(172.56, -361.92) * mm});
            skLineSegment(sketch, "E5245", {"start": v(172.56, -361.92) * mm, "end": v(188.33, -407.33) * mm});
            skLineSegment(sketch, "E5246", {"start": v(188.33, -407.33) * mm, "end": v(178.04, -407.33) * mm});
            skLineSegment(sketch, "E5247", {"start": v(178.04, -407.33) * mm, "end": v(174.61, -396.5) * mm});
            skLineSegment(sketch, "E5248", {"start": v(236.32, -370) * mm, "end": v(243.18, -370) * mm});
            skLineSegment(sketch, "E5249", {"start": v(243.18, -370) * mm, "end": v(243.94, -370.02) * mm});
            skLineSegment(sketch, "E5250", {"start": v(243.94, -370.02) * mm, "end": v(244.68, -370.07) * mm});
            skLineSegment(sketch, "E5251", {"start": v(244.68, -370.07) * mm, "end": v(245.4, -370.14) * mm});
            skLineSegment(sketch, "E5252", {"start": v(245.4, -370.14) * mm, "end": v(246.1, -370.25) * mm});
            skLineSegment(sketch, "E5253", {"start": v(246.1, -370.25) * mm, "end": v(246.8, -370.39) * mm});
            skLineSegment(sketch, "E5254", {"start": v(246.8, -370.39) * mm, "end": v(247.45, -370.55) * mm});
            skLineSegment(sketch, "E5255", {"start": v(247.45, -370.55) * mm, "end": v(248.09, -370.75) * mm});
            skLineSegment(sketch, "E5256", {"start": v(248.09, -370.75) * mm, "end": v(248.7, -370.97) * mm});
            skLineSegment(sketch, "E5257", {"start": v(248.7, -370.97) * mm, "end": v(249.3, -371.22) * mm});
            skLineSegment(sketch, "E5258", {"start": v(249.3, -371.22) * mm, "end": v(249.88, -371.5) * mm});
            skLineSegment(sketch, "E5259", {"start": v(249.88, -371.5) * mm, "end": v(250.43, -371.82) * mm});
            skLineSegment(sketch, "E5260", {"start": v(250.43, -371.82) * mm, "end": v(250.95, -372.15) * mm});
            skLineSegment(sketch, "E5261", {"start": v(250.95, -372.15) * mm, "end": v(251.46, -372.52) * mm});
            skLineSegment(sketch, "E5262", {"start": v(251.46, -372.52) * mm, "end": v(251.94, -372.91) * mm});
            skLineSegment(sketch, "E5263", {"start": v(251.94, -372.91) * mm, "end": v(252.4, -373.34) * mm});
            skLineSegment(sketch, "E5264", {"start": v(252.4, -373.34) * mm, "end": v(252.83, -373.78) * mm});
            skLineSegment(sketch, "E5265", {"start": v(252.83, -373.78) * mm, "end": v(253.24, -374.26) * mm});
            skLineSegment(sketch, "E5266", {"start": v(253.24, -374.26) * mm, "end": v(253.63, -374.76) * mm});
            skLineSegment(sketch, "E5267", {"start": v(253.63, -374.76) * mm, "end": v(253.99, -375.29) * mm});
            skLineSegment(sketch, "E5268", {"start": v(253.99, -375.29) * mm, "end": v(254.32, -375.84) * mm});
            skLineSegment(sketch, "E5269", {"start": v(254.32, -375.84) * mm, "end": v(254.63, -376.42) * mm});
            skLineSegment(sketch, "E5270", {"start": v(254.63, -376.42) * mm, "end": v(254.92, -377.03) * mm});
            skLineSegment(sketch, "E5271", {"start": v(254.92, -377.03) * mm, "end": v(255.18, -377.66) * mm});
            skLineSegment(sketch, "E5272", {"start": v(255.18, -377.66) * mm, "end": v(255.41, -378.32) * mm});
            skLineSegment(sketch, "E5273", {"start": v(255.41, -378.32) * mm, "end": v(255.62, -379) * mm});
            skLineSegment(sketch, "E5274", {"start": v(255.62, -379) * mm, "end": v(255.8, -379.7) * mm});
            skLineSegment(sketch, "E5275", {"start": v(255.8, -379.7) * mm, "end": v(255.95, -380.44) * mm});
            skLineSegment(sketch, "E5276", {"start": v(255.95, -380.44) * mm, "end": v(256.08, -381.2) * mm});
            skLineSegment(sketch, "E5277", {"start": v(256.08, -381.2) * mm, "end": v(256.18, -381.97) * mm});
            skLineSegment(sketch, "E5278", {"start": v(256.18, -381.97) * mm, "end": v(256.25, -382.78) * mm});
            skLineSegment(sketch, "E5279", {"start": v(256.25, -382.78) * mm, "end": v(256.29, -383.6) * mm});
            skLineSegment(sketch, "E5280", {"start": v(256.29, -383.6) * mm, "end": v(256.3, -384.45) * mm});
            skLineSegment(sketch, "E5281", {"start": v(256.3, -384.45) * mm, "end": v(256.29, -385.34) * mm});
            skLineSegment(sketch, "E5282", {"start": v(256.29, -385.34) * mm, "end": v(256.25, -386.2) * mm});
            skLineSegment(sketch, "E5283", {"start": v(256.25, -386.2) * mm, "end": v(256.18, -387.03) * mm});
            skLineSegment(sketch, "E5284", {"start": v(256.18, -387.03) * mm, "end": v(256.08, -387.84) * mm});
            skLineSegment(sketch, "E5285", {"start": v(256.08, -387.84) * mm, "end": v(255.96, -388.62) * mm});
            skLineSegment(sketch, "E5286", {"start": v(255.96, -388.62) * mm, "end": v(255.81, -389.38) * mm});
            skLineSegment(sketch, "E5287", {"start": v(255.81, -389.38) * mm, "end": v(255.64, -390.1) * mm});
            skLineSegment(sketch, "E5288", {"start": v(255.64, -390.1) * mm, "end": v(255.43, -390.8) * mm});
            skLineSegment(sketch, "E5289", {"start": v(255.43, -390.8) * mm, "end": v(255.2, -391.48) * mm});
            skLineSegment(sketch, "E5290", {"start": v(255.2, -391.48) * mm, "end": v(254.95, -392.13) * mm});
            skLineSegment(sketch, "E5291", {"start": v(254.95, -392.13) * mm, "end": v(254.67, -392.75) * mm});
            skLineSegment(sketch, "E5292", {"start": v(254.67, -392.75) * mm, "end": v(254.37, -393.34) * mm});
            skLineSegment(sketch, "E5293", {"start": v(254.37, -393.34) * mm, "end": v(254.03, -393.9) * mm});
            skLineSegment(sketch, "E5294", {"start": v(254.03, -393.9) * mm, "end": v(253.68, -394.44) * mm});
            skLineSegment(sketch, "E5295", {"start": v(253.68, -394.44) * mm, "end": v(253.3, -394.95) * mm});
            skLineSegment(sketch, "E5296", {"start": v(253.3, -394.95) * mm, "end": v(252.9, -395.43) * mm});
            skLineSegment(sketch, "E5297", {"start": v(252.9, -395.43) * mm, "end": v(252.46, -395.88) * mm});
            skLineSegment(sketch, "E5298", {"start": v(252.46, -395.88) * mm, "end": v(252, -396.3) * mm});
            skLineSegment(sketch, "E5299", {"start": v(252, -396.3) * mm, "end": v(251.53, -396.7) * mm});
            skLineSegment(sketch, "E5300", {"start": v(251.53, -396.7) * mm, "end": v(251.02, -397.07) * mm});
            skLineSegment(sketch, "E5301", {"start": v(251.02, -397.07) * mm, "end": v(250.5, -397.4) * mm});
            skLineSegment(sketch, "E5302", {"start": v(250.5, -397.4) * mm, "end": v(249.95, -397.72) * mm});
            skLineSegment(sketch, "E5303", {"start": v(249.95, -397.72) * mm, "end": v(249.37, -398) * mm});
            skLineSegment(sketch, "E5304", {"start": v(249.37, -398) * mm, "end": v(248.77, -398.25) * mm});
            skLineSegment(sketch, "E5305", {"start": v(248.77, -398.25) * mm, "end": v(248.15, -398.48) * mm});
            skLineSegment(sketch, "E5306", {"start": v(248.15, -398.48) * mm, "end": v(247.5, -398.67) * mm});
            skLineSegment(sketch, "E5307", {"start": v(247.5, -398.67) * mm, "end": v(246.84, -398.83) * mm});
            skLineSegment(sketch, "E5308", {"start": v(246.84, -398.83) * mm, "end": v(246.15, -398.97) * mm});
            skLineSegment(sketch, "E5309", {"start": v(246.15, -398.97) * mm, "end": v(245.44, -399.07) * mm});
            skLineSegment(sketch, "E5310", {"start": v(245.44, -399.07) * mm, "end": v(244.7, -399.15) * mm});
            skLineSegment(sketch, "E5311", {"start": v(244.7, -399.15) * mm, "end": v(243.95, -399.2) * mm});
            skLineSegment(sketch, "E5312", {"start": v(243.95, -399.2) * mm, "end": v(243.18, -399.2) * mm});
            skLineSegment(sketch, "E5313", {"start": v(243.18, -399.2) * mm, "end": v(236.32, -399.2) * mm});
            skLineSegment(sketch, "E5314", {"start": v(236.32, -399.2) * mm, "end": v(236.32, -370) * mm});
            skLineSegment(sketch, "E5315", {"start": v(244.69, -361.89) * mm, "end": v(245.94, -361.91) * mm});
            skLineSegment(sketch, "E5316", {"start": v(245.94, -361.91) * mm, "end": v(247.15, -361.98) * mm});
            skLineSegment(sketch, "E5317", {"start": v(247.15, -361.98) * mm, "end": v(248.33, -362.1) * mm});
            skLineSegment(sketch, "E5318", {"start": v(248.33, -362.1) * mm, "end": v(249.48, -362.27) * mm});
            skLineSegment(sketch, "E5319", {"start": v(249.48, -362.27) * mm, "end": v(250.6, -362.48) * mm});
            skLineSegment(sketch, "E5320", {"start": v(250.6, -362.48) * mm, "end": v(251.67, -362.74) * mm});
            skLineSegment(sketch, "E5321", {"start": v(251.67, -362.74) * mm, "end": v(252.7, -363.04) * mm});
            skLineSegment(sketch, "E5322", {"start": v(252.7, -363.04) * mm, "end": v(253.71, -363.39) * mm});
            skLineSegment(sketch, "E5323", {"start": v(253.71, -363.39) * mm, "end": v(254.68, -363.78) * mm});
            skLineSegment(sketch, "E5324", {"start": v(254.68, -363.78) * mm, "end": v(255.61, -364.22) * mm});
            skLineSegment(sketch, "E5325", {"start": v(255.61, -364.22) * mm, "end": v(256.5, -364.7) * mm});
            skLineSegment(sketch, "E5326", {"start": v(256.5, -364.7) * mm, "end": v(257.36, -365.23) * mm});
            skLineSegment(sketch, "E5327", {"start": v(257.36, -365.23) * mm, "end": v(258.18, -365.8) * mm});
            skLineSegment(sketch, "E5328", {"start": v(258.18, -365.8) * mm, "end": v(258.96, -366.4) * mm});
            skLineSegment(sketch, "E5329", {"start": v(258.96, -366.4) * mm, "end": v(259.7, -367.06) * mm});
            skLineSegment(sketch, "E5330", {"start": v(259.7, -367.06) * mm, "end": v(260.4, -367.76) * mm});
            skLineSegment(sketch, "E5331", {"start": v(260.4, -367.76) * mm, "end": v(261.06, -368.5) * mm});
            skLineSegment(sketch, "E5332", {"start": v(261.06, -368.5) * mm, "end": v(261.69, -369.27) * mm});
            skLineSegment(sketch, "E5333", {"start": v(261.69, -369.27) * mm, "end": v(262.27, -370.1) * mm});
            skLineSegment(sketch, "E5334", {"start": v(262.27, -370.1) * mm, "end": v(262.81, -370.95) * mm});
            skLineSegment(sketch, "E5335", {"start": v(262.81, -370.95) * mm, "end": v(263.31, -371.85) * mm});
            skLineSegment(sketch, "E5336", {"start": v(263.31, -371.85) * mm, "end": v(263.77, -372.8) * mm});
            skLineSegment(sketch, "E5337", {"start": v(263.77, -372.8) * mm, "end": v(264.19, -373.77) * mm});
            skLineSegment(sketch, "E5338", {"start": v(264.19, -373.77) * mm, "end": v(264.56, -374.8) * mm});
            skLineSegment(sketch, "E5339", {"start": v(264.56, -374.8) * mm, "end": v(264.9, -375.85) * mm});
            skLineSegment(sketch, "E5340", {"start": v(264.9, -375.85) * mm, "end": v(265.18, -376.94) * mm});
            skLineSegment(sketch, "E5341", {"start": v(265.18, -376.94) * mm, "end": v(265.43, -378.08) * mm});
            skLineSegment(sketch, "E5342", {"start": v(265.43, -378.08) * mm, "end": v(265.63, -379.25) * mm});
            skLineSegment(sketch, "E5343", {"start": v(265.63, -379.25) * mm, "end": v(265.79, -380.45) * mm});
            skLineSegment(sketch, "E5344", {"start": v(265.79, -380.45) * mm, "end": v(265.9, -381.7) * mm});
            skLineSegment(sketch, "E5345", {"start": v(265.9, -381.7) * mm, "end": v(265.97, -382.98) * mm});
            skLineSegment(sketch, "E5346", {"start": v(265.97, -382.98) * mm, "end": v(266, -384.3) * mm});
            skLineSegment(sketch, "E5347", {"start": v(266, -384.3) * mm, "end": v(265.97, -385.66) * mm});
            skLineSegment(sketch, "E5348", {"start": v(265.97, -385.66) * mm, "end": v(265.9, -386.98) * mm});
            skLineSegment(sketch, "E5349", {"start": v(265.9, -386.98) * mm, "end": v(265.8, -388.27) * mm});
            skLineSegment(sketch, "E5350", {"start": v(265.8, -388.27) * mm, "end": v(265.63, -389.52) * mm});
            skLineSegment(sketch, "E5351", {"start": v(265.63, -389.52) * mm, "end": v(265.43, -390.73) * mm});
            skLineSegment(sketch, "E5352", {"start": v(265.43, -390.73) * mm, "end": v(265.2, -391.9) * mm});
            skLineSegment(sketch, "E5353", {"start": v(265.2, -391.9) * mm, "end": v(264.9, -393.03) * mm});
            skLineSegment(sketch, "E5354", {"start": v(264.9, -393.03) * mm, "end": v(264.57, -394.12) * mm});
            skLineSegment(sketch, "E5355", {"start": v(264.57, -394.12) * mm, "end": v(264.2, -395.17) * mm});
            skLineSegment(sketch, "E5356", {"start": v(264.2, -395.17) * mm, "end": v(263.79, -396.18) * mm});
            skLineSegment(sketch, "E5357", {"start": v(263.79, -396.18) * mm, "end": v(263.33, -397.14) * mm});
            skLineSegment(sketch, "E5358", {"start": v(263.33, -397.14) * mm, "end": v(262.84, -398.07) * mm});
            skLineSegment(sketch, "E5359", {"start": v(262.84, -398.07) * mm, "end": v(262.3, -398.95) * mm});
            skLineSegment(sketch, "E5360", {"start": v(262.3, -398.95) * mm, "end": v(261.72, -399.8) * mm});
            skLineSegment(sketch, "E5361", {"start": v(261.72, -399.8) * mm, "end": v(261.1, -400.6) * mm});
            skLineSegment(sketch, "E5362", {"start": v(261.1, -400.6) * mm, "end": v(260.44, -401.35) * mm});
            skLineSegment(sketch, "E5363", {"start": v(260.44, -401.35) * mm, "end": v(259.74, -402.06) * mm});
            skLineSegment(sketch, "E5364", {"start": v(259.74, -402.06) * mm, "end": v(259, -402.73) * mm});
            skLineSegment(sketch, "E5365", {"start": v(259, -402.73) * mm, "end": v(258.22, -403.35) * mm});
            skLineSegment(sketch, "E5366", {"start": v(258.22, -403.35) * mm, "end": v(257.4, -403.93) * mm});
            skLineSegment(sketch, "E5367", {"start": v(257.4, -403.93) * mm, "end": v(256.55, -404.47) * mm});
            skLineSegment(sketch, "E5368", {"start": v(256.55, -404.47) * mm, "end": v(255.65, -404.96) * mm});
            skLineSegment(sketch, "E5369", {"start": v(255.65, -404.96) * mm, "end": v(254.72, -405.4) * mm});
            skLineSegment(sketch, "E5370", {"start": v(254.72, -405.4) * mm, "end": v(253.75, -405.8) * mm});
            skLineSegment(sketch, "E5371", {"start": v(253.75, -405.8) * mm, "end": v(252.74, -406.16) * mm});
            skLineSegment(sketch, "E5372", {"start": v(252.74, -406.16) * mm, "end": v(251.7, -406.47) * mm});
            skLineSegment(sketch, "E5373", {"start": v(251.7, -406.47) * mm, "end": v(250.62, -406.73) * mm});
            skLineSegment(sketch, "E5374", {"start": v(250.62, -406.73) * mm, "end": v(249.5, -406.94) * mm});
            skLineSegment(sketch, "E5375", {"start": v(249.5, -406.94) * mm, "end": v(248.35, -407.11) * mm});
            skLineSegment(sketch, "E5376", {"start": v(248.35, -407.11) * mm, "end": v(247.17, -407.23) * mm});
            skLineSegment(sketch, "E5377", {"start": v(247.17, -407.23) * mm, "end": v(245.94, -407.3) * mm});
            skLineSegment(sketch, "E5378", {"start": v(245.94, -407.3) * mm, "end": v(244.69, -407.33) * mm});
            skLineSegment(sketch, "E5379", {"start": v(244.69, -407.33) * mm, "end": v(226.81, -407.33) * mm});
            skLineSegment(sketch, "E5380", {"start": v(226.81, -407.33) * mm, "end": v(226.81, -361.89) * mm});
            skLineSegment(sketch, "E5381", {"start": v(226.81, -361.89) * mm, "end": v(244.69, -361.89) * mm});
            skLineSegment(sketch, "E5382", {"start": v(335.79, -407.33) * mm, "end": v(305.7, -407.33) * mm});
            skLineSegment(sketch, "E5383", {"start": v(305.7, -407.33) * mm, "end": v(305.7, -361.92) * mm});
            skLineSegment(sketch, "E5384", {"start": v(305.7, -361.92) * mm, "end": v(335.79, -361.92) * mm});
            skLineSegment(sketch, "E5385", {"start": v(335.79, -361.92) * mm, "end": v(335.79, -370.04) * mm});
            skLineSegment(sketch, "E5386", {"start": v(335.79, -370.04) * mm, "end": v(315.2, -370.04) * mm});
            skLineSegment(sketch, "E5387", {"start": v(315.2, -370.04) * mm, "end": v(315.2, -380.64) * mm});
            skLineSegment(sketch, "E5388", {"start": v(315.2, -380.64) * mm, "end": v(334.62, -380.64) * mm});
            skLineSegment(sketch, "E5389", {"start": v(334.62, -380.64) * mm, "end": v(334.62, -388.16) * mm});
            skLineSegment(sketch, "E5390", {"start": v(334.62, -388.16) * mm, "end": v(315.2, -388.16) * mm});
            skLineSegment(sketch, "E5391", {"start": v(315.2, -388.16) * mm, "end": v(315.2, -399.21) * mm});
            skLineSegment(sketch, "E5392", {"start": v(315.2, -399.21) * mm, "end": v(335.79, -399.21) * mm});
            skLineSegment(sketch, "E5393", {"start": v(335.79, -399.21) * mm, "end": v(335.79, -407.33) * mm});
            skLineSegment(sketch, "E5394", {"start": v(376.53, -407.33) * mm, "end": v(376.53, -361.92) * mm});
            skLineSegment(sketch, "E5395", {"start": v(376.53, -361.92) * mm, "end": v(387.74, -361.92) * mm});
            skLineSegment(sketch, "E5396", {"start": v(387.74, -361.92) * mm, "end": v(400.3, -392.44) * mm});
            skLineSegment(sketch, "E5397", {"start": v(400.3, -392.44) * mm, "end": v(400.86, -392.44) * mm});
            skLineSegment(sketch, "E5398", {"start": v(400.86, -392.44) * mm, "end": v(413.45, -361.92) * mm});
            skLineSegment(sketch, "E5399", {"start": v(413.45, -361.92) * mm, "end": v(424.62, -361.92) * mm});
            skLineSegment(sketch, "E5400", {"start": v(424.62, -361.92) * mm, "end": v(424.62, -407.33) * mm});
            skLineSegment(sketch, "E5401", {"start": v(424.62, -407.33) * mm, "end": v(415.8, -407.33) * mm});
            skLineSegment(sketch, "E5402", {"start": v(415.8, -407.33) * mm, "end": v(415.8, -376.96) * mm});
            skLineSegment(sketch, "E5403", {"start": v(415.8, -376.96) * mm, "end": v(415.3, -376.96) * mm});
            skLineSegment(sketch, "E5404", {"start": v(415.3, -376.96) * mm, "end": v(403.76, -404.72) * mm});
            skLineSegment(sketch, "E5405", {"start": v(403.76, -404.72) * mm, "end": v(397.43, -404.72) * mm});
            skLineSegment(sketch, "E5406", {"start": v(397.43, -404.72) * mm, "end": v(385.85, -376.96) * mm});
            skLineSegment(sketch, "E5407", {"start": v(385.85, -376.96) * mm, "end": v(385.35, -376.96) * mm});
            skLineSegment(sketch, "E5408", {"start": v(385.35, -376.96) * mm, "end": v(385.35, -407.33) * mm});
            skLineSegment(sketch, "E5409", {"start": v(385.35, -407.33) * mm, "end": v(376.53, -407.33) * mm});
            skLineSegment(sketch, "E5410", {"start": v(478.96, -407.33) * mm, "end": v(478.96, -390.62) * mm});
            skLineSegment(sketch, "E5411", {"start": v(478.96, -390.62) * mm, "end": v(463.14, -361.92) * mm});
            skLineSegment(sketch, "E5412", {"start": v(463.14, -361.92) * mm, "end": v(473.43, -361.92) * mm});
            skLineSegment(sketch, "E5413", {"start": v(473.43, -361.92) * mm, "end": v(483.43, -380.93) * mm});
            skLineSegment(sketch, "E5414", {"start": v(483.43, -380.93) * mm, "end": v(484, -380.93) * mm});
            skLineSegment(sketch, "E5415", {"start": v(484, -380.93) * mm, "end": v(493.97, -361.92) * mm});
            skLineSegment(sketch, "E5416", {"start": v(493.97, -361.92) * mm, "end": v(504.27, -361.92) * mm});
            skLineSegment(sketch, "E5417", {"start": v(504.27, -361.92) * mm, "end": v(488.47, -390.62) * mm});
            skLineSegment(sketch, "E5418", {"start": v(488.47, -390.62) * mm, "end": v(488.47, -407.33) * mm});
            skLineSegment(sketch, "E5419", {"start": v(488.47, -407.33) * mm, "end": v(478.96, -407.33) * mm});
            skLineSegment(sketch, "E5420", {"start": v(-489.55, -474.72) * mm, "end": v(-507.93, -474.72) * mm});
            skLineSegment(sketch, "E5421", {"start": v(-507.93, -474.72) * mm, "end": v(-507.93, -444.45) * mm});
            skLineSegment(sketch, "E5422", {"start": v(-507.93, -444.45) * mm, "end": v(-504.15, -444.45) * mm});
            skLineSegment(sketch, "E5423", {"start": v(-504.15, -444.45) * mm, "end": v(-504.15, -471.33) * mm});
            skLineSegment(sketch, "E5424", {"start": v(-504.15, -471.33) * mm, "end": v(-489.55, -471.33) * mm});
            skLineSegment(sketch, "E5425", {"start": v(-489.55, -471.33) * mm, "end": v(-489.55, -474.72) * mm});
            skLineSegment(sketch, "E5426", {"start": v(-400.47, -474.72) * mm, "end": v(-419.23, -474.72) * mm});
            skLineSegment(sketch, "E5427", {"start": v(-419.23, -474.72) * mm, "end": v(-419.23, -444.45) * mm});
            skLineSegment(sketch, "E5428", {"start": v(-419.23, -444.45) * mm, "end": v(-400.47, -444.45) * mm});
            skLineSegment(sketch, "E5429", {"start": v(-400.47, -444.45) * mm, "end": v(-400.47, -447.85) * mm});
            skLineSegment(sketch, "E5430", {"start": v(-400.47, -447.85) * mm, "end": v(-415.45, -447.85) * mm});
            skLineSegment(sketch, "E5431", {"start": v(-415.45, -447.85) * mm, "end": v(-415.45, -457.56) * mm});
            skLineSegment(sketch, "E5432", {"start": v(-415.45, -457.56) * mm, "end": v(-401.25, -457.56) * mm});
            skLineSegment(sketch, "E5433", {"start": v(-401.25, -457.56) * mm, "end": v(-401.25, -460.92) * mm});
            skLineSegment(sketch, "E5434", {"start": v(-401.25, -460.92) * mm, "end": v(-415.45, -460.92) * mm});
            skLineSegment(sketch, "E5435", {"start": v(-415.45, -460.92) * mm, "end": v(-415.45, -471.33) * mm});
            skLineSegment(sketch, "E5436", {"start": v(-415.45, -471.33) * mm, "end": v(-400.47, -471.33) * mm});
            skLineSegment(sketch, "E5437", {"start": v(-400.47, -471.33) * mm, "end": v(-400.47, -474.72) * mm});
            skLineSegment(sketch, "E5438", {"start": v(-321.47, -474.72) * mm, "end": v(-321.47, -447.85) * mm});
            skLineSegment(sketch, "E5439", {"start": v(-321.47, -447.85) * mm, "end": v(-331.22, -447.85) * mm});
            skLineSegment(sketch, "E5440", {"start": v(-331.22, -447.85) * mm, "end": v(-331.22, -444.45) * mm});
            skLineSegment(sketch, "E5441", {"start": v(-331.22, -444.45) * mm, "end": v(-307.93, -444.45) * mm});
            skLineSegment(sketch, "E5442", {"start": v(-307.93, -444.45) * mm, "end": v(-307.93, -447.85) * mm});
            skLineSegment(sketch, "E5443", {"start": v(-307.93, -447.85) * mm, "end": v(-317.7, -447.85) * mm});
            skLineSegment(sketch, "E5444", {"start": v(-317.7, -447.85) * mm, "end": v(-317.7, -474.72) * mm});
            skLineSegment(sketch, "E5445", {"start": v(-317.7, -474.72) * mm, "end": v(-321.47, -474.72) * mm});
            skLineSegment(sketch, "E5446", {"start": v(-235.43, -466.4) * mm, "end": v(-235.4, -466.7) * mm});
            skLineSegment(sketch, "E5447", {"start": v(-235.4, -466.7) * mm, "end": v(-235.33, -467) * mm});
            skLineSegment(sketch, "E5448", {"start": v(-235.33, -467) * mm, "end": v(-235.26, -467.28) * mm});
            skLineSegment(sketch, "E5449", {"start": v(-235.26, -467.28) * mm, "end": v(-235.17, -467.57) * mm});
            skLineSegment(sketch, "E5450", {"start": v(-235.17, -467.57) * mm, "end": v(-235.07, -467.84) * mm});
            skLineSegment(sketch, "E5451", {"start": v(-235.07, -467.84) * mm, "end": v(-234.95, -468.1) * mm});
            skLineSegment(sketch, "E5452", {"start": v(-234.95, -468.1) * mm, "end": v(-234.82, -468.37) * mm});
            skLineSegment(sketch, "E5453", {"start": v(-234.82, -468.37) * mm, "end": v(-234.67, -468.62) * mm});
            skLineSegment(sketch, "E5454", {"start": v(-234.67, -468.62) * mm, "end": v(-234.51, -468.87) * mm});
            skLineSegment(sketch, "E5455", {"start": v(-234.51, -468.87) * mm, "end": v(-234.34, -469.1) * mm});
            skLineSegment(sketch, "E5456", {"start": v(-234.34, -469.1) * mm, "end": v(-234.15, -469.33) * mm});
            skLineSegment(sketch, "E5457", {"start": v(-234.15, -469.33) * mm, "end": v(-233.95, -469.55) * mm});
            skLineSegment(sketch, "E5458", {"start": v(-233.95, -469.55) * mm, "end": v(-233.74, -469.76) * mm});
            skLineSegment(sketch, "E5459", {"start": v(-233.74, -469.76) * mm, "end": v(-233.51, -469.96) * mm});
            skLineSegment(sketch, "E5460", {"start": v(-233.51, -469.96) * mm, "end": v(-233.03, -470.34) * mm});
            skLineSegment(sketch, "E5461", {"start": v(-233.03, -470.34) * mm, "end": v(-232.5, -470.67) * mm});
            skLineSegment(sketch, "E5462", {"start": v(-232.5, -470.67) * mm, "end": v(-231.92, -470.97) * mm});
            skLineSegment(sketch, "E5463", {"start": v(-231.92, -470.97) * mm, "end": v(-231.3, -471.23) * mm});
            skLineSegment(sketch, "E5464", {"start": v(-231.3, -471.23) * mm, "end": v(-230.64, -471.44) * mm});
            skLineSegment(sketch, "E5465", {"start": v(-230.64, -471.44) * mm, "end": v(-229.94, -471.6) * mm});
            skLineSegment(sketch, "E5466", {"start": v(-229.94, -471.6) * mm, "end": v(-229.21, -471.73) * mm});
            skLineSegment(sketch, "E5467", {"start": v(-229.21, -471.73) * mm, "end": v(-228.45, -471.8) * mm});
            skLineSegment(sketch, "E5468", {"start": v(-228.45, -471.8) * mm, "end": v(-227.65, -471.83) * mm});
            skLineSegment(sketch, "E5469", {"start": v(-227.65, -471.83) * mm, "end": v(-226.9, -471.8) * mm});
            skLineSegment(sketch, "E5470", {"start": v(-226.9, -471.8) * mm, "end": v(-226.17, -471.73) * mm});
            skLineSegment(sketch, "E5471", {"start": v(-226.17, -471.73) * mm, "end": v(-225.48, -471.6) * mm});
            skLineSegment(sketch, "E5472", {"start": v(-225.48, -471.6) * mm, "end": v(-224.82, -471.44) * mm});
            skLineSegment(sketch, "E5473", {"start": v(-224.82, -471.44) * mm, "end": v(-224.2, -471.24) * mm});
            skLineSegment(sketch, "E5474", {"start": v(-224.2, -471.24) * mm, "end": v(-223.62, -470.99) * mm});
            skLineSegment(sketch, "E5475", {"start": v(-223.62, -470.99) * mm, "end": v(-223.08, -470.7) * mm});
            skLineSegment(sketch, "E5476", {"start": v(-223.08, -470.7) * mm, "end": v(-222.58, -470.37) * mm});
            skLineSegment(sketch, "E5477", {"start": v(-222.58, -470.37) * mm, "end": v(-222.13, -470.02) * mm});
            skLineSegment(sketch, "E5478", {"start": v(-222.13, -470.02) * mm, "end": v(-221.74, -469.62) * mm});
            skLineSegment(sketch, "E5479", {"start": v(-221.74, -469.62) * mm, "end": v(-221.56, -469.41) * mm});
            skLineSegment(sketch, "E5480", {"start": v(-221.56, -469.41) * mm, "end": v(-221.4, -469.2) * mm});
            skLineSegment(sketch, "E5481", {"start": v(-221.4, -469.2) * mm, "end": v(-221.25, -468.98) * mm});
            skLineSegment(sketch, "E5482", {"start": v(-221.25, -468.98) * mm, "end": v(-221.1, -468.75) * mm});
            skLineSegment(sketch, "E5483", {"start": v(-221.1, -468.75) * mm, "end": v(-220.99, -468.51) * mm});
            skLineSegment(sketch, "E5484", {"start": v(-220.99, -468.51) * mm, "end": v(-220.88, -468.27) * mm});
            skLineSegment(sketch, "E5485", {"start": v(-220.88, -468.27) * mm, "end": v(-220.8, -468.02) * mm});
            skLineSegment(sketch, "E5486", {"start": v(-220.8, -468.02) * mm, "end": v(-220.72, -467.76) * mm});
            skLineSegment(sketch, "E5487", {"start": v(-220.72, -467.76) * mm, "end": v(-220.66, -467.5) * mm});
            skLineSegment(sketch, "E5488", {"start": v(-220.66, -467.5) * mm, "end": v(-220.61, -467.24) * mm});
            skLineSegment(sketch, "E5489", {"start": v(-220.61, -467.24) * mm, "end": v(-220.59, -466.96) * mm});
            skLineSegment(sketch, "E5490", {"start": v(-220.59, -466.96) * mm, "end": v(-220.58, -466.69) * mm});
            skLineSegment(sketch, "E5491", {"start": v(-220.58, -466.69) * mm, "end": v(-220.6, -466.22) * mm});
            skLineSegment(sketch, "E5492", {"start": v(-220.6, -466.22) * mm, "end": v(-220.66, -465.77) * mm});
            skLineSegment(sketch, "E5493", {"start": v(-220.66, -465.77) * mm, "end": v(-220.77, -465.35) * mm});
            skLineSegment(sketch, "E5494", {"start": v(-220.77, -465.35) * mm, "end": v(-220.92, -464.95) * mm});
            skLineSegment(sketch, "E5495", {"start": v(-220.92, -464.95) * mm, "end": v(-221.12, -464.56) * mm});
            skLineSegment(sketch, "E5496", {"start": v(-221.12, -464.56) * mm, "end": v(-221.36, -464.2) * mm});
            skLineSegment(sketch, "E5497", {"start": v(-221.36, -464.2) * mm, "end": v(-221.65, -463.86) * mm});
            skLineSegment(sketch, "E5498", {"start": v(-221.65, -463.86) * mm, "end": v(-221.98, -463.53) * mm});
            skLineSegment(sketch, "E5499", {"start": v(-221.98, -463.53) * mm, "end": v(-222.36, -463.22) * mm});
            skLineSegment(sketch, "E5500", {"start": v(-222.36, -463.22) * mm, "end": v(-222.8, -462.93) * mm});
            skLineSegment(sketch, "E5501", {"start": v(-222.8, -462.93) * mm, "end": v(-223.27, -462.66) * mm});
            skLineSegment(sketch, "E5502", {"start": v(-223.27, -462.66) * mm, "end": v(-223.8, -462.4) * mm});
            skLineSegment(sketch, "E5503", {"start": v(-223.8, -462.4) * mm, "end": v(-224.38, -462.16) * mm});
            skLineSegment(sketch, "E5504", {"start": v(-224.38, -462.16) * mm, "end": v(-225.01, -461.93) * mm});
            skLineSegment(sketch, "E5505", {"start": v(-225.01, -461.93) * mm, "end": v(-225.7, -461.71) * mm});
            skLineSegment(sketch, "E5506", {"start": v(-225.7, -461.71) * mm, "end": v(-226.43, -461.5) * mm});
            skLineSegment(sketch, "E5507", {"start": v(-226.43, -461.5) * mm, "end": v(-230.31, -460.5) * mm});
            skLineSegment(sketch, "E5508", {"start": v(-230.31, -460.5) * mm, "end": v(-231.32, -460.22) * mm});
            skLineSegment(sketch, "E5509", {"start": v(-231.32, -460.22) * mm, "end": v(-232.26, -459.92) * mm});
            skLineSegment(sketch, "E5510", {"start": v(-232.26, -459.92) * mm, "end": v(-233.13, -459.58) * mm});
            skLineSegment(sketch, "E5511", {"start": v(-233.13, -459.58) * mm, "end": v(-233.93, -459.23) * mm});
            skLineSegment(sketch, "E5512", {"start": v(-233.93, -459.23) * mm, "end": v(-234.66, -458.84) * mm});
            skLineSegment(sketch, "E5513", {"start": v(-234.66, -458.84) * mm, "end": v(-235, -458.64) * mm});
            skLineSegment(sketch, "E5514", {"start": v(-235, -458.64) * mm, "end": v(-235.32, -458.43) * mm});
            skLineSegment(sketch, "E5515", {"start": v(-235.32, -458.43) * mm, "end": v(-235.62, -458.2) * mm});
            skLineSegment(sketch, "E5516", {"start": v(-235.62, -458.2) * mm, "end": v(-235.9, -457.98) * mm});
            skLineSegment(sketch, "E5517", {"start": v(-235.9, -457.98) * mm, "end": v(-236.18, -457.75) * mm});
            skLineSegment(sketch, "E5518", {"start": v(-236.18, -457.75) * mm, "end": v(-236.44, -457.5) * mm});
            skLineSegment(sketch, "E5519", {"start": v(-236.44, -457.5) * mm, "end": v(-236.67, -457.26) * mm});
            skLineSegment(sketch, "E5520", {"start": v(-236.67, -457.26) * mm, "end": v(-236.9, -457) * mm});
            skLineSegment(sketch, "E5521", {"start": v(-236.9, -457) * mm, "end": v(-237.1, -456.74) * mm});
            skLineSegment(sketch, "E5522", {"start": v(-237.1, -456.74) * mm, "end": v(-237.3, -456.46) * mm});
            skLineSegment(sketch, "E5523", {"start": v(-237.3, -456.46) * mm, "end": v(-237.47, -456.18) * mm});
            skLineSegment(sketch, "E5524", {"start": v(-237.47, -456.18) * mm, "end": v(-237.63, -455.9) * mm});
            skLineSegment(sketch, "E5525", {"start": v(-237.63, -455.9) * mm, "end": v(-237.77, -455.6) * mm});
            skLineSegment(sketch, "E5526", {"start": v(-237.77, -455.6) * mm, "end": v(-237.9, -455.29) * mm});
            skLineSegment(sketch, "E5527", {"start": v(-237.9, -455.29) * mm, "end": v(-238, -454.97) * mm});
            skLineSegment(sketch, "E5528", {"start": v(-238, -454.97) * mm, "end": v(-238.1, -454.65) * mm});
            skLineSegment(sketch, "E5529", {"start": v(-238.1, -454.65) * mm, "end": v(-238.19, -454.31) * mm});
            skLineSegment(sketch, "E5530", {"start": v(-238.19, -454.31) * mm, "end": v(-238.25, -453.97) * mm});
            skLineSegment(sketch, "E5531", {"start": v(-238.25, -453.97) * mm, "end": v(-238.3, -453.62) * mm});
            skLineSegment(sketch, "E5532", {"start": v(-238.3, -453.62) * mm, "end": v(-238.34, -453.26) * mm});
            skLineSegment(sketch, "E5533", {"start": v(-238.34, -453.26) * mm, "end": v(-238.36, -452.89) * mm});
            skLineSegment(sketch, "E5534", {"start": v(-238.36, -452.89) * mm, "end": v(-238.37, -452.5) * mm});
            skLineSegment(sketch, "E5535", {"start": v(-238.37, -452.5) * mm, "end": v(-238.36, -452.04) * mm});
            skLineSegment(sketch, "E5536", {"start": v(-238.36, -452.04) * mm, "end": v(-238.32, -451.58) * mm});
            skLineSegment(sketch, "E5537", {"start": v(-238.32, -451.58) * mm, "end": v(-238.26, -451.13) * mm});
            skLineSegment(sketch, "E5538", {"start": v(-238.26, -451.13) * mm, "end": v(-238.17, -450.7) * mm});
            skLineSegment(sketch, "E5539", {"start": v(-238.17, -450.7) * mm, "end": v(-238.06, -450.26) * mm});
            skLineSegment(sketch, "E5540", {"start": v(-238.06, -450.26) * mm, "end": v(-237.92, -449.85) * mm});
            skLineSegment(sketch, "E5541", {"start": v(-237.92, -449.85) * mm, "end": v(-237.76, -449.44) * mm});
            skLineSegment(sketch, "E5542", {"start": v(-237.76, -449.44) * mm, "end": v(-237.58, -449.04) * mm});
            skLineSegment(sketch, "E5543", {"start": v(-237.58, -449.04) * mm, "end": v(-237.38, -448.66) * mm});
            skLineSegment(sketch, "E5544", {"start": v(-237.38, -448.66) * mm, "end": v(-237.16, -448.29) * mm});
            skLineSegment(sketch, "E5545", {"start": v(-237.16, -448.29) * mm, "end": v(-236.91, -447.93) * mm});
            skLineSegment(sketch, "E5546", {"start": v(-236.91, -447.93) * mm, "end": v(-236.64, -447.58) * mm});
            skLineSegment(sketch, "E5547", {"start": v(-236.64, -447.58) * mm, "end": v(-236.36, -447.25) * mm});
            skLineSegment(sketch, "E5548", {"start": v(-236.36, -447.25) * mm, "end": v(-236.05, -446.93) * mm});
            skLineSegment(sketch, "E5549", {"start": v(-236.05, -446.93) * mm, "end": v(-235.73, -446.63) * mm});
            skLineSegment(sketch, "E5550", {"start": v(-235.73, -446.63) * mm, "end": v(-235.38, -446.34) * mm});
            skLineSegment(sketch, "E5551", {"start": v(-235.38, -446.34) * mm, "end": v(-235.02, -446.06) * mm});
            skLineSegment(sketch, "E5552", {"start": v(-235.02, -446.06) * mm, "end": v(-234.64, -445.8) * mm});
            skLineSegment(sketch, "E5553", {"start": v(-234.64, -445.8) * mm, "end": v(-234.24, -445.55) * mm});
            skLineSegment(sketch, "E5554", {"start": v(-234.24, -445.55) * mm, "end": v(-233.82, -445.33) * mm});
            skLineSegment(sketch, "E5555", {"start": v(-233.82, -445.33) * mm, "end": v(-233.39, -445.11) * mm});
            skLineSegment(sketch, "E5556", {"start": v(-233.39, -445.11) * mm, "end": v(-232.94, -444.92) * mm});
            skLineSegment(sketch, "E5557", {"start": v(-232.94, -444.92) * mm, "end": v(-232.48, -444.74) * mm});
            skLineSegment(sketch, "E5558", {"start": v(-232.48, -444.74) * mm, "end": v(-232, -444.57) * mm});
            skLineSegment(sketch, "E5559", {"start": v(-232, -444.57) * mm, "end": v(-231.5, -444.43) * mm});
            skLineSegment(sketch, "E5560", {"start": v(-231.5, -444.43) * mm, "end": v(-231, -444.3) * mm});
            skLineSegment(sketch, "E5561", {"start": v(-231, -444.3) * mm, "end": v(-230.47, -444.2) * mm});
            skLineSegment(sketch, "E5562", {"start": v(-230.47, -444.2) * mm, "end": v(-229.94, -444.1) * mm});
            skLineSegment(sketch, "E5563", {"start": v(-229.94, -444.1) * mm, "end": v(-229.39, -444.04) * mm});
            skLineSegment(sketch, "E5564", {"start": v(-229.39, -444.04) * mm, "end": v(-228.83, -443.98) * mm});
            skLineSegment(sketch, "E5565", {"start": v(-228.83, -443.98) * mm, "end": v(-228.26, -443.95) * mm});
            skLineSegment(sketch, "E5566", {"start": v(-228.26, -443.95) * mm, "end": v(-227.67, -443.94) * mm});
            skLineSegment(sketch, "E5567", {"start": v(-227.67, -443.94) * mm, "end": v(-227.11, -443.95) * mm});
            skLineSegment(sketch, "E5568", {"start": v(-227.11, -443.95) * mm, "end": v(-226.56, -443.99) * mm});
            skLineSegment(sketch, "E5569", {"start": v(-226.56, -443.99) * mm, "end": v(-226.02, -444.04) * mm});
            skLineSegment(sketch, "E5570", {"start": v(-226.02, -444.04) * mm, "end": v(-225.5, -444.1) * mm});
            skLineSegment(sketch, "E5571", {"start": v(-225.5, -444.1) * mm, "end": v(-224.98, -444.2) * mm});
            skLineSegment(sketch, "E5572", {"start": v(-224.98, -444.2) * mm, "end": v(-224.48, -444.3) * mm});
            skLineSegment(sketch, "E5573", {"start": v(-224.48, -444.3) * mm, "end": v(-223.98, -444.43) * mm});
            skLineSegment(sketch, "E5574", {"start": v(-223.98, -444.43) * mm, "end": v(-223.5, -444.58) * mm});
            skLineSegment(sketch, "E5575", {"start": v(-223.5, -444.58) * mm, "end": v(-223.04, -444.74) * mm});
            skLineSegment(sketch, "E5576", {"start": v(-223.04, -444.74) * mm, "end": v(-222.59, -444.93) * mm});
            skLineSegment(sketch, "E5577", {"start": v(-222.59, -444.93) * mm, "end": v(-222.15, -445.12) * mm});
            skLineSegment(sketch, "E5578", {"start": v(-222.15, -445.12) * mm, "end": v(-221.73, -445.34) * mm});
            skLineSegment(sketch, "E5579", {"start": v(-221.73, -445.34) * mm, "end": v(-221.32, -445.57) * mm});
            skLineSegment(sketch, "E5580", {"start": v(-221.32, -445.57) * mm, "end": v(-220.93, -445.82) * mm});
            skLineSegment(sketch, "E5581", {"start": v(-220.93, -445.82) * mm, "end": v(-220.56, -446.08) * mm});
            skLineSegment(sketch, "E5582", {"start": v(-220.56, -446.08) * mm, "end": v(-220.2, -446.36) * mm});
            skLineSegment(sketch, "E5583", {"start": v(-220.2, -446.36) * mm, "end": v(-219.86, -446.66) * mm});
            skLineSegment(sketch, "E5584", {"start": v(-219.86, -446.66) * mm, "end": v(-219.53, -446.96) * mm});
            skLineSegment(sketch, "E5585", {"start": v(-219.53, -446.96) * mm, "end": v(-219.23, -447.29) * mm});
            skLineSegment(sketch, "E5586", {"start": v(-219.23, -447.29) * mm, "end": v(-218.94, -447.62) * mm});
            skLineSegment(sketch, "E5587", {"start": v(-218.94, -447.62) * mm, "end": v(-218.67, -447.97) * mm});
            skLineSegment(sketch, "E5588", {"start": v(-218.67, -447.97) * mm, "end": v(-218.43, -448.33) * mm});
            skLineSegment(sketch, "E5589", {"start": v(-218.43, -448.33) * mm, "end": v(-218.2, -448.7) * mm});
            skLineSegment(sketch, "E5590", {"start": v(-218.2, -448.7) * mm, "end": v(-218, -449.1) * mm});
            skLineSegment(sketch, "E5591", {"start": v(-218, -449.1) * mm, "end": v(-217.8, -449.5) * mm});
            skLineSegment(sketch, "E5592", {"start": v(-217.8, -449.5) * mm, "end": v(-217.64, -449.9) * mm});
            skLineSegment(sketch, "E5593", {"start": v(-217.64, -449.9) * mm, "end": v(-217.5, -450.33) * mm});
            skLineSegment(sketch, "E5594", {"start": v(-217.5, -450.33) * mm, "end": v(-217.37, -450.76) * mm});
            skLineSegment(sketch, "E5595", {"start": v(-217.37, -450.76) * mm, "end": v(-217.27, -451.2) * mm});
            skLineSegment(sketch, "E5596", {"start": v(-217.27, -451.2) * mm, "end": v(-217.2, -451.65) * mm});
            skLineSegment(sketch, "E5597", {"start": v(-217.2, -451.65) * mm, "end": v(-217.15, -452.12) * mm});
            skLineSegment(sketch, "E5598", {"start": v(-217.15, -452.12) * mm, "end": v(-217.12, -452.59) * mm});
            skLineSegment(sketch, "E5599", {"start": v(-217.12, -452.59) * mm, "end": v(-220.9, -452.59) * mm});
            skLineSegment(sketch, "E5600", {"start": v(-220.9, -452.59) * mm, "end": v(-220.98, -452) * mm});
            skLineSegment(sketch, "E5601", {"start": v(-220.98, -452) * mm, "end": v(-221.13, -451.43) * mm});
            skLineSegment(sketch, "E5602", {"start": v(-221.13, -451.43) * mm, "end": v(-221.32, -450.9) * mm});
            skLineSegment(sketch, "E5603", {"start": v(-221.32, -450.9) * mm, "end": v(-221.56, -450.4) * mm});
            skLineSegment(sketch, "E5604", {"start": v(-221.56, -450.4) * mm, "end": v(-221.85, -449.93) * mm});
            skLineSegment(sketch, "E5605", {"start": v(-221.85, -449.93) * mm, "end": v(-222.19, -449.5) * mm});
            skLineSegment(sketch, "E5606", {"start": v(-222.19, -449.5) * mm, "end": v(-222.57, -449.1) * mm});
            skLineSegment(sketch, "E5607", {"start": v(-222.57, -449.1) * mm, "end": v(-223, -448.75) * mm});
            skLineSegment(sketch, "E5608", {"start": v(-223, -448.75) * mm, "end": v(-223.46, -448.43) * mm});
            skLineSegment(sketch, "E5609", {"start": v(-223.46, -448.43) * mm, "end": v(-223.97, -448.15) * mm});
            skLineSegment(sketch, "E5610", {"start": v(-223.97, -448.15) * mm, "end": v(-224.52, -447.9) * mm});
            skLineSegment(sketch, "E5611", {"start": v(-224.52, -447.9) * mm, "end": v(-225.1, -447.7) * mm});
            skLineSegment(sketch, "E5612", {"start": v(-225.1, -447.7) * mm, "end": v(-225.72, -447.55) * mm});
            skLineSegment(sketch, "E5613", {"start": v(-225.72, -447.55) * mm, "end": v(-226.38, -447.44) * mm});
            skLineSegment(sketch, "E5614", {"start": v(-226.38, -447.44) * mm, "end": v(-227.07, -447.37) * mm});
            skLineSegment(sketch, "E5615", {"start": v(-227.07, -447.37) * mm, "end": v(-227.8, -447.34) * mm});
            skLineSegment(sketch, "E5616", {"start": v(-227.8, -447.34) * mm, "end": v(-228.52, -447.37) * mm});
            skLineSegment(sketch, "E5617", {"start": v(-228.52, -447.37) * mm, "end": v(-229.2, -447.44) * mm});
            skLineSegment(sketch, "E5618", {"start": v(-229.2, -447.44) * mm, "end": v(-229.87, -447.55) * mm});
            skLineSegment(sketch, "E5619", {"start": v(-229.87, -447.55) * mm, "end": v(-230.5, -447.7) * mm});
            skLineSegment(sketch, "E5620", {"start": v(-230.5, -447.7) * mm, "end": v(-231.08, -447.9) * mm});
            skLineSegment(sketch, "E5621", {"start": v(-231.08, -447.9) * mm, "end": v(-231.63, -448.14) * mm});
            skLineSegment(sketch, "E5622", {"start": v(-231.63, -448.14) * mm, "end": v(-232.13, -448.42) * mm});
            skLineSegment(sketch, "E5623", {"start": v(-232.13, -448.42) * mm, "end": v(-232.6, -448.73) * mm});
            skLineSegment(sketch, "E5624", {"start": v(-232.6, -448.73) * mm, "end": v(-233, -449.08) * mm});
            skLineSegment(sketch, "E5625", {"start": v(-233, -449.08) * mm, "end": v(-233.38, -449.46) * mm});
            skLineSegment(sketch, "E5626", {"start": v(-233.38, -449.46) * mm, "end": v(-233.7, -449.87) * mm});
            skLineSegment(sketch, "E5627", {"start": v(-233.7, -449.87) * mm, "end": v(-233.83, -450.09) * mm});
            skLineSegment(sketch, "E5628", {"start": v(-233.83, -450.09) * mm, "end": v(-233.96, -450.3) * mm});
            skLineSegment(sketch, "E5629", {"start": v(-233.96, -450.3) * mm, "end": v(-234.07, -450.54) * mm});
            skLineSegment(sketch, "E5630", {"start": v(-234.07, -450.54) * mm, "end": v(-234.17, -450.78) * mm});
            skLineSegment(sketch, "E5631", {"start": v(-234.17, -450.78) * mm, "end": v(-234.25, -451.02) * mm});
            skLineSegment(sketch, "E5632", {"start": v(-234.25, -451.02) * mm, "end": v(-234.32, -451.27) * mm});
            skLineSegment(sketch, "E5633", {"start": v(-234.32, -451.27) * mm, "end": v(-234.38, -451.53) * mm});
            skLineSegment(sketch, "E5634", {"start": v(-234.38, -451.53) * mm, "end": v(-234.42, -451.8) * mm});
            skLineSegment(sketch, "E5635", {"start": v(-234.42, -451.8) * mm, "end": v(-234.44, -452.06) * mm});
            skLineSegment(sketch, "E5636", {"start": v(-234.44, -452.06) * mm, "end": v(-234.45, -452.34) * mm});
            skLineSegment(sketch, "E5637", {"start": v(-234.45, -452.34) * mm, "end": v(-234.43, -452.76) * mm});
            skLineSegment(sketch, "E5638", {"start": v(-234.43, -452.76) * mm, "end": v(-234.37, -453.15) * mm});
            skLineSegment(sketch, "E5639", {"start": v(-234.37, -453.15) * mm, "end": v(-234.27, -453.53) * mm});
            skLineSegment(sketch, "E5640", {"start": v(-234.27, -453.53) * mm, "end": v(-234.12, -453.9) * mm});
            skLineSegment(sketch, "E5641", {"start": v(-234.12, -453.9) * mm, "end": v(-233.93, -454.23) * mm});
            skLineSegment(sketch, "E5642", {"start": v(-233.93, -454.23) * mm, "end": v(-233.7, -454.56) * mm});
            skLineSegment(sketch, "E5643", {"start": v(-233.7, -454.56) * mm, "end": v(-233.42, -454.86) * mm});
            skLineSegment(sketch, "E5644", {"start": v(-233.42, -454.86) * mm, "end": v(-233.1, -455.16) * mm});
            skLineSegment(sketch, "E5645", {"start": v(-233.1, -455.16) * mm, "end": v(-232.72, -455.43) * mm});
            skLineSegment(sketch, "E5646", {"start": v(-232.72, -455.43) * mm, "end": v(-232.3, -455.7) * mm});
            skLineSegment(sketch, "E5647", {"start": v(-232.3, -455.7) * mm, "end": v(-231.82, -455.95) * mm});
            skLineSegment(sketch, "E5648", {"start": v(-231.82, -455.95) * mm, "end": v(-231.3, -456.2) * mm});
            skLineSegment(sketch, "E5649", {"start": v(-231.3, -456.2) * mm, "end": v(-230.72, -456.42) * mm});
            skLineSegment(sketch, "E5650", {"start": v(-230.72, -456.42) * mm, "end": v(-230.09, -456.64) * mm});
            skLineSegment(sketch, "E5651", {"start": v(-230.09, -456.64) * mm, "end": v(-229.4, -456.85) * mm});
            skLineSegment(sketch, "E5652", {"start": v(-229.4, -456.85) * mm, "end": v(-228.66, -457.06) * mm});
            skLineSegment(sketch, "E5653", {"start": v(-228.66, -457.06) * mm, "end": v(-225.49, -457.9) * mm});
            skLineSegment(sketch, "E5654", {"start": v(-225.49, -457.9) * mm, "end": v(-224.36, -458.2) * mm});
            skLineSegment(sketch, "E5655", {"start": v(-224.36, -458.2) * mm, "end": v(-223.3, -458.53) * mm});
            skLineSegment(sketch, "E5656", {"start": v(-223.3, -458.53) * mm, "end": v(-222.35, -458.88) * mm});
            skLineSegment(sketch, "E5657", {"start": v(-222.35, -458.88) * mm, "end": v(-221.47, -459.25) * mm});
            skLineSegment(sketch, "E5658", {"start": v(-221.47, -459.25) * mm, "end": v(-220.67, -459.65) * mm});
            skLineSegment(sketch, "E5659", {"start": v(-220.67, -459.65) * mm, "end": v(-220.3, -459.86) * mm});
            skLineSegment(sketch, "E5660", {"start": v(-220.3, -459.86) * mm, "end": v(-219.94, -460.08) * mm});
            skLineSegment(sketch, "E5661", {"start": v(-219.94, -460.08) * mm, "end": v(-219.61, -460.3) * mm});
            skLineSegment(sketch, "E5662", {"start": v(-219.61, -460.3) * mm, "end": v(-219.3, -460.54) * mm});
            skLineSegment(sketch, "E5663", {"start": v(-219.3, -460.54) * mm, "end": v(-219, -460.78) * mm});
            skLineSegment(sketch, "E5664", {"start": v(-219, -460.78) * mm, "end": v(-218.73, -461.02) * mm});
            skLineSegment(sketch, "E5665", {"start": v(-218.73, -461.02) * mm, "end": v(-218.47, -461.28) * mm});
            skLineSegment(sketch, "E5666", {"start": v(-218.47, -461.28) * mm, "end": v(-218.24, -461.54) * mm});
            skLineSegment(sketch, "E5667", {"start": v(-218.24, -461.54) * mm, "end": v(-218.01, -461.82) * mm});
            skLineSegment(sketch, "E5668", {"start": v(-218.01, -461.82) * mm, "end": v(-217.81, -462.1) * mm});
            skLineSegment(sketch, "E5669", {"start": v(-217.81, -462.1) * mm, "end": v(-217.63, -462.39) * mm});
            skLineSegment(sketch, "E5670", {"start": v(-217.63, -462.39) * mm, "end": v(-217.46, -462.69) * mm});
            skLineSegment(sketch, "E5671", {"start": v(-217.46, -462.69) * mm, "end": v(-217.3, -463) * mm});
            skLineSegment(sketch, "E5672", {"start": v(-217.3, -463) * mm, "end": v(-217.17, -463.31) * mm});
            skLineSegment(sketch, "E5673", {"start": v(-217.17, -463.31) * mm, "end": v(-217.05, -463.64) * mm});
            skLineSegment(sketch, "E5674", {"start": v(-217.05, -463.64) * mm, "end": v(-216.95, -463.98) * mm});
            skLineSegment(sketch, "E5675", {"start": v(-216.95, -463.98) * mm, "end": v(-216.87, -464.33) * mm});
            skLineSegment(sketch, "E5676", {"start": v(-216.87, -464.33) * mm, "end": v(-216.8, -464.69) * mm});
            skLineSegment(sketch, "E5677", {"start": v(-216.8, -464.69) * mm, "end": v(-216.75, -465.05) * mm});
            skLineSegment(sketch, "E5678", {"start": v(-216.75, -465.05) * mm, "end": v(-216.7, -465.43) * mm});
            skLineSegment(sketch, "E5679", {"start": v(-216.7, -465.43) * mm, "end": v(-216.69, -465.82) * mm});
            skLineSegment(sketch, "E5680", {"start": v(-216.69, -465.82) * mm, "end": v(-216.68, -466.23) * mm});
            skLineSegment(sketch, "E5681", {"start": v(-216.68, -466.23) * mm, "end": v(-216.7, -466.74) * mm});
            skLineSegment(sketch, "E5682", {"start": v(-216.7, -466.74) * mm, "end": v(-216.73, -467.24) * mm});
            skLineSegment(sketch, "E5683", {"start": v(-216.73, -467.24) * mm, "end": v(-216.8, -467.73) * mm});
            skLineSegment(sketch, "E5684", {"start": v(-216.8, -467.73) * mm, "end": v(-216.88, -468.2) * mm});
            skLineSegment(sketch, "E5685", {"start": v(-216.88, -468.2) * mm, "end": v(-217, -468.66) * mm});
            skLineSegment(sketch, "E5686", {"start": v(-217, -468.66) * mm, "end": v(-217.13, -469.11) * mm});
            skLineSegment(sketch, "E5687", {"start": v(-217.13, -469.11) * mm, "end": v(-217.29, -469.55) * mm});
            skLineSegment(sketch, "E5688", {"start": v(-217.29, -469.55) * mm, "end": v(-217.47, -469.97) * mm});
            skLineSegment(sketch, "E5689", {"start": v(-217.47, -469.97) * mm, "end": v(-217.67, -470.38) * mm});
            skLineSegment(sketch, "E5690", {"start": v(-217.67, -470.38) * mm, "end": v(-217.9, -470.77) * mm});
            skLineSegment(sketch, "E5691", {"start": v(-217.9, -470.77) * mm, "end": v(-218.15, -471.14) * mm});
            skLineSegment(sketch, "E5692", {"start": v(-218.15, -471.14) * mm, "end": v(-218.43, -471.5) * mm});
            skLineSegment(sketch, "E5693", {"start": v(-218.43, -471.5) * mm, "end": v(-218.72, -471.86) * mm});
            skLineSegment(sketch, "E5694", {"start": v(-218.72, -471.86) * mm, "end": v(-219.04, -472.19) * mm});
            skLineSegment(sketch, "E5695", {"start": v(-219.04, -472.19) * mm, "end": v(-219.37, -472.5) * mm});
            skLineSegment(sketch, "E5696", {"start": v(-219.37, -472.5) * mm, "end": v(-219.73, -472.8) * mm});
            skLineSegment(sketch, "E5697", {"start": v(-219.73, -472.8) * mm, "end": v(-220.1, -473.09) * mm});
            skLineSegment(sketch, "E5698", {"start": v(-220.1, -473.09) * mm, "end": v(-220.5, -473.36) * mm});
            skLineSegment(sketch, "E5699", {"start": v(-220.5, -473.36) * mm, "end": v(-220.92, -473.6) * mm});
            skLineSegment(sketch, "E5700", {"start": v(-220.92, -473.6) * mm, "end": v(-221.36, -473.84) * mm});
            skLineSegment(sketch, "E5701", {"start": v(-221.36, -473.84) * mm, "end": v(-221.82, -474.06) * mm});
            skLineSegment(sketch, "E5702", {"start": v(-221.82, -474.06) * mm, "end": v(-222.3, -474.26) * mm});
            skLineSegment(sketch, "E5703", {"start": v(-222.3, -474.26) * mm, "end": v(-222.79, -474.44) * mm});
            skLineSegment(sketch, "E5704", {"start": v(-222.79, -474.44) * mm, "end": v(-223.3, -474.6) * mm});
            skLineSegment(sketch, "E5705", {"start": v(-223.3, -474.6) * mm, "end": v(-223.83, -474.75) * mm});
            skLineSegment(sketch, "E5706", {"start": v(-223.83, -474.75) * mm, "end": v(-224.37, -474.87) * mm});
            skLineSegment(sketch, "E5707", {"start": v(-224.37, -474.87) * mm, "end": v(-224.94, -474.98) * mm});
            skLineSegment(sketch, "E5708", {"start": v(-224.94, -474.98) * mm, "end": v(-225.52, -475.07) * mm});
            skLineSegment(sketch, "E5709", {"start": v(-225.52, -475.07) * mm, "end": v(-226.12, -475.14) * mm});
            skLineSegment(sketch, "E5710", {"start": v(-226.12, -475.14) * mm, "end": v(-226.73, -475.19) * mm});
            skLineSegment(sketch, "E5711", {"start": v(-226.73, -475.19) * mm, "end": v(-227.36, -475.22) * mm});
            skLineSegment(sketch, "E5712", {"start": v(-227.36, -475.22) * mm, "end": v(-228, -475.23) * mm});
            skLineSegment(sketch, "E5713", {"start": v(-228, -475.23) * mm, "end": v(-228.6, -475.22) * mm});
            skLineSegment(sketch, "E5714", {"start": v(-228.6, -475.22) * mm, "end": v(-229.19, -475.19) * mm});
            skLineSegment(sketch, "E5715", {"start": v(-229.19, -475.19) * mm, "end": v(-229.76, -475.14) * mm});
            skLineSegment(sketch, "E5716", {"start": v(-229.76, -475.14) * mm, "end": v(-230.32, -475.07) * mm});
            skLineSegment(sketch, "E5717", {"start": v(-230.32, -475.07) * mm, "end": v(-230.86, -474.98) * mm});
            skLineSegment(sketch, "E5718", {"start": v(-230.86, -474.98) * mm, "end": v(-231.4, -474.87) * mm});
            skLineSegment(sketch, "E5719", {"start": v(-231.4, -474.87) * mm, "end": v(-231.91, -474.75) * mm});
            skLineSegment(sketch, "E5720", {"start": v(-231.91, -474.75) * mm, "end": v(-232.42, -474.6) * mm});
            skLineSegment(sketch, "E5721", {"start": v(-232.42, -474.6) * mm, "end": v(-232.9, -474.44) * mm});
            skLineSegment(sketch, "E5722", {"start": v(-232.9, -474.44) * mm, "end": v(-233.38, -474.26) * mm});
            skLineSegment(sketch, "E5723", {"start": v(-233.38, -474.26) * mm, "end": v(-233.84, -474.06) * mm});
            skLineSegment(sketch, "E5724", {"start": v(-233.84, -474.06) * mm, "end": v(-234.28, -473.84) * mm});
            skLineSegment(sketch, "E5725", {"start": v(-234.28, -473.84) * mm, "end": v(-234.71, -473.61) * mm});
            skLineSegment(sketch, "E5726", {"start": v(-234.71, -473.61) * mm, "end": v(-235.12, -473.36) * mm});
            skLineSegment(sketch, "E5727", {"start": v(-235.12, -473.36) * mm, "end": v(-235.52, -473.1) * mm});
            skLineSegment(sketch, "E5728", {"start": v(-235.52, -473.1) * mm, "end": v(-235.9, -472.82) * mm});
            skLineSegment(sketch, "E5729", {"start": v(-235.9, -472.82) * mm, "end": v(-236.25, -472.52) * mm});
            skLineSegment(sketch, "E5730", {"start": v(-236.25, -472.52) * mm, "end": v(-236.6, -472.2) * mm});
            skLineSegment(sketch, "E5731", {"start": v(-236.6, -472.2) * mm, "end": v(-236.91, -471.88) * mm});
            skLineSegment(sketch, "E5732", {"start": v(-236.91, -471.88) * mm, "end": v(-237.21, -471.54) * mm});
            skLineSegment(sketch, "E5733", {"start": v(-237.21, -471.54) * mm, "end": v(-237.5, -471.18) * mm});
            skLineSegment(sketch, "E5734", {"start": v(-237.5, -471.18) * mm, "end": v(-237.76, -470.81) * mm});
            skLineSegment(sketch, "E5735", {"start": v(-237.76, -470.81) * mm, "end": v(-238, -470.43) * mm});
            skLineSegment(sketch, "E5736", {"start": v(-238, -470.43) * mm, "end": v(-238.23, -470.03) * mm});
            skLineSegment(sketch, "E5737", {"start": v(-238.23, -470.03) * mm, "end": v(-238.43, -469.62) * mm});
            skLineSegment(sketch, "E5738", {"start": v(-238.43, -469.62) * mm, "end": v(-238.61, -469.2) * mm});
            skLineSegment(sketch, "E5739", {"start": v(-238.61, -469.2) * mm, "end": v(-238.77, -468.76) * mm});
            skLineSegment(sketch, "E5740", {"start": v(-238.77, -468.76) * mm, "end": v(-238.9, -468.3) * mm});
            skLineSegment(sketch, "E5741", {"start": v(-238.9, -468.3) * mm, "end": v(-239.02, -467.85) * mm});
            skLineSegment(sketch, "E5742", {"start": v(-239.02, -467.85) * mm, "end": v(-239.12, -467.37) * mm});
            skLineSegment(sketch, "E5743", {"start": v(-239.12, -467.37) * mm, "end": v(-239.18, -466.89) * mm});
            skLineSegment(sketch, "E5744", {"start": v(-239.18, -466.89) * mm, "end": v(-239.23, -466.4) * mm});
            skLineSegment(sketch, "E5745", {"start": v(-239.23, -466.4) * mm, "end": v(-235.43, -466.4) * mm});
            skLineSegment(sketch, "E5746", {"start": v(-30.45, -474.72) * mm, "end": v(-33.97, -474.72) * mm});
            skLineSegment(sketch, "E5747", {"start": v(-33.97, -474.72) * mm, "end": v(-33.97, -451.4) * mm});
            skLineSegment(sketch, "E5748", {"start": v(-33.97, -451.4) * mm, "end": v(-34.12, -451.4) * mm});
            skLineSegment(sketch, "E5749", {"start": v(-34.12, -451.4) * mm, "end": v(-43.77, -474.51) * mm});
            skLineSegment(sketch, "E5750", {"start": v(-43.77, -474.51) * mm, "end": v(-46.96, -474.51) * mm});
            skLineSegment(sketch, "E5751", {"start": v(-46.96, -474.51) * mm, "end": v(-56.6, -451.4) * mm});
            skLineSegment(sketch, "E5752", {"start": v(-56.6, -451.4) * mm, "end": v(-56.75, -451.4) * mm});
            skLineSegment(sketch, "E5753", {"start": v(-56.75, -451.4) * mm, "end": v(-56.75, -474.72) * mm});
            skLineSegment(sketch, "E5754", {"start": v(-56.75, -474.72) * mm, "end": v(-60.28, -474.72) * mm});
            skLineSegment(sketch, "E5755", {"start": v(-60.28, -474.72) * mm, "end": v(-60.28, -444.45) * mm});
            skLineSegment(sketch, "E5756", {"start": v(-60.28, -444.45) * mm, "end": v(-55.9, -444.45) * mm});
            skLineSegment(sketch, "E5757", {"start": v(-55.9, -444.45) * mm, "end": v(-45.45, -469.7) * mm});
            skLineSegment(sketch, "E5758", {"start": v(-45.45, -469.7) * mm, "end": v(-45.28, -469.7) * mm});
            skLineSegment(sketch, "E5759", {"start": v(-45.28, -469.7) * mm, "end": v(-34.83, -444.45) * mm});
            skLineSegment(sketch, "E5760", {"start": v(-34.83, -444.45) * mm, "end": v(-30.45, -444.45) * mm});
            skLineSegment(sketch, "E5761", {"start": v(-30.45, -444.45) * mm, "end": v(-30.45, -474.72) * mm});
            skLineSegment(sketch, "E5762", {"start": v(52.15, -449.05) * mm, "end": v(52.27, -449.05) * mm});
            skLineSegment(sketch, "E5763", {"start": v(52.27, -449.05) * mm, "end": v(57.12, -462.85) * mm});
            skLineSegment(sketch, "E5764", {"start": v(57.12, -462.85) * mm, "end": v(47.3, -462.85) * mm});
            skLineSegment(sketch, "E5765", {"start": v(47.3, -462.85) * mm, "end": v(52.15, -449.05) * mm});
            skLineSegment(sketch, "E5766", {"start": v(58.23, -466.06) * mm, "end": v(46.19, -466.06) * mm});
            skLineSegment(sketch, "E5767", {"start": v(46.19, -466.06) * mm, "end": v(43.15, -474.72) * mm});
            skLineSegment(sketch, "E5768", {"start": v(43.15, -474.72) * mm, "end": v(39.18, -474.72) * mm});
            skLineSegment(sketch, "E5769", {"start": v(39.18, -474.72) * mm, "end": v(50.34, -444.45) * mm});
            skLineSegment(sketch, "E5770", {"start": v(50.34, -444.45) * mm, "end": v(54.08, -444.45) * mm});
            skLineSegment(sketch, "E5771", {"start": v(54.08, -444.45) * mm, "end": v(65.24, -474.72) * mm});
            skLineSegment(sketch, "E5772", {"start": v(65.24, -474.72) * mm, "end": v(61.27, -474.72) * mm});
            skLineSegment(sketch, "E5773", {"start": v(61.27, -474.72) * mm, "end": v(58.23, -466.06) * mm});
            skLineSegment(sketch, "E5774", {"start": v(134.87, -474.72) * mm, "end": v(134.87, -444.45) * mm});
            skLineSegment(sketch, "E5775", {"start": v(134.87, -444.45) * mm, "end": v(138.64, -444.45) * mm});
            skLineSegment(sketch, "E5776", {"start": v(138.64, -444.45) * mm, "end": v(138.64, -459.22) * mm});
            skLineSegment(sketch, "E5777", {"start": v(138.64, -459.22) * mm, "end": v(138.85, -459.22) * mm});
            skLineSegment(sketch, "E5778", {"start": v(138.85, -459.22) * mm, "end": v(152.22, -444.45) * mm});
            skLineSegment(sketch, "E5779", {"start": v(152.22, -444.45) * mm, "end": v(156.98, -444.45) * mm});
            skLineSegment(sketch, "E5780", {"start": v(156.98, -444.45) * mm, "end": v(144.54, -457.86) * mm});
            skLineSegment(sketch, "E5781", {"start": v(144.54, -457.86) * mm, "end": v(158.1, -474.72) * mm});
            skLineSegment(sketch, "E5782", {"start": v(158.1, -474.72) * mm, "end": v(153.27, -474.72) * mm});
            skLineSegment(sketch, "E5783", {"start": v(153.27, -474.72) * mm, "end": v(141.92, -460.54) * mm});
            skLineSegment(sketch, "E5784", {"start": v(141.92, -460.54) * mm, "end": v(138.64, -464.15) * mm});
            skLineSegment(sketch, "E5785", {"start": v(138.64, -464.15) * mm, "end": v(138.64, -474.72) * mm});
            skLineSegment(sketch, "E5786", {"start": v(138.64, -474.72) * mm, "end": v(134.87, -474.72) * mm});
            skLineSegment(sketch, "E5787", {"start": v(246.22, -474.72) * mm, "end": v(227.47, -474.72) * mm});
            skLineSegment(sketch, "E5788", {"start": v(227.47, -474.72) * mm, "end": v(227.47, -444.45) * mm});
            skLineSegment(sketch, "E5789", {"start": v(227.47, -444.45) * mm, "end": v(246.22, -444.45) * mm});
            skLineSegment(sketch, "E5790", {"start": v(246.22, -444.45) * mm, "end": v(246.22, -447.85) * mm});
            skLineSegment(sketch, "E5791", {"start": v(246.22, -447.85) * mm, "end": v(231.25, -447.85) * mm});
            skLineSegment(sketch, "E5792", {"start": v(231.25, -447.85) * mm, "end": v(231.25, -457.56) * mm});
            skLineSegment(sketch, "E5793", {"start": v(231.25, -457.56) * mm, "end": v(245.45, -457.56) * mm});
            skLineSegment(sketch, "E5794", {"start": v(245.45, -457.56) * mm, "end": v(245.45, -460.92) * mm});
            skLineSegment(sketch, "E5795", {"start": v(245.45, -460.92) * mm, "end": v(231.25, -460.92) * mm});
            skLineSegment(sketch, "E5796", {"start": v(231.25, -460.92) * mm, "end": v(231.25, -471.33) * mm});
            skLineSegment(sketch, "E5797", {"start": v(231.25, -471.33) * mm, "end": v(246.22, -471.33) * mm});
            skLineSegment(sketch, "E5798", {"start": v(246.22, -471.33) * mm, "end": v(246.22, -474.72) * mm});
            skLineSegment(sketch, "E5799", {"start": v(403.2, -444.45) * mm, "end": v(406.97, -444.45) * mm});
            skLineSegment(sketch, "E5800", {"start": v(406.97, -444.45) * mm, "end": v(406.97, -474.72) * mm});
            skLineSegment(sketch, "E5801", {"start": v(406.97, -474.72) * mm, "end": v(403.2, -474.72) * mm});
            skLineSegment(sketch, "E5802", {"start": v(403.2, -474.72) * mm, "end": v(403.2, -444.45) * mm});
            skLineSegment(sketch, "E5803", {"start": v(486.88, -474.72) * mm, "end": v(486.88, -447.85) * mm});
            skLineSegment(sketch, "E5804", {"start": v(486.88, -447.85) * mm, "end": v(477.12, -447.85) * mm});
            skLineSegment(sketch, "E5805", {"start": v(477.12, -447.85) * mm, "end": v(477.12, -444.45) * mm});
            skLineSegment(sketch, "E5806", {"start": v(477.12, -444.45) * mm, "end": v(500.4, -444.45) * mm});
            skLineSegment(sketch, "E5807", {"start": v(500.4, -444.45) * mm, "end": v(500.4, -447.85) * mm});
            skLineSegment(sketch, "E5808", {"start": v(500.4, -447.85) * mm, "end": v(490.65, -447.85) * mm});
            skLineSegment(sketch, "E5809", {"start": v(490.65, -447.85) * mm, "end": v(490.65, -474.72) * mm});
            skLineSegment(sketch, "E5810", {"start": v(490.65, -474.72) * mm, "end": v(486.88, -474.72) * mm});
            skLineSegment(sketch, "E5811", {"start": v(550, -511.99) * mm, "end": v(550, -316.99) * mm});
            skSolve(sketch);
        }
        {
            var Q0;
            Q0=makeQuery(id+"F0.imprint","IMPRINT",FACE,{"disambiguationData":[TD([[makeQuery(id+"F0.imprint","IMPRINT",EDGE,{"derivedFrom":sQuery(id+"F0.wireOp",EDGE,"E3")}),-1.0]])]});
            var Q1;
            Q1=makeQuery(id+"F0.imprint","IMPRINT",FACE,{"disambiguationData":[TD([[makeQuery(id+"F0.imprint","IMPRINT",EDGE,{"derivedFrom":sQuery(id+"F0.wireOp",EDGE,"E3")}),1.0]])]});
            var Q2;
            Q2=makeQuery(id+"F0.imprint","IMPRINT",FACE,{"disambiguationData":[TD([[makeQuery(id+"F0.imprint","IMPRINT",EDGE,{"derivedFrom":sQuery(id+"F0.wireOp",EDGE,"E117")}),-1.0]])]});
            var Q3;
            Q3=makeQuery(id+"F0.imprint","IMPRINT",FACE,{"disambiguationData":[TD([[makeQuery(id+"F0.imprint","IMPRINT",EDGE,{"derivedFrom":sQuery(id+"F0.wireOp",EDGE,"E54")}),-1.0]])]});
            extrude(context, id + "F1", {"entities" : qUnion([Q0, Q1, Q2, Q3]), "endBound" : BoundingType.SYMMETRIC, "oppositeDirection" : true, "depth" : 20 * mm, "offsetDistance" : 25 * mm});
        }
        {
            var Q0;
            Q0=makeQuery(id+"F0.imprint","IMPRINT",FACE,{"disambiguationData":[TD([[makeQuery(id+"F0.imprint","IMPRINT",EDGE,{"derivedFrom":sQuery(id+"F0.wireOp",EDGE,"E201")}),1.0]])]});
            extrude(context, id + "F2", {"entities" : qUnion([Q0]), "oppositeDirection" : true, "depth" : 6 * mm, "offsetDistance" : 25 * mm});
        }
        {
            var Q0;
            Q0=makeQuery(id+"F0.imprint","IMPRINT",FACE,{"disambiguationData":[TD([[makeQuery(id+"F0.imprint","IMPRINT",EDGE,{"derivedFrom":sQuery(id+"F0.wireOp",EDGE,"E1731")}),1.0]])]});
            var Q1;
            Q1=makeQuery(id+"F0.imprint","IMPRINT",FACE,{"disambiguationData":[TD([[makeQuery(id+"F0.imprint","IMPRINT",EDGE,{"derivedFrom":sQuery(id+"F0.wireOp",EDGE,"E2537")}),1.0]])]});
            var Q2;
            Q2=makeQuery(id+"F0.imprint","IMPRINT",FACE,{"disambiguationData":[TD([[makeQuery(id+"F0.imprint","IMPRINT",EDGE,{"derivedFrom":sQuery(id+"F0.wireOp",EDGE,"E2921")}),1.0]])]});
            extrude(context, id + "F3", {"entities" : qUnion([Q0, Q1, Q2]), "oppositeDirection" : true, "depth" : 6 * mm, "offsetDistance" : 25 * mm});
        }
        {
            var Q0;
            Q0=makeQuery(id+"F0.imprint","IMPRINT",FACE,{"disambiguationData":[TD([[makeQuery(id+"F0.imprint","IMPRINT",EDGE,{"derivedFrom":sQuery(id+"F0.wireOp",EDGE,"E123")}),-1.0]])]});
            var Q1;
            Q1=makeQuery(id+"F0.imprint","IMPRINT",FACE,{"disambiguationData":[TD([[makeQuery(id+"F0.imprint","IMPRINT",EDGE,{"derivedFrom":sQuery(id+"F0.wireOp",EDGE,"E197")}),-1.0]])]});
            var Q2;
            Q2=makeQuery(id+"F0.imprint","IMPRINT",FACE,{"disambiguationData":[TD([[makeQuery(id+"F0.imprint","IMPRINT",EDGE,{"derivedFrom":sQuery(id+"F0.wireOp",EDGE,"E5236")}),-1.0]])]});
            var Q3;
            Q3=makeQuery(id+"F0.imprint","IMPRINT",FACE,{"disambiguationData":[TD([[makeQuery(id+"F0.imprint","IMPRINT",EDGE,{"derivedFrom":sQuery(id+"F0.wireOp",EDGE,"E5248")}),-1.0]])]});
            var Q4;
            Q4=makeQuery(id+"F0.imprint","IMPRINT",FACE,{"disambiguationData":[TD([[makeQuery(id+"F0.imprint","IMPRINT",EDGE,{"derivedFrom":sQuery(id+"F0.wireOp",EDGE,"E4966")}),-1.0]])]});
            var Q5;
            Q5=makeQuery(id+"F0.imprint","IMPRINT",FACE,{"disambiguationData":[TD([[makeQuery(id+"F0.imprint","IMPRINT",EDGE,{"derivedFrom":sQuery(id+"F0.wireOp",EDGE,"E4485")}),-1.0]])]});
            var Q6;
            Q6=makeQuery(id+"F0.imprint","IMPRINT",FACE,{"disambiguationData":[TD([[makeQuery(id+"F0.imprint","IMPRINT",EDGE,{"derivedFrom":sQuery(id+"F0.wireOp",EDGE,"E4448")}),-1.0]])]});
            var Q7;
            Q7=makeQuery(id+"F0.imprint","IMPRINT",FACE,{"disambiguationData":[TD([[makeQuery(id+"F0.imprint","IMPRINT",EDGE,{"derivedFrom":sQuery(id+"F0.wireOp",EDGE,"E5762")}),-1.0]])]});
            var Q8;
            Q8=makeQuery(id+"F0.imprint","IMPRINT",FACE,{"disambiguationData":[TD([[makeQuery(id+"F0.imprint","IMPRINT",EDGE,{"derivedFrom":sQuery(id+"F0.wireOp",EDGE,"E4176")}),-1.0]])]});
            var Q9;
            Q9=makeQuery(id+"F0.imprint","IMPRINT",FACE,{"disambiguationData":[TD([[makeQuery(id+"F0.imprint","IMPRINT",EDGE,{"derivedFrom":sQuery(id+"F0.wireOp",EDGE,"E2991")}),1.0]])]});
            var Q10;
            Q10=makeQuery(id+"F0.imprint","IMPRINT",FACE,{"disambiguationData":[TD([[makeQuery(id+"F0.imprint","IMPRINT",EDGE,{"derivedFrom":sQuery(id+"F0.wireOp",EDGE,"E2665")}),-1.0]])]});
            var Q11;
            Q11=makeQuery(id+"F0.imprint","IMPRINT",FACE,{"disambiguationData":[TD([[makeQuery(id+"F0.imprint","IMPRINT",EDGE,{"derivedFrom":sQuery(id+"F0.wireOp",EDGE,"E3517")}),-1.0]])]});
            var Q12;
            Q12=makeQuery(id+"F0.imprint","IMPRINT",FACE,{"disambiguationData":[TD([[makeQuery(id+"F0.imprint","IMPRINT",EDGE,{"derivedFrom":sQuery(id+"F0.wireOp",EDGE,"E969")}),-1.0]])]});
            var Q13;
            Q13=makeQuery(id+"F0.imprint","IMPRINT",FACE,{"disambiguationData":[TD([[makeQuery(id+"F0.imprint","IMPRINT",EDGE,{"derivedFrom":sQuery(id+"F0.wireOp",EDGE,"E201")}),-1.0]])]});
            var Q14;
            Q14=makeQuery(id+"F0.imprint","IMPRINT",FACE,{"disambiguationData":[TD([[makeQuery(id+"F0.imprint","IMPRINT",EDGE,{"derivedFrom":sQuery(id+"F0.wireOp",EDGE,"E457")}),-1.0]])]});
            var Q15;
            Q15=makeQuery(id+"F0.imprint","IMPRINT",FACE,{"disambiguationData":[TD([[makeQuery(id+"F0.imprint","IMPRINT",EDGE,{"derivedFrom":sQuery(id+"F0.wireOp",EDGE,"E713")}),-1.0]])]});
            var Q16;
            Q16=makeQuery(id+"F0.imprint","IMPRINT",FACE,{"disambiguationData":[TD([[makeQuery(id+"F0.imprint","IMPRINT",EDGE,{"derivedFrom":sQuery(id+"F0.wireOp",EDGE,"E0")}),1.0]])]});
            extrude(context, id + "F4", {"entities" : qUnion([Q0, Q1, Q2, Q3, Q4, Q5, Q6, Q7, Q8, Q9, Q10, Q11, Q12, Q13, Q14, Q15, Q16]), "endBound" : BoundingType.SYMMETRIC, "oppositeDirection" : true, "depth" : 3 * mm, "offsetDistance" : 25 * mm});
        }
        {
            var Q0;
            Q0=makeQuery(id+"F0.imprint","IMPRINT",FACE,{"disambiguationData":[TD([[makeQuery(id+"F0.imprint","IMPRINT",EDGE,{"derivedFrom":sQuery(id+"F0.wireOp",EDGE,"E5248")}),1.0]])]});
            var Q1;
            Q1=makeQuery(id+"F0.imprint","IMPRINT",FACE,{"disambiguationData":[TD([[makeQuery(id+"F0.imprint","IMPRINT",EDGE,{"derivedFrom":sQuery(id+"F0.wireOp",EDGE,"E5382")}),-1.0]])]});
            var Q2;
            Q2=makeQuery(id+"F0.imprint","IMPRINT",FACE,{"disambiguationData":[TD([[makeQuery(id+"F0.imprint","IMPRINT",EDGE,{"derivedFrom":sQuery(id+"F0.wireOp",EDGE,"E5394")}),-1.0]])]});
            var Q3;
            Q3=makeQuery(id+"F0.imprint","IMPRINT",FACE,{"disambiguationData":[TD([[makeQuery(id+"F0.imprint","IMPRINT",EDGE,{"derivedFrom":sQuery(id+"F0.wireOp",EDGE,"E5410")}),-1.0]])]});
            var Q4;
            Q4=makeQuery(id+"F0.imprint","IMPRINT",FACE,{"disambiguationData":[TD([[makeQuery(id+"F0.imprint","IMPRINT",EDGE,{"derivedFrom":sQuery(id+"F0.wireOp",EDGE,"E5803")}),-1.0]])]});
            var Q5;
            Q5=makeQuery(id+"F0.imprint","IMPRINT",FACE,{"disambiguationData":[TD([[makeQuery(id+"F0.imprint","IMPRINT",EDGE,{"derivedFrom":sQuery(id+"F0.wireOp",EDGE,"E5799")}),-1.0]])]});
            var Q6;
            Q6=makeQuery(id+"F0.imprint","IMPRINT",FACE,{"disambiguationData":[TD([[makeQuery(id+"F0.imprint","IMPRINT",EDGE,{"derivedFrom":sQuery(id+"F0.wireOp",EDGE,"E5236")}),1.0]])]});
            var Q7;
            Q7=makeQuery(id+"F0.imprint","IMPRINT",FACE,{"disambiguationData":[TD([[makeQuery(id+"F0.imprint","IMPRINT",EDGE,{"derivedFrom":sQuery(id+"F0.wireOp",EDGE,"E4966")}),1.0]])]});
            var Q8;
            Q8=makeQuery(id+"F0.imprint","IMPRINT",FACE,{"disambiguationData":[TD([[makeQuery(id+"F0.imprint","IMPRINT",EDGE,{"derivedFrom":sQuery(id+"F0.wireOp",EDGE,"E4624")}),-1.0]])]});
            var Q9;
            Q9=makeQuery(id+"F0.imprint","IMPRINT",FACE,{"disambiguationData":[TD([[makeQuery(id+"F0.imprint","IMPRINT",EDGE,{"derivedFrom":sQuery(id+"F0.wireOp",EDGE,"E4485")}),1.0]])]});
            var Q10;
            Q10=makeQuery(id+"F0.imprint","IMPRINT",FACE,{"disambiguationData":[TD([[makeQuery(id+"F0.imprint","IMPRINT",EDGE,{"derivedFrom":sQuery(id+"F0.wireOp",EDGE,"E4473")}),-1.0]])]});
            var Q11;
            Q11=makeQuery(id+"F0.imprint","IMPRINT",FACE,{"disambiguationData":[TD([[makeQuery(id+"F0.imprint","IMPRINT",EDGE,{"derivedFrom":sQuery(id+"F0.wireOp",EDGE,"E4460")}),-1.0]])]});
            var Q12;
            Q12=makeQuery(id+"F0.imprint","IMPRINT",FACE,{"disambiguationData":[TD([[makeQuery(id+"F0.imprint","IMPRINT",EDGE,{"derivedFrom":sQuery(id+"F0.wireOp",EDGE,"E4448")}),1.0]])]});
            var Q13;
            Q13=makeQuery(id+"F0.imprint","IMPRINT",FACE,{"disambiguationData":[TD([[makeQuery(id+"F0.imprint","IMPRINT",EDGE,{"derivedFrom":sQuery(id+"F0.wireOp",EDGE,"E4432")}),-1.0]])]});
            var Q14;
            Q14=makeQuery(id+"F0.imprint","IMPRINT",FACE,{"disambiguationData":[TD([[makeQuery(id+"F0.imprint","IMPRINT",EDGE,{"derivedFrom":sQuery(id+"F0.wireOp",EDGE,"E5420")}),-1.0]])]});
            var Q15;
            Q15=makeQuery(id+"F0.imprint","IMPRINT",FACE,{"disambiguationData":[TD([[makeQuery(id+"F0.imprint","IMPRINT",EDGE,{"derivedFrom":sQuery(id+"F0.wireOp",EDGE,"E5426")}),-1.0]])]});
            var Q16;
            Q16=makeQuery(id+"F0.imprint","IMPRINT",FACE,{"disambiguationData":[TD([[makeQuery(id+"F0.imprint","IMPRINT",EDGE,{"derivedFrom":sQuery(id+"F0.wireOp",EDGE,"E5438")}),-1.0]])]});
            var Q17;
            Q17=makeQuery(id+"F0.imprint","IMPRINT",FACE,{"disambiguationData":[TD([[makeQuery(id+"F0.imprint","IMPRINT",EDGE,{"derivedFrom":sQuery(id+"F0.wireOp",EDGE,"E4978")}),-1.0]])]});
            var Q18;
            Q18=makeQuery(id+"F0.imprint","IMPRINT",FACE,{"disambiguationData":[TD([[makeQuery(id+"F0.imprint","IMPRINT",EDGE,{"derivedFrom":sQuery(id+"F0.wireOp",EDGE,"E5787")}),-1.0]])]});
            var Q19;
            Q19=makeQuery(id+"F0.imprint","IMPRINT",FACE,{"disambiguationData":[TD([[makeQuery(id+"F0.imprint","IMPRINT",EDGE,{"derivedFrom":sQuery(id+"F0.wireOp",EDGE,"E5774")}),-1.0]])]});
            var Q20;
            Q20=makeQuery(id+"F0.imprint","IMPRINT",FACE,{"disambiguationData":[TD([[makeQuery(id+"F0.imprint","IMPRINT",EDGE,{"derivedFrom":sQuery(id+"F0.wireOp",EDGE,"E5762")}),1.0]])]});
            var Q21;
            Q21=makeQuery(id+"F0.imprint","IMPRINT",FACE,{"disambiguationData":[TD([[makeQuery(id+"F0.imprint","IMPRINT",EDGE,{"derivedFrom":sQuery(id+"F0.wireOp",EDGE,"E5746")}),-1.0]])]});
            var Q22;
            Q22=makeQuery(id+"F0.imprint","IMPRINT",FACE,{"disambiguationData":[TD([[makeQuery(id+"F0.imprint","IMPRINT",EDGE,{"derivedFrom":sQuery(id+"F0.wireOp",EDGE,"E5446")}),-1.0]])]});
            extrude(context, id + "F5", {"entities" : qUnion([Q0, Q1, Q2, Q3, Q4, Q5, Q6, Q7, Q8, Q9, Q10, Q11, Q12, Q13, Q14, Q15, Q16, Q17, Q18, Q19, Q20, Q21, Q22]), "depth" : 10 * mm, "offsetDistance" : 25 * mm});
        }
        {
            var Q0;
            Q0=makeQuery(id+"F0.imprint","IMPRINT",FACE,{"disambiguationData":[TD([[makeQuery(id+"F0.imprint","IMPRINT",EDGE,{"derivedFrom":sQuery(id+"F0.wireOp",EDGE,"E0")}),-1.0]])]});
            extrude(context, id + "F6", {"entities" : qUnion([Q0]), "oppositeDirection" : true, "depth" : 300 * mm, "offsetDistance" : 25 * mm});
        }
        {
            var Q0;
            Q0=qCreatedBy(makeId("Top.planeOp"),FACE);
            var sketch = newSketch(context, id + "F7", { "sketchPlane" : qUnion([Q0])});
            skLineSegment(sketch, "E5812", {"start": v(-595.06, 150.3) * mm, "end": v(653.53, 150.3) * mm, "construction": true});
            skLineSegment(sketch, "E5813", {"start": v(324.86, 328.93) * mm, "end": v(324.86, -81.91) * mm, "construction": true});
            skLineSegment(sketch, "E5814", {"start": v(0, -81.91) * mm, "end": v(0, 328.93) * mm, "construction": true});
            skLineSegment(sketch, "E5815", {"start": v(0, 328.93) * mm, "end": v(324.86, 328.93) * mm, "construction": true});
            skLineSegment(sketch, "E5816", {"start": v(0, 328.93) * mm, "end": v(-324.86, 328.93) * mm, "construction": true});
            skLineSegment(sketch, "E5817", {"start": v(-324.86, 328.93) * mm, "end": v(-324.86, -78.34) * mm, "construction": true});
            skCircle(sketch, "E5818", {"center": v(-324.86, 150.3) * mm, "radius": 25 * mm});
            skCircle(sketch, "E5819", {"center": v(324.86, 150.3) * mm, "radius": 25 * mm});
            skSolve(sketch);
        }
        {
            var Q0;
            Q0=sQuery(id+"F7.wireOp",EDGE,"E5818");
            var Q1;
            Q1=sQuery(id+"F7.wireOp",EDGE,"E5819");
            extrude(context, id + "F8", {"bodyType" : ToolBodyType.SURFACE, "surfaceEntities" : qUnion([Q0, Q1]), "endBound" : BoundingType.SYMMETRIC, "depth" : 2400 * mm, "offsetDistance" : 25 * mm});
        }
    });
